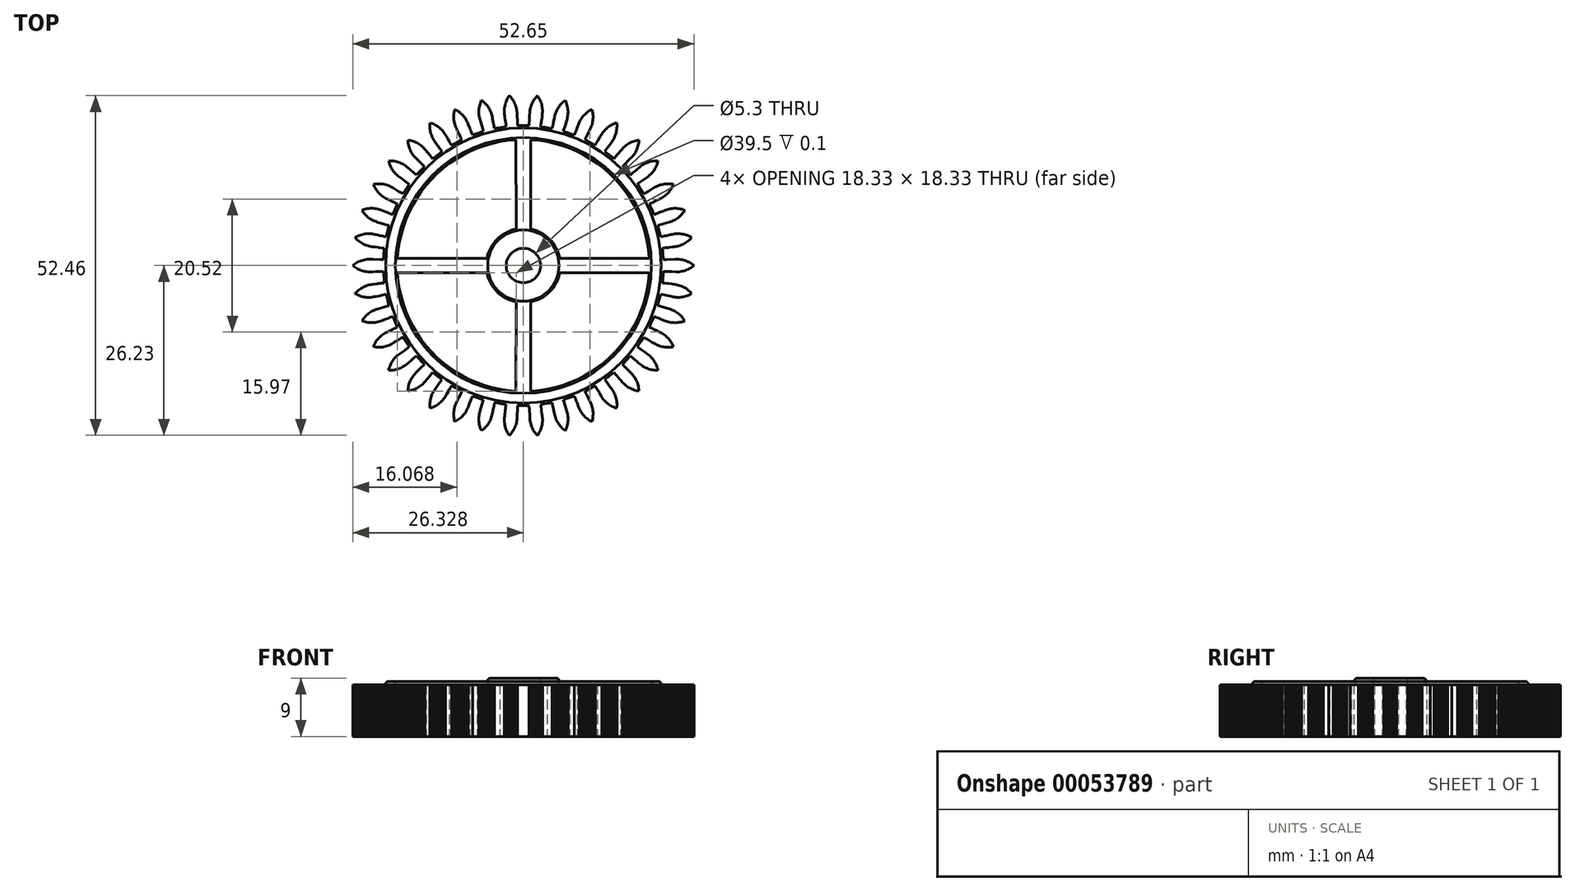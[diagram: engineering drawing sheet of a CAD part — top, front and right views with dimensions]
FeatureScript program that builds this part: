
annotation { "Feature Type Name" : "Feature", "Feature Type Description" : "" }
export const myFeature = defineFeature(function(context is Context, id is Id, definition is map)
    precondition{}
    {
        {
            var Q0;
            Q0=qCreatedBy(makeId("Top.planeOp"),FACE);
            var sketch = newSketch(context, id + "F0", { "sketchPlane" : qUnion([Q0])});
            skLineSegment(sketch, "E0", {"start": v(20.55, -0.9) * mm, "end": v(20.68, -0.9) * mm});
            skLineSegment(sketch, "E1", {"start": v(20.68, -0.9) * mm, "end": v(20.92, -0.9) * mm});
            skLineSegment(sketch, "E2", {"start": v(20.92, -0.9) * mm, "end": v(21.14, -0.92) * mm});
            skLineSegment(sketch, "E3", {"start": v(21.14, -0.92) * mm, "end": v(21.37, -0.93) * mm});
            skLineSegment(sketch, "E4", {"start": v(21.37, -0.93) * mm, "end": v(21.59, -0.94) * mm});
            skLineSegment(sketch, "E5", {"start": v(21.59, -0.94) * mm, "end": v(21.82, -0.95) * mm});
            skLineSegment(sketch, "E6", {"start": v(21.82, -0.95) * mm, "end": v(22.04, -0.96) * mm});
            skLineSegment(sketch, "E7", {"start": v(22.04, -0.96) * mm, "end": v(22.28, -0.96) * mm});
            skLineSegment(sketch, "E8", {"start": v(22.28, -0.96) * mm, "end": v(22.5, -0.97) * mm});
            skLineSegment(sketch, "E9", {"start": v(22.5, -0.97) * mm, "end": v(22.73, -0.97) * mm});
            skLineSegment(sketch, "E10", {"start": v(22.73, -0.97) * mm, "end": v(22.97, -0.96) * mm});
            skLineSegment(sketch, "E11", {"start": v(22.97, -0.96) * mm, "end": v(23.2, -0.94) * mm});
            skLineSegment(sketch, "E12", {"start": v(23.2, -0.94) * mm, "end": v(23.43, -0.9) * mm});
            skLineSegment(sketch, "E13", {"start": v(23.43, -0.9) * mm, "end": v(23.66, -0.84) * mm});
            skLineSegment(sketch, "E14", {"start": v(23.66, -0.84) * mm, "end": v(23.88, -0.78) * mm});
            skLineSegment(sketch, "E15", {"start": v(23.88, -0.78) * mm, "end": v(24.1, -0.7) * mm});
            skLineSegment(sketch, "E16", {"start": v(24.1, -0.7) * mm, "end": v(24.32, -0.6) * mm});
            skLineSegment(sketch, "E17", {"start": v(24.32, -0.6) * mm, "end": v(24.53, -0.5) * mm});
            skLineSegment(sketch, "E18", {"start": v(24.53, -0.5) * mm, "end": v(24.73, -0.39) * mm});
            skLineSegment(sketch, "E19", {"start": v(24.73, -0.39) * mm, "end": v(24.93, -0.26) * mm});
            skLineSegment(sketch, "E20", {"start": v(24.93, -0.26) * mm, "end": v(25.12, -0.13) * mm});
            skLineSegment(sketch, "E21", {"start": v(25.12, -0.13) * mm, "end": v(25.27, 0) * mm});
            skLineSegment(sketch, "E22", {"start": v(25.27, 0) * mm, "end": v(25.09, 0.15) * mm});
            skLineSegment(sketch, "E23", {"start": v(25.09, 0.15) * mm, "end": v(24.9, 0.28) * mm});
            skLineSegment(sketch, "E24", {"start": v(24.9, 0.28) * mm, "end": v(24.7, 0.4) * mm});
            skLineSegment(sketch, "E25", {"start": v(24.7, 0.4) * mm, "end": v(24.5, 0.52) * mm});
            skLineSegment(sketch, "E26", {"start": v(24.5, 0.52) * mm, "end": v(24.29, 0.62) * mm});
            skLineSegment(sketch, "E27", {"start": v(24.29, 0.62) * mm, "end": v(24.07, 0.71) * mm});
            skLineSegment(sketch, "E28", {"start": v(24.07, 0.71) * mm, "end": v(23.85, 0.79) * mm});
            skLineSegment(sketch, "E29", {"start": v(23.85, 0.79) * mm, "end": v(23.62, 0.85) * mm});
            skLineSegment(sketch, "E30", {"start": v(23.62, 0.85) * mm, "end": v(23.4, 0.9) * mm});
            skLineSegment(sketch, "E31", {"start": v(23.4, 0.9) * mm, "end": v(23.17, 0.94) * mm});
            skLineSegment(sketch, "E32", {"start": v(23.17, 0.94) * mm, "end": v(22.93, 0.96) * mm});
            skLineSegment(sketch, "E33", {"start": v(22.93, 0.96) * mm, "end": v(22.7, 0.98) * mm});
            skLineSegment(sketch, "E34", {"start": v(22.7, 0.98) * mm, "end": v(22.6, 0.98) * mm});
            skLineSegment(sketch, "E35", {"start": v(22.6, 0.98) * mm, "end": v(22.37, 0.97) * mm});
            skLineSegment(sketch, "E36", {"start": v(22.37, 0.97) * mm, "end": v(22.13, 0.96) * mm});
            skLineSegment(sketch, "E37", {"start": v(22.13, 0.96) * mm, "end": v(21.91, 0.95) * mm});
            skLineSegment(sketch, "E38", {"start": v(21.91, 0.95) * mm, "end": v(21.68, 0.94) * mm});
            skLineSegment(sketch, "E39", {"start": v(21.68, 0.94) * mm, "end": v(21.46, 0.93) * mm});
            skLineSegment(sketch, "E40", {"start": v(21.46, 0.93) * mm, "end": v(21.23, 0.92) * mm});
            skLineSegment(sketch, "E41", {"start": v(21.23, 0.92) * mm, "end": v(21, 0.91) * mm});
            skLineSegment(sketch, "E42", {"start": v(21, 0.91) * mm, "end": v(20.77, 0.9) * mm});
            skLineSegment(sketch, "E43", {"start": v(20.77, 0.9) * mm, "end": v(20.55, 0.9) * mm});
            skLineSegment(sketch, "E44", {"start": v(20.55, 0.9) * mm, "end": v(20.53, 1.13) * mm});
            skLineSegment(sketch, "E45", {"start": v(20.53, 1.13) * mm, "end": v(20.51, 1.36) * mm});
            skLineSegment(sketch, "E46", {"start": v(20.51, 1.36) * mm, "end": v(20.5, 1.6) * mm});
            skLineSegment(sketch, "E47", {"start": v(20.5, 1.6) * mm, "end": v(20.47, 1.83) * mm});
            skLineSegment(sketch, "E48", {"start": v(20.47, 1.83) * mm, "end": v(20.45, 2.06) * mm});
            skLineSegment(sketch, "E49", {"start": v(20.45, 2.06) * mm, "end": v(20.44, 2.3) * mm});
            skLineSegment(sketch, "E50", {"start": v(20.44, 2.3) * mm, "end": v(20.42, 2.53) * mm});
            skLineSegment(sketch, "E51", {"start": v(20.42, 2.53) * mm, "end": v(20.4, 2.67) * mm});
            skLineSegment(sketch, "E52", {"start": v(20.4, 2.67) * mm, "end": v(20.64, 2.7) * mm});
            skLineSegment(sketch, "E53", {"start": v(20.64, 2.7) * mm, "end": v(20.86, 2.73) * mm});
            skLineSegment(sketch, "E54", {"start": v(20.86, 2.73) * mm, "end": v(21.09, 2.76) * mm});
            skLineSegment(sketch, "E55", {"start": v(21.09, 2.76) * mm, "end": v(21.3, 2.79) * mm});
            skLineSegment(sketch, "E56", {"start": v(21.3, 2.79) * mm, "end": v(21.54, 2.82) * mm});
            skLineSegment(sketch, "E57", {"start": v(21.54, 2.82) * mm, "end": v(21.76, 2.84) * mm});
            skLineSegment(sketch, "E58", {"start": v(21.76, 2.84) * mm, "end": v(21.99, 2.87) * mm});
            skLineSegment(sketch, "E59", {"start": v(21.99, 2.87) * mm, "end": v(22.2, 2.9) * mm});
            skLineSegment(sketch, "E60", {"start": v(22.2, 2.9) * mm, "end": v(22.44, 2.93) * mm});
            skLineSegment(sketch, "E61", {"start": v(22.44, 2.93) * mm, "end": v(22.67, 2.98) * mm});
            skLineSegment(sketch, "E62", {"start": v(22.67, 2.98) * mm, "end": v(22.9, 3.03) * mm});
            skLineSegment(sketch, "E63", {"start": v(22.9, 3.03) * mm, "end": v(23.12, 3.1) * mm});
            skLineSegment(sketch, "E64", {"start": v(23.12, 3.1) * mm, "end": v(23.34, 3.18) * mm});
            skLineSegment(sketch, "E65", {"start": v(23.34, 3.18) * mm, "end": v(23.55, 3.28) * mm});
            skLineSegment(sketch, "E66", {"start": v(23.55, 3.28) * mm, "end": v(23.76, 3.38) * mm});
            skLineSegment(sketch, "E67", {"start": v(23.76, 3.38) * mm, "end": v(23.96, 3.5) * mm});
            skLineSegment(sketch, "E68", {"start": v(23.96, 3.5) * mm, "end": v(24.15, 3.63) * mm});
            skLineSegment(sketch, "E69", {"start": v(24.15, 3.63) * mm, "end": v(24.34, 3.77) * mm});
            skLineSegment(sketch, "E70", {"start": v(24.34, 3.77) * mm, "end": v(24.52, 3.93) * mm});
            skLineSegment(sketch, "E71", {"start": v(24.52, 3.93) * mm, "end": v(24.69, 4.09) * mm});
            skLineSegment(sketch, "E72", {"start": v(24.69, 4.09) * mm, "end": v(24.85, 4.26) * mm});
            skLineSegment(sketch, "E73", {"start": v(24.85, 4.26) * mm, "end": v(24.91, 4.33) * mm});
            skLineSegment(sketch, "E74", {"start": v(24.91, 4.33) * mm, "end": v(24.7, 4.45) * mm});
            skLineSegment(sketch, "E75", {"start": v(24.7, 4.45) * mm, "end": v(24.5, 4.55) * mm});
            skLineSegment(sketch, "E76", {"start": v(24.5, 4.55) * mm, "end": v(24.28, 4.64) * mm});
            skLineSegment(sketch, "E77", {"start": v(24.28, 4.64) * mm, "end": v(24.06, 4.72) * mm});
            skLineSegment(sketch, "E78", {"start": v(24.06, 4.72) * mm, "end": v(23.84, 4.78) * mm});
            skLineSegment(sketch, "E79", {"start": v(23.84, 4.78) * mm, "end": v(23.61, 4.84) * mm});
            skLineSegment(sketch, "E80", {"start": v(23.61, 4.84) * mm, "end": v(23.38, 4.88) * mm});
            skLineSegment(sketch, "E81", {"start": v(23.38, 4.88) * mm, "end": v(23.15, 4.9) * mm});
            skLineSegment(sketch, "E82", {"start": v(23.15, 4.9) * mm, "end": v(22.91, 4.92) * mm});
            skLineSegment(sketch, "E83", {"start": v(22.91, 4.92) * mm, "end": v(22.81, 4.92) * mm});
            skLineSegment(sketch, "E84", {"start": v(22.81, 4.92) * mm, "end": v(22.58, 4.9) * mm});
            skLineSegment(sketch, "E85", {"start": v(22.58, 4.9) * mm, "end": v(22.35, 4.89) * mm});
            skLineSegment(sketch, "E86", {"start": v(22.35, 4.89) * mm, "end": v(22.12, 4.86) * mm});
            skLineSegment(sketch, "E87", {"start": v(22.12, 4.86) * mm, "end": v(21.89, 4.81) * mm});
            skLineSegment(sketch, "E88", {"start": v(21.89, 4.81) * mm, "end": v(21.66, 4.76) * mm});
            skLineSegment(sketch, "E89", {"start": v(21.66, 4.76) * mm, "end": v(21.44, 4.72) * mm});
            skLineSegment(sketch, "E90", {"start": v(21.44, 4.72) * mm, "end": v(21.22, 4.67) * mm});
            skLineSegment(sketch, "E91", {"start": v(21.22, 4.67) * mm, "end": v(21, 4.62) * mm});
            skLineSegment(sketch, "E92", {"start": v(21, 4.62) * mm, "end": v(20.77, 4.58) * mm});
            skLineSegment(sketch, "E93", {"start": v(20.77, 4.58) * mm, "end": v(20.55, 4.53) * mm});
            skLineSegment(sketch, "E94", {"start": v(20.55, 4.53) * mm, "end": v(20.33, 4.48) * mm});
            skLineSegment(sketch, "E95", {"start": v(20.33, 4.48) * mm, "end": v(20.1, 4.44) * mm});
            skLineSegment(sketch, "E96", {"start": v(20.1, 4.44) * mm, "end": v(20.05, 4.66) * mm});
            skLineSegment(sketch, "E97", {"start": v(20.05, 4.66) * mm, "end": v(20, 4.9) * mm});
            skLineSegment(sketch, "E98", {"start": v(20, 4.9) * mm, "end": v(19.94, 5.12) * mm});
            skLineSegment(sketch, "E99", {"start": v(19.94, 5.12) * mm, "end": v(19.88, 5.34) * mm});
            skLineSegment(sketch, "E100", {"start": v(19.88, 5.34) * mm, "end": v(19.82, 5.57) * mm});
            skLineSegment(sketch, "E101", {"start": v(19.82, 5.57) * mm, "end": v(19.76, 5.8) * mm});
            skLineSegment(sketch, "E102", {"start": v(19.76, 5.8) * mm, "end": v(19.7, 6.03) * mm});
            skLineSegment(sketch, "E103", {"start": v(19.7, 6.03) * mm, "end": v(19.67, 6.17) * mm});
            skLineSegment(sketch, "E104", {"start": v(19.67, 6.17) * mm, "end": v(19.9, 6.24) * mm});
            skLineSegment(sketch, "E105", {"start": v(19.9, 6.24) * mm, "end": v(20.1, 6.3) * mm});
            skLineSegment(sketch, "E106", {"start": v(20.1, 6.3) * mm, "end": v(20.33, 6.37) * mm});
            skLineSegment(sketch, "E107", {"start": v(20.33, 6.37) * mm, "end": v(20.54, 6.43) * mm});
            skLineSegment(sketch, "E108", {"start": v(20.54, 6.43) * mm, "end": v(20.77, 6.5) * mm});
            skLineSegment(sketch, "E109", {"start": v(20.77, 6.5) * mm, "end": v(20.98, 6.56) * mm});
            skLineSegment(sketch, "E110", {"start": v(20.98, 6.56) * mm, "end": v(21.2, 6.63) * mm});
            skLineSegment(sketch, "E111", {"start": v(21.2, 6.63) * mm, "end": v(21.41, 6.69) * mm});
            skLineSegment(sketch, "E112", {"start": v(21.41, 6.69) * mm, "end": v(21.63, 6.76) * mm});
            skLineSegment(sketch, "E113", {"start": v(21.63, 6.76) * mm, "end": v(21.85, 6.84) * mm});
            skLineSegment(sketch, "E114", {"start": v(21.85, 6.84) * mm, "end": v(22.07, 6.93) * mm});
            skLineSegment(sketch, "E115", {"start": v(22.07, 6.93) * mm, "end": v(22.28, 7.03) * mm});
            skLineSegment(sketch, "E116", {"start": v(22.28, 7.03) * mm, "end": v(22.48, 7.15) * mm});
            skLineSegment(sketch, "E117", {"start": v(22.48, 7.15) * mm, "end": v(22.68, 7.28) * mm});
            skLineSegment(sketch, "E118", {"start": v(22.68, 7.28) * mm, "end": v(22.86, 7.42) * mm});
            skLineSegment(sketch, "E119", {"start": v(22.86, 7.42) * mm, "end": v(23.04, 7.57) * mm});
            skLineSegment(sketch, "E120", {"start": v(23.04, 7.57) * mm, "end": v(23.21, 7.73) * mm});
            skLineSegment(sketch, "E121", {"start": v(23.21, 7.73) * mm, "end": v(23.37, 7.9) * mm});
            skLineSegment(sketch, "E122", {"start": v(23.37, 7.9) * mm, "end": v(23.52, 8.08) * mm});
            skLineSegment(sketch, "E123", {"start": v(23.52, 8.08) * mm, "end": v(23.66, 8.27) * mm});
            skLineSegment(sketch, "E124", {"start": v(23.66, 8.27) * mm, "end": v(23.8, 8.46) * mm});
            skLineSegment(sketch, "E125", {"start": v(23.8, 8.46) * mm, "end": v(23.85, 8.55) * mm});
            skLineSegment(sketch, "E126", {"start": v(23.85, 8.55) * mm, "end": v(23.63, 8.63) * mm});
            skLineSegment(sketch, "E127", {"start": v(23.63, 8.63) * mm, "end": v(23.4, 8.7) * mm});
            skLineSegment(sketch, "E128", {"start": v(23.4, 8.7) * mm, "end": v(23.17, 8.75) * mm});
            skLineSegment(sketch, "E129", {"start": v(23.17, 8.75) * mm, "end": v(22.94, 8.79) * mm});
            skLineSegment(sketch, "E130", {"start": v(22.94, 8.79) * mm, "end": v(22.71, 8.82) * mm});
            skLineSegment(sketch, "E131", {"start": v(22.71, 8.82) * mm, "end": v(22.48, 8.83) * mm});
            skLineSegment(sketch, "E132", {"start": v(22.48, 8.83) * mm, "end": v(22.38, 8.83) * mm});
            skLineSegment(sketch, "E133", {"start": v(22.38, 8.83) * mm, "end": v(22.14, 8.83) * mm});
            skLineSegment(sketch, "E134", {"start": v(22.14, 8.83) * mm, "end": v(21.91, 8.8) * mm});
            skLineSegment(sketch, "E135", {"start": v(21.91, 8.8) * mm, "end": v(21.68, 8.78) * mm});
            skLineSegment(sketch, "E136", {"start": v(21.68, 8.78) * mm, "end": v(21.45, 8.73) * mm});
            skLineSegment(sketch, "E137", {"start": v(21.45, 8.73) * mm, "end": v(21.22, 8.67) * mm});
            skLineSegment(sketch, "E138", {"start": v(21.22, 8.67) * mm, "end": v(21, 8.6) * mm});
            skLineSegment(sketch, "E139", {"start": v(21, 8.6) * mm, "end": v(20.79, 8.52) * mm});
            skLineSegment(sketch, "E140", {"start": v(20.79, 8.52) * mm, "end": v(20.57, 8.44) * mm});
            skLineSegment(sketch, "E141", {"start": v(20.57, 8.44) * mm, "end": v(20.36, 8.36) * mm});
            skLineSegment(sketch, "E142", {"start": v(20.36, 8.36) * mm, "end": v(20.14, 8.27) * mm});
            skLineSegment(sketch, "E143", {"start": v(20.14, 8.27) * mm, "end": v(19.94, 8.2) * mm});
            skLineSegment(sketch, "E144", {"start": v(19.94, 8.2) * mm, "end": v(19.72, 8.1) * mm});
            skLineSegment(sketch, "E145", {"start": v(19.72, 8.1) * mm, "end": v(19.51, 8.02) * mm});
            skLineSegment(sketch, "E146", {"start": v(19.51, 8.02) * mm, "end": v(19.3, 7.94) * mm});
            skLineSegment(sketch, "E147", {"start": v(19.3, 7.94) * mm, "end": v(19.1, 7.86) * mm});
            skLineSegment(sketch, "E148", {"start": v(19.1, 7.86) * mm, "end": v(19, 8.07) * mm});
            skLineSegment(sketch, "E149", {"start": v(19, 8.07) * mm, "end": v(18.9, 8.29) * mm});
            skLineSegment(sketch, "E150", {"start": v(18.9, 8.29) * mm, "end": v(18.8, 8.5) * mm});
            skLineSegment(sketch, "E151", {"start": v(18.8, 8.5) * mm, "end": v(18.71, 8.72) * mm});
            skLineSegment(sketch, "E152", {"start": v(18.71, 8.72) * mm, "end": v(18.62, 8.93) * mm});
            skLineSegment(sketch, "E153", {"start": v(18.62, 8.93) * mm, "end": v(18.53, 9.15) * mm});
            skLineSegment(sketch, "E154", {"start": v(18.53, 9.15) * mm, "end": v(18.43, 9.36) * mm});
            skLineSegment(sketch, "E155", {"start": v(18.43, 9.36) * mm, "end": v(18.37, 9.5) * mm});
            skLineSegment(sketch, "E156", {"start": v(18.37, 9.5) * mm, "end": v(18.58, 9.6) * mm});
            skLineSegment(sketch, "E157", {"start": v(18.58, 9.6) * mm, "end": v(18.78, 9.7) * mm});
            skLineSegment(sketch, "E158", {"start": v(18.78, 9.7) * mm, "end": v(19, 9.8) * mm});
            skLineSegment(sketch, "E159", {"start": v(19, 9.8) * mm, "end": v(19.19, 9.9) * mm});
            skLineSegment(sketch, "E160", {"start": v(19.19, 9.9) * mm, "end": v(19.4, 10) * mm});
            skLineSegment(sketch, "E161", {"start": v(19.4, 10) * mm, "end": v(19.6, 10.1) * mm});
            skLineSegment(sketch, "E162", {"start": v(19.6, 10.1) * mm, "end": v(19.8, 10.2) * mm});
            skLineSegment(sketch, "E163", {"start": v(19.8, 10.2) * mm, "end": v(20, 10.3) * mm});
            skLineSegment(sketch, "E164", {"start": v(20, 10.3) * mm, "end": v(20.21, 10.4) * mm});
            skLineSegment(sketch, "E165", {"start": v(20.21, 10.4) * mm, "end": v(20.42, 10.52) * mm});
            skLineSegment(sketch, "E166", {"start": v(20.42, 10.52) * mm, "end": v(20.61, 10.64) * mm});
            skLineSegment(sketch, "E167", {"start": v(20.61, 10.64) * mm, "end": v(20.8, 10.78) * mm});
            skLineSegment(sketch, "E168", {"start": v(20.8, 10.78) * mm, "end": v(20.98, 10.93) * mm});
            skLineSegment(sketch, "E169", {"start": v(20.98, 10.93) * mm, "end": v(21.15, 11.09) * mm});
            skLineSegment(sketch, "E170", {"start": v(21.15, 11.09) * mm, "end": v(21.32, 11.26) * mm});
            skLineSegment(sketch, "E171", {"start": v(21.32, 11.26) * mm, "end": v(21.47, 11.43) * mm});
            skLineSegment(sketch, "E172", {"start": v(21.47, 11.43) * mm, "end": v(21.6, 11.62) * mm});
            skLineSegment(sketch, "E173", {"start": v(21.6, 11.62) * mm, "end": v(21.74, 11.81) * mm});
            skLineSegment(sketch, "E174", {"start": v(21.74, 11.81) * mm, "end": v(21.86, 12.02) * mm});
            skLineSegment(sketch, "E175", {"start": v(21.86, 12.02) * mm, "end": v(21.97, 12.22) * mm});
            skLineSegment(sketch, "E176", {"start": v(21.97, 12.22) * mm, "end": v(22.06, 12.44) * mm});
            skLineSegment(sketch, "E177", {"start": v(22.06, 12.44) * mm, "end": v(22.1, 12.53) * mm});
            skLineSegment(sketch, "E178", {"start": v(22.1, 12.53) * mm, "end": v(21.87, 12.57) * mm});
            skLineSegment(sketch, "E179", {"start": v(21.87, 12.57) * mm, "end": v(21.64, 12.6) * mm});
            skLineSegment(sketch, "E180", {"start": v(21.64, 12.6) * mm, "end": v(21.4, 12.62) * mm});
            skLineSegment(sketch, "E181", {"start": v(21.4, 12.62) * mm, "end": v(21.2, 12.62) * mm});
            skLineSegment(sketch, "E182", {"start": v(21.2, 12.62) * mm, "end": v(20.97, 12.6) * mm});
            skLineSegment(sketch, "E183", {"start": v(20.97, 12.6) * mm, "end": v(20.74, 12.59) * mm});
            skLineSegment(sketch, "E184", {"start": v(20.74, 12.59) * mm, "end": v(20.5, 12.55) * mm});
            skLineSegment(sketch, "E185", {"start": v(20.5, 12.55) * mm, "end": v(20.28, 12.5) * mm});
            skLineSegment(sketch, "E186", {"start": v(20.28, 12.5) * mm, "end": v(20.05, 12.44) * mm});
            skLineSegment(sketch, "E187", {"start": v(20.05, 12.44) * mm, "end": v(19.83, 12.37) * mm});
            skLineSegment(sketch, "E188", {"start": v(19.83, 12.37) * mm, "end": v(19.61, 12.28) * mm});
            skLineSegment(sketch, "E189", {"start": v(19.61, 12.28) * mm, "end": v(19.4, 12.18) * mm});
            skLineSegment(sketch, "E190", {"start": v(19.4, 12.18) * mm, "end": v(19.2, 12.07) * mm});
            skLineSegment(sketch, "E191", {"start": v(19.2, 12.07) * mm, "end": v(19, 11.95) * mm});
            skLineSegment(sketch, "E192", {"start": v(19, 11.95) * mm, "end": v(18.8, 11.83) * mm});
            skLineSegment(sketch, "E193", {"start": v(18.8, 11.83) * mm, "end": v(18.6, 11.71) * mm});
            skLineSegment(sketch, "E194", {"start": v(18.6, 11.71) * mm, "end": v(18.42, 11.6) * mm});
            skLineSegment(sketch, "E195", {"start": v(18.42, 11.6) * mm, "end": v(18.21, 11.48) * mm});
            skLineSegment(sketch, "E196", {"start": v(18.21, 11.48) * mm, "end": v(18.02, 11.37) * mm});
            skLineSegment(sketch, "E197", {"start": v(18.02, 11.37) * mm, "end": v(17.82, 11.25) * mm});
            skLineSegment(sketch, "E198", {"start": v(17.82, 11.25) * mm, "end": v(17.63, 11.13) * mm});
            skLineSegment(sketch, "E199", {"start": v(17.63, 11.13) * mm, "end": v(17.52, 11.07) * mm});
            skLineSegment(sketch, "E200", {"start": v(17.52, 11.07) * mm, "end": v(17.4, 11.26) * mm});
            skLineSegment(sketch, "E201", {"start": v(17.4, 11.26) * mm, "end": v(17.27, 11.46) * mm});
            skLineSegment(sketch, "E202", {"start": v(17.27, 11.46) * mm, "end": v(17.14, 11.66) * mm});
            skLineSegment(sketch, "E203", {"start": v(17.14, 11.66) * mm, "end": v(17.01, 11.85) * mm});
            skLineSegment(sketch, "E204", {"start": v(17.01, 11.85) * mm, "end": v(16.88, 12.05) * mm});
            skLineSegment(sketch, "E205", {"start": v(16.88, 12.05) * mm, "end": v(16.75, 12.24) * mm});
            skLineSegment(sketch, "E206", {"start": v(16.75, 12.24) * mm, "end": v(16.63, 12.44) * mm});
            skLineSegment(sketch, "E207", {"start": v(16.63, 12.44) * mm, "end": v(16.54, 12.56) * mm});
            skLineSegment(sketch, "E208", {"start": v(16.54, 12.56) * mm, "end": v(16.74, 12.7) * mm});
            skLineSegment(sketch, "E209", {"start": v(16.74, 12.7) * mm, "end": v(16.92, 12.83) * mm});
            skLineSegment(sketch, "E210", {"start": v(16.92, 12.83) * mm, "end": v(17.1, 12.96) * mm});
            skLineSegment(sketch, "E211", {"start": v(17.1, 12.96) * mm, "end": v(17.29, 13.1) * mm});
            skLineSegment(sketch, "E212", {"start": v(17.29, 13.1) * mm, "end": v(17.48, 13.23) * mm});
            skLineSegment(sketch, "E213", {"start": v(17.48, 13.23) * mm, "end": v(17.66, 13.36) * mm});
            skLineSegment(sketch, "E214", {"start": v(17.66, 13.36) * mm, "end": v(17.85, 13.5) * mm});
            skLineSegment(sketch, "E215", {"start": v(17.85, 13.5) * mm, "end": v(18.03, 13.62) * mm});
            skLineSegment(sketch, "E216", {"start": v(18.03, 13.62) * mm, "end": v(18.21, 13.76) * mm});
            skLineSegment(sketch, "E217", {"start": v(18.21, 13.76) * mm, "end": v(18.4, 13.9) * mm});
            skLineSegment(sketch, "E218", {"start": v(18.4, 13.9) * mm, "end": v(18.57, 14.06) * mm});
            skLineSegment(sketch, "E219", {"start": v(18.57, 14.06) * mm, "end": v(18.73, 14.23) * mm});
            skLineSegment(sketch, "E220", {"start": v(18.73, 14.23) * mm, "end": v(18.88, 14.4) * mm});
            skLineSegment(sketch, "E221", {"start": v(18.88, 14.4) * mm, "end": v(19.03, 14.6) * mm});
            skLineSegment(sketch, "E222", {"start": v(19.03, 14.6) * mm, "end": v(19.16, 14.78) * mm});
            skLineSegment(sketch, "E223", {"start": v(19.16, 14.78) * mm, "end": v(19.28, 14.98) * mm});
            skLineSegment(sketch, "E224", {"start": v(19.28, 14.98) * mm, "end": v(19.39, 15.2) * mm});
            skLineSegment(sketch, "E225", {"start": v(19.39, 15.2) * mm, "end": v(19.49, 15.4) * mm});
            skLineSegment(sketch, "E226", {"start": v(19.49, 15.4) * mm, "end": v(19.57, 15.62) * mm});
            skLineSegment(sketch, "E227", {"start": v(19.57, 15.62) * mm, "end": v(19.64, 15.85) * mm});
            skLineSegment(sketch, "E228", {"start": v(19.64, 15.85) * mm, "end": v(19.7, 16.07) * mm});
            skLineSegment(sketch, "E229", {"start": v(19.7, 16.07) * mm, "end": v(19.72, 16.17) * mm});
            skLineSegment(sketch, "E230", {"start": v(19.72, 16.17) * mm, "end": v(19.52, 16.17) * mm});
            skLineSegment(sketch, "E231", {"start": v(19.52, 16.17) * mm, "end": v(19.29, 16.16) * mm});
            skLineSegment(sketch, "E232", {"start": v(19.29, 16.16) * mm, "end": v(19.05, 16.14) * mm});
            skLineSegment(sketch, "E233", {"start": v(19.05, 16.14) * mm, "end": v(18.82, 16.11) * mm});
            skLineSegment(sketch, "E234", {"start": v(18.82, 16.11) * mm, "end": v(18.6, 16.06) * mm});
            skLineSegment(sketch, "E235", {"start": v(18.6, 16.06) * mm, "end": v(18.37, 16) * mm});
            skLineSegment(sketch, "E236", {"start": v(18.37, 16) * mm, "end": v(18.15, 15.93) * mm});
            skLineSegment(sketch, "E237", {"start": v(18.15, 15.93) * mm, "end": v(17.93, 15.84) * mm});
            skLineSegment(sketch, "E238", {"start": v(17.93, 15.84) * mm, "end": v(17.72, 15.74) * mm});
            skLineSegment(sketch, "E239", {"start": v(17.72, 15.74) * mm, "end": v(17.5, 15.63) * mm});
            skLineSegment(sketch, "E240", {"start": v(17.5, 15.63) * mm, "end": v(17.31, 15.5) * mm});
            skLineSegment(sketch, "E241", {"start": v(17.31, 15.5) * mm, "end": v(17.12, 15.38) * mm});
            skLineSegment(sketch, "E242", {"start": v(17.12, 15.38) * mm, "end": v(16.93, 15.23) * mm});
            skLineSegment(sketch, "E243", {"start": v(16.93, 15.23) * mm, "end": v(16.76, 15.08) * mm});
            skLineSegment(sketch, "E244", {"start": v(16.76, 15.08) * mm, "end": v(16.59, 14.94) * mm});
            skLineSegment(sketch, "E245", {"start": v(16.59, 14.94) * mm, "end": v(16.4, 14.79) * mm});
            skLineSegment(sketch, "E246", {"start": v(16.4, 14.79) * mm, "end": v(16.24, 14.65) * mm});
            skLineSegment(sketch, "E247", {"start": v(16.24, 14.65) * mm, "end": v(16.06, 14.5) * mm});
            skLineSegment(sketch, "E248", {"start": v(16.06, 14.5) * mm, "end": v(15.9, 14.35) * mm});
            skLineSegment(sketch, "E249", {"start": v(15.9, 14.35) * mm, "end": v(15.71, 14.2) * mm});
            skLineSegment(sketch, "E250", {"start": v(15.71, 14.2) * mm, "end": v(15.55, 14.06) * mm});
            skLineSegment(sketch, "E251", {"start": v(15.55, 14.06) * mm, "end": v(15.45, 13.97) * mm});
            skLineSegment(sketch, "E252", {"start": v(15.45, 13.97) * mm, "end": v(15.29, 14.15) * mm});
            skLineSegment(sketch, "E253", {"start": v(15.29, 14.15) * mm, "end": v(15.13, 14.32) * mm});
            skLineSegment(sketch, "E254", {"start": v(15.13, 14.32) * mm, "end": v(14.97, 14.5) * mm});
            skLineSegment(sketch, "E255", {"start": v(14.97, 14.5) * mm, "end": v(14.81, 14.66) * mm});
            skLineSegment(sketch, "E256", {"start": v(14.81, 14.66) * mm, "end": v(14.65, 14.83) * mm});
            skLineSegment(sketch, "E257", {"start": v(14.65, 14.83) * mm, "end": v(14.5, 15) * mm});
            skLineSegment(sketch, "E258", {"start": v(14.5, 15) * mm, "end": v(14.34, 15.18) * mm});
            skLineSegment(sketch, "E259", {"start": v(14.34, 15.18) * mm, "end": v(14.24, 15.29) * mm});
            skLineSegment(sketch, "E260", {"start": v(14.24, 15.29) * mm, "end": v(14.4, 15.45) * mm});
            skLineSegment(sketch, "E261", {"start": v(14.4, 15.45) * mm, "end": v(14.56, 15.61) * mm});
            skLineSegment(sketch, "E262", {"start": v(14.56, 15.61) * mm, "end": v(14.72, 15.78) * mm});
            skLineSegment(sketch, "E263", {"start": v(14.72, 15.78) * mm, "end": v(14.88, 15.93) * mm});
            skLineSegment(sketch, "E264", {"start": v(14.88, 15.93) * mm, "end": v(15.05, 16.1) * mm});
            skLineSegment(sketch, "E265", {"start": v(15.05, 16.1) * mm, "end": v(15.2, 16.25) * mm});
            skLineSegment(sketch, "E266", {"start": v(15.2, 16.25) * mm, "end": v(15.37, 16.42) * mm});
            skLineSegment(sketch, "E267", {"start": v(15.37, 16.42) * mm, "end": v(15.52, 16.57) * mm});
            skLineSegment(sketch, "E268", {"start": v(15.52, 16.57) * mm, "end": v(15.68, 16.74) * mm});
            skLineSegment(sketch, "E269", {"start": v(15.68, 16.74) * mm, "end": v(15.84, 16.92) * mm});
            skLineSegment(sketch, "E270", {"start": v(15.84, 16.92) * mm, "end": v(15.98, 17.1) * mm});
            skLineSegment(sketch, "E271", {"start": v(15.98, 17.1) * mm, "end": v(16.12, 17.3) * mm});
            skLineSegment(sketch, "E272", {"start": v(16.12, 17.3) * mm, "end": v(16.24, 17.5) * mm});
            skLineSegment(sketch, "E273", {"start": v(16.24, 17.5) * mm, "end": v(16.35, 17.7) * mm});
            skLineSegment(sketch, "E274", {"start": v(16.35, 17.7) * mm, "end": v(16.45, 17.9) * mm});
            skLineSegment(sketch, "E275", {"start": v(16.45, 17.9) * mm, "end": v(16.53, 18.13) * mm});
            skLineSegment(sketch, "E276", {"start": v(16.53, 18.13) * mm, "end": v(16.6, 18.35) * mm});
            skLineSegment(sketch, "E277", {"start": v(16.6, 18.35) * mm, "end": v(16.67, 18.57) * mm});
            skLineSegment(sketch, "E278", {"start": v(16.67, 18.57) * mm, "end": v(16.72, 18.8) * mm});
            skLineSegment(sketch, "E279", {"start": v(16.72, 18.8) * mm, "end": v(16.75, 19.03) * mm});
            skLineSegment(sketch, "E280", {"start": v(16.75, 19.03) * mm, "end": v(16.77, 19.27) * mm});
            skLineSegment(sketch, "E281", {"start": v(16.77, 19.27) * mm, "end": v(16.78, 19.37) * mm});
            skLineSegment(sketch, "E282", {"start": v(16.78, 19.37) * mm, "end": v(16.55, 19.33) * mm});
            skLineSegment(sketch, "E283", {"start": v(16.55, 19.33) * mm, "end": v(16.32, 19.28) * mm});
            skLineSegment(sketch, "E284", {"start": v(16.32, 19.28) * mm, "end": v(16.1, 19.22) * mm});
            skLineSegment(sketch, "E285", {"start": v(16.1, 19.22) * mm, "end": v(15.87, 19.15) * mm});
            skLineSegment(sketch, "E286", {"start": v(15.87, 19.15) * mm, "end": v(15.65, 19.06) * mm});
            skLineSegment(sketch, "E287", {"start": v(15.65, 19.06) * mm, "end": v(15.44, 18.97) * mm});
            skLineSegment(sketch, "E288", {"start": v(15.44, 18.97) * mm, "end": v(15.23, 18.85) * mm});
            skLineSegment(sketch, "E289", {"start": v(15.23, 18.85) * mm, "end": v(15.03, 18.73) * mm});
            skLineSegment(sketch, "E290", {"start": v(15.03, 18.73) * mm, "end": v(14.84, 18.6) * mm});
            skLineSegment(sketch, "E291", {"start": v(14.84, 18.6) * mm, "end": v(14.66, 18.45) * mm});
            skLineSegment(sketch, "E292", {"start": v(14.66, 18.45) * mm, "end": v(14.48, 18.3) * mm});
            skLineSegment(sketch, "E293", {"start": v(14.48, 18.3) * mm, "end": v(14.32, 18.13) * mm});
            skLineSegment(sketch, "E294", {"start": v(14.32, 18.13) * mm, "end": v(14.16, 17.96) * mm});
            skLineSegment(sketch, "E295", {"start": v(14.16, 17.96) * mm, "end": v(14.01, 17.79) * mm});
            skLineSegment(sketch, "E296", {"start": v(14.01, 17.79) * mm, "end": v(13.86, 17.6) * mm});
            skLineSegment(sketch, "E297", {"start": v(13.86, 17.6) * mm, "end": v(13.72, 17.44) * mm});
            skLineSegment(sketch, "E298", {"start": v(13.72, 17.44) * mm, "end": v(13.57, 17.26) * mm});
            skLineSegment(sketch, "E299", {"start": v(13.57, 17.26) * mm, "end": v(13.43, 17.1) * mm});
            skLineSegment(sketch, "E300", {"start": v(13.43, 17.1) * mm, "end": v(13.27, 16.92) * mm});
            skLineSegment(sketch, "E301", {"start": v(13.27, 16.92) * mm, "end": v(13.13, 16.75) * mm});
            skLineSegment(sketch, "E302", {"start": v(13.13, 16.75) * mm, "end": v(12.98, 16.57) * mm});
            skLineSegment(sketch, "E303", {"start": v(12.98, 16.57) * mm, "end": v(12.92, 16.5) * mm});
            skLineSegment(sketch, "E304", {"start": v(12.92, 16.5) * mm, "end": v(12.74, 16.64) * mm});
            skLineSegment(sketch, "E305", {"start": v(12.74, 16.64) * mm, "end": v(12.55, 16.79) * mm});
            skLineSegment(sketch, "E306", {"start": v(12.55, 16.79) * mm, "end": v(12.37, 16.93) * mm});
            skLineSegment(sketch, "E307", {"start": v(12.37, 16.93) * mm, "end": v(12.18, 17.07) * mm});
            skLineSegment(sketch, "E308", {"start": v(12.18, 17.07) * mm, "end": v(12, 17.22) * mm});
            skLineSegment(sketch, "E309", {"start": v(12, 17.22) * mm, "end": v(11.81, 17.36) * mm});
            skLineSegment(sketch, "E310", {"start": v(11.81, 17.36) * mm, "end": v(11.63, 17.5) * mm});
            skLineSegment(sketch, "E311", {"start": v(11.63, 17.5) * mm, "end": v(11.51, 17.6) * mm});
            skLineSegment(sketch, "E312", {"start": v(11.51, 17.6) * mm, "end": v(11.65, 17.79) * mm});
            skLineSegment(sketch, "E313", {"start": v(11.65, 17.79) * mm, "end": v(11.78, 17.97) * mm});
            skLineSegment(sketch, "E314", {"start": v(11.78, 17.97) * mm, "end": v(11.91, 18.16) * mm});
            skLineSegment(sketch, "E315", {"start": v(11.91, 18.16) * mm, "end": v(12.04, 18.34) * mm});
            skLineSegment(sketch, "E316", {"start": v(12.04, 18.34) * mm, "end": v(12.18, 18.53) * mm});
            skLineSegment(sketch, "E317", {"start": v(12.18, 18.53) * mm, "end": v(12.3, 18.7) * mm});
            skLineSegment(sketch, "E318", {"start": v(12.3, 18.7) * mm, "end": v(12.44, 18.9) * mm});
            skLineSegment(sketch, "E319", {"start": v(12.44, 18.9) * mm, "end": v(12.57, 19.08) * mm});
            skLineSegment(sketch, "E320", {"start": v(12.57, 19.08) * mm, "end": v(12.7, 19.27) * mm});
            skLineSegment(sketch, "E321", {"start": v(12.7, 19.27) * mm, "end": v(12.82, 19.46) * mm});
            skLineSegment(sketch, "E322", {"start": v(12.82, 19.46) * mm, "end": v(12.94, 19.67) * mm});
            skLineSegment(sketch, "E323", {"start": v(12.94, 19.67) * mm, "end": v(13.04, 19.88) * mm});
            skLineSegment(sketch, "E324", {"start": v(13.04, 19.88) * mm, "end": v(13.12, 20.1) * mm});
            skLineSegment(sketch, "E325", {"start": v(13.12, 20.1) * mm, "end": v(13.2, 20.32) * mm});
            skLineSegment(sketch, "E326", {"start": v(13.2, 20.32) * mm, "end": v(13.26, 20.54) * mm});
            skLineSegment(sketch, "E327", {"start": v(13.26, 20.54) * mm, "end": v(13.31, 20.77) * mm});
            skLineSegment(sketch, "E328", {"start": v(13.31, 20.77) * mm, "end": v(13.35, 21) * mm});
            skLineSegment(sketch, "E329", {"start": v(13.35, 21) * mm, "end": v(13.37, 21.24) * mm});
            skLineSegment(sketch, "E330", {"start": v(13.37, 21.24) * mm, "end": v(13.38, 21.47) * mm});
            skLineSegment(sketch, "E331", {"start": v(13.38, 21.47) * mm, "end": v(13.37, 21.7) * mm});
            skLineSegment(sketch, "E332", {"start": v(13.37, 21.7) * mm, "end": v(13.36, 21.94) * mm});
            skLineSegment(sketch, "E333", {"start": v(13.36, 21.94) * mm, "end": v(13.35, 22.04) * mm});
            skLineSegment(sketch, "E334", {"start": v(13.35, 22.04) * mm, "end": v(13.12, 21.96) * mm});
            skLineSegment(sketch, "E335", {"start": v(13.12, 21.96) * mm, "end": v(12.9, 21.88) * mm});
            skLineSegment(sketch, "E336", {"start": v(12.9, 21.88) * mm, "end": v(12.7, 21.78) * mm});
            skLineSegment(sketch, "E337", {"start": v(12.7, 21.78) * mm, "end": v(12.49, 21.67) * mm});
            skLineSegment(sketch, "E338", {"start": v(12.49, 21.67) * mm, "end": v(12.29, 21.55) * mm});
            skLineSegment(sketch, "E339", {"start": v(12.29, 21.55) * mm, "end": v(12.1, 21.42) * mm});
            skLineSegment(sketch, "E340", {"start": v(12.1, 21.42) * mm, "end": v(11.9, 21.28) * mm});
            skLineSegment(sketch, "E341", {"start": v(11.9, 21.28) * mm, "end": v(11.73, 21.12) * mm});
            skLineSegment(sketch, "E342", {"start": v(11.73, 21.12) * mm, "end": v(11.56, 20.96) * mm});
            skLineSegment(sketch, "E343", {"start": v(11.56, 20.96) * mm, "end": v(11.4, 20.79) * mm});
            skLineSegment(sketch, "E344", {"start": v(11.4, 20.79) * mm, "end": v(11.26, 20.6) * mm});
            skLineSegment(sketch, "E345", {"start": v(11.26, 20.6) * mm, "end": v(11.12, 20.42) * mm});
            skLineSegment(sketch, "E346", {"start": v(11.12, 20.42) * mm, "end": v(11, 20.22) * mm});
            skLineSegment(sketch, "E347", {"start": v(11, 20.22) * mm, "end": v(10.88, 20.02) * mm});
            skLineSegment(sketch, "E348", {"start": v(10.88, 20.02) * mm, "end": v(10.76, 19.82) * mm});
            skLineSegment(sketch, "E349", {"start": v(10.76, 19.82) * mm, "end": v(10.65, 19.63) * mm});
            skLineSegment(sketch, "E350", {"start": v(10.65, 19.63) * mm, "end": v(10.53, 19.43) * mm});
            skLineSegment(sketch, "E351", {"start": v(10.53, 19.43) * mm, "end": v(10.42, 19.24) * mm});
            skLineSegment(sketch, "E352", {"start": v(10.42, 19.24) * mm, "end": v(10.3, 19.04) * mm});
            skLineSegment(sketch, "E353", {"start": v(10.3, 19.04) * mm, "end": v(10.18, 18.85) * mm});
            skLineSegment(sketch, "E354", {"start": v(10.18, 18.85) * mm, "end": v(10.06, 18.65) * mm});
            skLineSegment(sketch, "E355", {"start": v(10.06, 18.65) * mm, "end": v(10.02, 18.57) * mm});
            skLineSegment(sketch, "E356", {"start": v(10.02, 18.57) * mm, "end": v(9.81, 18.69) * mm});
            skLineSegment(sketch, "E357", {"start": v(9.81, 18.69) * mm, "end": v(9.6, 18.8) * mm});
            skLineSegment(sketch, "E358", {"start": v(9.6, 18.8) * mm, "end": v(9.4, 18.9) * mm});
            skLineSegment(sketch, "E359", {"start": v(9.4, 18.9) * mm, "end": v(9.2, 19.02) * mm});
            skLineSegment(sketch, "E360", {"start": v(9.2, 19.02) * mm, "end": v(8.99, 19.13) * mm});
            skLineSegment(sketch, "E361", {"start": v(8.99, 19.13) * mm, "end": v(8.78, 19.24) * mm});
            skLineSegment(sketch, "E362", {"start": v(8.78, 19.24) * mm, "end": v(8.58, 19.35) * mm});
            skLineSegment(sketch, "E363", {"start": v(8.58, 19.35) * mm, "end": v(8.44, 19.42) * mm});
            skLineSegment(sketch, "E364", {"start": v(8.44, 19.42) * mm, "end": v(8.55, 19.63) * mm});
            skLineSegment(sketch, "E365", {"start": v(8.55, 19.63) * mm, "end": v(8.64, 19.83) * mm});
            skLineSegment(sketch, "E366", {"start": v(8.64, 19.83) * mm, "end": v(8.75, 20.04) * mm});
            skLineSegment(sketch, "E367", {"start": v(8.75, 20.04) * mm, "end": v(8.84, 20.24) * mm});
            skLineSegment(sketch, "E368", {"start": v(8.84, 20.24) * mm, "end": v(8.95, 20.45) * mm});
            skLineSegment(sketch, "E369", {"start": v(8.95, 20.45) * mm, "end": v(9.04, 20.65) * mm});
            skLineSegment(sketch, "E370", {"start": v(9.04, 20.65) * mm, "end": v(9.15, 20.86) * mm});
            skLineSegment(sketch, "E371", {"start": v(9.15, 20.86) * mm, "end": v(9.24, 21.06) * mm});
            skLineSegment(sketch, "E372", {"start": v(9.24, 21.06) * mm, "end": v(9.34, 21.27) * mm});
            skLineSegment(sketch, "E373", {"start": v(9.34, 21.27) * mm, "end": v(9.43, 21.48) * mm});
            skLineSegment(sketch, "E374", {"start": v(9.43, 21.48) * mm, "end": v(9.5, 21.7) * mm});
            skLineSegment(sketch, "E375", {"start": v(9.5, 21.7) * mm, "end": v(9.57, 21.93) * mm});
            skLineSegment(sketch, "E376", {"start": v(9.57, 21.93) * mm, "end": v(9.62, 22.16) * mm});
            skLineSegment(sketch, "E377", {"start": v(9.62, 22.16) * mm, "end": v(9.66, 22.39) * mm});
            skLineSegment(sketch, "E378", {"start": v(9.66, 22.39) * mm, "end": v(9.69, 22.62) * mm});
            skLineSegment(sketch, "E379", {"start": v(9.69, 22.62) * mm, "end": v(9.7, 22.85) * mm});
            skLineSegment(sketch, "E380", {"start": v(9.7, 22.85) * mm, "end": v(9.7, 23.09) * mm});
            skLineSegment(sketch, "E381", {"start": v(9.7, 23.09) * mm, "end": v(9.68, 23.32) * mm});
            skLineSegment(sketch, "E382", {"start": v(9.68, 23.32) * mm, "end": v(9.65, 23.55) * mm});
            skLineSegment(sketch, "E383", {"start": v(9.65, 23.55) * mm, "end": v(9.6, 23.78) * mm});
            skLineSegment(sketch, "E384", {"start": v(9.6, 23.78) * mm, "end": v(9.55, 24.01) * mm});
            skLineSegment(sketch, "E385", {"start": v(9.55, 24.01) * mm, "end": v(9.52, 24.1) * mm});
            skLineSegment(sketch, "E386", {"start": v(9.52, 24.1) * mm, "end": v(9.32, 24) * mm});
            skLineSegment(sketch, "E387", {"start": v(9.32, 24) * mm, "end": v(9.11, 23.88) * mm});
            skLineSegment(sketch, "E388", {"start": v(9.11, 23.88) * mm, "end": v(8.92, 23.75) * mm});
            skLineSegment(sketch, "E389", {"start": v(8.92, 23.75) * mm, "end": v(8.73, 23.6) * mm});
            skLineSegment(sketch, "E390", {"start": v(8.73, 23.6) * mm, "end": v(8.56, 23.45) * mm});
            skLineSegment(sketch, "E391", {"start": v(8.56, 23.45) * mm, "end": v(8.39, 23.3) * mm});
            skLineSegment(sketch, "E392", {"start": v(8.39, 23.3) * mm, "end": v(8.23, 23.12) * mm});
            skLineSegment(sketch, "E393", {"start": v(8.23, 23.12) * mm, "end": v(8.08, 22.94) * mm});
            skLineSegment(sketch, "E394", {"start": v(8.08, 22.94) * mm, "end": v(7.94, 22.75) * mm});
            skLineSegment(sketch, "E395", {"start": v(7.94, 22.75) * mm, "end": v(7.82, 22.55) * mm});
            skLineSegment(sketch, "E396", {"start": v(7.82, 22.55) * mm, "end": v(7.7, 22.35) * mm});
            skLineSegment(sketch, "E397", {"start": v(7.7, 22.35) * mm, "end": v(7.6, 22.14) * mm});
            skLineSegment(sketch, "E398", {"start": v(7.6, 22.14) * mm, "end": v(7.5, 21.93) * mm});
            skLineSegment(sketch, "E399", {"start": v(7.5, 21.93) * mm, "end": v(7.42, 21.72) * mm});
            skLineSegment(sketch, "E400", {"start": v(7.42, 21.72) * mm, "end": v(7.34, 21.5) * mm});
            skLineSegment(sketch, "E401", {"start": v(7.34, 21.5) * mm, "end": v(7.26, 21.3) * mm});
            skLineSegment(sketch, "E402", {"start": v(7.26, 21.3) * mm, "end": v(7.17, 21.07) * mm});
            skLineSegment(sketch, "E403", {"start": v(7.17, 21.07) * mm, "end": v(7.1, 20.87) * mm});
            skLineSegment(sketch, "E404", {"start": v(7.1, 20.87) * mm, "end": v(7, 20.65) * mm});
            skLineSegment(sketch, "E405", {"start": v(7, 20.65) * mm, "end": v(6.93, 20.45) * mm});
            skLineSegment(sketch, "E406", {"start": v(6.93, 20.45) * mm, "end": v(6.84, 20.23) * mm});
            skLineSegment(sketch, "E407", {"start": v(6.84, 20.23) * mm, "end": v(6.8, 20.14) * mm});
            skLineSegment(sketch, "E408", {"start": v(6.8, 20.14) * mm, "end": v(6.59, 20.22) * mm});
            skLineSegment(sketch, "E409", {"start": v(6.59, 20.22) * mm, "end": v(6.37, 20.3) * mm});
            skLineSegment(sketch, "E410", {"start": v(6.37, 20.3) * mm, "end": v(6.14, 20.37) * mm});
            skLineSegment(sketch, "E411", {"start": v(6.14, 20.37) * mm, "end": v(5.92, 20.45) * mm});
            skLineSegment(sketch, "E412", {"start": v(5.92, 20.45) * mm, "end": v(5.7, 20.52) * mm});
            skLineSegment(sketch, "E413", {"start": v(5.7, 20.52) * mm, "end": v(5.48, 20.6) * mm});
            skLineSegment(sketch, "E414", {"start": v(5.48, 20.6) * mm, "end": v(5.26, 20.67) * mm});
            skLineSegment(sketch, "E415", {"start": v(5.26, 20.67) * mm, "end": v(5.12, 20.72) * mm});
            skLineSegment(sketch, "E416", {"start": v(5.12, 20.72) * mm, "end": v(5.18, 20.95) * mm});
            skLineSegment(sketch, "E417", {"start": v(5.18, 20.95) * mm, "end": v(5.25, 21.16) * mm});
            skLineSegment(sketch, "E418", {"start": v(5.25, 21.16) * mm, "end": v(5.31, 21.38) * mm});
            skLineSegment(sketch, "E419", {"start": v(5.31, 21.38) * mm, "end": v(5.38, 21.6) * mm});
            skLineSegment(sketch, "E420", {"start": v(5.38, 21.6) * mm, "end": v(5.44, 21.82) * mm});
            skLineSegment(sketch, "E421", {"start": v(5.44, 21.82) * mm, "end": v(5.5, 22.03) * mm});
            skLineSegment(sketch, "E422", {"start": v(5.5, 22.03) * mm, "end": v(5.57, 22.25) * mm});
            skLineSegment(sketch, "E423", {"start": v(5.57, 22.25) * mm, "end": v(5.64, 22.47) * mm});
            skLineSegment(sketch, "E424", {"start": v(5.64, 22.47) * mm, "end": v(5.7, 22.69) * mm});
            skLineSegment(sketch, "E425", {"start": v(5.7, 22.69) * mm, "end": v(5.75, 22.92) * mm});
            skLineSegment(sketch, "E426", {"start": v(5.75, 22.92) * mm, "end": v(5.8, 23.15) * mm});
            skLineSegment(sketch, "E427", {"start": v(5.8, 23.15) * mm, "end": v(5.82, 23.38) * mm});
            skLineSegment(sketch, "E428", {"start": v(5.82, 23.38) * mm, "end": v(5.83, 23.61) * mm});
            skLineSegment(sketch, "E429", {"start": v(5.83, 23.61) * mm, "end": v(5.83, 23.85) * mm});
            skLineSegment(sketch, "E430", {"start": v(5.83, 23.85) * mm, "end": v(5.82, 24.08) * mm});
            skLineSegment(sketch, "E431", {"start": v(5.82, 24.08) * mm, "end": v(5.79, 24.31) * mm});
            skLineSegment(sketch, "E432", {"start": v(5.79, 24.31) * mm, "end": v(5.75, 24.54) * mm});
            skLineSegment(sketch, "E433", {"start": v(5.75, 24.54) * mm, "end": v(5.7, 24.77) * mm});
            skLineSegment(sketch, "E434", {"start": v(5.7, 24.77) * mm, "end": v(5.62, 25) * mm});
            skLineSegment(sketch, "E435", {"start": v(5.62, 25) * mm, "end": v(5.55, 25.21) * mm});
            skLineSegment(sketch, "E436", {"start": v(5.55, 25.21) * mm, "end": v(5.45, 25.43) * mm});
            skLineSegment(sketch, "E437", {"start": v(5.45, 25.43) * mm, "end": v(5.41, 25.52) * mm});
            skLineSegment(sketch, "E438", {"start": v(5.41, 25.52) * mm, "end": v(5.22, 25.38) * mm});
            skLineSegment(sketch, "E439", {"start": v(5.22, 25.38) * mm, "end": v(5.05, 25.23) * mm});
            skLineSegment(sketch, "E440", {"start": v(5.05, 25.23) * mm, "end": v(4.87, 25.07) * mm});
            skLineSegment(sketch, "E441", {"start": v(4.87, 25.07) * mm, "end": v(4.72, 24.9) * mm});
            skLineSegment(sketch, "E442", {"start": v(4.72, 24.9) * mm, "end": v(4.57, 24.72) * mm});
            skLineSegment(sketch, "E443", {"start": v(4.57, 24.72) * mm, "end": v(4.42, 24.53) * mm});
            skLineSegment(sketch, "E444", {"start": v(4.42, 24.53) * mm, "end": v(4.3, 24.33) * mm});
            skLineSegment(sketch, "E445", {"start": v(4.3, 24.33) * mm, "end": v(4.18, 24.13) * mm});
            skLineSegment(sketch, "E446", {"start": v(4.18, 24.13) * mm, "end": v(4.07, 23.92) * mm});
            skLineSegment(sketch, "E447", {"start": v(4.07, 23.92) * mm, "end": v(3.98, 23.7) * mm});
            skLineSegment(sketch, "E448", {"start": v(3.98, 23.7) * mm, "end": v(3.9, 23.49) * mm});
            skLineSegment(sketch, "E449", {"start": v(3.9, 23.49) * mm, "end": v(3.83, 23.26) * mm});
            skLineSegment(sketch, "E450", {"start": v(3.83, 23.26) * mm, "end": v(3.78, 23.04) * mm});
            skLineSegment(sketch, "E451", {"start": v(3.78, 23.04) * mm, "end": v(3.73, 22.81) * mm});
            skLineSegment(sketch, "E452", {"start": v(3.73, 22.81) * mm, "end": v(3.68, 22.59) * mm});
            skLineSegment(sketch, "E453", {"start": v(3.68, 22.59) * mm, "end": v(3.64, 22.37) * mm});
            skLineSegment(sketch, "E454", {"start": v(3.64, 22.37) * mm, "end": v(3.6, 22.14) * mm});
            skLineSegment(sketch, "E455", {"start": v(3.6, 22.14) * mm, "end": v(3.55, 21.92) * mm});
            skLineSegment(sketch, "E456", {"start": v(3.55, 21.92) * mm, "end": v(3.5, 21.7) * mm});
            skLineSegment(sketch, "E457", {"start": v(3.5, 21.7) * mm, "end": v(3.45, 21.48) * mm});
            skLineSegment(sketch, "E458", {"start": v(3.45, 21.48) * mm, "end": v(3.4, 21.25) * mm});
            skLineSegment(sketch, "E459", {"start": v(3.4, 21.25) * mm, "end": v(3.39, 21.16) * mm});
            skLineSegment(sketch, "E460", {"start": v(3.39, 21.16) * mm, "end": v(3.15, 21.2) * mm});
            skLineSegment(sketch, "E461", {"start": v(3.15, 21.2) * mm, "end": v(2.92, 21.24) * mm});
            skLineSegment(sketch, "E462", {"start": v(2.92, 21.24) * mm, "end": v(2.7, 21.28) * mm});
            skLineSegment(sketch, "E463", {"start": v(2.7, 21.28) * mm, "end": v(2.46, 21.32) * mm});
            skLineSegment(sketch, "E464", {"start": v(2.46, 21.32) * mm, "end": v(2.23, 21.35) * mm});
            skLineSegment(sketch, "E465", {"start": v(2.23, 21.35) * mm, "end": v(2, 21.4) * mm});
            skLineSegment(sketch, "E466", {"start": v(2, 21.4) * mm, "end": v(1.77, 21.43) * mm});
            skLineSegment(sketch, "E467", {"start": v(1.77, 21.43) * mm, "end": v(1.62, 21.46) * mm});
            skLineSegment(sketch, "E468", {"start": v(1.62, 21.46) * mm, "end": v(1.65, 21.69) * mm});
            skLineSegment(sketch, "E469", {"start": v(1.65, 21.69) * mm, "end": v(1.68, 21.9) * mm});
            skLineSegment(sketch, "E470", {"start": v(1.68, 21.9) * mm, "end": v(1.7, 22.14) * mm});
            skLineSegment(sketch, "E471", {"start": v(1.7, 22.14) * mm, "end": v(1.74, 22.36) * mm});
            skLineSegment(sketch, "E472", {"start": v(1.74, 22.36) * mm, "end": v(1.76, 22.6) * mm});
            skLineSegment(sketch, "E473", {"start": v(1.76, 22.6) * mm, "end": v(1.8, 22.8) * mm});
            skLineSegment(sketch, "E474", {"start": v(1.8, 22.8) * mm, "end": v(1.82, 23.04) * mm});
            skLineSegment(sketch, "E475", {"start": v(1.82, 23.04) * mm, "end": v(1.85, 23.26) * mm});
            skLineSegment(sketch, "E476", {"start": v(1.85, 23.26) * mm, "end": v(1.87, 23.49) * mm});
            skLineSegment(sketch, "E477", {"start": v(1.87, 23.49) * mm, "end": v(1.89, 23.72) * mm});
            skLineSegment(sketch, "E478", {"start": v(1.89, 23.72) * mm, "end": v(1.89, 23.96) * mm});
            skLineSegment(sketch, "E479", {"start": v(1.89, 23.96) * mm, "end": v(1.88, 24.2) * mm});
            skLineSegment(sketch, "E480", {"start": v(1.88, 24.2) * mm, "end": v(1.85, 24.42) * mm});
            skLineSegment(sketch, "E481", {"start": v(1.85, 24.42) * mm, "end": v(1.81, 24.65) * mm});
            skLineSegment(sketch, "E482", {"start": v(1.81, 24.65) * mm, "end": v(1.76, 24.88) * mm});
            skLineSegment(sketch, "E483", {"start": v(1.76, 24.88) * mm, "end": v(1.7, 25.1) * mm});
            skLineSegment(sketch, "E484", {"start": v(1.7, 25.1) * mm, "end": v(1.61, 25.33) * mm});
            skLineSegment(sketch, "E485", {"start": v(1.61, 25.33) * mm, "end": v(1.52, 25.54) * mm});
            skLineSegment(sketch, "E486", {"start": v(1.52, 25.54) * mm, "end": v(1.42, 25.75) * mm});
            skLineSegment(sketch, "E487", {"start": v(1.42, 25.75) * mm, "end": v(1.3, 25.96) * mm});
            skLineSegment(sketch, "E488", {"start": v(1.3, 25.96) * mm, "end": v(1.18, 26.15) * mm});
            skLineSegment(sketch, "E489", {"start": v(1.18, 26.15) * mm, "end": v(1.12, 26.23) * mm});
            skLineSegment(sketch, "E490", {"start": v(1.12, 26.23) * mm, "end": v(0.96, 26.06) * mm});
            skLineSegment(sketch, "E491", {"start": v(0.96, 26.06) * mm, "end": v(0.8, 25.89) * mm});
            skLineSegment(sketch, "E492", {"start": v(0.8, 25.89) * mm, "end": v(0.67, 25.7) * mm});
            skLineSegment(sketch, "E493", {"start": v(0.67, 25.7) * mm, "end": v(0.54, 25.5) * mm});
            skLineSegment(sketch, "E494", {"start": v(0.54, 25.5) * mm, "end": v(0.42, 25.3) * mm});
            skLineSegment(sketch, "E495", {"start": v(0.42, 25.3) * mm, "end": v(0.31, 25.1) * mm});
            skLineSegment(sketch, "E496", {"start": v(0.31, 25.1) * mm, "end": v(0.22, 24.88) * mm});
            skLineSegment(sketch, "E497", {"start": v(0.22, 24.88) * mm, "end": v(0.14, 24.66) * mm});
            skLineSegment(sketch, "E498", {"start": v(0.14, 24.66) * mm, "end": v(0.07, 24.44) * mm});
            skLineSegment(sketch, "E499", {"start": v(0.07, 24.44) * mm, "end": v(0.01, 24.21) * mm});
            skLineSegment(sketch, "E500", {"start": v(0.01, 24.21) * mm, "end": v(-0.03, 23.98) * mm});
            skLineSegment(sketch, "E501", {"start": v(-0.03, 23.98) * mm, "end": v(-0.06, 23.75) * mm});
            skLineSegment(sketch, "E502", {"start": v(-0.06, 23.75) * mm, "end": v(-0.08, 23.52) * mm});
            skLineSegment(sketch, "E503", {"start": v(-0.08, 23.52) * mm, "end": v(-0.09, 23.3) * mm});
            skLineSegment(sketch, "E504", {"start": v(-0.09, 23.3) * mm, "end": v(-0.1, 23.06) * mm});
            skLineSegment(sketch, "E505", {"start": v(-0.1, 23.06) * mm, "end": v(-0.1, 22.84) * mm});
            skLineSegment(sketch, "E506", {"start": v(-0.1, 22.84) * mm, "end": v(-0.12, 22.6) * mm});
            skLineSegment(sketch, "E507", {"start": v(-0.12, 22.6) * mm, "end": v(-0.13, 22.38) * mm});
            skLineSegment(sketch, "E508", {"start": v(-0.13, 22.38) * mm, "end": v(-0.14, 22.15) * mm});
            skLineSegment(sketch, "E509", {"start": v(-0.14, 22.15) * mm, "end": v(-0.14, 21.93) * mm});
            skLineSegment(sketch, "E510", {"start": v(-0.14, 21.93) * mm, "end": v(-0.15, 21.7) * mm});
            skLineSegment(sketch, "E511", {"start": v(-0.15, 21.7) * mm, "end": v(-0.16, 21.6) * mm});
            skLineSegment(sketch, "E512", {"start": v(-0.16, 21.6) * mm, "end": v(-0.4, 21.6) * mm});
            skLineSegment(sketch, "E513", {"start": v(-0.4, 21.6) * mm, "end": v(-0.63, 21.6) * mm});
            skLineSegment(sketch, "E514", {"start": v(-0.63, 21.6) * mm, "end": v(-0.86, 21.6) * mm});
            skLineSegment(sketch, "E515", {"start": v(-0.86, 21.6) * mm, "end": v(-1.1, 21.6) * mm});
            skLineSegment(sketch, "E516", {"start": v(-1.1, 21.6) * mm, "end": v(-1.33, 21.6) * mm});
            skLineSegment(sketch, "E517", {"start": v(-1.33, 21.6) * mm, "end": v(-1.56, 21.6) * mm});
            skLineSegment(sketch, "E518", {"start": v(-1.56, 21.6) * mm, "end": v(-1.8, 21.6) * mm});
            skLineSegment(sketch, "E519", {"start": v(-1.8, 21.6) * mm, "end": v(-1.95, 21.6) * mm});
            skLineSegment(sketch, "E520", {"start": v(-1.95, 21.6) * mm, "end": v(-1.95, 21.84) * mm});
            skLineSegment(sketch, "E521", {"start": v(-1.95, 21.84) * mm, "end": v(-1.96, 22.06) * mm});
            skLineSegment(sketch, "E522", {"start": v(-1.96, 22.06) * mm, "end": v(-1.97, 22.3) * mm});
            skLineSegment(sketch, "E523", {"start": v(-1.97, 22.3) * mm, "end": v(-1.98, 22.51) * mm});
            skLineSegment(sketch, "E524", {"start": v(-1.98, 22.51) * mm, "end": v(-2, 22.75) * mm});
            skLineSegment(sketch, "E525", {"start": v(-2, 22.75) * mm, "end": v(-2, 22.97) * mm});
            skLineSegment(sketch, "E526", {"start": v(-2, 22.97) * mm, "end": v(-2.01, 23.2) * mm});
            skLineSegment(sketch, "E527", {"start": v(-2.01, 23.2) * mm, "end": v(-2.02, 23.42) * mm});
            skLineSegment(sketch, "E528", {"start": v(-2.02, 23.42) * mm, "end": v(-2.03, 23.65) * mm});
            skLineSegment(sketch, "E529", {"start": v(-2.03, 23.65) * mm, "end": v(-2.06, 23.88) * mm});
            skLineSegment(sketch, "E530", {"start": v(-2.06, 23.88) * mm, "end": v(-2.1, 24.11) * mm});
            skLineSegment(sketch, "E531", {"start": v(-2.1, 24.11) * mm, "end": v(-2.14, 24.34) * mm});
            skLineSegment(sketch, "E532", {"start": v(-2.14, 24.34) * mm, "end": v(-2.2, 24.57) * mm});
            skLineSegment(sketch, "E533", {"start": v(-2.2, 24.57) * mm, "end": v(-2.29, 24.79) * mm});
            skLineSegment(sketch, "E534", {"start": v(-2.29, 24.79) * mm, "end": v(-2.37, 25) * mm});
            skLineSegment(sketch, "E535", {"start": v(-2.37, 25) * mm, "end": v(-2.48, 25.21) * mm});
            skLineSegment(sketch, "E536", {"start": v(-2.48, 25.21) * mm, "end": v(-2.6, 25.42) * mm});
            skLineSegment(sketch, "E537", {"start": v(-2.6, 25.42) * mm, "end": v(-2.71, 25.62) * mm});
            skLineSegment(sketch, "E538", {"start": v(-2.71, 25.62) * mm, "end": v(-2.85, 25.8) * mm});
            skLineSegment(sketch, "E539", {"start": v(-2.85, 25.8) * mm, "end": v(-3, 25.99) * mm});
            skLineSegment(sketch, "E540", {"start": v(-3, 25.99) * mm, "end": v(-3.16, 26.16) * mm});
            skLineSegment(sketch, "E541", {"start": v(-3.16, 26.16) * mm, "end": v(-3.23, 26.23) * mm});
            skLineSegment(sketch, "E542", {"start": v(-3.23, 26.23) * mm, "end": v(-3.36, 26.04) * mm});
            skLineSegment(sketch, "E543", {"start": v(-3.36, 26.04) * mm, "end": v(-3.48, 25.84) * mm});
            skLineSegment(sketch, "E544", {"start": v(-3.48, 25.84) * mm, "end": v(-3.59, 25.63) * mm});
            skLineSegment(sketch, "E545", {"start": v(-3.59, 25.63) * mm, "end": v(-3.68, 25.42) * mm});
            skLineSegment(sketch, "E546", {"start": v(-3.68, 25.42) * mm, "end": v(-3.76, 25.2) * mm});
            skLineSegment(sketch, "E547", {"start": v(-3.76, 25.2) * mm, "end": v(-3.84, 24.98) * mm});
            skLineSegment(sketch, "E548", {"start": v(-3.84, 24.98) * mm, "end": v(-3.9, 24.75) * mm});
            skLineSegment(sketch, "E549", {"start": v(-3.9, 24.75) * mm, "end": v(-3.94, 24.52) * mm});
            skLineSegment(sketch, "E550", {"start": v(-3.94, 24.52) * mm, "end": v(-3.97, 24.3) * mm});
            skLineSegment(sketch, "E551", {"start": v(-3.97, 24.3) * mm, "end": v(-3.99, 24.06) * mm});
            skLineSegment(sketch, "E552", {"start": v(-3.99, 24.06) * mm, "end": v(-4, 23.82) * mm});
            skLineSegment(sketch, "E553", {"start": v(-4, 23.82) * mm, "end": v(-3.99, 23.59) * mm});
            skLineSegment(sketch, "E554", {"start": v(-3.99, 23.59) * mm, "end": v(-3.96, 23.36) * mm});
            skLineSegment(sketch, "E555", {"start": v(-3.96, 23.36) * mm, "end": v(-3.94, 23.13) * mm});
            skLineSegment(sketch, "E556", {"start": v(-3.94, 23.13) * mm, "end": v(-3.9, 22.9) * mm});
            skLineSegment(sketch, "E557", {"start": v(-3.9, 22.9) * mm, "end": v(-3.88, 22.68) * mm});
            skLineSegment(sketch, "E558", {"start": v(-3.88, 22.68) * mm, "end": v(-3.85, 22.45) * mm});
            skLineSegment(sketch, "E559", {"start": v(-3.85, 22.45) * mm, "end": v(-3.82, 22.23) * mm});
            skLineSegment(sketch, "E560", {"start": v(-3.82, 22.23) * mm, "end": v(-3.8, 22) * mm});
            skLineSegment(sketch, "E561", {"start": v(-3.8, 22) * mm, "end": v(-3.77, 21.78) * mm});
            skLineSegment(sketch, "E562", {"start": v(-3.77, 21.78) * mm, "end": v(-3.74, 21.55) * mm});
            skLineSegment(sketch, "E563", {"start": v(-3.74, 21.55) * mm, "end": v(-3.73, 21.46) * mm});
            skLineSegment(sketch, "E564", {"start": v(-3.73, 21.46) * mm, "end": v(-3.96, 21.42) * mm});
            skLineSegment(sketch, "E565", {"start": v(-3.96, 21.42) * mm, "end": v(-4.19, 21.38) * mm});
            skLineSegment(sketch, "E566", {"start": v(-4.19, 21.38) * mm, "end": v(-4.42, 21.34) * mm});
            skLineSegment(sketch, "E567", {"start": v(-4.42, 21.34) * mm, "end": v(-4.65, 21.3) * mm});
            skLineSegment(sketch, "E568", {"start": v(-4.65, 21.3) * mm, "end": v(-4.88, 21.26) * mm});
            skLineSegment(sketch, "E569", {"start": v(-4.88, 21.26) * mm, "end": v(-5.11, 21.22) * mm});
            skLineSegment(sketch, "E570", {"start": v(-5.11, 21.22) * mm, "end": v(-5.34, 21.19) * mm});
            skLineSegment(sketch, "E571", {"start": v(-5.34, 21.19) * mm, "end": v(-5.49, 21.16) * mm});
            skLineSegment(sketch, "E572", {"start": v(-5.49, 21.16) * mm, "end": v(-5.54, 21.4) * mm});
            skLineSegment(sketch, "E573", {"start": v(-5.54, 21.4) * mm, "end": v(-5.58, 21.6) * mm});
            skLineSegment(sketch, "E574", {"start": v(-5.58, 21.6) * mm, "end": v(-5.63, 21.84) * mm});
            skLineSegment(sketch, "E575", {"start": v(-5.63, 21.84) * mm, "end": v(-5.68, 22.05) * mm});
            skLineSegment(sketch, "E576", {"start": v(-5.68, 22.05) * mm, "end": v(-5.72, 22.28) * mm});
            skLineSegment(sketch, "E577", {"start": v(-5.72, 22.28) * mm, "end": v(-5.77, 22.5) * mm});
            skLineSegment(sketch, "E578", {"start": v(-5.77, 22.5) * mm, "end": v(-5.82, 22.73) * mm});
            skLineSegment(sketch, "E579", {"start": v(-5.82, 22.73) * mm, "end": v(-5.86, 22.94) * mm});
            skLineSegment(sketch, "E580", {"start": v(-5.86, 22.94) * mm, "end": v(-5.91, 23.17) * mm});
            skLineSegment(sketch, "E581", {"start": v(-5.91, 23.17) * mm, "end": v(-5.98, 23.4) * mm});
            skLineSegment(sketch, "E582", {"start": v(-5.98, 23.4) * mm, "end": v(-6.05, 23.61) * mm});
            skLineSegment(sketch, "E583", {"start": v(-6.05, 23.61) * mm, "end": v(-6.14, 23.83) * mm});
            skLineSegment(sketch, "E584", {"start": v(-6.14, 23.83) * mm, "end": v(-6.24, 24.04) * mm});
            skLineSegment(sketch, "E585", {"start": v(-6.24, 24.04) * mm, "end": v(-6.35, 24.25) * mm});
            skLineSegment(sketch, "E586", {"start": v(-6.35, 24.25) * mm, "end": v(-6.47, 24.45) * mm});
            skLineSegment(sketch, "E587", {"start": v(-6.47, 24.45) * mm, "end": v(-6.6, 24.64) * mm});
            skLineSegment(sketch, "E588", {"start": v(-6.6, 24.64) * mm, "end": v(-6.75, 24.82) * mm});
            skLineSegment(sketch, "E589", {"start": v(-6.75, 24.82) * mm, "end": v(-6.9, 25) * mm});
            skLineSegment(sketch, "E590", {"start": v(-6.9, 25) * mm, "end": v(-7.08, 25.16) * mm});
            skLineSegment(sketch, "E591", {"start": v(-7.08, 25.16) * mm, "end": v(-7.25, 25.31) * mm});
            skLineSegment(sketch, "E592", {"start": v(-7.25, 25.31) * mm, "end": v(-7.43, 25.46) * mm});
            skLineSegment(sketch, "E593", {"start": v(-7.43, 25.46) * mm, "end": v(-7.51, 25.52) * mm});
            skLineSegment(sketch, "E594", {"start": v(-7.51, 25.52) * mm, "end": v(-7.61, 25.3) * mm});
            skLineSegment(sketch, "E595", {"start": v(-7.61, 25.3) * mm, "end": v(-7.7, 25.09) * mm});
            skLineSegment(sketch, "E596", {"start": v(-7.7, 25.09) * mm, "end": v(-7.77, 24.87) * mm});
            skLineSegment(sketch, "E597", {"start": v(-7.77, 24.87) * mm, "end": v(-7.83, 24.64) * mm});
            skLineSegment(sketch, "E598", {"start": v(-7.83, 24.64) * mm, "end": v(-7.88, 24.41) * mm});
            skLineSegment(sketch, "E599", {"start": v(-7.88, 24.41) * mm, "end": v(-7.9, 24.18) * mm});
            skLineSegment(sketch, "E600", {"start": v(-7.9, 24.18) * mm, "end": v(-7.93, 23.95) * mm});
            skLineSegment(sketch, "E601", {"start": v(-7.93, 23.95) * mm, "end": v(-7.94, 23.71) * mm});
            skLineSegment(sketch, "E602", {"start": v(-7.94, 23.71) * mm, "end": v(-7.93, 23.48) * mm});
            skLineSegment(sketch, "E603", {"start": v(-7.93, 23.48) * mm, "end": v(-7.9, 23.25) * mm});
            skLineSegment(sketch, "E604", {"start": v(-7.9, 23.25) * mm, "end": v(-7.87, 23.01) * mm});
            skLineSegment(sketch, "E605", {"start": v(-7.87, 23.01) * mm, "end": v(-7.83, 22.78) * mm});
            skLineSegment(sketch, "E606", {"start": v(-7.83, 22.78) * mm, "end": v(-7.77, 22.56) * mm});
            skLineSegment(sketch, "E607", {"start": v(-7.77, 22.56) * mm, "end": v(-7.7, 22.34) * mm});
            skLineSegment(sketch, "E608", {"start": v(-7.7, 22.34) * mm, "end": v(-7.64, 22.12) * mm});
            skLineSegment(sketch, "E609", {"start": v(-7.64, 22.12) * mm, "end": v(-7.57, 21.9) * mm});
            skLineSegment(sketch, "E610", {"start": v(-7.57, 21.9) * mm, "end": v(-7.5, 21.68) * mm});
            skLineSegment(sketch, "E611", {"start": v(-7.5, 21.68) * mm, "end": v(-7.44, 21.47) * mm});
            skLineSegment(sketch, "E612", {"start": v(-7.44, 21.47) * mm, "end": v(-7.38, 21.25) * mm});
            skLineSegment(sketch, "E613", {"start": v(-7.38, 21.25) * mm, "end": v(-7.31, 21.03) * mm});
            skLineSegment(sketch, "E614", {"start": v(-7.31, 21.03) * mm, "end": v(-7.25, 20.8) * mm});
            skLineSegment(sketch, "E615", {"start": v(-7.25, 20.8) * mm, "end": v(-7.22, 20.72) * mm});
            skLineSegment(sketch, "E616", {"start": v(-7.22, 20.72) * mm, "end": v(-7.44, 20.65) * mm});
            skLineSegment(sketch, "E617", {"start": v(-7.44, 20.65) * mm, "end": v(-7.66, 20.57) * mm});
            skLineSegment(sketch, "E618", {"start": v(-7.66, 20.57) * mm, "end": v(-7.89, 20.5) * mm});
            skLineSegment(sketch, "E619", {"start": v(-7.89, 20.5) * mm, "end": v(-8.1, 20.42) * mm});
            skLineSegment(sketch, "E620", {"start": v(-8.1, 20.42) * mm, "end": v(-8.33, 20.34) * mm});
            skLineSegment(sketch, "E621", {"start": v(-8.33, 20.34) * mm, "end": v(-8.55, 20.27) * mm});
            skLineSegment(sketch, "E622", {"start": v(-8.55, 20.27) * mm, "end": v(-8.77, 20.2) * mm});
            skLineSegment(sketch, "E623", {"start": v(-8.77, 20.2) * mm, "end": v(-8.91, 20.14) * mm});
            skLineSegment(sketch, "E624", {"start": v(-8.91, 20.14) * mm, "end": v(-9, 20.36) * mm});
            skLineSegment(sketch, "E625", {"start": v(-9, 20.36) * mm, "end": v(-9.08, 20.57) * mm});
            skLineSegment(sketch, "E626", {"start": v(-9.08, 20.57) * mm, "end": v(-9.16, 20.78) * mm});
            skLineSegment(sketch, "E627", {"start": v(-9.16, 20.78) * mm, "end": v(-9.24, 20.99) * mm});
            skLineSegment(sketch, "E628", {"start": v(-9.24, 20.99) * mm, "end": v(-9.33, 21.2) * mm});
            skLineSegment(sketch, "E629", {"start": v(-9.33, 21.2) * mm, "end": v(-9.4, 21.41) * mm});
            skLineSegment(sketch, "E630", {"start": v(-9.4, 21.41) * mm, "end": v(-9.5, 21.63) * mm});
            skLineSegment(sketch, "E631", {"start": v(-9.5, 21.63) * mm, "end": v(-9.57, 21.84) * mm});
            skLineSegment(sketch, "E632", {"start": v(-9.57, 21.84) * mm, "end": v(-9.66, 22.05) * mm});
            skLineSegment(sketch, "E633", {"start": v(-9.66, 22.05) * mm, "end": v(-9.76, 22.26) * mm});
            skLineSegment(sketch, "E634", {"start": v(-9.76, 22.26) * mm, "end": v(-9.87, 22.47) * mm});
            skLineSegment(sketch, "E635", {"start": v(-9.87, 22.47) * mm, "end": v(-9.99, 22.67) * mm});
            skLineSegment(sketch, "E636", {"start": v(-9.99, 22.67) * mm, "end": v(-10.12, 22.86) * mm});
            skLineSegment(sketch, "E637", {"start": v(-10.12, 22.86) * mm, "end": v(-10.27, 23.04) * mm});
            skLineSegment(sketch, "E638", {"start": v(-10.27, 23.04) * mm, "end": v(-10.42, 23.22) * mm});
            skLineSegment(sketch, "E639", {"start": v(-10.42, 23.22) * mm, "end": v(-10.59, 23.39) * mm});
            skLineSegment(sketch, "E640", {"start": v(-10.59, 23.39) * mm, "end": v(-10.76, 23.54) * mm});
            skLineSegment(sketch, "E641", {"start": v(-10.76, 23.54) * mm, "end": v(-10.94, 23.7) * mm});
            skLineSegment(sketch, "E642", {"start": v(-10.94, 23.7) * mm, "end": v(-11.13, 23.82) * mm});
            skLineSegment(sketch, "E643", {"start": v(-11.13, 23.82) * mm, "end": v(-11.33, 23.95) * mm});
            skLineSegment(sketch, "E644", {"start": v(-11.33, 23.95) * mm, "end": v(-11.54, 24.06) * mm});
            skLineSegment(sketch, "E645", {"start": v(-11.54, 24.06) * mm, "end": v(-11.63, 24.1) * mm});
            skLineSegment(sketch, "E646", {"start": v(-11.63, 24.1) * mm, "end": v(-11.69, 23.88) * mm});
            skLineSegment(sketch, "E647", {"start": v(-11.69, 23.88) * mm, "end": v(-11.74, 23.65) * mm});
            skLineSegment(sketch, "E648", {"start": v(-11.74, 23.65) * mm, "end": v(-11.77, 23.42) * mm});
            skLineSegment(sketch, "E649", {"start": v(-11.77, 23.42) * mm, "end": v(-11.8, 23.19) * mm});
            skLineSegment(sketch, "E650", {"start": v(-11.8, 23.19) * mm, "end": v(-11.8, 22.95) * mm});
            skLineSegment(sketch, "E651", {"start": v(-11.8, 22.95) * mm, "end": v(-11.8, 22.72) * mm});
            skLineSegment(sketch, "E652", {"start": v(-11.8, 22.72) * mm, "end": v(-11.78, 22.49) * mm});
            skLineSegment(sketch, "E653", {"start": v(-11.78, 22.49) * mm, "end": v(-11.74, 22.26) * mm});
            skLineSegment(sketch, "E654", {"start": v(-11.74, 22.26) * mm, "end": v(-11.7, 22.03) * mm});
            skLineSegment(sketch, "E655", {"start": v(-11.7, 22.03) * mm, "end": v(-11.64, 21.8) * mm});
            skLineSegment(sketch, "E656", {"start": v(-11.64, 21.8) * mm, "end": v(-11.57, 21.58) * mm});
            skLineSegment(sketch, "E657", {"start": v(-11.57, 21.58) * mm, "end": v(-11.49, 21.36) * mm});
            skLineSegment(sketch, "E658", {"start": v(-11.49, 21.36) * mm, "end": v(-11.39, 21.15) * mm});
            skLineSegment(sketch, "E659", {"start": v(-11.39, 21.15) * mm, "end": v(-11.29, 20.94) * mm});
            skLineSegment(sketch, "E660", {"start": v(-11.29, 20.94) * mm, "end": v(-11.19, 20.73) * mm});
            skLineSegment(sketch, "E661", {"start": v(-11.19, 20.73) * mm, "end": v(-11.09, 20.53) * mm});
            skLineSegment(sketch, "E662", {"start": v(-11.09, 20.53) * mm, "end": v(-10.99, 20.32) * mm});
            skLineSegment(sketch, "E663", {"start": v(-10.99, 20.32) * mm, "end": v(-10.9, 20.12) * mm});
            skLineSegment(sketch, "E664", {"start": v(-10.9, 20.12) * mm, "end": v(-10.79, 19.91) * mm});
            skLineSegment(sketch, "E665", {"start": v(-10.79, 19.91) * mm, "end": v(-10.7, 19.72) * mm});
            skLineSegment(sketch, "E666", {"start": v(-10.7, 19.72) * mm, "end": v(-10.59, 19.5) * mm});
            skLineSegment(sketch, "E667", {"start": v(-10.59, 19.5) * mm, "end": v(-10.55, 19.42) * mm});
            skLineSegment(sketch, "E668", {"start": v(-10.55, 19.42) * mm, "end": v(-10.75, 19.31) * mm});
            skLineSegment(sketch, "E669", {"start": v(-10.75, 19.31) * mm, "end": v(-10.96, 19.2) * mm});
            skLineSegment(sketch, "E670", {"start": v(-10.96, 19.2) * mm, "end": v(-11.17, 19.1) * mm});
            skLineSegment(sketch, "E671", {"start": v(-11.17, 19.1) * mm, "end": v(-11.37, 18.98) * mm});
            skLineSegment(sketch, "E672", {"start": v(-11.37, 18.98) * mm, "end": v(-11.58, 18.87) * mm});
            skLineSegment(sketch, "E673", {"start": v(-11.58, 18.87) * mm, "end": v(-11.78, 18.76) * mm});
            skLineSegment(sketch, "E674", {"start": v(-11.78, 18.76) * mm, "end": v(-11.99, 18.64) * mm});
            skLineSegment(sketch, "E675", {"start": v(-11.99, 18.64) * mm, "end": v(-12.12, 18.57) * mm});
            skLineSegment(sketch, "E676", {"start": v(-12.12, 18.57) * mm, "end": v(-12.24, 18.78) * mm});
            skLineSegment(sketch, "E677", {"start": v(-12.24, 18.78) * mm, "end": v(-12.35, 18.96) * mm});
            skLineSegment(sketch, "E678", {"start": v(-12.35, 18.96) * mm, "end": v(-12.47, 19.17) * mm});
            skLineSegment(sketch, "E679", {"start": v(-12.47, 19.17) * mm, "end": v(-12.58, 19.36) * mm});
            skLineSegment(sketch, "E680", {"start": v(-12.58, 19.36) * mm, "end": v(-12.7, 19.56) * mm});
            skLineSegment(sketch, "E681", {"start": v(-12.7, 19.56) * mm, "end": v(-12.82, 19.75) * mm});
            skLineSegment(sketch, "E682", {"start": v(-12.82, 19.75) * mm, "end": v(-12.94, 19.95) * mm});
            skLineSegment(sketch, "E683", {"start": v(-12.94, 19.95) * mm, "end": v(-13.05, 20.14) * mm});
            skLineSegment(sketch, "E684", {"start": v(-13.05, 20.14) * mm, "end": v(-13.17, 20.33) * mm});
            skLineSegment(sketch, "E685", {"start": v(-13.17, 20.33) * mm, "end": v(-13.3, 20.53) * mm});
            skLineSegment(sketch, "E686", {"start": v(-13.3, 20.53) * mm, "end": v(-13.45, 20.71) * mm});
            skLineSegment(sketch, "E687", {"start": v(-13.45, 20.71) * mm, "end": v(-13.6, 20.89) * mm});
            skLineSegment(sketch, "E688", {"start": v(-13.6, 20.89) * mm, "end": v(-13.76, 21.05) * mm});
            skLineSegment(sketch, "E689", {"start": v(-13.76, 21.05) * mm, "end": v(-13.94, 21.21) * mm});
            skLineSegment(sketch, "E690", {"start": v(-13.94, 21.21) * mm, "end": v(-14.12, 21.36) * mm});
            skLineSegment(sketch, "E691", {"start": v(-14.12, 21.36) * mm, "end": v(-14.3, 21.5) * mm});
            skLineSegment(sketch, "E692", {"start": v(-14.3, 21.5) * mm, "end": v(-14.5, 21.62) * mm});
            skLineSegment(sketch, "E693", {"start": v(-14.5, 21.62) * mm, "end": v(-14.7, 21.74) * mm});
            skLineSegment(sketch, "E694", {"start": v(-14.7, 21.74) * mm, "end": v(-14.92, 21.84) * mm});
            skLineSegment(sketch, "E695", {"start": v(-14.92, 21.84) * mm, "end": v(-15.13, 21.93) * mm});
            skLineSegment(sketch, "E696", {"start": v(-15.13, 21.93) * mm, "end": v(-15.35, 22) * mm});
            skLineSegment(sketch, "E697", {"start": v(-15.35, 22) * mm, "end": v(-15.45, 22.04) * mm});
            skLineSegment(sketch, "E698", {"start": v(-15.45, 22.04) * mm, "end": v(-15.47, 21.8) * mm});
            skLineSegment(sketch, "E699", {"start": v(-15.47, 21.8) * mm, "end": v(-15.48, 21.57) * mm});
            skLineSegment(sketch, "E700", {"start": v(-15.48, 21.57) * mm, "end": v(-15.48, 21.34) * mm});
            skLineSegment(sketch, "E701", {"start": v(-15.48, 21.34) * mm, "end": v(-15.46, 21.1) * mm});
            skLineSegment(sketch, "E702", {"start": v(-15.46, 21.1) * mm, "end": v(-15.43, 20.87) * mm});
            skLineSegment(sketch, "E703", {"start": v(-15.43, 20.87) * mm, "end": v(-15.39, 20.64) * mm});
            skLineSegment(sketch, "E704", {"start": v(-15.39, 20.64) * mm, "end": v(-15.33, 20.42) * mm});
            skLineSegment(sketch, "E705", {"start": v(-15.33, 20.42) * mm, "end": v(-15.26, 20.2) * mm});
            skLineSegment(sketch, "E706", {"start": v(-15.26, 20.2) * mm, "end": v(-15.18, 19.97) * mm});
            skLineSegment(sketch, "E707", {"start": v(-15.18, 19.97) * mm, "end": v(-15.08, 19.76) * mm});
            skLineSegment(sketch, "E708", {"start": v(-15.08, 19.76) * mm, "end": v(-14.98, 19.55) * mm});
            skLineSegment(sketch, "E709", {"start": v(-14.98, 19.55) * mm, "end": v(-14.86, 19.35) * mm});
            skLineSegment(sketch, "E710", {"start": v(-14.86, 19.35) * mm, "end": v(-14.73, 19.16) * mm});
            skLineSegment(sketch, "E711", {"start": v(-14.73, 19.16) * mm, "end": v(-14.6, 18.97) * mm});
            skLineSegment(sketch, "E712", {"start": v(-14.6, 18.97) * mm, "end": v(-14.46, 18.78) * mm});
            skLineSegment(sketch, "E713", {"start": v(-14.46, 18.78) * mm, "end": v(-14.33, 18.6) * mm});
            skLineSegment(sketch, "E714", {"start": v(-14.33, 18.6) * mm, "end": v(-14.2, 18.41) * mm});
            skLineSegment(sketch, "E715", {"start": v(-14.2, 18.41) * mm, "end": v(-14.07, 18.23) * mm});
            skLineSegment(sketch, "E716", {"start": v(-14.07, 18.23) * mm, "end": v(-13.93, 18.04) * mm});
            skLineSegment(sketch, "E717", {"start": v(-13.93, 18.04) * mm, "end": v(-13.8, 17.86) * mm});
            skLineSegment(sketch, "E718", {"start": v(-13.8, 17.86) * mm, "end": v(-13.67, 17.67) * mm});
            skLineSegment(sketch, "E719", {"start": v(-13.67, 17.67) * mm, "end": v(-13.62, 17.6) * mm});
            skLineSegment(sketch, "E720", {"start": v(-13.62, 17.6) * mm, "end": v(-13.8, 17.45) * mm});
            skLineSegment(sketch, "E721", {"start": v(-13.8, 17.45) * mm, "end": v(-13.98, 17.3) * mm});
            skLineSegment(sketch, "E722", {"start": v(-13.98, 17.3) * mm, "end": v(-14.17, 17.17) * mm});
            skLineSegment(sketch, "E723", {"start": v(-14.17, 17.17) * mm, "end": v(-14.35, 17.02) * mm});
            skLineSegment(sketch, "E724", {"start": v(-14.35, 17.02) * mm, "end": v(-14.54, 16.88) * mm});
            skLineSegment(sketch, "E725", {"start": v(-14.54, 16.88) * mm, "end": v(-14.72, 16.73) * mm});
            skLineSegment(sketch, "E726", {"start": v(-14.72, 16.73) * mm, "end": v(-14.9, 16.6) * mm});
            skLineSegment(sketch, "E727", {"start": v(-14.9, 16.6) * mm, "end": v(-15.03, 16.5) * mm});
            skLineSegment(sketch, "E728", {"start": v(-15.03, 16.5) * mm, "end": v(-15.18, 16.68) * mm});
            skLineSegment(sketch, "E729", {"start": v(-15.18, 16.68) * mm, "end": v(-15.32, 16.85) * mm});
            skLineSegment(sketch, "E730", {"start": v(-15.32, 16.85) * mm, "end": v(-15.47, 17.02) * mm});
            skLineSegment(sketch, "E731", {"start": v(-15.47, 17.02) * mm, "end": v(-15.61, 17.2) * mm});
            skLineSegment(sketch, "E732", {"start": v(-15.61, 17.2) * mm, "end": v(-15.76, 17.37) * mm});
            skLineSegment(sketch, "E733", {"start": v(-15.76, 17.37) * mm, "end": v(-15.9, 17.54) * mm});
            skLineSegment(sketch, "E734", {"start": v(-15.9, 17.54) * mm, "end": v(-16.06, 17.72) * mm});
            skLineSegment(sketch, "E735", {"start": v(-16.06, 17.72) * mm, "end": v(-16.2, 17.89) * mm});
            skLineSegment(sketch, "E736", {"start": v(-16.2, 17.89) * mm, "end": v(-16.35, 18.06) * mm});
            skLineSegment(sketch, "E737", {"start": v(-16.35, 18.06) * mm, "end": v(-16.51, 18.23) * mm});
            skLineSegment(sketch, "E738", {"start": v(-16.51, 18.23) * mm, "end": v(-16.69, 18.39) * mm});
            skLineSegment(sketch, "E739", {"start": v(-16.69, 18.39) * mm, "end": v(-16.87, 18.54) * mm});
            skLineSegment(sketch, "E740", {"start": v(-16.87, 18.54) * mm, "end": v(-17.06, 18.68) * mm});
            skLineSegment(sketch, "E741", {"start": v(-17.06, 18.68) * mm, "end": v(-17.25, 18.8) * mm});
            skLineSegment(sketch, "E742", {"start": v(-17.25, 18.8) * mm, "end": v(-17.45, 18.92) * mm});
            skLineSegment(sketch, "E743", {"start": v(-17.45, 18.92) * mm, "end": v(-17.66, 19.02) * mm});
            skLineSegment(sketch, "E744", {"start": v(-17.66, 19.02) * mm, "end": v(-17.88, 19.11) * mm});
            skLineSegment(sketch, "E745", {"start": v(-17.88, 19.11) * mm, "end": v(-18.1, 19.2) * mm});
            skLineSegment(sketch, "E746", {"start": v(-18.1, 19.2) * mm, "end": v(-18.32, 19.26) * mm});
            skLineSegment(sketch, "E747", {"start": v(-18.32, 19.26) * mm, "end": v(-18.55, 19.31) * mm});
            skLineSegment(sketch, "E748", {"start": v(-18.55, 19.31) * mm, "end": v(-18.78, 19.35) * mm});
            skLineSegment(sketch, "E749", {"start": v(-18.78, 19.35) * mm, "end": v(-18.88, 19.37) * mm});
            skLineSegment(sketch, "E750", {"start": v(-18.88, 19.37) * mm, "end": v(-18.86, 19.13) * mm});
            skLineSegment(sketch, "E751", {"start": v(-18.86, 19.13) * mm, "end": v(-18.84, 18.9) * mm});
            skLineSegment(sketch, "E752", {"start": v(-18.84, 18.9) * mm, "end": v(-18.8, 18.67) * mm});
            skLineSegment(sketch, "E753", {"start": v(-18.8, 18.67) * mm, "end": v(-18.74, 18.44) * mm});
            skLineSegment(sketch, "E754", {"start": v(-18.74, 18.44) * mm, "end": v(-18.67, 18.22) * mm});
            skLineSegment(sketch, "E755", {"start": v(-18.67, 18.22) * mm, "end": v(-18.6, 18) * mm});
            skLineSegment(sketch, "E756", {"start": v(-18.6, 18) * mm, "end": v(-18.5, 17.79) * mm});
            skLineSegment(sketch, "E757", {"start": v(-18.5, 17.79) * mm, "end": v(-18.4, 17.58) * mm});
            skLineSegment(sketch, "E758", {"start": v(-18.4, 17.58) * mm, "end": v(-18.27, 17.38) * mm});
            skLineSegment(sketch, "E759", {"start": v(-18.27, 17.38) * mm, "end": v(-18.14, 17.18) * mm});
            skLineSegment(sketch, "E760", {"start": v(-18.14, 17.18) * mm, "end": v(-18, 17) * mm});
            skLineSegment(sketch, "E761", {"start": v(-18, 17) * mm, "end": v(-17.86, 16.81) * mm});
            skLineSegment(sketch, "E762", {"start": v(-17.86, 16.81) * mm, "end": v(-17.7, 16.64) * mm});
            skLineSegment(sketch, "E763", {"start": v(-17.7, 16.64) * mm, "end": v(-17.53, 16.48) * mm});
            skLineSegment(sketch, "E764", {"start": v(-17.53, 16.48) * mm, "end": v(-17.37, 16.32) * mm});
            skLineSegment(sketch, "E765", {"start": v(-17.37, 16.32) * mm, "end": v(-17.21, 16.16) * mm});
            skLineSegment(sketch, "E766", {"start": v(-17.21, 16.16) * mm, "end": v(-17.05, 16) * mm});
            skLineSegment(sketch, "E767", {"start": v(-17.05, 16) * mm, "end": v(-16.9, 15.84) * mm});
            skLineSegment(sketch, "E768", {"start": v(-16.9, 15.84) * mm, "end": v(-16.73, 15.67) * mm});
            skLineSegment(sketch, "E769", {"start": v(-16.73, 15.67) * mm, "end": v(-16.57, 15.52) * mm});
            skLineSegment(sketch, "E770", {"start": v(-16.57, 15.52) * mm, "end": v(-16.4, 15.35) * mm});
            skLineSegment(sketch, "E771", {"start": v(-16.4, 15.35) * mm, "end": v(-16.34, 15.29) * mm});
            skLineSegment(sketch, "E772", {"start": v(-16.34, 15.29) * mm, "end": v(-16.5, 15.12) * mm});
            skLineSegment(sketch, "E773", {"start": v(-16.5, 15.12) * mm, "end": v(-16.66, 14.94) * mm});
            skLineSegment(sketch, "E774", {"start": v(-16.66, 14.94) * mm, "end": v(-16.82, 14.77) * mm});
            skLineSegment(sketch, "E775", {"start": v(-16.82, 14.77) * mm, "end": v(-16.97, 14.6) * mm});
            skLineSegment(sketch, "E776", {"start": v(-16.97, 14.6) * mm, "end": v(-17.13, 14.43) * mm});
            skLineSegment(sketch, "E777", {"start": v(-17.13, 14.43) * mm, "end": v(-17.3, 14.26) * mm});
            skLineSegment(sketch, "E778", {"start": v(-17.3, 14.26) * mm, "end": v(-17.45, 14.08) * mm});
            skLineSegment(sketch, "E779", {"start": v(-17.45, 14.08) * mm, "end": v(-17.55, 13.97) * mm});
            skLineSegment(sketch, "E780", {"start": v(-17.55, 13.97) * mm, "end": v(-17.73, 14.13) * mm});
            skLineSegment(sketch, "E781", {"start": v(-17.73, 14.13) * mm, "end": v(-17.9, 14.27) * mm});
            skLineSegment(sketch, "E782", {"start": v(-17.9, 14.27) * mm, "end": v(-18.08, 14.42) * mm});
            skLineSegment(sketch, "E783", {"start": v(-18.08, 14.42) * mm, "end": v(-18.24, 14.56) * mm});
            skLineSegment(sketch, "E784", {"start": v(-18.24, 14.56) * mm, "end": v(-18.42, 14.71) * mm});
            skLineSegment(sketch, "E785", {"start": v(-18.42, 14.71) * mm, "end": v(-18.6, 14.86) * mm});
            skLineSegment(sketch, "E786", {"start": v(-18.6, 14.86) * mm, "end": v(-18.77, 15) * mm});
            skLineSegment(sketch, "E787", {"start": v(-18.77, 15) * mm, "end": v(-18.94, 15.15) * mm});
            skLineSegment(sketch, "E788", {"start": v(-18.94, 15.15) * mm, "end": v(-19.12, 15.3) * mm});
            skLineSegment(sketch, "E789", {"start": v(-19.12, 15.3) * mm, "end": v(-19.3, 15.44) * mm});
            skLineSegment(sketch, "E790", {"start": v(-19.3, 15.44) * mm, "end": v(-19.5, 15.56) * mm});
            skLineSegment(sketch, "E791", {"start": v(-19.5, 15.56) * mm, "end": v(-19.7, 15.68) * mm});
            skLineSegment(sketch, "E792", {"start": v(-19.7, 15.68) * mm, "end": v(-19.91, 15.79) * mm});
            skLineSegment(sketch, "E793", {"start": v(-19.91, 15.79) * mm, "end": v(-20.13, 15.88) * mm});
            skLineSegment(sketch, "E794", {"start": v(-20.13, 15.88) * mm, "end": v(-20.34, 15.96) * mm});
            skLineSegment(sketch, "E795", {"start": v(-20.34, 15.96) * mm, "end": v(-20.57, 16.03) * mm});
            skLineSegment(sketch, "E796", {"start": v(-20.57, 16.03) * mm, "end": v(-20.8, 16.08) * mm});
            skLineSegment(sketch, "E797", {"start": v(-20.8, 16.08) * mm, "end": v(-21.03, 16.13) * mm});
            skLineSegment(sketch, "E798", {"start": v(-21.03, 16.13) * mm, "end": v(-21.26, 16.15) * mm});
            skLineSegment(sketch, "E799", {"start": v(-21.26, 16.15) * mm, "end": v(-21.5, 16.17) * mm});
            skLineSegment(sketch, "E800", {"start": v(-21.5, 16.17) * mm, "end": v(-21.63, 16.17) * mm});
            skLineSegment(sketch, "E801", {"start": v(-21.63, 16.17) * mm, "end": v(-21.83, 16.17) * mm});
            skLineSegment(sketch, "E802", {"start": v(-21.83, 16.17) * mm, "end": v(-21.77, 15.94) * mm});
            skLineSegment(sketch, "E803", {"start": v(-21.77, 15.94) * mm, "end": v(-21.7, 15.72) * mm});
            skLineSegment(sketch, "E804", {"start": v(-21.7, 15.72) * mm, "end": v(-21.63, 15.5) * mm});
            skLineSegment(sketch, "E805", {"start": v(-21.63, 15.5) * mm, "end": v(-21.53, 15.28) * mm});
            skLineSegment(sketch, "E806", {"start": v(-21.53, 15.28) * mm, "end": v(-21.43, 15.07) * mm});
            skLineSegment(sketch, "E807", {"start": v(-21.43, 15.07) * mm, "end": v(-21.31, 14.87) * mm});
            skLineSegment(sketch, "E808", {"start": v(-21.31, 14.87) * mm, "end": v(-21.19, 14.67) * mm});
            skLineSegment(sketch, "E809", {"start": v(-21.19, 14.67) * mm, "end": v(-21.05, 14.48) * mm});
            skLineSegment(sketch, "E810", {"start": v(-21.05, 14.48) * mm, "end": v(-20.9, 14.3) * mm});
            skLineSegment(sketch, "E811", {"start": v(-20.9, 14.3) * mm, "end": v(-20.74, 14.13) * mm});
            skLineSegment(sketch, "E812", {"start": v(-20.74, 14.13) * mm, "end": v(-20.57, 13.97) * mm});
            skLineSegment(sketch, "E813", {"start": v(-20.57, 13.97) * mm, "end": v(-20.4, 13.82) * mm});
            skLineSegment(sketch, "E814", {"start": v(-20.4, 13.82) * mm, "end": v(-20.2, 13.68) * mm});
            skLineSegment(sketch, "E815", {"start": v(-20.2, 13.68) * mm, "end": v(-20.02, 13.55) * mm});
            skLineSegment(sketch, "E816", {"start": v(-20.02, 13.55) * mm, "end": v(-19.83, 13.4) * mm});
            skLineSegment(sketch, "E817", {"start": v(-19.83, 13.4) * mm, "end": v(-19.65, 13.28) * mm});
            skLineSegment(sketch, "E818", {"start": v(-19.65, 13.28) * mm, "end": v(-19.46, 13.14) * mm});
            skLineSegment(sketch, "E819", {"start": v(-19.46, 13.14) * mm, "end": v(-19.28, 13.02) * mm});
            skLineSegment(sketch, "E820", {"start": v(-19.28, 13.02) * mm, "end": v(-19.1, 12.88) * mm});
            skLineSegment(sketch, "E821", {"start": v(-19.1, 12.88) * mm, "end": v(-18.91, 12.75) * mm});
            skLineSegment(sketch, "E822", {"start": v(-18.91, 12.75) * mm, "end": v(-18.72, 12.62) * mm});
            skLineSegment(sketch, "E823", {"start": v(-18.72, 12.62) * mm, "end": v(-18.65, 12.56) * mm});
            skLineSegment(sketch, "E824", {"start": v(-18.65, 12.56) * mm, "end": v(-18.78, 12.37) * mm});
            skLineSegment(sketch, "E825", {"start": v(-18.78, 12.37) * mm, "end": v(-18.9, 12.17) * mm});
            skLineSegment(sketch, "E826", {"start": v(-18.9, 12.17) * mm, "end": v(-19.03, 11.98) * mm});
            skLineSegment(sketch, "E827", {"start": v(-19.03, 11.98) * mm, "end": v(-19.16, 11.78) * mm});
            skLineSegment(sketch, "E828", {"start": v(-19.16, 11.78) * mm, "end": v(-19.29, 11.58) * mm});
            skLineSegment(sketch, "E829", {"start": v(-19.29, 11.58) * mm, "end": v(-19.42, 11.39) * mm});
            skLineSegment(sketch, "E830", {"start": v(-19.42, 11.39) * mm, "end": v(-19.54, 11.2) * mm});
            skLineSegment(sketch, "E831", {"start": v(-19.54, 11.2) * mm, "end": v(-19.63, 11.07) * mm});
            skLineSegment(sketch, "E832", {"start": v(-19.63, 11.07) * mm, "end": v(-19.83, 11.19) * mm});
            skLineSegment(sketch, "E833", {"start": v(-19.83, 11.19) * mm, "end": v(-20.02, 11.3) * mm});
            skLineSegment(sketch, "E834", {"start": v(-20.02, 11.3) * mm, "end": v(-20.22, 11.42) * mm});
            skLineSegment(sketch, "E835", {"start": v(-20.22, 11.42) * mm, "end": v(-20.4, 11.53) * mm});
            skLineSegment(sketch, "E836", {"start": v(-20.4, 11.53) * mm, "end": v(-20.6, 11.65) * mm});
            skLineSegment(sketch, "E837", {"start": v(-20.6, 11.65) * mm, "end": v(-20.8, 11.77) * mm});
            skLineSegment(sketch, "E838", {"start": v(-20.8, 11.77) * mm, "end": v(-21, 11.89) * mm});
            skLineSegment(sketch, "E839", {"start": v(-21, 11.89) * mm, "end": v(-21.19, 12) * mm});
            skLineSegment(sketch, "E840", {"start": v(-21.19, 12) * mm, "end": v(-21.39, 12.11) * mm});
            skLineSegment(sketch, "E841", {"start": v(-21.39, 12.11) * mm, "end": v(-21.6, 12.22) * mm});
            skLineSegment(sketch, "E842", {"start": v(-21.6, 12.22) * mm, "end": v(-21.8, 12.32) * mm});
            skLineSegment(sketch, "E843", {"start": v(-21.8, 12.32) * mm, "end": v(-22.03, 12.4) * mm});
            skLineSegment(sketch, "E844", {"start": v(-22.03, 12.4) * mm, "end": v(-22.25, 12.47) * mm});
            skLineSegment(sketch, "E845", {"start": v(-22.25, 12.47) * mm, "end": v(-22.48, 12.52) * mm});
            skLineSegment(sketch, "E846", {"start": v(-22.48, 12.52) * mm, "end": v(-22.7, 12.57) * mm});
            skLineSegment(sketch, "E847", {"start": v(-22.7, 12.57) * mm, "end": v(-22.94, 12.6) * mm});
            skLineSegment(sketch, "E848", {"start": v(-22.94, 12.6) * mm, "end": v(-23.17, 12.62) * mm});
            skLineSegment(sketch, "E849", {"start": v(-23.17, 12.62) * mm, "end": v(-23.3, 12.62) * mm});
            skLineSegment(sketch, "E850", {"start": v(-23.3, 12.62) * mm, "end": v(-23.54, 12.61) * mm});
            skLineSegment(sketch, "E851", {"start": v(-23.54, 12.61) * mm, "end": v(-23.77, 12.6) * mm});
            skLineSegment(sketch, "E852", {"start": v(-23.77, 12.6) * mm, "end": v(-24, 12.57) * mm});
            skLineSegment(sketch, "E853", {"start": v(-24, 12.57) * mm, "end": v(-24.2, 12.53) * mm});
            skLineSegment(sketch, "E854", {"start": v(-24.2, 12.53) * mm, "end": v(-24.11, 12.31) * mm});
            skLineSegment(sketch, "E855", {"start": v(-24.11, 12.31) * mm, "end": v(-24, 12.1) * mm});
            skLineSegment(sketch, "E856", {"start": v(-24, 12.1) * mm, "end": v(-23.9, 11.9) * mm});
            skLineSegment(sketch, "E857", {"start": v(-23.9, 11.9) * mm, "end": v(-23.77, 11.7) * mm});
            skLineSegment(sketch, "E858", {"start": v(-23.77, 11.7) * mm, "end": v(-23.63, 11.51) * mm});
            skLineSegment(sketch, "E859", {"start": v(-23.63, 11.51) * mm, "end": v(-23.49, 11.33) * mm});
            skLineSegment(sketch, "E860", {"start": v(-23.49, 11.33) * mm, "end": v(-23.33, 11.16) * mm});
            skLineSegment(sketch, "E861", {"start": v(-23.33, 11.16) * mm, "end": v(-23.16, 11) * mm});
            skLineSegment(sketch, "E862", {"start": v(-23.16, 11) * mm, "end": v(-22.98, 10.84) * mm});
            skLineSegment(sketch, "E863", {"start": v(-22.98, 10.84) * mm, "end": v(-22.8, 10.7) * mm});
            skLineSegment(sketch, "E864", {"start": v(-22.8, 10.7) * mm, "end": v(-22.6, 10.57) * mm});
            skLineSegment(sketch, "E865", {"start": v(-22.6, 10.57) * mm, "end": v(-22.4, 10.45) * mm});
            skLineSegment(sketch, "E866", {"start": v(-22.4, 10.45) * mm, "end": v(-22.2, 10.34) * mm});
            skLineSegment(sketch, "E867", {"start": v(-22.2, 10.34) * mm, "end": v(-22, 10.24) * mm});
            skLineSegment(sketch, "E868", {"start": v(-22, 10.24) * mm, "end": v(-21.78, 10.14) * mm});
            skLineSegment(sketch, "E869", {"start": v(-21.78, 10.14) * mm, "end": v(-21.59, 10.04) * mm});
            skLineSegment(sketch, "E870", {"start": v(-21.59, 10.04) * mm, "end": v(-21.37, 9.94) * mm});
            skLineSegment(sketch, "E871", {"start": v(-21.37, 9.94) * mm, "end": v(-21.18, 9.84) * mm});
            skLineSegment(sketch, "E872", {"start": v(-21.18, 9.84) * mm, "end": v(-20.97, 9.74) * mm});
            skLineSegment(sketch, "E873", {"start": v(-20.97, 9.74) * mm, "end": v(-20.77, 9.64) * mm});
            skLineSegment(sketch, "E874", {"start": v(-20.77, 9.64) * mm, "end": v(-20.56, 9.54) * mm});
            skLineSegment(sketch, "E875", {"start": v(-20.56, 9.54) * mm, "end": v(-20.48, 9.5) * mm});
            skLineSegment(sketch, "E876", {"start": v(-20.48, 9.5) * mm, "end": v(-20.57, 9.28) * mm});
            skLineSegment(sketch, "E877", {"start": v(-20.57, 9.28) * mm, "end": v(-20.66, 9.07) * mm});
            skLineSegment(sketch, "E878", {"start": v(-20.66, 9.07) * mm, "end": v(-20.76, 8.85) * mm});
            skLineSegment(sketch, "E879", {"start": v(-20.76, 8.85) * mm, "end": v(-20.85, 8.64) * mm});
            skLineSegment(sketch, "E880", {"start": v(-20.85, 8.64) * mm, "end": v(-20.95, 8.42) * mm});
            skLineSegment(sketch, "E881", {"start": v(-20.95, 8.42) * mm, "end": v(-21.04, 8.21) * mm});
            skLineSegment(sketch, "E882", {"start": v(-21.04, 8.21) * mm, "end": v(-21.13, 8) * mm});
            skLineSegment(sketch, "E883", {"start": v(-21.13, 8) * mm, "end": v(-21.2, 7.86) * mm});
            skLineSegment(sketch, "E884", {"start": v(-21.2, 7.86) * mm, "end": v(-21.41, 7.94) * mm});
            skLineSegment(sketch, "E885", {"start": v(-21.41, 7.94) * mm, "end": v(-21.62, 8.02) * mm});
            skLineSegment(sketch, "E886", {"start": v(-21.62, 8.02) * mm, "end": v(-21.84, 8.1) * mm});
            skLineSegment(sketch, "E887", {"start": v(-21.84, 8.1) * mm, "end": v(-22.04, 8.2) * mm});
            skLineSegment(sketch, "E888", {"start": v(-22.04, 8.2) * mm, "end": v(-22.26, 8.28) * mm});
            skLineSegment(sketch, "E889", {"start": v(-22.26, 8.28) * mm, "end": v(-22.46, 8.36) * mm});
            skLineSegment(sketch, "E890", {"start": v(-22.46, 8.36) * mm, "end": v(-22.68, 8.44) * mm});
            skLineSegment(sketch, "E891", {"start": v(-22.68, 8.44) * mm, "end": v(-22.89, 8.52) * mm});
            skLineSegment(sketch, "E892", {"start": v(-22.89, 8.52) * mm, "end": v(-23.1, 8.6) * mm});
            skLineSegment(sketch, "E893", {"start": v(-23.1, 8.6) * mm, "end": v(-23.33, 8.67) * mm});
            skLineSegment(sketch, "E894", {"start": v(-23.33, 8.67) * mm, "end": v(-23.55, 8.73) * mm});
            skLineSegment(sketch, "E895", {"start": v(-23.55, 8.73) * mm, "end": v(-23.78, 8.78) * mm});
            skLineSegment(sketch, "E896", {"start": v(-23.78, 8.78) * mm, "end": v(-24.01, 8.8) * mm});
            skLineSegment(sketch, "E897", {"start": v(-24.01, 8.8) * mm, "end": v(-24.25, 8.83) * mm});
            skLineSegment(sketch, "E898", {"start": v(-24.25, 8.83) * mm, "end": v(-24.48, 8.83) * mm});
            skLineSegment(sketch, "E899", {"start": v(-24.48, 8.83) * mm, "end": v(-24.72, 8.82) * mm});
            skLineSegment(sketch, "E900", {"start": v(-24.72, 8.82) * mm, "end": v(-24.95, 8.8) * mm});
            skLineSegment(sketch, "E901", {"start": v(-24.95, 8.8) * mm, "end": v(-25.18, 8.77) * mm});
            skLineSegment(sketch, "E902", {"start": v(-25.18, 8.77) * mm, "end": v(-25.4, 8.72) * mm});
            skLineSegment(sketch, "E903", {"start": v(-25.4, 8.72) * mm, "end": v(-25.63, 8.66) * mm});
            skLineSegment(sketch, "E904", {"start": v(-25.63, 8.66) * mm, "end": v(-25.86, 8.58) * mm});
            skLineSegment(sketch, "E905", {"start": v(-25.86, 8.58) * mm, "end": v(-25.95, 8.55) * mm});
            skLineSegment(sketch, "E906", {"start": v(-25.95, 8.55) * mm, "end": v(-25.82, 8.35) * mm});
            skLineSegment(sketch, "E907", {"start": v(-25.82, 8.35) * mm, "end": v(-25.69, 8.16) * mm});
            skLineSegment(sketch, "E908", {"start": v(-25.69, 8.16) * mm, "end": v(-25.54, 7.98) * mm});
            skLineSegment(sketch, "E909", {"start": v(-25.54, 7.98) * mm, "end": v(-25.39, 7.8) * mm});
            skLineSegment(sketch, "E910", {"start": v(-25.39, 7.8) * mm, "end": v(-25.22, 7.64) * mm});
            skLineSegment(sketch, "E911", {"start": v(-25.22, 7.64) * mm, "end": v(-25.04, 7.48) * mm});
            skLineSegment(sketch, "E912", {"start": v(-25.04, 7.48) * mm, "end": v(-24.86, 7.34) * mm});
            skLineSegment(sketch, "E913", {"start": v(-24.86, 7.34) * mm, "end": v(-24.67, 7.2) * mm});
            skLineSegment(sketch, "E914", {"start": v(-24.67, 7.2) * mm, "end": v(-24.47, 7.08) * mm});
            skLineSegment(sketch, "E915", {"start": v(-24.47, 7.08) * mm, "end": v(-24.26, 6.97) * mm});
            skLineSegment(sketch, "E916", {"start": v(-24.26, 6.97) * mm, "end": v(-24.05, 6.88) * mm});
            skLineSegment(sketch, "E917", {"start": v(-24.05, 6.88) * mm, "end": v(-23.83, 6.79) * mm});
            skLineSegment(sketch, "E918", {"start": v(-23.83, 6.79) * mm, "end": v(-23.6, 6.72) * mm});
            skLineSegment(sketch, "E919", {"start": v(-23.6, 6.72) * mm, "end": v(-23.4, 6.65) * mm});
            skLineSegment(sketch, "E920", {"start": v(-23.4, 6.65) * mm, "end": v(-23.17, 6.58) * mm});
            skLineSegment(sketch, "E921", {"start": v(-23.17, 6.58) * mm, "end": v(-22.96, 6.52) * mm});
            skLineSegment(sketch, "E922", {"start": v(-22.96, 6.52) * mm, "end": v(-22.73, 6.45) * mm});
            skLineSegment(sketch, "E923", {"start": v(-22.73, 6.45) * mm, "end": v(-22.52, 6.4) * mm});
            skLineSegment(sketch, "E924", {"start": v(-22.52, 6.4) * mm, "end": v(-22.3, 6.33) * mm});
            skLineSegment(sketch, "E925", {"start": v(-22.3, 6.33) * mm, "end": v(-22.09, 6.26) * mm});
            skLineSegment(sketch, "E926", {"start": v(-22.09, 6.26) * mm, "end": v(-21.86, 6.2) * mm});
            skLineSegment(sketch, "E927", {"start": v(-21.86, 6.2) * mm, "end": v(-21.77, 6.17) * mm});
            skLineSegment(sketch, "E928", {"start": v(-21.77, 6.17) * mm, "end": v(-21.83, 5.94) * mm});
            skLineSegment(sketch, "E929", {"start": v(-21.83, 5.94) * mm, "end": v(-21.89, 5.72) * mm});
            skLineSegment(sketch, "E930", {"start": v(-21.89, 5.72) * mm, "end": v(-21.95, 5.49) * mm});
            skLineSegment(sketch, "E931", {"start": v(-21.95, 5.49) * mm, "end": v(-22, 5.26) * mm});
            skLineSegment(sketch, "E932", {"start": v(-22, 5.26) * mm, "end": v(-22.06, 5.04) * mm});
            skLineSegment(sketch, "E933", {"start": v(-22.06, 5.04) * mm, "end": v(-22.12, 4.8) * mm});
            skLineSegment(sketch, "E934", {"start": v(-22.12, 4.8) * mm, "end": v(-22.18, 4.58) * mm});
            skLineSegment(sketch, "E935", {"start": v(-22.18, 4.58) * mm, "end": v(-22.21, 4.44) * mm});
            skLineSegment(sketch, "E936", {"start": v(-22.21, 4.44) * mm, "end": v(-22.44, 4.49) * mm});
            skLineSegment(sketch, "E937", {"start": v(-22.44, 4.49) * mm, "end": v(-22.66, 4.53) * mm});
            skLineSegment(sketch, "E938", {"start": v(-22.66, 4.53) * mm, "end": v(-22.89, 4.58) * mm});
            skLineSegment(sketch, "E939", {"start": v(-22.89, 4.58) * mm, "end": v(-23.1, 4.62) * mm});
            skLineSegment(sketch, "E940", {"start": v(-23.1, 4.62) * mm, "end": v(-23.33, 4.67) * mm});
            skLineSegment(sketch, "E941", {"start": v(-23.33, 4.67) * mm, "end": v(-23.55, 4.72) * mm});
            skLineSegment(sketch, "E942", {"start": v(-23.55, 4.72) * mm, "end": v(-23.78, 4.77) * mm});
            skLineSegment(sketch, "E943", {"start": v(-23.78, 4.77) * mm, "end": v(-24, 4.81) * mm});
            skLineSegment(sketch, "E944", {"start": v(-24, 4.81) * mm, "end": v(-24.22, 4.86) * mm});
            skLineSegment(sketch, "E945", {"start": v(-24.22, 4.86) * mm, "end": v(-24.45, 4.89) * mm});
            skLineSegment(sketch, "E946", {"start": v(-24.45, 4.89) * mm, "end": v(-24.68, 4.9) * mm});
            skLineSegment(sketch, "E947", {"start": v(-24.68, 4.9) * mm, "end": v(-24.92, 4.92) * mm});
            skLineSegment(sketch, "E948", {"start": v(-24.92, 4.92) * mm, "end": v(-25.15, 4.9) * mm});
            skLineSegment(sketch, "E949", {"start": v(-25.15, 4.9) * mm, "end": v(-25.38, 4.89) * mm});
            skLineSegment(sketch, "E950", {"start": v(-25.38, 4.89) * mm, "end": v(-25.62, 4.86) * mm});
            skLineSegment(sketch, "E951", {"start": v(-25.62, 4.86) * mm, "end": v(-25.85, 4.8) * mm});
            skLineSegment(sketch, "E952", {"start": v(-25.85, 4.8) * mm, "end": v(-26.07, 4.75) * mm});
            skLineSegment(sketch, "E953", {"start": v(-26.07, 4.75) * mm, "end": v(-26.3, 4.68) * mm});
            skLineSegment(sketch, "E954", {"start": v(-26.3, 4.68) * mm, "end": v(-26.51, 4.59) * mm});
            skLineSegment(sketch, "E955", {"start": v(-26.51, 4.59) * mm, "end": v(-26.72, 4.5) * mm});
            skLineSegment(sketch, "E956", {"start": v(-26.72, 4.5) * mm, "end": v(-26.93, 4.38) * mm});
            skLineSegment(sketch, "E957", {"start": v(-26.93, 4.38) * mm, "end": v(-27.02, 4.33) * mm});
            skLineSegment(sketch, "E958", {"start": v(-27.02, 4.33) * mm, "end": v(-26.86, 4.16) * mm});
            skLineSegment(sketch, "E959", {"start": v(-26.86, 4.16) * mm, "end": v(-26.7, 4) * mm});
            skLineSegment(sketch, "E960", {"start": v(-26.7, 4) * mm, "end": v(-26.52, 3.84) * mm});
            skLineSegment(sketch, "E961", {"start": v(-26.52, 3.84) * mm, "end": v(-26.34, 3.7) * mm});
            skLineSegment(sketch, "E962", {"start": v(-26.34, 3.7) * mm, "end": v(-26.15, 3.56) * mm});
            skLineSegment(sketch, "E963", {"start": v(-26.15, 3.56) * mm, "end": v(-25.95, 3.43) * mm});
            skLineSegment(sketch, "E964", {"start": v(-25.95, 3.43) * mm, "end": v(-25.74, 3.32) * mm});
            skLineSegment(sketch, "E965", {"start": v(-25.74, 3.32) * mm, "end": v(-25.53, 3.22) * mm});
            skLineSegment(sketch, "E966", {"start": v(-25.53, 3.22) * mm, "end": v(-25.32, 3.13) * mm});
            skLineSegment(sketch, "E967", {"start": v(-25.32, 3.13) * mm, "end": v(-25.1, 3.06) * mm});
            skLineSegment(sketch, "E968", {"start": v(-25.1, 3.06) * mm, "end": v(-24.87, 3) * mm});
            skLineSegment(sketch, "E969", {"start": v(-24.87, 3) * mm, "end": v(-24.64, 2.95) * mm});
            skLineSegment(sketch, "E970", {"start": v(-24.64, 2.95) * mm, "end": v(-24.4, 2.91) * mm});
            skLineSegment(sketch, "E971", {"start": v(-24.4, 2.91) * mm, "end": v(-24.18, 2.88) * mm});
            skLineSegment(sketch, "E972", {"start": v(-24.18, 2.88) * mm, "end": v(-23.95, 2.85) * mm});
            skLineSegment(sketch, "E973", {"start": v(-23.95, 2.85) * mm, "end": v(-23.73, 2.83) * mm});
            skLineSegment(sketch, "E974", {"start": v(-23.73, 2.83) * mm, "end": v(-23.5, 2.8) * mm});
            skLineSegment(sketch, "E975", {"start": v(-23.5, 2.8) * mm, "end": v(-23.28, 2.77) * mm});
            skLineSegment(sketch, "E976", {"start": v(-23.28, 2.77) * mm, "end": v(-23.05, 2.74) * mm});
            skLineSegment(sketch, "E977", {"start": v(-23.05, 2.74) * mm, "end": v(-22.83, 2.71) * mm});
            skLineSegment(sketch, "E978", {"start": v(-22.83, 2.71) * mm, "end": v(-22.6, 2.69) * mm});
            skLineSegment(sketch, "E979", {"start": v(-22.6, 2.69) * mm, "end": v(-22.5, 2.67) * mm});
            skLineSegment(sketch, "E980", {"start": v(-22.5, 2.67) * mm, "end": v(-22.53, 2.44) * mm});
            skLineSegment(sketch, "E981", {"start": v(-22.53, 2.44) * mm, "end": v(-22.55, 2.2) * mm});
            skLineSegment(sketch, "E982", {"start": v(-22.55, 2.2) * mm, "end": v(-22.57, 1.97) * mm});
            skLineSegment(sketch, "E983", {"start": v(-22.57, 1.97) * mm, "end": v(-22.58, 1.74) * mm});
            skLineSegment(sketch, "E984", {"start": v(-22.58, 1.74) * mm, "end": v(-22.6, 1.5) * mm});
            skLineSegment(sketch, "E985", {"start": v(-22.6, 1.5) * mm, "end": v(-22.62, 1.27) * mm});
            skLineSegment(sketch, "E986", {"start": v(-22.62, 1.27) * mm, "end": v(-22.64, 1.04) * mm});
            skLineSegment(sketch, "E987", {"start": v(-22.64, 1.04) * mm, "end": v(-22.65, 0.9) * mm});
            skLineSegment(sketch, "E988", {"start": v(-22.65, 0.9) * mm, "end": v(-22.89, 0.9) * mm});
            skLineSegment(sketch, "E989", {"start": v(-22.89, 0.9) * mm, "end": v(-23.1, 0.91) * mm});
            skLineSegment(sketch, "E990", {"start": v(-23.1, 0.91) * mm, "end": v(-23.34, 0.92) * mm});
            skLineSegment(sketch, "E991", {"start": v(-23.34, 0.92) * mm, "end": v(-23.56, 0.93) * mm});
            skLineSegment(sketch, "E992", {"start": v(-23.56, 0.93) * mm, "end": v(-23.8, 0.94) * mm});
            skLineSegment(sketch, "E993", {"start": v(-23.8, 0.94) * mm, "end": v(-24.02, 0.95) * mm});
            skLineSegment(sketch, "E994", {"start": v(-24.02, 0.95) * mm, "end": v(-24.25, 0.96) * mm});
            skLineSegment(sketch, "E995", {"start": v(-24.25, 0.96) * mm, "end": v(-24.47, 0.97) * mm});
            skLineSegment(sketch, "E996", {"start": v(-24.47, 0.97) * mm, "end": v(-24.7, 0.98) * mm});
            skLineSegment(sketch, "E997", {"start": v(-24.7, 0.98) * mm, "end": v(-24.94, 0.97) * mm});
            skLineSegment(sketch, "E998", {"start": v(-24.94, 0.97) * mm, "end": v(-25.17, 0.95) * mm});
            skLineSegment(sketch, "E999", {"start": v(-25.17, 0.95) * mm, "end": v(-25.4, 0.92) * mm});
            skLineSegment(sketch, "E1000", {"start": v(-25.4, 0.92) * mm, "end": v(-25.63, 0.87) * mm});
            skLineSegment(sketch, "E1001", {"start": v(-25.63, 0.87) * mm, "end": v(-25.86, 0.82) * mm});
            skLineSegment(sketch, "E1002", {"start": v(-25.86, 0.82) * mm, "end": v(-26.08, 0.75) * mm});
            skLineSegment(sketch, "E1003", {"start": v(-26.08, 0.75) * mm, "end": v(-26.3, 0.66) * mm});
            skLineSegment(sketch, "E1004", {"start": v(-26.3, 0.66) * mm, "end": v(-26.51, 0.57) * mm});
            skLineSegment(sketch, "E1005", {"start": v(-26.51, 0.57) * mm, "end": v(-26.72, 0.46) * mm});
            skLineSegment(sketch, "E1006", {"start": v(-26.72, 0.46) * mm, "end": v(-26.92, 0.34) * mm});
            skLineSegment(sketch, "E1007", {"start": v(-26.92, 0.34) * mm, "end": v(-27.11, 0.2) * mm});
            skLineSegment(sketch, "E1008", {"start": v(-27.11, 0.2) * mm, "end": v(-27.3, 0.06) * mm});
            skLineSegment(sketch, "E1009", {"start": v(-27.3, 0.06) * mm, "end": v(-27.38, 0) * mm});
            skLineSegment(sketch, "E1010", {"start": v(-27.38, 0) * mm, "end": v(-27.2, -0.15) * mm});
            skLineSegment(sketch, "E1011", {"start": v(-27.2, -0.15) * mm, "end": v(-27, -0.28) * mm});
            skLineSegment(sketch, "E1012", {"start": v(-27, -0.28) * mm, "end": v(-26.8, -0.4) * mm});
            skLineSegment(sketch, "E1013", {"start": v(-26.8, -0.4) * mm, "end": v(-26.6, -0.52) * mm});
            skLineSegment(sketch, "E1014", {"start": v(-26.6, -0.52) * mm, "end": v(-26.4, -0.62) * mm});
            skLineSegment(sketch, "E1015", {"start": v(-26.4, -0.62) * mm, "end": v(-26.17, -0.71) * mm});
            skLineSegment(sketch, "E1016", {"start": v(-26.17, -0.71) * mm, "end": v(-25.95, -0.79) * mm});
            skLineSegment(sketch, "E1017", {"start": v(-25.95, -0.79) * mm, "end": v(-25.73, -0.85) * mm});
            skLineSegment(sketch, "E1018", {"start": v(-25.73, -0.85) * mm, "end": v(-25.5, -0.9) * mm});
            skLineSegment(sketch, "E1019", {"start": v(-25.5, -0.9) * mm, "end": v(-25.27, -0.94) * mm});
            skLineSegment(sketch, "E1020", {"start": v(-25.27, -0.94) * mm, "end": v(-25.04, -0.96) * mm});
            skLineSegment(sketch, "E1021", {"start": v(-25.04, -0.96) * mm, "end": v(-24.8, -0.98) * mm});
            skLineSegment(sketch, "E1022", {"start": v(-24.8, -0.98) * mm, "end": v(-24.57, -0.97) * mm});
            skLineSegment(sketch, "E1023", {"start": v(-24.57, -0.97) * mm, "end": v(-24.34, -0.96) * mm});
            skLineSegment(sketch, "E1024", {"start": v(-24.34, -0.96) * mm, "end": v(-24.1, -0.95) * mm});
            skLineSegment(sketch, "E1025", {"start": v(-24.1, -0.95) * mm, "end": v(-23.89, -0.94) * mm});
            skLineSegment(sketch, "E1026", {"start": v(-23.89, -0.94) * mm, "end": v(-23.65, -0.93) * mm});
            skLineSegment(sketch, "E1027", {"start": v(-23.65, -0.93) * mm, "end": v(-23.43, -0.93) * mm});
            skLineSegment(sketch, "E1028", {"start": v(-23.43, -0.93) * mm, "end": v(-23.2, -0.92) * mm});
            skLineSegment(sketch, "E1029", {"start": v(-23.2, -0.92) * mm, "end": v(-22.98, -0.9) * mm});
            skLineSegment(sketch, "E1030", {"start": v(-22.98, -0.9) * mm, "end": v(-22.75, -0.9) * mm});
            skLineSegment(sketch, "E1031", {"start": v(-22.75, -0.9) * mm, "end": v(-22.65, -0.9) * mm});
            skLineSegment(sketch, "E1032", {"start": v(-22.65, -0.9) * mm, "end": v(-22.64, -1.13) * mm});
            skLineSegment(sketch, "E1033", {"start": v(-22.64, -1.13) * mm, "end": v(-22.62, -1.36) * mm});
            skLineSegment(sketch, "E1034", {"start": v(-22.62, -1.36) * mm, "end": v(-22.6, -1.6) * mm});
            skLineSegment(sketch, "E1035", {"start": v(-22.6, -1.6) * mm, "end": v(-22.58, -1.83) * mm});
            skLineSegment(sketch, "E1036", {"start": v(-22.58, -1.83) * mm, "end": v(-22.56, -2.06) * mm});
            skLineSegment(sketch, "E1037", {"start": v(-22.56, -2.06) * mm, "end": v(-22.54, -2.3) * mm});
            skLineSegment(sketch, "E1038", {"start": v(-22.54, -2.3) * mm, "end": v(-22.52, -2.53) * mm});
            skLineSegment(sketch, "E1039", {"start": v(-22.52, -2.53) * mm, "end": v(-22.5, -2.67) * mm});
            skLineSegment(sketch, "E1040", {"start": v(-22.5, -2.67) * mm, "end": v(-22.74, -2.7) * mm});
            skLineSegment(sketch, "E1041", {"start": v(-22.74, -2.7) * mm, "end": v(-22.96, -2.73) * mm});
            skLineSegment(sketch, "E1042", {"start": v(-22.96, -2.73) * mm, "end": v(-23.2, -2.76) * mm});
            skLineSegment(sketch, "E1043", {"start": v(-23.2, -2.76) * mm, "end": v(-23.4, -2.79) * mm});
            skLineSegment(sketch, "E1044", {"start": v(-23.4, -2.79) * mm, "end": v(-23.64, -2.82) * mm});
            skLineSegment(sketch, "E1045", {"start": v(-23.64, -2.82) * mm, "end": v(-23.86, -2.84) * mm});
            skLineSegment(sketch, "E1046", {"start": v(-23.86, -2.84) * mm, "end": v(-24.1, -2.87) * mm});
            skLineSegment(sketch, "E1047", {"start": v(-24.1, -2.87) * mm, "end": v(-24.31, -2.9) * mm});
            skLineSegment(sketch, "E1048", {"start": v(-24.31, -2.9) * mm, "end": v(-24.54, -2.93) * mm});
            skLineSegment(sketch, "E1049", {"start": v(-24.54, -2.93) * mm, "end": v(-24.77, -2.98) * mm});
            skLineSegment(sketch, "E1050", {"start": v(-24.77, -2.98) * mm, "end": v(-25, -3.03) * mm});
            skLineSegment(sketch, "E1051", {"start": v(-25, -3.03) * mm, "end": v(-25.22, -3.1) * mm});
            skLineSegment(sketch, "E1052", {"start": v(-25.22, -3.1) * mm, "end": v(-25.44, -3.18) * mm});
            skLineSegment(sketch, "E1053", {"start": v(-25.44, -3.18) * mm, "end": v(-25.65, -3.28) * mm});
            skLineSegment(sketch, "E1054", {"start": v(-25.65, -3.28) * mm, "end": v(-25.86, -3.38) * mm});
            skLineSegment(sketch, "E1055", {"start": v(-25.86, -3.38) * mm, "end": v(-26.06, -3.5) * mm});
            skLineSegment(sketch, "E1056", {"start": v(-26.06, -3.5) * mm, "end": v(-26.26, -3.63) * mm});
            skLineSegment(sketch, "E1057", {"start": v(-26.26, -3.63) * mm, "end": v(-26.44, -3.77) * mm});
            skLineSegment(sketch, "E1058", {"start": v(-26.44, -3.77) * mm, "end": v(-26.62, -3.93) * mm});
            skLineSegment(sketch, "E1059", {"start": v(-26.62, -3.93) * mm, "end": v(-26.8, -4.09) * mm});
            skLineSegment(sketch, "E1060", {"start": v(-26.8, -4.09) * mm, "end": v(-26.95, -4.26) * mm});
            skLineSegment(sketch, "E1061", {"start": v(-26.95, -4.26) * mm, "end": v(-27.02, -4.33) * mm});
            skLineSegment(sketch, "E1062", {"start": v(-27.02, -4.33) * mm, "end": v(-26.81, -4.45) * mm});
            skLineSegment(sketch, "E1063", {"start": v(-26.81, -4.45) * mm, "end": v(-26.6, -4.55) * mm});
            skLineSegment(sketch, "E1064", {"start": v(-26.6, -4.55) * mm, "end": v(-26.39, -4.64) * mm});
            skLineSegment(sketch, "E1065", {"start": v(-26.39, -4.64) * mm, "end": v(-26.17, -4.72) * mm});
            skLineSegment(sketch, "E1066", {"start": v(-26.17, -4.72) * mm, "end": v(-25.94, -4.78) * mm});
            skLineSegment(sketch, "E1067", {"start": v(-25.94, -4.78) * mm, "end": v(-25.71, -4.84) * mm});
            skLineSegment(sketch, "E1068", {"start": v(-25.71, -4.84) * mm, "end": v(-25.48, -4.88) * mm});
            skLineSegment(sketch, "E1069", {"start": v(-25.48, -4.88) * mm, "end": v(-25.25, -4.9) * mm});
            skLineSegment(sketch, "E1070", {"start": v(-25.25, -4.9) * mm, "end": v(-25.02, -4.92) * mm});
            skLineSegment(sketch, "E1071", {"start": v(-25.02, -4.92) * mm, "end": v(-24.78, -4.91) * mm});
            skLineSegment(sketch, "E1072", {"start": v(-24.78, -4.91) * mm, "end": v(-24.55, -4.9) * mm});
            skLineSegment(sketch, "E1073", {"start": v(-24.55, -4.9) * mm, "end": v(-24.32, -4.87) * mm});
            skLineSegment(sketch, "E1074", {"start": v(-24.32, -4.87) * mm, "end": v(-24.09, -4.83) * mm});
            skLineSegment(sketch, "E1075", {"start": v(-24.09, -4.83) * mm, "end": v(-23.87, -4.78) * mm});
            skLineSegment(sketch, "E1076", {"start": v(-23.87, -4.78) * mm, "end": v(-23.64, -4.74) * mm});
            skLineSegment(sketch, "E1077", {"start": v(-23.64, -4.74) * mm, "end": v(-23.42, -4.7) * mm});
            skLineSegment(sketch, "E1078", {"start": v(-23.42, -4.7) * mm, "end": v(-23.2, -4.64) * mm});
            skLineSegment(sketch, "E1079", {"start": v(-23.2, -4.64) * mm, "end": v(-22.98, -4.6) * mm});
            skLineSegment(sketch, "E1080", {"start": v(-22.98, -4.6) * mm, "end": v(-22.75, -4.55) * mm});
            skLineSegment(sketch, "E1081", {"start": v(-22.75, -4.55) * mm, "end": v(-22.53, -4.5) * mm});
            skLineSegment(sketch, "E1082", {"start": v(-22.53, -4.5) * mm, "end": v(-22.3, -4.46) * mm});
            skLineSegment(sketch, "E1083", {"start": v(-22.3, -4.46) * mm, "end": v(-22.21, -4.44) * mm});
            skLineSegment(sketch, "E1084", {"start": v(-22.21, -4.44) * mm, "end": v(-22.16, -4.66) * mm});
            skLineSegment(sketch, "E1085", {"start": v(-22.16, -4.66) * mm, "end": v(-22.1, -4.9) * mm});
            skLineSegment(sketch, "E1086", {"start": v(-22.1, -4.9) * mm, "end": v(-22.04, -5.12) * mm});
            skLineSegment(sketch, "E1087", {"start": v(-22.04, -5.12) * mm, "end": v(-21.98, -5.34) * mm});
            skLineSegment(sketch, "E1088", {"start": v(-21.98, -5.34) * mm, "end": v(-21.93, -5.57) * mm});
            skLineSegment(sketch, "E1089", {"start": v(-21.93, -5.57) * mm, "end": v(-21.87, -5.8) * mm});
            skLineSegment(sketch, "E1090", {"start": v(-21.87, -5.8) * mm, "end": v(-21.81, -6.03) * mm});
            skLineSegment(sketch, "E1091", {"start": v(-21.81, -6.03) * mm, "end": v(-21.77, -6.17) * mm});
            skLineSegment(sketch, "E1092", {"start": v(-21.77, -6.17) * mm, "end": v(-22, -6.24) * mm});
            skLineSegment(sketch, "E1093", {"start": v(-22, -6.24) * mm, "end": v(-22.21, -6.3) * mm});
            skLineSegment(sketch, "E1094", {"start": v(-22.21, -6.3) * mm, "end": v(-22.43, -6.37) * mm});
            skLineSegment(sketch, "E1095", {"start": v(-22.43, -6.37) * mm, "end": v(-22.65, -6.43) * mm});
            skLineSegment(sketch, "E1096", {"start": v(-22.65, -6.43) * mm, "end": v(-22.87, -6.5) * mm});
            skLineSegment(sketch, "E1097", {"start": v(-22.87, -6.5) * mm, "end": v(-23.08, -6.56) * mm});
            skLineSegment(sketch, "E1098", {"start": v(-23.08, -6.56) * mm, "end": v(-23.3, -6.63) * mm});
            skLineSegment(sketch, "E1099", {"start": v(-23.3, -6.63) * mm, "end": v(-23.52, -6.69) * mm});
            skLineSegment(sketch, "E1100", {"start": v(-23.52, -6.69) * mm, "end": v(-23.74, -6.76) * mm});
            skLineSegment(sketch, "E1101", {"start": v(-23.74, -6.76) * mm, "end": v(-23.96, -6.84) * mm});
            skLineSegment(sketch, "E1102", {"start": v(-23.96, -6.84) * mm, "end": v(-24.17, -6.93) * mm});
            skLineSegment(sketch, "E1103", {"start": v(-24.17, -6.93) * mm, "end": v(-24.38, -7.03) * mm});
            skLineSegment(sketch, "E1104", {"start": v(-24.38, -7.03) * mm, "end": v(-24.58, -7.15) * mm});
            skLineSegment(sketch, "E1105", {"start": v(-24.58, -7.15) * mm, "end": v(-24.78, -7.28) * mm});
            skLineSegment(sketch, "E1106", {"start": v(-24.78, -7.28) * mm, "end": v(-24.97, -7.42) * mm});
            skLineSegment(sketch, "E1107", {"start": v(-24.97, -7.42) * mm, "end": v(-25.15, -7.57) * mm});
            skLineSegment(sketch, "E1108", {"start": v(-25.15, -7.57) * mm, "end": v(-25.32, -7.73) * mm});
            skLineSegment(sketch, "E1109", {"start": v(-25.32, -7.73) * mm, "end": v(-25.48, -7.9) * mm});
            skLineSegment(sketch, "E1110", {"start": v(-25.48, -7.9) * mm, "end": v(-25.63, -8.08) * mm});
            skLineSegment(sketch, "E1111", {"start": v(-25.63, -8.08) * mm, "end": v(-25.77, -8.27) * mm});
            skLineSegment(sketch, "E1112", {"start": v(-25.77, -8.27) * mm, "end": v(-25.9, -8.46) * mm});
            skLineSegment(sketch, "E1113", {"start": v(-25.9, -8.46) * mm, "end": v(-25.95, -8.55) * mm});
            skLineSegment(sketch, "E1114", {"start": v(-25.95, -8.55) * mm, "end": v(-25.73, -8.63) * mm});
            skLineSegment(sketch, "E1115", {"start": v(-25.73, -8.63) * mm, "end": v(-25.5, -8.7) * mm});
            skLineSegment(sketch, "E1116", {"start": v(-25.5, -8.7) * mm, "end": v(-25.28, -8.75) * mm});
            skLineSegment(sketch, "E1117", {"start": v(-25.28, -8.75) * mm, "end": v(-25.05, -8.79) * mm});
            skLineSegment(sketch, "E1118", {"start": v(-25.05, -8.79) * mm, "end": v(-24.82, -8.82) * mm});
            skLineSegment(sketch, "E1119", {"start": v(-24.82, -8.82) * mm, "end": v(-24.58, -8.83) * mm});
            skLineSegment(sketch, "E1120", {"start": v(-24.58, -8.83) * mm, "end": v(-24.35, -8.83) * mm});
            skLineSegment(sketch, "E1121", {"start": v(-24.35, -8.83) * mm, "end": v(-24.11, -8.82) * mm});
            skLineSegment(sketch, "E1122", {"start": v(-24.11, -8.82) * mm, "end": v(-23.88, -8.8) * mm});
            skLineSegment(sketch, "E1123", {"start": v(-23.88, -8.8) * mm, "end": v(-23.65, -8.75) * mm});
            skLineSegment(sketch, "E1124", {"start": v(-23.65, -8.75) * mm, "end": v(-23.42, -8.7) * mm});
            skLineSegment(sketch, "E1125", {"start": v(-23.42, -8.7) * mm, "end": v(-23.2, -8.63) * mm});
            skLineSegment(sketch, "E1126", {"start": v(-23.2, -8.63) * mm, "end": v(-22.98, -8.56) * mm});
            skLineSegment(sketch, "E1127", {"start": v(-22.98, -8.56) * mm, "end": v(-22.77, -8.47) * mm});
            skLineSegment(sketch, "E1128", {"start": v(-22.77, -8.47) * mm, "end": v(-22.55, -8.39) * mm});
            skLineSegment(sketch, "E1129", {"start": v(-22.55, -8.39) * mm, "end": v(-22.34, -8.3) * mm});
            skLineSegment(sketch, "E1130", {"start": v(-22.34, -8.3) * mm, "end": v(-22.13, -8.22) * mm});
            skLineSegment(sketch, "E1131", {"start": v(-22.13, -8.22) * mm, "end": v(-21.92, -8.14) * mm});
            skLineSegment(sketch, "E1132", {"start": v(-21.92, -8.14) * mm, "end": v(-21.7, -8.06) * mm});
            skLineSegment(sketch, "E1133", {"start": v(-21.7, -8.06) * mm, "end": v(-21.5, -7.98) * mm});
            skLineSegment(sketch, "E1134", {"start": v(-21.5, -7.98) * mm, "end": v(-21.28, -7.9) * mm});
            skLineSegment(sketch, "E1135", {"start": v(-21.28, -7.9) * mm, "end": v(-21.2, -7.86) * mm});
            skLineSegment(sketch, "E1136", {"start": v(-21.2, -7.86) * mm, "end": v(-21.1, -8.07) * mm});
            skLineSegment(sketch, "E1137", {"start": v(-21.1, -8.07) * mm, "end": v(-21, -8.29) * mm});
            skLineSegment(sketch, "E1138", {"start": v(-21, -8.29) * mm, "end": v(-20.91, -8.5) * mm});
            skLineSegment(sketch, "E1139", {"start": v(-20.91, -8.5) * mm, "end": v(-20.82, -8.72) * mm});
            skLineSegment(sketch, "E1140", {"start": v(-20.82, -8.72) * mm, "end": v(-20.72, -8.93) * mm});
            skLineSegment(sketch, "E1141", {"start": v(-20.72, -8.93) * mm, "end": v(-20.63, -9.15) * mm});
            skLineSegment(sketch, "E1142", {"start": v(-20.63, -9.15) * mm, "end": v(-20.54, -9.36) * mm});
            skLineSegment(sketch, "E1143", {"start": v(-20.54, -9.36) * mm, "end": v(-20.48, -9.5) * mm});
            skLineSegment(sketch, "E1144", {"start": v(-20.48, -9.5) * mm, "end": v(-20.69, -9.6) * mm});
            skLineSegment(sketch, "E1145", {"start": v(-20.69, -9.6) * mm, "end": v(-20.88, -9.7) * mm});
            skLineSegment(sketch, "E1146", {"start": v(-20.88, -9.7) * mm, "end": v(-21.1, -9.8) * mm});
            skLineSegment(sketch, "E1147", {"start": v(-21.1, -9.8) * mm, "end": v(-21.3, -9.9) * mm});
            skLineSegment(sketch, "E1148", {"start": v(-21.3, -9.9) * mm, "end": v(-21.5, -10) * mm});
            skLineSegment(sketch, "E1149", {"start": v(-21.5, -10) * mm, "end": v(-21.7, -10.1) * mm});
            skLineSegment(sketch, "E1150", {"start": v(-21.7, -10.1) * mm, "end": v(-21.91, -10.2) * mm});
            skLineSegment(sketch, "E1151", {"start": v(-21.91, -10.2) * mm, "end": v(-22.11, -10.3) * mm});
            skLineSegment(sketch, "E1152", {"start": v(-22.11, -10.3) * mm, "end": v(-22.32, -10.4) * mm});
            skLineSegment(sketch, "E1153", {"start": v(-22.32, -10.4) * mm, "end": v(-22.52, -10.52) * mm});
            skLineSegment(sketch, "E1154", {"start": v(-22.52, -10.52) * mm, "end": v(-22.72, -10.64) * mm});
            skLineSegment(sketch, "E1155", {"start": v(-22.72, -10.64) * mm, "end": v(-22.9, -10.78) * mm});
            skLineSegment(sketch, "E1156", {"start": v(-22.9, -10.78) * mm, "end": v(-23.08, -10.93) * mm});
            skLineSegment(sketch, "E1157", {"start": v(-23.08, -10.93) * mm, "end": v(-23.26, -11.09) * mm});
            skLineSegment(sketch, "E1158", {"start": v(-23.26, -11.09) * mm, "end": v(-23.42, -11.26) * mm});
            skLineSegment(sketch, "E1159", {"start": v(-23.42, -11.26) * mm, "end": v(-23.57, -11.43) * mm});
            skLineSegment(sketch, "E1160", {"start": v(-23.57, -11.43) * mm, "end": v(-23.71, -11.62) * mm});
            skLineSegment(sketch, "E1161", {"start": v(-23.71, -11.62) * mm, "end": v(-23.84, -11.81) * mm});
            skLineSegment(sketch, "E1162", {"start": v(-23.84, -11.81) * mm, "end": v(-23.96, -12.02) * mm});
            skLineSegment(sketch, "E1163", {"start": v(-23.96, -12.02) * mm, "end": v(-24.07, -12.22) * mm});
            skLineSegment(sketch, "E1164", {"start": v(-24.07, -12.22) * mm, "end": v(-24.17, -12.44) * mm});
            skLineSegment(sketch, "E1165", {"start": v(-24.17, -12.44) * mm, "end": v(-24.2, -12.53) * mm});
            skLineSegment(sketch, "E1166", {"start": v(-24.2, -12.53) * mm, "end": v(-23.97, -12.57) * mm});
            skLineSegment(sketch, "E1167", {"start": v(-23.97, -12.57) * mm, "end": v(-23.74, -12.6) * mm});
            skLineSegment(sketch, "E1168", {"start": v(-23.74, -12.6) * mm, "end": v(-23.5, -12.62) * mm});
            skLineSegment(sketch, "E1169", {"start": v(-23.5, -12.62) * mm, "end": v(-23.27, -12.62) * mm});
            skLineSegment(sketch, "E1170", {"start": v(-23.27, -12.62) * mm, "end": v(-23.04, -12.6) * mm});
            skLineSegment(sketch, "E1171", {"start": v(-23.04, -12.6) * mm, "end": v(-22.8, -12.58) * mm});
            skLineSegment(sketch, "E1172", {"start": v(-22.8, -12.58) * mm, "end": v(-22.58, -12.54) * mm});
            skLineSegment(sketch, "E1173", {"start": v(-22.58, -12.54) * mm, "end": v(-22.35, -12.5) * mm});
            skLineSegment(sketch, "E1174", {"start": v(-22.35, -12.5) * mm, "end": v(-22.12, -12.43) * mm});
            skLineSegment(sketch, "E1175", {"start": v(-22.12, -12.43) * mm, "end": v(-21.9, -12.35) * mm});
            skLineSegment(sketch, "E1176", {"start": v(-21.9, -12.35) * mm, "end": v(-21.69, -12.26) * mm});
            skLineSegment(sketch, "E1177", {"start": v(-21.69, -12.26) * mm, "end": v(-21.48, -12.16) * mm});
            skLineSegment(sketch, "E1178", {"start": v(-21.48, -12.16) * mm, "end": v(-21.27, -12.05) * mm});
            skLineSegment(sketch, "E1179", {"start": v(-21.27, -12.05) * mm, "end": v(-21.08, -11.93) * mm});
            skLineSegment(sketch, "E1180", {"start": v(-21.08, -11.93) * mm, "end": v(-20.88, -11.81) * mm});
            skLineSegment(sketch, "E1181", {"start": v(-20.88, -11.81) * mm, "end": v(-20.69, -11.7) * mm});
            skLineSegment(sketch, "E1182", {"start": v(-20.69, -11.7) * mm, "end": v(-20.48, -11.58) * mm});
            skLineSegment(sketch, "E1183", {"start": v(-20.48, -11.58) * mm, "end": v(-20.3, -11.47) * mm});
            skLineSegment(sketch, "E1184", {"start": v(-20.3, -11.47) * mm, "end": v(-20.1, -11.35) * mm});
            skLineSegment(sketch, "E1185", {"start": v(-20.1, -11.35) * mm, "end": v(-19.9, -11.23) * mm});
            skLineSegment(sketch, "E1186", {"start": v(-19.9, -11.23) * mm, "end": v(-19.7, -11.11) * mm});
            skLineSegment(sketch, "E1187", {"start": v(-19.7, -11.11) * mm, "end": v(-19.63, -11.07) * mm});
            skLineSegment(sketch, "E1188", {"start": v(-19.63, -11.07) * mm, "end": v(-19.5, -11.26) * mm});
            skLineSegment(sketch, "E1189", {"start": v(-19.5, -11.26) * mm, "end": v(-19.37, -11.46) * mm});
            skLineSegment(sketch, "E1190", {"start": v(-19.37, -11.46) * mm, "end": v(-19.24, -11.66) * mm});
            skLineSegment(sketch, "E1191", {"start": v(-19.24, -11.66) * mm, "end": v(-19.11, -11.85) * mm});
            skLineSegment(sketch, "E1192", {"start": v(-19.11, -11.85) * mm, "end": v(-18.99, -12.05) * mm});
            skLineSegment(sketch, "E1193", {"start": v(-18.99, -12.05) * mm, "end": v(-18.86, -12.24) * mm});
            skLineSegment(sketch, "E1194", {"start": v(-18.86, -12.24) * mm, "end": v(-18.73, -12.44) * mm});
            skLineSegment(sketch, "E1195", {"start": v(-18.73, -12.44) * mm, "end": v(-18.65, -12.56) * mm});
            skLineSegment(sketch, "E1196", {"start": v(-18.65, -12.56) * mm, "end": v(-18.84, -12.7) * mm});
            skLineSegment(sketch, "E1197", {"start": v(-18.84, -12.7) * mm, "end": v(-19.02, -12.83) * mm});
            skLineSegment(sketch, "E1198", {"start": v(-19.02, -12.83) * mm, "end": v(-19.2, -12.96) * mm});
            skLineSegment(sketch, "E1199", {"start": v(-19.2, -12.96) * mm, "end": v(-19.39, -13.1) * mm});
            skLineSegment(sketch, "E1200", {"start": v(-19.39, -13.1) * mm, "end": v(-19.58, -13.23) * mm});
            skLineSegment(sketch, "E1201", {"start": v(-19.58, -13.23) * mm, "end": v(-19.76, -13.36) * mm});
            skLineSegment(sketch, "E1202", {"start": v(-19.76, -13.36) * mm, "end": v(-19.95, -13.5) * mm});
            skLineSegment(sketch, "E1203", {"start": v(-19.95, -13.5) * mm, "end": v(-20.13, -13.62) * mm});
            skLineSegment(sketch, "E1204", {"start": v(-20.13, -13.62) * mm, "end": v(-20.31, -13.76) * mm});
            skLineSegment(sketch, "E1205", {"start": v(-20.31, -13.76) * mm, "end": v(-20.5, -13.9) * mm});
            skLineSegment(sketch, "E1206", {"start": v(-20.5, -13.9) * mm, "end": v(-20.67, -14.06) * mm});
            skLineSegment(sketch, "E1207", {"start": v(-20.67, -14.06) * mm, "end": v(-20.83, -14.23) * mm});
            skLineSegment(sketch, "E1208", {"start": v(-20.83, -14.23) * mm, "end": v(-20.98, -14.4) * mm});
            skLineSegment(sketch, "E1209", {"start": v(-20.98, -14.4) * mm, "end": v(-21.13, -14.6) * mm});
            skLineSegment(sketch, "E1210", {"start": v(-21.13, -14.6) * mm, "end": v(-21.26, -14.78) * mm});
            skLineSegment(sketch, "E1211", {"start": v(-21.26, -14.78) * mm, "end": v(-21.38, -14.98) * mm});
            skLineSegment(sketch, "E1212", {"start": v(-21.38, -14.98) * mm, "end": v(-21.5, -15.2) * mm});
            skLineSegment(sketch, "E1213", {"start": v(-21.5, -15.2) * mm, "end": v(-21.59, -15.4) * mm});
            skLineSegment(sketch, "E1214", {"start": v(-21.59, -15.4) * mm, "end": v(-21.67, -15.62) * mm});
            skLineSegment(sketch, "E1215", {"start": v(-21.67, -15.62) * mm, "end": v(-21.74, -15.85) * mm});
            skLineSegment(sketch, "E1216", {"start": v(-21.74, -15.85) * mm, "end": v(-21.8, -16.07) * mm});
            skLineSegment(sketch, "E1217", {"start": v(-21.8, -16.07) * mm, "end": v(-21.83, -16.17) * mm});
            skLineSegment(sketch, "E1218", {"start": v(-21.83, -16.17) * mm, "end": v(-21.6, -16.17) * mm});
            skLineSegment(sketch, "E1219", {"start": v(-21.6, -16.17) * mm, "end": v(-21.36, -16.16) * mm});
            skLineSegment(sketch, "E1220", {"start": v(-21.36, -16.16) * mm, "end": v(-21.12, -16.14) * mm});
            skLineSegment(sketch, "E1221", {"start": v(-21.12, -16.14) * mm, "end": v(-20.9, -16.1) * mm});
            skLineSegment(sketch, "E1222", {"start": v(-20.9, -16.1) * mm, "end": v(-20.67, -16.05) * mm});
            skLineSegment(sketch, "E1223", {"start": v(-20.67, -16.05) * mm, "end": v(-20.44, -16) * mm});
            skLineSegment(sketch, "E1224", {"start": v(-20.44, -16) * mm, "end": v(-20.22, -15.92) * mm});
            skLineSegment(sketch, "E1225", {"start": v(-20.22, -15.92) * mm, "end": v(-20, -15.83) * mm});
            skLineSegment(sketch, "E1226", {"start": v(-20, -15.83) * mm, "end": v(-19.79, -15.73) * mm});
            skLineSegment(sketch, "E1227", {"start": v(-19.79, -15.73) * mm, "end": v(-19.59, -15.62) * mm});
            skLineSegment(sketch, "E1228", {"start": v(-19.59, -15.62) * mm, "end": v(-19.39, -15.5) * mm});
            skLineSegment(sketch, "E1229", {"start": v(-19.39, -15.5) * mm, "end": v(-19.2, -15.36) * mm});
            skLineSegment(sketch, "E1230", {"start": v(-19.2, -15.36) * mm, "end": v(-19.01, -15.21) * mm});
            skLineSegment(sketch, "E1231", {"start": v(-19.01, -15.21) * mm, "end": v(-18.84, -15.07) * mm});
            skLineSegment(sketch, "E1232", {"start": v(-18.84, -15.07) * mm, "end": v(-18.66, -14.91) * mm});
            skLineSegment(sketch, "E1233", {"start": v(-18.66, -14.91) * mm, "end": v(-18.5, -14.77) * mm});
            skLineSegment(sketch, "E1234", {"start": v(-18.5, -14.77) * mm, "end": v(-18.31, -14.62) * mm});
            skLineSegment(sketch, "E1235", {"start": v(-18.31, -14.62) * mm, "end": v(-18.15, -14.48) * mm});
            skLineSegment(sketch, "E1236", {"start": v(-18.15, -14.48) * mm, "end": v(-17.97, -14.33) * mm});
            skLineSegment(sketch, "E1237", {"start": v(-17.97, -14.33) * mm, "end": v(-17.8, -14.18) * mm});
            skLineSegment(sketch, "E1238", {"start": v(-17.8, -14.18) * mm, "end": v(-17.62, -14.03) * mm});
            skLineSegment(sketch, "E1239", {"start": v(-17.62, -14.03) * mm, "end": v(-17.55, -13.97) * mm});
            skLineSegment(sketch, "E1240", {"start": v(-17.55, -13.97) * mm, "end": v(-17.4, -14.15) * mm});
            skLineSegment(sketch, "E1241", {"start": v(-17.4, -14.15) * mm, "end": v(-17.23, -14.32) * mm});
            skLineSegment(sketch, "E1242", {"start": v(-17.23, -14.32) * mm, "end": v(-17.08, -14.5) * mm});
            skLineSegment(sketch, "E1243", {"start": v(-17.08, -14.5) * mm, "end": v(-16.92, -14.66) * mm});
            skLineSegment(sketch, "E1244", {"start": v(-16.92, -14.66) * mm, "end": v(-16.76, -14.83) * mm});
            skLineSegment(sketch, "E1245", {"start": v(-16.76, -14.83) * mm, "end": v(-16.6, -15) * mm});
            skLineSegment(sketch, "E1246", {"start": v(-16.6, -15) * mm, "end": v(-16.44, -15.18) * mm});
            skLineSegment(sketch, "E1247", {"start": v(-16.44, -15.18) * mm, "end": v(-16.34, -15.29) * mm});
            skLineSegment(sketch, "E1248", {"start": v(-16.34, -15.29) * mm, "end": v(-16.5, -15.45) * mm});
            skLineSegment(sketch, "E1249", {"start": v(-16.5, -15.45) * mm, "end": v(-16.66, -15.61) * mm});
            skLineSegment(sketch, "E1250", {"start": v(-16.66, -15.61) * mm, "end": v(-16.83, -15.78) * mm});
            skLineSegment(sketch, "E1251", {"start": v(-16.83, -15.78) * mm, "end": v(-16.98, -15.93) * mm});
            skLineSegment(sketch, "E1252", {"start": v(-16.98, -15.93) * mm, "end": v(-17.15, -16.1) * mm});
            skLineSegment(sketch, "E1253", {"start": v(-17.15, -16.1) * mm, "end": v(-17.3, -16.25) * mm});
            skLineSegment(sketch, "E1254", {"start": v(-17.3, -16.25) * mm, "end": v(-17.47, -16.42) * mm});
            skLineSegment(sketch, "E1255", {"start": v(-17.47, -16.42) * mm, "end": v(-17.63, -16.57) * mm});
            skLineSegment(sketch, "E1256", {"start": v(-17.63, -16.57) * mm, "end": v(-17.79, -16.74) * mm});
            skLineSegment(sketch, "E1257", {"start": v(-17.79, -16.74) * mm, "end": v(-17.94, -16.92) * mm});
            skLineSegment(sketch, "E1258", {"start": v(-17.94, -16.92) * mm, "end": v(-18.09, -17.1) * mm});
            skLineSegment(sketch, "E1259", {"start": v(-18.09, -17.1) * mm, "end": v(-18.22, -17.3) * mm});
            skLineSegment(sketch, "E1260", {"start": v(-18.22, -17.3) * mm, "end": v(-18.34, -17.5) * mm});
            skLineSegment(sketch, "E1261", {"start": v(-18.34, -17.5) * mm, "end": v(-18.45, -17.7) * mm});
            skLineSegment(sketch, "E1262", {"start": v(-18.45, -17.7) * mm, "end": v(-18.55, -17.9) * mm});
            skLineSegment(sketch, "E1263", {"start": v(-18.55, -17.9) * mm, "end": v(-18.64, -18.13) * mm});
            skLineSegment(sketch, "E1264", {"start": v(-18.64, -18.13) * mm, "end": v(-18.71, -18.35) * mm});
            skLineSegment(sketch, "E1265", {"start": v(-18.71, -18.35) * mm, "end": v(-18.77, -18.57) * mm});
            skLineSegment(sketch, "E1266", {"start": v(-18.77, -18.57) * mm, "end": v(-18.82, -18.8) * mm});
            skLineSegment(sketch, "E1267", {"start": v(-18.82, -18.8) * mm, "end": v(-18.85, -19.03) * mm});
            skLineSegment(sketch, "E1268", {"start": v(-18.85, -19.03) * mm, "end": v(-18.88, -19.27) * mm});
            skLineSegment(sketch, "E1269", {"start": v(-18.88, -19.27) * mm, "end": v(-18.88, -19.37) * mm});
            skLineSegment(sketch, "E1270", {"start": v(-18.88, -19.37) * mm, "end": v(-18.65, -19.33) * mm});
            skLineSegment(sketch, "E1271", {"start": v(-18.65, -19.33) * mm, "end": v(-18.42, -19.28) * mm});
            skLineSegment(sketch, "E1272", {"start": v(-18.42, -19.28) * mm, "end": v(-18.2, -19.22) * mm});
            skLineSegment(sketch, "E1273", {"start": v(-18.2, -19.22) * mm, "end": v(-17.97, -19.15) * mm});
            skLineSegment(sketch, "E1274", {"start": v(-17.97, -19.15) * mm, "end": v(-17.76, -19.06) * mm});
            skLineSegment(sketch, "E1275", {"start": v(-17.76, -19.06) * mm, "end": v(-17.54, -18.97) * mm});
            skLineSegment(sketch, "E1276", {"start": v(-17.54, -18.97) * mm, "end": v(-17.34, -18.85) * mm});
            skLineSegment(sketch, "E1277", {"start": v(-17.34, -18.85) * mm, "end": v(-17.14, -18.73) * mm});
            skLineSegment(sketch, "E1278", {"start": v(-17.14, -18.73) * mm, "end": v(-16.95, -18.6) * mm});
            skLineSegment(sketch, "E1279", {"start": v(-16.95, -18.6) * mm, "end": v(-16.76, -18.45) * mm});
            skLineSegment(sketch, "E1280", {"start": v(-16.76, -18.45) * mm, "end": v(-16.59, -18.3) * mm});
            skLineSegment(sketch, "E1281", {"start": v(-16.59, -18.3) * mm, "end": v(-16.42, -18.13) * mm});
            skLineSegment(sketch, "E1282", {"start": v(-16.42, -18.13) * mm, "end": v(-16.26, -17.96) * mm});
            skLineSegment(sketch, "E1283", {"start": v(-16.26, -17.96) * mm, "end": v(-16.12, -17.79) * mm});
            skLineSegment(sketch, "E1284", {"start": v(-16.12, -17.79) * mm, "end": v(-15.97, -17.6) * mm});
            skLineSegment(sketch, "E1285", {"start": v(-15.97, -17.6) * mm, "end": v(-15.82, -17.44) * mm});
            skLineSegment(sketch, "E1286", {"start": v(-15.82, -17.44) * mm, "end": v(-15.67, -17.26) * mm});
            skLineSegment(sketch, "E1287", {"start": v(-15.67, -17.26) * mm, "end": v(-15.53, -17.1) * mm});
            skLineSegment(sketch, "E1288", {"start": v(-15.53, -17.1) * mm, "end": v(-15.38, -16.92) * mm});
            skLineSegment(sketch, "E1289", {"start": v(-15.38, -16.92) * mm, "end": v(-15.24, -16.75) * mm});
            skLineSegment(sketch, "E1290", {"start": v(-15.24, -16.75) * mm, "end": v(-15.08, -16.57) * mm});
            skLineSegment(sketch, "E1291", {"start": v(-15.08, -16.57) * mm, "end": v(-15.03, -16.5) * mm});
            skLineSegment(sketch, "E1292", {"start": v(-15.03, -16.5) * mm, "end": v(-14.84, -16.64) * mm});
            skLineSegment(sketch, "E1293", {"start": v(-14.84, -16.64) * mm, "end": v(-14.66, -16.79) * mm});
            skLineSegment(sketch, "E1294", {"start": v(-14.66, -16.79) * mm, "end": v(-14.47, -16.93) * mm});
            skLineSegment(sketch, "E1295", {"start": v(-14.47, -16.93) * mm, "end": v(-14.29, -17.07) * mm});
            skLineSegment(sketch, "E1296", {"start": v(-14.29, -17.07) * mm, "end": v(-14.1, -17.22) * mm});
            skLineSegment(sketch, "E1297", {"start": v(-14.1, -17.22) * mm, "end": v(-13.92, -17.36) * mm});
            skLineSegment(sketch, "E1298", {"start": v(-13.92, -17.36) * mm, "end": v(-13.73, -17.5) * mm});
            skLineSegment(sketch, "E1299", {"start": v(-13.73, -17.5) * mm, "end": v(-13.62, -17.6) * mm});
            skLineSegment(sketch, "E1300", {"start": v(-13.62, -17.6) * mm, "end": v(-13.75, -17.79) * mm});
            skLineSegment(sketch, "E1301", {"start": v(-13.75, -17.79) * mm, "end": v(-13.88, -17.97) * mm});
            skLineSegment(sketch, "E1302", {"start": v(-13.88, -17.97) * mm, "end": v(-14.02, -18.16) * mm});
            skLineSegment(sketch, "E1303", {"start": v(-14.02, -18.16) * mm, "end": v(-14.14, -18.34) * mm});
            skLineSegment(sketch, "E1304", {"start": v(-14.14, -18.34) * mm, "end": v(-14.28, -18.53) * mm});
            skLineSegment(sketch, "E1305", {"start": v(-14.28, -18.53) * mm, "end": v(-14.4, -18.7) * mm});
            skLineSegment(sketch, "E1306", {"start": v(-14.4, -18.7) * mm, "end": v(-14.54, -18.9) * mm});
            skLineSegment(sketch, "E1307", {"start": v(-14.54, -18.9) * mm, "end": v(-14.67, -19.08) * mm});
            skLineSegment(sketch, "E1308", {"start": v(-14.67, -19.08) * mm, "end": v(-14.8, -19.27) * mm});
            skLineSegment(sketch, "E1309", {"start": v(-14.8, -19.27) * mm, "end": v(-14.93, -19.46) * mm});
            skLineSegment(sketch, "E1310", {"start": v(-14.93, -19.46) * mm, "end": v(-15.04, -19.67) * mm});
            skLineSegment(sketch, "E1311", {"start": v(-15.04, -19.67) * mm, "end": v(-15.14, -19.88) * mm});
            skLineSegment(sketch, "E1312", {"start": v(-15.14, -19.88) * mm, "end": v(-15.23, -20.1) * mm});
            skLineSegment(sketch, "E1313", {"start": v(-15.23, -20.1) * mm, "end": v(-15.3, -20.32) * mm});
            skLineSegment(sketch, "E1314", {"start": v(-15.3, -20.32) * mm, "end": v(-15.37, -20.54) * mm});
            skLineSegment(sketch, "E1315", {"start": v(-15.37, -20.54) * mm, "end": v(-15.41, -20.77) * mm});
            skLineSegment(sketch, "E1316", {"start": v(-15.41, -20.77) * mm, "end": v(-15.45, -21) * mm});
            skLineSegment(sketch, "E1317", {"start": v(-15.45, -21) * mm, "end": v(-15.47, -21.24) * mm});
            skLineSegment(sketch, "E1318", {"start": v(-15.47, -21.24) * mm, "end": v(-15.48, -21.47) * mm});
            skLineSegment(sketch, "E1319", {"start": v(-15.48, -21.47) * mm, "end": v(-15.48, -21.7) * mm});
            skLineSegment(sketch, "E1320", {"start": v(-15.48, -21.7) * mm, "end": v(-15.46, -21.94) * mm});
            skLineSegment(sketch, "E1321", {"start": v(-15.46, -21.94) * mm, "end": v(-15.45, -22.04) * mm});
            skLineSegment(sketch, "E1322", {"start": v(-15.45, -22.04) * mm, "end": v(-15.23, -21.96) * mm});
            skLineSegment(sketch, "E1323", {"start": v(-15.23, -21.96) * mm, "end": v(-15, -21.88) * mm});
            skLineSegment(sketch, "E1324", {"start": v(-15, -21.88) * mm, "end": v(-14.8, -21.78) * mm});
            skLineSegment(sketch, "E1325", {"start": v(-14.8, -21.78) * mm, "end": v(-14.6, -21.67) * mm});
            skLineSegment(sketch, "E1326", {"start": v(-14.6, -21.67) * mm, "end": v(-14.39, -21.55) * mm});
            skLineSegment(sketch, "E1327", {"start": v(-14.39, -21.55) * mm, "end": v(-14.2, -21.42) * mm});
            skLineSegment(sketch, "E1328", {"start": v(-14.2, -21.42) * mm, "end": v(-14.01, -21.28) * mm});
            skLineSegment(sketch, "E1329", {"start": v(-14.01, -21.28) * mm, "end": v(-13.84, -21.12) * mm});
            skLineSegment(sketch, "E1330", {"start": v(-13.84, -21.12) * mm, "end": v(-13.67, -20.96) * mm});
            skLineSegment(sketch, "E1331", {"start": v(-13.67, -20.96) * mm, "end": v(-13.51, -20.79) * mm});
            skLineSegment(sketch, "E1332", {"start": v(-13.51, -20.79) * mm, "end": v(-13.36, -20.6) * mm});
            skLineSegment(sketch, "E1333", {"start": v(-13.36, -20.6) * mm, "end": v(-13.23, -20.42) * mm});
            skLineSegment(sketch, "E1334", {"start": v(-13.23, -20.42) * mm, "end": v(-13.1, -20.22) * mm});
            skLineSegment(sketch, "E1335", {"start": v(-13.1, -20.22) * mm, "end": v(-12.98, -20.02) * mm});
            skLineSegment(sketch, "E1336", {"start": v(-12.98, -20.02) * mm, "end": v(-12.86, -19.82) * mm});
            skLineSegment(sketch, "E1337", {"start": v(-12.86, -19.82) * mm, "end": v(-12.75, -19.63) * mm});
            skLineSegment(sketch, "E1338", {"start": v(-12.75, -19.63) * mm, "end": v(-12.63, -19.43) * mm});
            skLineSegment(sketch, "E1339", {"start": v(-12.63, -19.43) * mm, "end": v(-12.52, -19.24) * mm});
            skLineSegment(sketch, "E1340", {"start": v(-12.52, -19.24) * mm, "end": v(-12.4, -19.04) * mm});
            skLineSegment(sketch, "E1341", {"start": v(-12.4, -19.04) * mm, "end": v(-12.29, -18.85) * mm});
            skLineSegment(sketch, "E1342", {"start": v(-12.29, -18.85) * mm, "end": v(-12.17, -18.65) * mm});
            skLineSegment(sketch, "E1343", {"start": v(-12.17, -18.65) * mm, "end": v(-12.12, -18.57) * mm});
            skLineSegment(sketch, "E1344", {"start": v(-12.12, -18.57) * mm, "end": v(-11.91, -18.69) * mm});
            skLineSegment(sketch, "E1345", {"start": v(-11.91, -18.69) * mm, "end": v(-11.7, -18.8) * mm});
            skLineSegment(sketch, "E1346", {"start": v(-11.7, -18.8) * mm, "end": v(-11.5, -18.9) * mm});
            skLineSegment(sketch, "E1347", {"start": v(-11.5, -18.9) * mm, "end": v(-11.3, -19.02) * mm});
            skLineSegment(sketch, "E1348", {"start": v(-11.3, -19.02) * mm, "end": v(-11.1, -19.13) * mm});
            skLineSegment(sketch, "E1349", {"start": v(-11.1, -19.13) * mm, "end": v(-10.88, -19.24) * mm});
            skLineSegment(sketch, "E1350", {"start": v(-10.88, -19.24) * mm, "end": v(-10.68, -19.35) * mm});
            skLineSegment(sketch, "E1351", {"start": v(-10.68, -19.35) * mm, "end": v(-10.55, -19.42) * mm});
            skLineSegment(sketch, "E1352", {"start": v(-10.55, -19.42) * mm, "end": v(-10.65, -19.63) * mm});
            skLineSegment(sketch, "E1353", {"start": v(-10.65, -19.63) * mm, "end": v(-10.75, -19.83) * mm});
            skLineSegment(sketch, "E1354", {"start": v(-10.75, -19.83) * mm, "end": v(-10.85, -20.04) * mm});
            skLineSegment(sketch, "E1355", {"start": v(-10.85, -20.04) * mm, "end": v(-10.95, -20.24) * mm});
            skLineSegment(sketch, "E1356", {"start": v(-10.95, -20.24) * mm, "end": v(-11.05, -20.45) * mm});
            skLineSegment(sketch, "E1357", {"start": v(-11.05, -20.45) * mm, "end": v(-11.15, -20.65) * mm});
            skLineSegment(sketch, "E1358", {"start": v(-11.15, -20.65) * mm, "end": v(-11.25, -20.86) * mm});
            skLineSegment(sketch, "E1359", {"start": v(-11.25, -20.86) * mm, "end": v(-11.35, -21.06) * mm});
            skLineSegment(sketch, "E1360", {"start": v(-11.35, -21.06) * mm, "end": v(-11.45, -21.27) * mm});
            skLineSegment(sketch, "E1361", {"start": v(-11.45, -21.27) * mm, "end": v(-11.53, -21.48) * mm});
            skLineSegment(sketch, "E1362", {"start": v(-11.53, -21.48) * mm, "end": v(-11.61, -21.7) * mm});
            skLineSegment(sketch, "E1363", {"start": v(-11.61, -21.7) * mm, "end": v(-11.68, -21.93) * mm});
            skLineSegment(sketch, "E1364", {"start": v(-11.68, -21.93) * mm, "end": v(-11.73, -22.16) * mm});
            skLineSegment(sketch, "E1365", {"start": v(-11.73, -22.16) * mm, "end": v(-11.76, -22.39) * mm});
            skLineSegment(sketch, "E1366", {"start": v(-11.76, -22.39) * mm, "end": v(-11.79, -22.62) * mm});
            skLineSegment(sketch, "E1367", {"start": v(-11.79, -22.62) * mm, "end": v(-11.8, -22.85) * mm});
            skLineSegment(sketch, "E1368", {"start": v(-11.8, -22.85) * mm, "end": v(-11.8, -23.09) * mm});
            skLineSegment(sketch, "E1369", {"start": v(-11.8, -23.09) * mm, "end": v(-11.78, -23.32) * mm});
            skLineSegment(sketch, "E1370", {"start": v(-11.78, -23.32) * mm, "end": v(-11.75, -23.55) * mm});
            skLineSegment(sketch, "E1371", {"start": v(-11.75, -23.55) * mm, "end": v(-11.7, -23.78) * mm});
            skLineSegment(sketch, "E1372", {"start": v(-11.7, -23.78) * mm, "end": v(-11.65, -24.01) * mm});
            skLineSegment(sketch, "E1373", {"start": v(-11.65, -24.01) * mm, "end": v(-11.63, -24.1) * mm});
            skLineSegment(sketch, "E1374", {"start": v(-11.63, -24.1) * mm, "end": v(-11.42, -24) * mm});
            skLineSegment(sketch, "E1375", {"start": v(-11.42, -24) * mm, "end": v(-11.22, -23.88) * mm});
            skLineSegment(sketch, "E1376", {"start": v(-11.22, -23.88) * mm, "end": v(-11.02, -23.75) * mm});
            skLineSegment(sketch, "E1377", {"start": v(-11.02, -23.75) * mm, "end": v(-10.84, -23.6) * mm});
            skLineSegment(sketch, "E1378", {"start": v(-10.84, -23.6) * mm, "end": v(-10.66, -23.45) * mm});
            skLineSegment(sketch, "E1379", {"start": v(-10.66, -23.45) * mm, "end": v(-10.5, -23.3) * mm});
            skLineSegment(sketch, "E1380", {"start": v(-10.5, -23.3) * mm, "end": v(-10.33, -23.12) * mm});
            skLineSegment(sketch, "E1381", {"start": v(-10.33, -23.12) * mm, "end": v(-10.18, -22.94) * mm});
            skLineSegment(sketch, "E1382", {"start": v(-10.18, -22.94) * mm, "end": v(-10.04, -22.75) * mm});
            skLineSegment(sketch, "E1383", {"start": v(-10.04, -22.75) * mm, "end": v(-9.92, -22.55) * mm});
            skLineSegment(sketch, "E1384", {"start": v(-9.92, -22.55) * mm, "end": v(-9.8, -22.35) * mm});
            skLineSegment(sketch, "E1385", {"start": v(-9.8, -22.35) * mm, "end": v(-9.7, -22.14) * mm});
            skLineSegment(sketch, "E1386", {"start": v(-9.7, -22.14) * mm, "end": v(-9.6, -21.93) * mm});
            skLineSegment(sketch, "E1387", {"start": v(-9.6, -21.93) * mm, "end": v(-9.53, -21.72) * mm});
            skLineSegment(sketch, "E1388", {"start": v(-9.53, -21.72) * mm, "end": v(-9.44, -21.5) * mm});
            skLineSegment(sketch, "E1389", {"start": v(-9.44, -21.5) * mm, "end": v(-9.36, -21.3) * mm});
            skLineSegment(sketch, "E1390", {"start": v(-9.36, -21.3) * mm, "end": v(-9.27, -21.07) * mm});
            skLineSegment(sketch, "E1391", {"start": v(-9.27, -21.07) * mm, "end": v(-9.2, -20.87) * mm});
            skLineSegment(sketch, "E1392", {"start": v(-9.2, -20.87) * mm, "end": v(-9.1, -20.65) * mm});
            skLineSegment(sketch, "E1393", {"start": v(-9.1, -20.65) * mm, "end": v(-9.03, -20.45) * mm});
            skLineSegment(sketch, "E1394", {"start": v(-9.03, -20.45) * mm, "end": v(-8.94, -20.23) * mm});
            skLineSegment(sketch, "E1395", {"start": v(-8.94, -20.23) * mm, "end": v(-8.91, -20.14) * mm});
            skLineSegment(sketch, "E1396", {"start": v(-8.91, -20.14) * mm, "end": v(-8.69, -20.22) * mm});
            skLineSegment(sketch, "E1397", {"start": v(-8.69, -20.22) * mm, "end": v(-8.47, -20.3) * mm});
            skLineSegment(sketch, "E1398", {"start": v(-8.47, -20.3) * mm, "end": v(-8.25, -20.37) * mm});
            skLineSegment(sketch, "E1399", {"start": v(-8.25, -20.37) * mm, "end": v(-8.03, -20.45) * mm});
            skLineSegment(sketch, "E1400", {"start": v(-8.03, -20.45) * mm, "end": v(-7.8, -20.52) * mm});
            skLineSegment(sketch, "E1401", {"start": v(-7.8, -20.52) * mm, "end": v(-7.58, -20.6) * mm});
            skLineSegment(sketch, "E1402", {"start": v(-7.58, -20.6) * mm, "end": v(-7.36, -20.67) * mm});
            skLineSegment(sketch, "E1403", {"start": v(-7.36, -20.67) * mm, "end": v(-7.22, -20.72) * mm});
            skLineSegment(sketch, "E1404", {"start": v(-7.22, -20.72) * mm, "end": v(-7.29, -20.95) * mm});
            skLineSegment(sketch, "E1405", {"start": v(-7.29, -20.95) * mm, "end": v(-7.35, -21.16) * mm});
            skLineSegment(sketch, "E1406", {"start": v(-7.35, -21.16) * mm, "end": v(-7.42, -21.38) * mm});
            skLineSegment(sketch, "E1407", {"start": v(-7.42, -21.38) * mm, "end": v(-7.48, -21.6) * mm});
            skLineSegment(sketch, "E1408", {"start": v(-7.48, -21.6) * mm, "end": v(-7.55, -21.82) * mm});
            skLineSegment(sketch, "E1409", {"start": v(-7.55, -21.82) * mm, "end": v(-7.61, -22.03) * mm});
            skLineSegment(sketch, "E1410", {"start": v(-7.61, -22.03) * mm, "end": v(-7.68, -22.25) * mm});
            skLineSegment(sketch, "E1411", {"start": v(-7.68, -22.25) * mm, "end": v(-7.74, -22.47) * mm});
            skLineSegment(sketch, "E1412", {"start": v(-7.74, -22.47) * mm, "end": v(-7.8, -22.69) * mm});
            skLineSegment(sketch, "E1413", {"start": v(-7.8, -22.69) * mm, "end": v(-7.85, -22.92) * mm});
            skLineSegment(sketch, "E1414", {"start": v(-7.85, -22.92) * mm, "end": v(-7.9, -23.15) * mm});
            skLineSegment(sketch, "E1415", {"start": v(-7.9, -23.15) * mm, "end": v(-7.92, -23.38) * mm});
            skLineSegment(sketch, "E1416", {"start": v(-7.92, -23.38) * mm, "end": v(-7.93, -23.61) * mm});
            skLineSegment(sketch, "E1417", {"start": v(-7.93, -23.61) * mm, "end": v(-7.93, -23.85) * mm});
            skLineSegment(sketch, "E1418", {"start": v(-7.93, -23.85) * mm, "end": v(-7.92, -24.08) * mm});
            skLineSegment(sketch, "E1419", {"start": v(-7.92, -24.08) * mm, "end": v(-7.9, -24.31) * mm});
            skLineSegment(sketch, "E1420", {"start": v(-7.9, -24.31) * mm, "end": v(-7.85, -24.54) * mm});
            skLineSegment(sketch, "E1421", {"start": v(-7.85, -24.54) * mm, "end": v(-7.8, -24.77) * mm});
            skLineSegment(sketch, "E1422", {"start": v(-7.8, -24.77) * mm, "end": v(-7.73, -25) * mm});
            skLineSegment(sketch, "E1423", {"start": v(-7.73, -25) * mm, "end": v(-7.65, -25.21) * mm});
            skLineSegment(sketch, "E1424", {"start": v(-7.65, -25.21) * mm, "end": v(-7.56, -25.43) * mm});
            skLineSegment(sketch, "E1425", {"start": v(-7.56, -25.43) * mm, "end": v(-7.51, -25.52) * mm});
            skLineSegment(sketch, "E1426", {"start": v(-7.51, -25.52) * mm, "end": v(-7.33, -25.38) * mm});
            skLineSegment(sketch, "E1427", {"start": v(-7.33, -25.38) * mm, "end": v(-7.15, -25.23) * mm});
            skLineSegment(sketch, "E1428", {"start": v(-7.15, -25.23) * mm, "end": v(-6.98, -25.07) * mm});
            skLineSegment(sketch, "E1429", {"start": v(-6.98, -25.07) * mm, "end": v(-6.82, -24.9) * mm});
            skLineSegment(sketch, "E1430", {"start": v(-6.82, -24.9) * mm, "end": v(-6.67, -24.72) * mm});
            skLineSegment(sketch, "E1431", {"start": v(-6.67, -24.72) * mm, "end": v(-6.53, -24.53) * mm});
            skLineSegment(sketch, "E1432", {"start": v(-6.53, -24.53) * mm, "end": v(-6.4, -24.33) * mm});
            skLineSegment(sketch, "E1433", {"start": v(-6.4, -24.33) * mm, "end": v(-6.28, -24.13) * mm});
            skLineSegment(sketch, "E1434", {"start": v(-6.28, -24.13) * mm, "end": v(-6.18, -23.92) * mm});
            skLineSegment(sketch, "E1435", {"start": v(-6.18, -23.92) * mm, "end": v(-6.09, -23.7) * mm});
            skLineSegment(sketch, "E1436", {"start": v(-6.09, -23.7) * mm, "end": v(-6, -23.49) * mm});
            skLineSegment(sketch, "E1437", {"start": v(-6, -23.49) * mm, "end": v(-5.94, -23.26) * mm});
            skLineSegment(sketch, "E1438", {"start": v(-5.94, -23.26) * mm, "end": v(-5.88, -23.04) * mm});
            skLineSegment(sketch, "E1439", {"start": v(-5.88, -23.04) * mm, "end": v(-5.84, -22.81) * mm});
            skLineSegment(sketch, "E1440", {"start": v(-5.84, -22.81) * mm, "end": v(-5.79, -22.59) * mm});
            skLineSegment(sketch, "E1441", {"start": v(-5.79, -22.59) * mm, "end": v(-5.74, -22.37) * mm});
            skLineSegment(sketch, "E1442", {"start": v(-5.74, -22.37) * mm, "end": v(-5.7, -22.14) * mm});
            skLineSegment(sketch, "E1443", {"start": v(-5.7, -22.14) * mm, "end": v(-5.65, -21.92) * mm});
            skLineSegment(sketch, "E1444", {"start": v(-5.65, -21.92) * mm, "end": v(-5.6, -21.7) * mm});
            skLineSegment(sketch, "E1445", {"start": v(-5.6, -21.7) * mm, "end": v(-5.56, -21.48) * mm});
            skLineSegment(sketch, "E1446", {"start": v(-5.56, -21.48) * mm, "end": v(-5.5, -21.25) * mm});
            skLineSegment(sketch, "E1447", {"start": v(-5.5, -21.25) * mm, "end": v(-5.49, -21.16) * mm});
            skLineSegment(sketch, "E1448", {"start": v(-5.49, -21.16) * mm, "end": v(-5.26, -21.2) * mm});
            skLineSegment(sketch, "E1449", {"start": v(-5.26, -21.2) * mm, "end": v(-5.03, -21.24) * mm});
            skLineSegment(sketch, "E1450", {"start": v(-5.03, -21.24) * mm, "end": v(-4.8, -21.28) * mm});
            skLineSegment(sketch, "E1451", {"start": v(-4.8, -21.28) * mm, "end": v(-4.57, -21.32) * mm});
            skLineSegment(sketch, "E1452", {"start": v(-4.57, -21.32) * mm, "end": v(-4.33, -21.35) * mm});
            skLineSegment(sketch, "E1453", {"start": v(-4.33, -21.35) * mm, "end": v(-4.1, -21.4) * mm});
            skLineSegment(sketch, "E1454", {"start": v(-4.1, -21.4) * mm, "end": v(-3.87, -21.43) * mm});
            skLineSegment(sketch, "E1455", {"start": v(-3.87, -21.43) * mm, "end": v(-3.73, -21.46) * mm});
            skLineSegment(sketch, "E1456", {"start": v(-3.73, -21.46) * mm, "end": v(-3.76, -21.69) * mm});
            skLineSegment(sketch, "E1457", {"start": v(-3.76, -21.69) * mm, "end": v(-3.78, -21.9) * mm});
            skLineSegment(sketch, "E1458", {"start": v(-3.78, -21.9) * mm, "end": v(-3.81, -22.14) * mm});
            skLineSegment(sketch, "E1459", {"start": v(-3.81, -22.14) * mm, "end": v(-3.84, -22.36) * mm});
            skLineSegment(sketch, "E1460", {"start": v(-3.84, -22.36) * mm, "end": v(-3.87, -22.6) * mm});
            skLineSegment(sketch, "E1461", {"start": v(-3.87, -22.6) * mm, "end": v(-3.9, -22.8) * mm});
            skLineSegment(sketch, "E1462", {"start": v(-3.9, -22.8) * mm, "end": v(-3.92, -23.04) * mm});
            skLineSegment(sketch, "E1463", {"start": v(-3.92, -23.04) * mm, "end": v(-3.95, -23.26) * mm});
            skLineSegment(sketch, "E1464", {"start": v(-3.95, -23.26) * mm, "end": v(-3.98, -23.49) * mm});
            skLineSegment(sketch, "E1465", {"start": v(-3.98, -23.49) * mm, "end": v(-4, -23.72) * mm});
            skLineSegment(sketch, "E1466", {"start": v(-4, -23.72) * mm, "end": v(-4, -23.96) * mm});
            skLineSegment(sketch, "E1467", {"start": v(-4, -23.96) * mm, "end": v(-3.98, -24.2) * mm});
            skLineSegment(sketch, "E1468", {"start": v(-3.98, -24.2) * mm, "end": v(-3.95, -24.42) * mm});
            skLineSegment(sketch, "E1469", {"start": v(-3.95, -24.42) * mm, "end": v(-3.91, -24.65) * mm});
            skLineSegment(sketch, "E1470", {"start": v(-3.91, -24.65) * mm, "end": v(-3.86, -24.88) * mm});
            skLineSegment(sketch, "E1471", {"start": v(-3.86, -24.88) * mm, "end": v(-3.8, -25.1) * mm});
            skLineSegment(sketch, "E1472", {"start": v(-3.8, -25.1) * mm, "end": v(-3.72, -25.33) * mm});
            skLineSegment(sketch, "E1473", {"start": v(-3.72, -25.33) * mm, "end": v(-3.63, -25.54) * mm});
            skLineSegment(sketch, "E1474", {"start": v(-3.63, -25.54) * mm, "end": v(-3.52, -25.75) * mm});
            skLineSegment(sketch, "E1475", {"start": v(-3.52, -25.75) * mm, "end": v(-3.4, -25.96) * mm});
            skLineSegment(sketch, "E1476", {"start": v(-3.4, -25.96) * mm, "end": v(-3.28, -26.15) * mm});
            skLineSegment(sketch, "E1477", {"start": v(-3.28, -26.15) * mm, "end": v(-3.23, -26.23) * mm});
            skLineSegment(sketch, "E1478", {"start": v(-3.23, -26.23) * mm, "end": v(-3.07, -26.06) * mm});
            skLineSegment(sketch, "E1479", {"start": v(-3.07, -26.06) * mm, "end": v(-2.91, -25.89) * mm});
            skLineSegment(sketch, "E1480", {"start": v(-2.91, -25.89) * mm, "end": v(-2.77, -25.7) * mm});
            skLineSegment(sketch, "E1481", {"start": v(-2.77, -25.7) * mm, "end": v(-2.64, -25.5) * mm});
            skLineSegment(sketch, "E1482", {"start": v(-2.64, -25.5) * mm, "end": v(-2.52, -25.3) * mm});
            skLineSegment(sketch, "E1483", {"start": v(-2.52, -25.3) * mm, "end": v(-2.42, -25.1) * mm});
            skLineSegment(sketch, "E1484", {"start": v(-2.42, -25.1) * mm, "end": v(-2.32, -24.88) * mm});
            skLineSegment(sketch, "E1485", {"start": v(-2.32, -24.88) * mm, "end": v(-2.24, -24.66) * mm});
            skLineSegment(sketch, "E1486", {"start": v(-2.24, -24.66) * mm, "end": v(-2.17, -24.44) * mm});
            skLineSegment(sketch, "E1487", {"start": v(-2.17, -24.44) * mm, "end": v(-2.12, -24.21) * mm});
            skLineSegment(sketch, "E1488", {"start": v(-2.12, -24.21) * mm, "end": v(-2.07, -23.98) * mm});
            skLineSegment(sketch, "E1489", {"start": v(-2.07, -23.98) * mm, "end": v(-2.04, -23.75) * mm});
            skLineSegment(sketch, "E1490", {"start": v(-2.04, -23.75) * mm, "end": v(-2.03, -23.52) * mm});
            skLineSegment(sketch, "E1491", {"start": v(-2.03, -23.52) * mm, "end": v(-2.02, -23.3) * mm});
            skLineSegment(sketch, "E1492", {"start": v(-2.02, -23.3) * mm, "end": v(-2, -23.06) * mm});
            skLineSegment(sketch, "E1493", {"start": v(-2, -23.06) * mm, "end": v(-2, -22.84) * mm});
            skLineSegment(sketch, "E1494", {"start": v(-2, -22.84) * mm, "end": v(-1.99, -22.6) * mm});
            skLineSegment(sketch, "E1495", {"start": v(-1.99, -22.6) * mm, "end": v(-1.98, -22.38) * mm});
            skLineSegment(sketch, "E1496", {"start": v(-1.98, -22.38) * mm, "end": v(-1.97, -22.15) * mm});
            skLineSegment(sketch, "E1497", {"start": v(-1.97, -22.15) * mm, "end": v(-1.96, -21.93) * mm});
            skLineSegment(sketch, "E1498", {"start": v(-1.96, -21.93) * mm, "end": v(-1.95, -21.7) * mm});
            skLineSegment(sketch, "E1499", {"start": v(-1.95, -21.7) * mm, "end": v(-1.95, -21.6) * mm});
            skLineSegment(sketch, "E1500", {"start": v(-1.95, -21.6) * mm, "end": v(-1.71, -21.6) * mm});
            skLineSegment(sketch, "E1501", {"start": v(-1.71, -21.6) * mm, "end": v(-1.48, -21.6) * mm});
            skLineSegment(sketch, "E1502", {"start": v(-1.48, -21.6) * mm, "end": v(-1.24, -21.6) * mm});
            skLineSegment(sketch, "E1503", {"start": v(-1.24, -21.6) * mm, "end": v(-1, -21.6) * mm});
            skLineSegment(sketch, "E1504", {"start": v(-1, -21.6) * mm, "end": v(-0.78, -21.6) * mm});
            skLineSegment(sketch, "E1505", {"start": v(-0.78, -21.6) * mm, "end": v(-0.54, -21.6) * mm});
            skLineSegment(sketch, "E1506", {"start": v(-0.54, -21.6) * mm, "end": v(-0.3, -21.6) * mm});
            skLineSegment(sketch, "E1507", {"start": v(-0.3, -21.6) * mm, "end": v(-0.16, -21.6) * mm});
            skLineSegment(sketch, "E1508", {"start": v(-0.16, -21.6) * mm, "end": v(-0.15, -21.84) * mm});
            skLineSegment(sketch, "E1509", {"start": v(-0.15, -21.84) * mm, "end": v(-0.14, -22.06) * mm});
            skLineSegment(sketch, "E1510", {"start": v(-0.14, -22.06) * mm, "end": v(-0.13, -22.3) * mm});
            skLineSegment(sketch, "E1511", {"start": v(-0.13, -22.3) * mm, "end": v(-0.12, -22.51) * mm});
            skLineSegment(sketch, "E1512", {"start": v(-0.12, -22.51) * mm, "end": v(-0.11, -22.75) * mm});
            skLineSegment(sketch, "E1513", {"start": v(-0.11, -22.75) * mm, "end": v(-0.1, -22.97) * mm});
            skLineSegment(sketch, "E1514", {"start": v(-0.1, -22.97) * mm, "end": v(-0.1, -23.2) * mm});
            skLineSegment(sketch, "E1515", {"start": v(-0.1, -23.2) * mm, "end": v(-0.08, -23.42) * mm});
            skLineSegment(sketch, "E1516", {"start": v(-0.08, -23.42) * mm, "end": v(-0.07, -23.65) * mm});
            skLineSegment(sketch, "E1517", {"start": v(-0.07, -23.65) * mm, "end": v(-0.05, -23.88) * mm});
            skLineSegment(sketch, "E1518", {"start": v(-0.05, -23.88) * mm, "end": v(0, -24.11) * mm});
            skLineSegment(sketch, "E1519", {"start": v(0, -24.11) * mm, "end": v(0.04, -24.34) * mm});
            skLineSegment(sketch, "E1520", {"start": v(0.04, -24.34) * mm, "end": v(0.1, -24.57) * mm});
            skLineSegment(sketch, "E1521", {"start": v(0.1, -24.57) * mm, "end": v(0.18, -24.79) * mm});
            skLineSegment(sketch, "E1522", {"start": v(0.18, -24.79) * mm, "end": v(0.27, -25) * mm});
            skLineSegment(sketch, "E1523", {"start": v(0.27, -25) * mm, "end": v(0.37, -25.21) * mm});
            skLineSegment(sketch, "E1524", {"start": v(0.37, -25.21) * mm, "end": v(0.49, -25.42) * mm});
            skLineSegment(sketch, "E1525", {"start": v(0.49, -25.42) * mm, "end": v(0.61, -25.62) * mm});
            skLineSegment(sketch, "E1526", {"start": v(0.61, -25.62) * mm, "end": v(0.75, -25.8) * mm});
            skLineSegment(sketch, "E1527", {"start": v(0.75, -25.8) * mm, "end": v(0.9, -25.99) * mm});
            skLineSegment(sketch, "E1528", {"start": v(0.9, -25.99) * mm, "end": v(1.05, -26.16) * mm});
            skLineSegment(sketch, "E1529", {"start": v(1.05, -26.16) * mm, "end": v(1.12, -26.23) * mm});
            skLineSegment(sketch, "E1530", {"start": v(1.12, -26.23) * mm, "end": v(1.25, -26.04) * mm});
            skLineSegment(sketch, "E1531", {"start": v(1.25, -26.04) * mm, "end": v(1.37, -25.84) * mm});
            skLineSegment(sketch, "E1532", {"start": v(1.37, -25.84) * mm, "end": v(1.48, -25.63) * mm});
            skLineSegment(sketch, "E1533", {"start": v(1.48, -25.63) * mm, "end": v(1.58, -25.42) * mm});
            skLineSegment(sketch, "E1534", {"start": v(1.58, -25.42) * mm, "end": v(1.66, -25.2) * mm});
            skLineSegment(sketch, "E1535", {"start": v(1.66, -25.2) * mm, "end": v(1.73, -24.98) * mm});
            skLineSegment(sketch, "E1536", {"start": v(1.73, -24.98) * mm, "end": v(1.79, -24.75) * mm});
            skLineSegment(sketch, "E1537", {"start": v(1.79, -24.75) * mm, "end": v(1.84, -24.52) * mm});
            skLineSegment(sketch, "E1538", {"start": v(1.84, -24.52) * mm, "end": v(1.87, -24.3) * mm});
            skLineSegment(sketch, "E1539", {"start": v(1.87, -24.3) * mm, "end": v(1.88, -24.06) * mm});
            skLineSegment(sketch, "E1540", {"start": v(1.88, -24.06) * mm, "end": v(1.89, -23.82) * mm});
            skLineSegment(sketch, "E1541", {"start": v(1.89, -23.82) * mm, "end": v(1.88, -23.59) * mm});
            skLineSegment(sketch, "E1542", {"start": v(1.88, -23.59) * mm, "end": v(1.86, -23.36) * mm});
            skLineSegment(sketch, "E1543", {"start": v(1.86, -23.36) * mm, "end": v(1.83, -23.13) * mm});
            skLineSegment(sketch, "E1544", {"start": v(1.83, -23.13) * mm, "end": v(1.8, -22.9) * mm});
            skLineSegment(sketch, "E1545", {"start": v(1.8, -22.9) * mm, "end": v(1.78, -22.68) * mm});
            skLineSegment(sketch, "E1546", {"start": v(1.78, -22.68) * mm, "end": v(1.75, -22.45) * mm});
            skLineSegment(sketch, "E1547", {"start": v(1.75, -22.45) * mm, "end": v(1.72, -22.23) * mm});
            skLineSegment(sketch, "E1548", {"start": v(1.72, -22.23) * mm, "end": v(1.7, -22) * mm});
            skLineSegment(sketch, "E1549", {"start": v(1.7, -22) * mm, "end": v(1.66, -21.78) * mm});
            skLineSegment(sketch, "E1550", {"start": v(1.66, -21.78) * mm, "end": v(1.63, -21.55) * mm});
            skLineSegment(sketch, "E1551", {"start": v(1.63, -21.55) * mm, "end": v(1.62, -21.46) * mm});
            skLineSegment(sketch, "E1552", {"start": v(1.62, -21.46) * mm, "end": v(1.85, -21.42) * mm});
            skLineSegment(sketch, "E1553", {"start": v(1.85, -21.42) * mm, "end": v(2.08, -21.38) * mm});
            skLineSegment(sketch, "E1554", {"start": v(2.08, -21.38) * mm, "end": v(2.32, -21.34) * mm});
            skLineSegment(sketch, "E1555", {"start": v(2.32, -21.34) * mm, "end": v(2.55, -21.3) * mm});
            skLineSegment(sketch, "E1556", {"start": v(2.55, -21.3) * mm, "end": v(2.78, -21.26) * mm});
            skLineSegment(sketch, "E1557", {"start": v(2.78, -21.26) * mm, "end": v(3, -21.22) * mm});
            skLineSegment(sketch, "E1558", {"start": v(3, -21.22) * mm, "end": v(3.24, -21.19) * mm});
            skLineSegment(sketch, "E1559", {"start": v(3.24, -21.19) * mm, "end": v(3.39, -21.16) * mm});
            skLineSegment(sketch, "E1560", {"start": v(3.39, -21.16) * mm, "end": v(3.43, -21.4) * mm});
            skLineSegment(sketch, "E1561", {"start": v(3.43, -21.4) * mm, "end": v(3.48, -21.6) * mm});
            skLineSegment(sketch, "E1562", {"start": v(3.48, -21.6) * mm, "end": v(3.53, -21.84) * mm});
            skLineSegment(sketch, "E1563", {"start": v(3.53, -21.84) * mm, "end": v(3.57, -22.05) * mm});
            skLineSegment(sketch, "E1564", {"start": v(3.57, -22.05) * mm, "end": v(3.62, -22.28) * mm});
            skLineSegment(sketch, "E1565", {"start": v(3.62, -22.28) * mm, "end": v(3.67, -22.5) * mm});
            skLineSegment(sketch, "E1566", {"start": v(3.67, -22.5) * mm, "end": v(3.71, -22.73) * mm});
            skLineSegment(sketch, "E1567", {"start": v(3.71, -22.73) * mm, "end": v(3.76, -22.94) * mm});
            skLineSegment(sketch, "E1568", {"start": v(3.76, -22.94) * mm, "end": v(3.8, -23.17) * mm});
            skLineSegment(sketch, "E1569", {"start": v(3.8, -23.17) * mm, "end": v(3.87, -23.4) * mm});
            skLineSegment(sketch, "E1570", {"start": v(3.87, -23.4) * mm, "end": v(3.95, -23.61) * mm});
            skLineSegment(sketch, "E1571", {"start": v(3.95, -23.61) * mm, "end": v(4.03, -23.83) * mm});
            skLineSegment(sketch, "E1572", {"start": v(4.03, -23.83) * mm, "end": v(4.13, -24.04) * mm});
            skLineSegment(sketch, "E1573", {"start": v(4.13, -24.04) * mm, "end": v(4.25, -24.25) * mm});
            skLineSegment(sketch, "E1574", {"start": v(4.25, -24.25) * mm, "end": v(4.37, -24.45) * mm});
            skLineSegment(sketch, "E1575", {"start": v(4.37, -24.45) * mm, "end": v(4.5, -24.64) * mm});
            skLineSegment(sketch, "E1576", {"start": v(4.5, -24.64) * mm, "end": v(4.65, -24.82) * mm});
            skLineSegment(sketch, "E1577", {"start": v(4.65, -24.82) * mm, "end": v(4.8, -25) * mm});
            skLineSegment(sketch, "E1578", {"start": v(4.8, -25) * mm, "end": v(4.97, -25.16) * mm});
            skLineSegment(sketch, "E1579", {"start": v(4.97, -25.16) * mm, "end": v(5.15, -25.31) * mm});
            skLineSegment(sketch, "E1580", {"start": v(5.15, -25.31) * mm, "end": v(5.33, -25.46) * mm});
            skLineSegment(sketch, "E1581", {"start": v(5.33, -25.46) * mm, "end": v(5.41, -25.52) * mm});
            skLineSegment(sketch, "E1582", {"start": v(5.41, -25.52) * mm, "end": v(5.5, -25.3) * mm});
            skLineSegment(sketch, "E1583", {"start": v(5.5, -25.3) * mm, "end": v(5.6, -25.09) * mm});
            skLineSegment(sketch, "E1584", {"start": v(5.6, -25.09) * mm, "end": v(5.67, -24.87) * mm});
            skLineSegment(sketch, "E1585", {"start": v(5.67, -24.87) * mm, "end": v(5.72, -24.64) * mm});
            skLineSegment(sketch, "E1586", {"start": v(5.72, -24.64) * mm, "end": v(5.77, -24.41) * mm});
            skLineSegment(sketch, "E1587", {"start": v(5.77, -24.41) * mm, "end": v(5.8, -24.18) * mm});
            skLineSegment(sketch, "E1588", {"start": v(5.8, -24.18) * mm, "end": v(5.82, -23.95) * mm});
            skLineSegment(sketch, "E1589", {"start": v(5.82, -23.95) * mm, "end": v(5.83, -23.71) * mm});
            skLineSegment(sketch, "E1590", {"start": v(5.83, -23.71) * mm, "end": v(5.83, -23.48) * mm});
            skLineSegment(sketch, "E1591", {"start": v(5.83, -23.48) * mm, "end": v(5.8, -23.25) * mm});
            skLineSegment(sketch, "E1592", {"start": v(5.8, -23.25) * mm, "end": v(5.77, -23.01) * mm});
            skLineSegment(sketch, "E1593", {"start": v(5.77, -23.01) * mm, "end": v(5.72, -22.78) * mm});
            skLineSegment(sketch, "E1594", {"start": v(5.72, -22.78) * mm, "end": v(5.66, -22.56) * mm});
            skLineSegment(sketch, "E1595", {"start": v(5.66, -22.56) * mm, "end": v(5.6, -22.34) * mm});
            skLineSegment(sketch, "E1596", {"start": v(5.6, -22.34) * mm, "end": v(5.53, -22.12) * mm});
            skLineSegment(sketch, "E1597", {"start": v(5.53, -22.12) * mm, "end": v(5.47, -21.9) * mm});
            skLineSegment(sketch, "E1598", {"start": v(5.47, -21.9) * mm, "end": v(5.4, -21.68) * mm});
            skLineSegment(sketch, "E1599", {"start": v(5.4, -21.68) * mm, "end": v(5.34, -21.47) * mm});
            skLineSegment(sketch, "E1600", {"start": v(5.34, -21.47) * mm, "end": v(5.27, -21.25) * mm});
            skLineSegment(sketch, "E1601", {"start": v(5.27, -21.25) * mm, "end": v(5.21, -21.03) * mm});
            skLineSegment(sketch, "E1602", {"start": v(5.21, -21.03) * mm, "end": v(5.14, -20.8) * mm});
            skLineSegment(sketch, "E1603", {"start": v(5.14, -20.8) * mm, "end": v(5.12, -20.72) * mm});
            skLineSegment(sketch, "E1604", {"start": v(5.12, -20.72) * mm, "end": v(5.34, -20.65) * mm});
            skLineSegment(sketch, "E1605", {"start": v(5.34, -20.65) * mm, "end": v(5.56, -20.57) * mm});
            skLineSegment(sketch, "E1606", {"start": v(5.56, -20.57) * mm, "end": v(5.78, -20.5) * mm});
            skLineSegment(sketch, "E1607", {"start": v(5.78, -20.5) * mm, "end": v(6, -20.42) * mm});
            skLineSegment(sketch, "E1608", {"start": v(6, -20.42) * mm, "end": v(6.22, -20.34) * mm});
            skLineSegment(sketch, "E1609", {"start": v(6.22, -20.34) * mm, "end": v(6.45, -20.27) * mm});
            skLineSegment(sketch, "E1610", {"start": v(6.45, -20.27) * mm, "end": v(6.67, -20.2) * mm});
            skLineSegment(sketch, "E1611", {"start": v(6.67, -20.2) * mm, "end": v(6.8, -20.14) * mm});
            skLineSegment(sketch, "E1612", {"start": v(6.8, -20.14) * mm, "end": v(6.9, -20.36) * mm});
            skLineSegment(sketch, "E1613", {"start": v(6.9, -20.36) * mm, "end": v(6.97, -20.57) * mm});
            skLineSegment(sketch, "E1614", {"start": v(6.97, -20.57) * mm, "end": v(7.06, -20.78) * mm});
            skLineSegment(sketch, "E1615", {"start": v(7.06, -20.78) * mm, "end": v(7.14, -20.99) * mm});
            skLineSegment(sketch, "E1616", {"start": v(7.14, -20.99) * mm, "end": v(7.22, -21.2) * mm});
            skLineSegment(sketch, "E1617", {"start": v(7.22, -21.2) * mm, "end": v(7.3, -21.41) * mm});
            skLineSegment(sketch, "E1618", {"start": v(7.3, -21.41) * mm, "end": v(7.39, -21.63) * mm});
            skLineSegment(sketch, "E1619", {"start": v(7.39, -21.63) * mm, "end": v(7.47, -21.84) * mm});
            skLineSegment(sketch, "E1620", {"start": v(7.47, -21.84) * mm, "end": v(7.55, -22.05) * mm});
            skLineSegment(sketch, "E1621", {"start": v(7.55, -22.05) * mm, "end": v(7.65, -22.26) * mm});
            skLineSegment(sketch, "E1622", {"start": v(7.65, -22.26) * mm, "end": v(7.76, -22.47) * mm});
            skLineSegment(sketch, "E1623", {"start": v(7.76, -22.47) * mm, "end": v(7.89, -22.67) * mm});
            skLineSegment(sketch, "E1624", {"start": v(7.89, -22.67) * mm, "end": v(8.02, -22.86) * mm});
            skLineSegment(sketch, "E1625", {"start": v(8.02, -22.86) * mm, "end": v(8.16, -23.04) * mm});
            skLineSegment(sketch, "E1626", {"start": v(8.16, -23.04) * mm, "end": v(8.32, -23.22) * mm});
            skLineSegment(sketch, "E1627", {"start": v(8.32, -23.22) * mm, "end": v(8.48, -23.39) * mm});
            skLineSegment(sketch, "E1628", {"start": v(8.48, -23.39) * mm, "end": v(8.66, -23.54) * mm});
            skLineSegment(sketch, "E1629", {"start": v(8.66, -23.54) * mm, "end": v(8.84, -23.7) * mm});
            skLineSegment(sketch, "E1630", {"start": v(8.84, -23.7) * mm, "end": v(9.03, -23.82) * mm});
            skLineSegment(sketch, "E1631", {"start": v(9.03, -23.82) * mm, "end": v(9.23, -23.95) * mm});
            skLineSegment(sketch, "E1632", {"start": v(9.23, -23.95) * mm, "end": v(9.43, -24.06) * mm});
            skLineSegment(sketch, "E1633", {"start": v(9.43, -24.06) * mm, "end": v(9.52, -24.1) * mm});
            skLineSegment(sketch, "E1634", {"start": v(9.52, -24.1) * mm, "end": v(9.58, -23.88) * mm});
            skLineSegment(sketch, "E1635", {"start": v(9.58, -23.88) * mm, "end": v(9.63, -23.65) * mm});
            skLineSegment(sketch, "E1636", {"start": v(9.63, -23.65) * mm, "end": v(9.67, -23.42) * mm});
            skLineSegment(sketch, "E1637", {"start": v(9.67, -23.42) * mm, "end": v(9.69, -23.19) * mm});
            skLineSegment(sketch, "E1638", {"start": v(9.69, -23.19) * mm, "end": v(9.7, -22.95) * mm});
            skLineSegment(sketch, "E1639", {"start": v(9.7, -22.95) * mm, "end": v(9.7, -22.72) * mm});
            skLineSegment(sketch, "E1640", {"start": v(9.7, -22.72) * mm, "end": v(9.67, -22.49) * mm});
            skLineSegment(sketch, "E1641", {"start": v(9.67, -22.49) * mm, "end": v(9.64, -22.26) * mm});
            skLineSegment(sketch, "E1642", {"start": v(9.64, -22.26) * mm, "end": v(9.6, -22.03) * mm});
            skLineSegment(sketch, "E1643", {"start": v(9.6, -22.03) * mm, "end": v(9.54, -21.8) * mm});
            skLineSegment(sketch, "E1644", {"start": v(9.54, -21.8) * mm, "end": v(9.47, -21.58) * mm});
            skLineSegment(sketch, "E1645", {"start": v(9.47, -21.58) * mm, "end": v(9.38, -21.36) * mm});
            skLineSegment(sketch, "E1646", {"start": v(9.38, -21.36) * mm, "end": v(9.28, -21.15) * mm});
            skLineSegment(sketch, "E1647", {"start": v(9.28, -21.15) * mm, "end": v(9.19, -20.94) * mm});
            skLineSegment(sketch, "E1648", {"start": v(9.19, -20.94) * mm, "end": v(9.08, -20.73) * mm});
            skLineSegment(sketch, "E1649", {"start": v(9.08, -20.73) * mm, "end": v(8.99, -20.53) * mm});
            skLineSegment(sketch, "E1650", {"start": v(8.99, -20.53) * mm, "end": v(8.88, -20.32) * mm});
            skLineSegment(sketch, "E1651", {"start": v(8.88, -20.32) * mm, "end": v(8.79, -20.12) * mm});
            skLineSegment(sketch, "E1652", {"start": v(8.79, -20.12) * mm, "end": v(8.68, -19.91) * mm});
            skLineSegment(sketch, "E1653", {"start": v(8.68, -19.91) * mm, "end": v(8.59, -19.72) * mm});
            skLineSegment(sketch, "E1654", {"start": v(8.59, -19.72) * mm, "end": v(8.48, -19.5) * mm});
            skLineSegment(sketch, "E1655", {"start": v(8.48, -19.5) * mm, "end": v(8.44, -19.42) * mm});
            skLineSegment(sketch, "E1656", {"start": v(8.44, -19.42) * mm, "end": v(8.65, -19.31) * mm});
            skLineSegment(sketch, "E1657", {"start": v(8.65, -19.31) * mm, "end": v(8.86, -19.2) * mm});
            skLineSegment(sketch, "E1658", {"start": v(8.86, -19.2) * mm, "end": v(9.06, -19.1) * mm});
            skLineSegment(sketch, "E1659", {"start": v(9.06, -19.1) * mm, "end": v(9.27, -18.98) * mm});
            skLineSegment(sketch, "E1660", {"start": v(9.27, -18.98) * mm, "end": v(9.47, -18.87) * mm});
            skLineSegment(sketch, "E1661", {"start": v(9.47, -18.87) * mm, "end": v(9.68, -18.76) * mm});
            skLineSegment(sketch, "E1662", {"start": v(9.68, -18.76) * mm, "end": v(9.89, -18.64) * mm});
            skLineSegment(sketch, "E1663", {"start": v(9.89, -18.64) * mm, "end": v(10.02, -18.57) * mm});
            skLineSegment(sketch, "E1664", {"start": v(10.02, -18.57) * mm, "end": v(10.14, -18.78) * mm});
            skLineSegment(sketch, "E1665", {"start": v(10.14, -18.78) * mm, "end": v(10.25, -18.96) * mm});
            skLineSegment(sketch, "E1666", {"start": v(10.25, -18.96) * mm, "end": v(10.37, -19.17) * mm});
            skLineSegment(sketch, "E1667", {"start": v(10.37, -19.17) * mm, "end": v(10.48, -19.36) * mm});
            skLineSegment(sketch, "E1668", {"start": v(10.48, -19.36) * mm, "end": v(10.6, -19.56) * mm});
            skLineSegment(sketch, "E1669", {"start": v(10.6, -19.56) * mm, "end": v(10.71, -19.75) * mm});
            skLineSegment(sketch, "E1670", {"start": v(10.71, -19.75) * mm, "end": v(10.83, -19.95) * mm});
            skLineSegment(sketch, "E1671", {"start": v(10.83, -19.95) * mm, "end": v(10.95, -20.14) * mm});
            skLineSegment(sketch, "E1672", {"start": v(10.95, -20.14) * mm, "end": v(11.07, -20.33) * mm});
            skLineSegment(sketch, "E1673", {"start": v(11.07, -20.33) * mm, "end": v(11.2, -20.53) * mm});
            skLineSegment(sketch, "E1674", {"start": v(11.2, -20.53) * mm, "end": v(11.34, -20.71) * mm});
            skLineSegment(sketch, "E1675", {"start": v(11.34, -20.71) * mm, "end": v(11.5, -20.89) * mm});
            skLineSegment(sketch, "E1676", {"start": v(11.5, -20.89) * mm, "end": v(11.66, -21.05) * mm});
            skLineSegment(sketch, "E1677", {"start": v(11.66, -21.05) * mm, "end": v(11.83, -21.21) * mm});
            skLineSegment(sketch, "E1678", {"start": v(11.83, -21.21) * mm, "end": v(12.01, -21.36) * mm});
            skLineSegment(sketch, "E1679", {"start": v(12.01, -21.36) * mm, "end": v(12.2, -21.5) * mm});
            skLineSegment(sketch, "E1680", {"start": v(12.2, -21.5) * mm, "end": v(12.4, -21.62) * mm});
            skLineSegment(sketch, "E1681", {"start": v(12.4, -21.62) * mm, "end": v(12.6, -21.74) * mm});
            skLineSegment(sketch, "E1682", {"start": v(12.6, -21.74) * mm, "end": v(12.81, -21.84) * mm});
            skLineSegment(sketch, "E1683", {"start": v(12.81, -21.84) * mm, "end": v(13.03, -21.93) * mm});
            skLineSegment(sketch, "E1684", {"start": v(13.03, -21.93) * mm, "end": v(13.25, -22) * mm});
            skLineSegment(sketch, "E1685", {"start": v(13.25, -22) * mm, "end": v(13.35, -22.04) * mm});
            skLineSegment(sketch, "E1686", {"start": v(13.35, -22.04) * mm, "end": v(13.37, -21.8) * mm});
            skLineSegment(sketch, "E1687", {"start": v(13.37, -21.8) * mm, "end": v(13.38, -21.57) * mm});
            skLineSegment(sketch, "E1688", {"start": v(13.38, -21.57) * mm, "end": v(13.38, -21.34) * mm});
            skLineSegment(sketch, "E1689", {"start": v(13.38, -21.34) * mm, "end": v(13.36, -21.1) * mm});
            skLineSegment(sketch, "E1690", {"start": v(13.36, -21.1) * mm, "end": v(13.33, -20.87) * mm});
            skLineSegment(sketch, "E1691", {"start": v(13.33, -20.87) * mm, "end": v(13.29, -20.64) * mm});
            skLineSegment(sketch, "E1692", {"start": v(13.29, -20.64) * mm, "end": v(13.23, -20.42) * mm});
            skLineSegment(sketch, "E1693", {"start": v(13.23, -20.42) * mm, "end": v(13.16, -20.2) * mm});
            skLineSegment(sketch, "E1694", {"start": v(13.16, -20.2) * mm, "end": v(13.08, -19.97) * mm});
            skLineSegment(sketch, "E1695", {"start": v(13.08, -19.97) * mm, "end": v(12.98, -19.76) * mm});
            skLineSegment(sketch, "E1696", {"start": v(12.98, -19.76) * mm, "end": v(12.87, -19.55) * mm});
            skLineSegment(sketch, "E1697", {"start": v(12.87, -19.55) * mm, "end": v(12.76, -19.35) * mm});
            skLineSegment(sketch, "E1698", {"start": v(12.76, -19.35) * mm, "end": v(12.62, -19.16) * mm});
            skLineSegment(sketch, "E1699", {"start": v(12.62, -19.16) * mm, "end": v(12.5, -18.97) * mm});
            skLineSegment(sketch, "E1700", {"start": v(12.5, -18.97) * mm, "end": v(12.36, -18.78) * mm});
            skLineSegment(sketch, "E1701", {"start": v(12.36, -18.78) * mm, "end": v(12.23, -18.6) * mm});
            skLineSegment(sketch, "E1702", {"start": v(12.23, -18.6) * mm, "end": v(12.1, -18.41) * mm});
            skLineSegment(sketch, "E1703", {"start": v(12.1, -18.41) * mm, "end": v(11.97, -18.23) * mm});
            skLineSegment(sketch, "E1704", {"start": v(11.97, -18.23) * mm, "end": v(11.83, -18.04) * mm});
            skLineSegment(sketch, "E1705", {"start": v(11.83, -18.04) * mm, "end": v(11.7, -17.86) * mm});
            skLineSegment(sketch, "E1706", {"start": v(11.7, -17.86) * mm, "end": v(11.56, -17.67) * mm});
            skLineSegment(sketch, "E1707", {"start": v(11.56, -17.67) * mm, "end": v(11.51, -17.6) * mm});
            skLineSegment(sketch, "E1708", {"start": v(11.51, -17.6) * mm, "end": v(11.7, -17.45) * mm});
            skLineSegment(sketch, "E1709", {"start": v(11.7, -17.45) * mm, "end": v(11.88, -17.3) * mm});
            skLineSegment(sketch, "E1710", {"start": v(11.88, -17.3) * mm, "end": v(12.07, -17.17) * mm});
            skLineSegment(sketch, "E1711", {"start": v(12.07, -17.17) * mm, "end": v(12.25, -17.02) * mm});
            skLineSegment(sketch, "E1712", {"start": v(12.25, -17.02) * mm, "end": v(12.44, -16.88) * mm});
            skLineSegment(sketch, "E1713", {"start": v(12.44, -16.88) * mm, "end": v(12.62, -16.73) * mm});
            skLineSegment(sketch, "E1714", {"start": v(12.62, -16.73) * mm, "end": v(12.8, -16.6) * mm});
            skLineSegment(sketch, "E1715", {"start": v(12.8, -16.6) * mm, "end": v(12.92, -16.5) * mm});
            skLineSegment(sketch, "E1716", {"start": v(12.92, -16.5) * mm, "end": v(13.07, -16.68) * mm});
            skLineSegment(sketch, "E1717", {"start": v(13.07, -16.68) * mm, "end": v(13.22, -16.85) * mm});
            skLineSegment(sketch, "E1718", {"start": v(13.22, -16.85) * mm, "end": v(13.37, -17.02) * mm});
            skLineSegment(sketch, "E1719", {"start": v(13.37, -17.02) * mm, "end": v(13.51, -17.2) * mm});
            skLineSegment(sketch, "E1720", {"start": v(13.51, -17.2) * mm, "end": v(13.66, -17.37) * mm});
            skLineSegment(sketch, "E1721", {"start": v(13.66, -17.37) * mm, "end": v(13.8, -17.54) * mm});
            skLineSegment(sketch, "E1722", {"start": v(13.8, -17.54) * mm, "end": v(13.96, -17.72) * mm});
            skLineSegment(sketch, "E1723", {"start": v(13.96, -17.72) * mm, "end": v(14.1, -17.89) * mm});
            skLineSegment(sketch, "E1724", {"start": v(14.1, -17.89) * mm, "end": v(14.25, -18.06) * mm});
            skLineSegment(sketch, "E1725", {"start": v(14.25, -18.06) * mm, "end": v(14.41, -18.23) * mm});
            skLineSegment(sketch, "E1726", {"start": v(14.41, -18.23) * mm, "end": v(14.58, -18.39) * mm});
            skLineSegment(sketch, "E1727", {"start": v(14.58, -18.39) * mm, "end": v(14.76, -18.54) * mm});
            skLineSegment(sketch, "E1728", {"start": v(14.76, -18.54) * mm, "end": v(14.95, -18.68) * mm});
            skLineSegment(sketch, "E1729", {"start": v(14.95, -18.68) * mm, "end": v(15.15, -18.8) * mm});
            skLineSegment(sketch, "E1730", {"start": v(15.15, -18.8) * mm, "end": v(15.35, -18.92) * mm});
            skLineSegment(sketch, "E1731", {"start": v(15.35, -18.92) * mm, "end": v(15.56, -19.02) * mm});
            skLineSegment(sketch, "E1732", {"start": v(15.56, -19.02) * mm, "end": v(15.78, -19.11) * mm});
            skLineSegment(sketch, "E1733", {"start": v(15.78, -19.11) * mm, "end": v(16, -19.2) * mm});
            skLineSegment(sketch, "E1734", {"start": v(16, -19.2) * mm, "end": v(16.22, -19.26) * mm});
            skLineSegment(sketch, "E1735", {"start": v(16.22, -19.26) * mm, "end": v(16.45, -19.31) * mm});
            skLineSegment(sketch, "E1736", {"start": v(16.45, -19.31) * mm, "end": v(16.68, -19.35) * mm});
            skLineSegment(sketch, "E1737", {"start": v(16.68, -19.35) * mm, "end": v(16.78, -19.37) * mm});
            skLineSegment(sketch, "E1738", {"start": v(16.78, -19.37) * mm, "end": v(16.76, -19.13) * mm});
            skLineSegment(sketch, "E1739", {"start": v(16.76, -19.13) * mm, "end": v(16.73, -18.9) * mm});
            skLineSegment(sketch, "E1740", {"start": v(16.73, -18.9) * mm, "end": v(16.7, -18.67) * mm});
            skLineSegment(sketch, "E1741", {"start": v(16.7, -18.67) * mm, "end": v(16.64, -18.44) * mm});
            skLineSegment(sketch, "E1742", {"start": v(16.64, -18.44) * mm, "end": v(16.57, -18.22) * mm});
            skLineSegment(sketch, "E1743", {"start": v(16.57, -18.22) * mm, "end": v(16.49, -18) * mm});
            skLineSegment(sketch, "E1744", {"start": v(16.49, -18) * mm, "end": v(16.4, -17.79) * mm});
            skLineSegment(sketch, "E1745", {"start": v(16.4, -17.79) * mm, "end": v(16.29, -17.58) * mm});
            skLineSegment(sketch, "E1746", {"start": v(16.29, -17.58) * mm, "end": v(16.17, -17.38) * mm});
            skLineSegment(sketch, "E1747", {"start": v(16.17, -17.38) * mm, "end": v(16.04, -17.18) * mm});
            skLineSegment(sketch, "E1748", {"start": v(16.04, -17.18) * mm, "end": v(15.9, -17) * mm});
            skLineSegment(sketch, "E1749", {"start": v(15.9, -17) * mm, "end": v(15.75, -16.81) * mm});
            skLineSegment(sketch, "E1750", {"start": v(15.75, -16.81) * mm, "end": v(15.6, -16.64) * mm});
            skLineSegment(sketch, "E1751", {"start": v(15.6, -16.64) * mm, "end": v(15.43, -16.48) * mm});
            skLineSegment(sketch, "E1752", {"start": v(15.43, -16.48) * mm, "end": v(15.27, -16.32) * mm});
            skLineSegment(sketch, "E1753", {"start": v(15.27, -16.32) * mm, "end": v(15.1, -16.16) * mm});
            skLineSegment(sketch, "E1754", {"start": v(15.1, -16.16) * mm, "end": v(14.94, -16) * mm});
            skLineSegment(sketch, "E1755", {"start": v(14.94, -16) * mm, "end": v(14.79, -15.84) * mm});
            skLineSegment(sketch, "E1756", {"start": v(14.79, -15.84) * mm, "end": v(14.62, -15.67) * mm});
            skLineSegment(sketch, "E1757", {"start": v(14.62, -15.67) * mm, "end": v(14.47, -15.52) * mm});
            skLineSegment(sketch, "E1758", {"start": v(14.47, -15.52) * mm, "end": v(14.3, -15.35) * mm});
            skLineSegment(sketch, "E1759", {"start": v(14.3, -15.35) * mm, "end": v(14.24, -15.29) * mm});
            skLineSegment(sketch, "E1760", {"start": v(14.24, -15.29) * mm, "end": v(14.4, -15.12) * mm});
            skLineSegment(sketch, "E1761", {"start": v(14.4, -15.12) * mm, "end": v(14.55, -14.94) * mm});
            skLineSegment(sketch, "E1762", {"start": v(14.55, -14.94) * mm, "end": v(14.71, -14.77) * mm});
            skLineSegment(sketch, "E1763", {"start": v(14.71, -14.77) * mm, "end": v(14.87, -14.6) * mm});
            skLineSegment(sketch, "E1764", {"start": v(14.87, -14.6) * mm, "end": v(15.03, -14.43) * mm});
            skLineSegment(sketch, "E1765", {"start": v(15.03, -14.43) * mm, "end": v(15.19, -14.26) * mm});
            skLineSegment(sketch, "E1766", {"start": v(15.19, -14.26) * mm, "end": v(15.35, -14.08) * mm});
            skLineSegment(sketch, "E1767", {"start": v(15.35, -14.08) * mm, "end": v(15.45, -13.97) * mm});
            skLineSegment(sketch, "E1768", {"start": v(15.45, -13.97) * mm, "end": v(15.63, -14.13) * mm});
            skLineSegment(sketch, "E1769", {"start": v(15.63, -14.13) * mm, "end": v(15.8, -14.27) * mm});
            skLineSegment(sketch, "E1770", {"start": v(15.8, -14.27) * mm, "end": v(15.97, -14.42) * mm});
            skLineSegment(sketch, "E1771", {"start": v(15.97, -14.42) * mm, "end": v(16.14, -14.56) * mm});
            skLineSegment(sketch, "E1772", {"start": v(16.14, -14.56) * mm, "end": v(16.32, -14.71) * mm});
            skLineSegment(sketch, "E1773", {"start": v(16.32, -14.71) * mm, "end": v(16.49, -14.86) * mm});
            skLineSegment(sketch, "E1774", {"start": v(16.49, -14.86) * mm, "end": v(16.67, -15) * mm});
            skLineSegment(sketch, "E1775", {"start": v(16.67, -15) * mm, "end": v(16.84, -15.15) * mm});
            skLineSegment(sketch, "E1776", {"start": v(16.84, -15.15) * mm, "end": v(17.01, -15.3) * mm});
            skLineSegment(sketch, "E1777", {"start": v(17.01, -15.3) * mm, "end": v(17.2, -15.44) * mm});
            skLineSegment(sketch, "E1778", {"start": v(17.2, -15.44) * mm, "end": v(17.4, -15.56) * mm});
            skLineSegment(sketch, "E1779", {"start": v(17.4, -15.56) * mm, "end": v(17.6, -15.68) * mm});
            skLineSegment(sketch, "E1780", {"start": v(17.6, -15.68) * mm, "end": v(17.8, -15.79) * mm});
            skLineSegment(sketch, "E1781", {"start": v(17.8, -15.79) * mm, "end": v(18.02, -15.88) * mm});
            skLineSegment(sketch, "E1782", {"start": v(18.02, -15.88) * mm, "end": v(18.24, -15.96) * mm});
            skLineSegment(sketch, "E1783", {"start": v(18.24, -15.96) * mm, "end": v(18.47, -16.03) * mm});
            skLineSegment(sketch, "E1784", {"start": v(18.47, -16.03) * mm, "end": v(18.7, -16.08) * mm});
            skLineSegment(sketch, "E1785", {"start": v(18.7, -16.08) * mm, "end": v(18.92, -16.13) * mm});
            skLineSegment(sketch, "E1786", {"start": v(18.92, -16.13) * mm, "end": v(19.15, -16.15) * mm});
            skLineSegment(sketch, "E1787", {"start": v(19.15, -16.15) * mm, "end": v(19.39, -16.17) * mm});
            skLineSegment(sketch, "E1788", {"start": v(19.39, -16.17) * mm, "end": v(19.62, -16.17) * mm});
            skLineSegment(sketch, "E1789", {"start": v(19.62, -16.17) * mm, "end": v(19.72, -16.17) * mm});
            skLineSegment(sketch, "E1790", {"start": v(19.72, -16.17) * mm, "end": v(19.67, -15.94) * mm});
            skLineSegment(sketch, "E1791", {"start": v(19.67, -15.94) * mm, "end": v(19.6, -15.72) * mm});
            skLineSegment(sketch, "E1792", {"start": v(19.6, -15.72) * mm, "end": v(19.52, -15.5) * mm});
            skLineSegment(sketch, "E1793", {"start": v(19.52, -15.5) * mm, "end": v(19.43, -15.28) * mm});
            skLineSegment(sketch, "E1794", {"start": v(19.43, -15.28) * mm, "end": v(19.33, -15.07) * mm});
            skLineSegment(sketch, "E1795", {"start": v(19.33, -15.07) * mm, "end": v(19.21, -14.87) * mm});
            skLineSegment(sketch, "E1796", {"start": v(19.21, -14.87) * mm, "end": v(19.08, -14.67) * mm});
            skLineSegment(sketch, "E1797", {"start": v(19.08, -14.67) * mm, "end": v(18.94, -14.48) * mm});
            skLineSegment(sketch, "E1798", {"start": v(18.94, -14.48) * mm, "end": v(18.8, -14.3) * mm});
            skLineSegment(sketch, "E1799", {"start": v(18.8, -14.3) * mm, "end": v(18.64, -14.13) * mm});
            skLineSegment(sketch, "E1800", {"start": v(18.64, -14.13) * mm, "end": v(18.47, -13.97) * mm});
            skLineSegment(sketch, "E1801", {"start": v(18.47, -13.97) * mm, "end": v(18.3, -13.82) * mm});
            skLineSegment(sketch, "E1802", {"start": v(18.3, -13.82) * mm, "end": v(18.13, -13.7) * mm});
            skLineSegment(sketch, "E1803", {"start": v(18.13, -13.7) * mm, "end": v(17.94, -13.56) * mm});
            skLineSegment(sketch, "E1804", {"start": v(17.94, -13.56) * mm, "end": v(17.76, -13.43) * mm});
            skLineSegment(sketch, "E1805", {"start": v(17.76, -13.43) * mm, "end": v(17.57, -13.3) * mm});
            skLineSegment(sketch, "E1806", {"start": v(17.57, -13.3) * mm, "end": v(17.4, -13.17) * mm});
            skLineSegment(sketch, "E1807", {"start": v(17.4, -13.17) * mm, "end": v(17.2, -13.03) * mm});
            skLineSegment(sketch, "E1808", {"start": v(17.2, -13.03) * mm, "end": v(17.02, -12.9) * mm});
            skLineSegment(sketch, "E1809", {"start": v(17.02, -12.9) * mm, "end": v(16.83, -12.77) * mm});
            skLineSegment(sketch, "E1810", {"start": v(16.83, -12.77) * mm, "end": v(16.65, -12.64) * mm});
            skLineSegment(sketch, "E1811", {"start": v(16.65, -12.64) * mm, "end": v(16.54, -12.56) * mm});
            skLineSegment(sketch, "E1812", {"start": v(16.54, -12.56) * mm, "end": v(16.67, -12.37) * mm});
            skLineSegment(sketch, "E1813", {"start": v(16.67, -12.37) * mm, "end": v(16.8, -12.17) * mm});
            skLineSegment(sketch, "E1814", {"start": v(16.8, -12.17) * mm, "end": v(16.93, -11.98) * mm});
            skLineSegment(sketch, "E1815", {"start": v(16.93, -11.98) * mm, "end": v(17.06, -11.78) * mm});
            skLineSegment(sketch, "E1816", {"start": v(17.06, -11.78) * mm, "end": v(17.19, -11.58) * mm});
            skLineSegment(sketch, "E1817", {"start": v(17.19, -11.58) * mm, "end": v(17.31, -11.39) * mm});
            skLineSegment(sketch, "E1818", {"start": v(17.31, -11.39) * mm, "end": v(17.44, -11.2) * mm});
            skLineSegment(sketch, "E1819", {"start": v(17.44, -11.2) * mm, "end": v(17.52, -11.07) * mm});
            skLineSegment(sketch, "E1820", {"start": v(17.52, -11.07) * mm, "end": v(17.72, -11.19) * mm});
            skLineSegment(sketch, "E1821", {"start": v(17.72, -11.19) * mm, "end": v(17.91, -11.3) * mm});
            skLineSegment(sketch, "E1822", {"start": v(17.91, -11.3) * mm, "end": v(18.11, -11.42) * mm});
            skLineSegment(sketch, "E1823", {"start": v(18.11, -11.42) * mm, "end": v(18.3, -11.53) * mm});
            skLineSegment(sketch, "E1824", {"start": v(18.3, -11.53) * mm, "end": v(18.5, -11.65) * mm});
            skLineSegment(sketch, "E1825", {"start": v(18.5, -11.65) * mm, "end": v(18.7, -11.77) * mm});
            skLineSegment(sketch, "E1826", {"start": v(18.7, -11.77) * mm, "end": v(18.9, -11.89) * mm});
            skLineSegment(sketch, "E1827", {"start": v(18.9, -11.89) * mm, "end": v(19.08, -12) * mm});
            skLineSegment(sketch, "E1828", {"start": v(19.08, -12) * mm, "end": v(19.28, -12.11) * mm});
            skLineSegment(sketch, "E1829", {"start": v(19.28, -12.11) * mm, "end": v(19.5, -12.22) * mm});
            skLineSegment(sketch, "E1830", {"start": v(19.5, -12.22) * mm, "end": v(19.7, -12.32) * mm});
            skLineSegment(sketch, "E1831", {"start": v(19.7, -12.32) * mm, "end": v(19.92, -12.4) * mm});
            skLineSegment(sketch, "E1832", {"start": v(19.92, -12.4) * mm, "end": v(20.15, -12.47) * mm});
            skLineSegment(sketch, "E1833", {"start": v(20.15, -12.47) * mm, "end": v(20.38, -12.52) * mm});
            skLineSegment(sketch, "E1834", {"start": v(20.38, -12.52) * mm, "end": v(20.6, -12.57) * mm});
            skLineSegment(sketch, "E1835", {"start": v(20.6, -12.57) * mm, "end": v(20.84, -12.6) * mm});
            skLineSegment(sketch, "E1836", {"start": v(20.84, -12.6) * mm, "end": v(21.07, -12.62) * mm});
            skLineSegment(sketch, "E1837", {"start": v(21.07, -12.62) * mm, "end": v(21.3, -12.62) * mm});
            skLineSegment(sketch, "E1838", {"start": v(21.3, -12.62) * mm, "end": v(21.54, -12.6) * mm});
            skLineSegment(sketch, "E1839", {"start": v(21.54, -12.6) * mm, "end": v(21.77, -12.58) * mm});
            skLineSegment(sketch, "E1840", {"start": v(21.77, -12.58) * mm, "end": v(22, -12.55) * mm});
            skLineSegment(sketch, "E1841", {"start": v(22, -12.55) * mm, "end": v(22.1, -12.53) * mm});
            skLineSegment(sketch, "E1842", {"start": v(22.1, -12.53) * mm, "end": v(22, -12.31) * mm});
            skLineSegment(sketch, "E1843", {"start": v(22, -12.31) * mm, "end": v(21.9, -12.1) * mm});
            skLineSegment(sketch, "E1844", {"start": v(21.9, -12.1) * mm, "end": v(21.8, -11.9) * mm});
            skLineSegment(sketch, "E1845", {"start": v(21.8, -11.9) * mm, "end": v(21.67, -11.7) * mm});
            skLineSegment(sketch, "E1846", {"start": v(21.67, -11.7) * mm, "end": v(21.53, -11.51) * mm});
            skLineSegment(sketch, "E1847", {"start": v(21.53, -11.51) * mm, "end": v(21.38, -11.33) * mm});
            skLineSegment(sketch, "E1848", {"start": v(21.38, -11.33) * mm, "end": v(21.22, -11.16) * mm});
            skLineSegment(sketch, "E1849", {"start": v(21.22, -11.16) * mm, "end": v(21.06, -11) * mm});
            skLineSegment(sketch, "E1850", {"start": v(21.06, -11) * mm, "end": v(20.88, -10.84) * mm});
            skLineSegment(sketch, "E1851", {"start": v(20.88, -10.84) * mm, "end": v(20.7, -10.7) * mm});
            skLineSegment(sketch, "E1852", {"start": v(20.7, -10.7) * mm, "end": v(20.5, -10.57) * mm});
            skLineSegment(sketch, "E1853", {"start": v(20.5, -10.57) * mm, "end": v(20.3, -10.45) * mm});
            skLineSegment(sketch, "E1854", {"start": v(20.3, -10.45) * mm, "end": v(20.1, -10.34) * mm});
            skLineSegment(sketch, "E1855", {"start": v(20.1, -10.34) * mm, "end": v(19.9, -10.24) * mm});
            skLineSegment(sketch, "E1856", {"start": v(19.9, -10.24) * mm, "end": v(19.68, -10.14) * mm});
            skLineSegment(sketch, "E1857", {"start": v(19.68, -10.14) * mm, "end": v(19.48, -10.04) * mm});
            skLineSegment(sketch, "E1858", {"start": v(19.48, -10.04) * mm, "end": v(19.27, -9.94) * mm});
            skLineSegment(sketch, "E1859", {"start": v(19.27, -9.94) * mm, "end": v(19.07, -9.84) * mm});
            skLineSegment(sketch, "E1860", {"start": v(19.07, -9.84) * mm, "end": v(18.86, -9.74) * mm});
            skLineSegment(sketch, "E1861", {"start": v(18.86, -9.74) * mm, "end": v(18.66, -9.64) * mm});
            skLineSegment(sketch, "E1862", {"start": v(18.66, -9.64) * mm, "end": v(18.45, -9.54) * mm});
            skLineSegment(sketch, "E1863", {"start": v(18.45, -9.54) * mm, "end": v(18.37, -9.5) * mm});
            skLineSegment(sketch, "E1864", {"start": v(18.37, -9.5) * mm, "end": v(18.47, -9.28) * mm});
            skLineSegment(sketch, "E1865", {"start": v(18.47, -9.28) * mm, "end": v(18.56, -9.07) * mm});
            skLineSegment(sketch, "E1866", {"start": v(18.56, -9.07) * mm, "end": v(18.65, -8.85) * mm});
            skLineSegment(sketch, "E1867", {"start": v(18.65, -8.85) * mm, "end": v(18.75, -8.64) * mm});
            skLineSegment(sketch, "E1868", {"start": v(18.75, -8.64) * mm, "end": v(18.84, -8.42) * mm});
            skLineSegment(sketch, "E1869", {"start": v(18.84, -8.42) * mm, "end": v(18.94, -8.21) * mm});
            skLineSegment(sketch, "E1870", {"start": v(18.94, -8.21) * mm, "end": v(19.03, -8) * mm});
            skLineSegment(sketch, "E1871", {"start": v(19.03, -8) * mm, "end": v(19.1, -7.86) * mm});
            skLineSegment(sketch, "E1872", {"start": v(19.1, -7.86) * mm, "end": v(19.3, -7.94) * mm});
            skLineSegment(sketch, "E1873", {"start": v(19.3, -7.94) * mm, "end": v(19.51, -8.02) * mm});
            skLineSegment(sketch, "E1874", {"start": v(19.51, -8.02) * mm, "end": v(19.73, -8.1) * mm});
            skLineSegment(sketch, "E1875", {"start": v(19.73, -8.1) * mm, "end": v(19.94, -8.2) * mm});
            skLineSegment(sketch, "E1876", {"start": v(19.94, -8.2) * mm, "end": v(20.16, -8.28) * mm});
            skLineSegment(sketch, "E1877", {"start": v(20.16, -8.28) * mm, "end": v(20.36, -8.36) * mm});
            skLineSegment(sketch, "E1878", {"start": v(20.36, -8.36) * mm, "end": v(20.58, -8.44) * mm});
            skLineSegment(sketch, "E1879", {"start": v(20.58, -8.44) * mm, "end": v(20.79, -8.52) * mm});
            skLineSegment(sketch, "E1880", {"start": v(20.79, -8.52) * mm, "end": v(21, -8.6) * mm});
            skLineSegment(sketch, "E1881", {"start": v(21, -8.6) * mm, "end": v(21.22, -8.67) * mm});
            skLineSegment(sketch, "E1882", {"start": v(21.22, -8.67) * mm, "end": v(21.45, -8.73) * mm});
            skLineSegment(sketch, "E1883", {"start": v(21.45, -8.73) * mm, "end": v(21.68, -8.78) * mm});
            skLineSegment(sketch, "E1884", {"start": v(21.68, -8.78) * mm, "end": v(21.91, -8.8) * mm});
            skLineSegment(sketch, "E1885", {"start": v(21.91, -8.8) * mm, "end": v(22.14, -8.83) * mm});
            skLineSegment(sketch, "E1886", {"start": v(22.14, -8.83) * mm, "end": v(22.38, -8.83) * mm});
            skLineSegment(sketch, "E1887", {"start": v(22.38, -8.83) * mm, "end": v(22.61, -8.82) * mm});
            skLineSegment(sketch, "E1888", {"start": v(22.61, -8.82) * mm, "end": v(22.85, -8.8) * mm});
            skLineSegment(sketch, "E1889", {"start": v(22.85, -8.8) * mm, "end": v(23.08, -8.77) * mm});
            skLineSegment(sketch, "E1890", {"start": v(23.08, -8.77) * mm, "end": v(23.3, -8.72) * mm});
            skLineSegment(sketch, "E1891", {"start": v(23.3, -8.72) * mm, "end": v(23.53, -8.66) * mm});
            skLineSegment(sketch, "E1892", {"start": v(23.53, -8.66) * mm, "end": v(23.75, -8.58) * mm});
            skLineSegment(sketch, "E1893", {"start": v(23.75, -8.58) * mm, "end": v(23.85, -8.55) * mm});
            skLineSegment(sketch, "E1894", {"start": v(23.85, -8.55) * mm, "end": v(23.72, -8.35) * mm});
            skLineSegment(sketch, "E1895", {"start": v(23.72, -8.35) * mm, "end": v(23.59, -8.16) * mm});
            skLineSegment(sketch, "E1896", {"start": v(23.59, -8.16) * mm, "end": v(23.44, -7.98) * mm});
            skLineSegment(sketch, "E1897", {"start": v(23.44, -7.98) * mm, "end": v(23.28, -7.8) * mm});
            skLineSegment(sketch, "E1898", {"start": v(23.28, -7.8) * mm, "end": v(23.12, -7.64) * mm});
            skLineSegment(sketch, "E1899", {"start": v(23.12, -7.64) * mm, "end": v(22.94, -7.48) * mm});
            skLineSegment(sketch, "E1900", {"start": v(22.94, -7.48) * mm, "end": v(22.76, -7.34) * mm});
            skLineSegment(sketch, "E1901", {"start": v(22.76, -7.34) * mm, "end": v(22.56, -7.2) * mm});
            skLineSegment(sketch, "E1902", {"start": v(22.56, -7.2) * mm, "end": v(22.37, -7.08) * mm});
            skLineSegment(sketch, "E1903", {"start": v(22.37, -7.08) * mm, "end": v(22.16, -6.97) * mm});
            skLineSegment(sketch, "E1904", {"start": v(22.16, -6.97) * mm, "end": v(21.95, -6.88) * mm});
            skLineSegment(sketch, "E1905", {"start": v(21.95, -6.88) * mm, "end": v(21.73, -6.79) * mm});
            skLineSegment(sketch, "E1906", {"start": v(21.73, -6.79) * mm, "end": v(21.5, -6.72) * mm});
            skLineSegment(sketch, "E1907", {"start": v(21.5, -6.72) * mm, "end": v(21.29, -6.65) * mm});
            skLineSegment(sketch, "E1908", {"start": v(21.29, -6.65) * mm, "end": v(21.07, -6.58) * mm});
            skLineSegment(sketch, "E1909", {"start": v(21.07, -6.58) * mm, "end": v(20.85, -6.52) * mm});
            skLineSegment(sketch, "E1910", {"start": v(20.85, -6.52) * mm, "end": v(20.63, -6.45) * mm});
            skLineSegment(sketch, "E1911", {"start": v(20.63, -6.45) * mm, "end": v(20.42, -6.4) * mm});
            skLineSegment(sketch, "E1912", {"start": v(20.42, -6.4) * mm, "end": v(20.2, -6.33) * mm});
            skLineSegment(sketch, "E1913", {"start": v(20.2, -6.33) * mm, "end": v(19.98, -6.26) * mm});
            skLineSegment(sketch, "E1914", {"start": v(19.98, -6.26) * mm, "end": v(19.76, -6.2) * mm});
            skLineSegment(sketch, "E1915", {"start": v(19.76, -6.2) * mm, "end": v(19.67, -6.17) * mm});
            skLineSegment(sketch, "E1916", {"start": v(19.67, -6.17) * mm, "end": v(19.73, -5.94) * mm});
            skLineSegment(sketch, "E1917", {"start": v(19.73, -5.94) * mm, "end": v(19.79, -5.72) * mm});
            skLineSegment(sketch, "E1918", {"start": v(19.79, -5.72) * mm, "end": v(19.84, -5.49) * mm});
            skLineSegment(sketch, "E1919", {"start": v(19.84, -5.49) * mm, "end": v(19.9, -5.26) * mm});
            skLineSegment(sketch, "E1920", {"start": v(19.9, -5.26) * mm, "end": v(19.96, -5.04) * mm});
            skLineSegment(sketch, "E1921", {"start": v(19.96, -5.04) * mm, "end": v(20.02, -4.8) * mm});
            skLineSegment(sketch, "E1922", {"start": v(20.02, -4.8) * mm, "end": v(20.07, -4.58) * mm});
            skLineSegment(sketch, "E1923", {"start": v(20.07, -4.58) * mm, "end": v(20.1, -4.44) * mm});
            skLineSegment(sketch, "E1924", {"start": v(20.1, -4.44) * mm, "end": v(20.34, -4.49) * mm});
            skLineSegment(sketch, "E1925", {"start": v(20.34, -4.49) * mm, "end": v(20.55, -4.53) * mm});
            skLineSegment(sketch, "E1926", {"start": v(20.55, -4.53) * mm, "end": v(20.78, -4.58) * mm});
            skLineSegment(sketch, "E1927", {"start": v(20.78, -4.58) * mm, "end": v(21, -4.62) * mm});
            skLineSegment(sketch, "E1928", {"start": v(21, -4.62) * mm, "end": v(21.23, -4.67) * mm});
            skLineSegment(sketch, "E1929", {"start": v(21.23, -4.67) * mm, "end": v(21.44, -4.72) * mm});
            skLineSegment(sketch, "E1930", {"start": v(21.44, -4.72) * mm, "end": v(21.67, -4.77) * mm});
            skLineSegment(sketch, "E1931", {"start": v(21.67, -4.77) * mm, "end": v(21.89, -4.81) * mm});
            skLineSegment(sketch, "E1932", {"start": v(21.89, -4.81) * mm, "end": v(22.12, -4.86) * mm});
            skLineSegment(sketch, "E1933", {"start": v(22.12, -4.86) * mm, "end": v(22.35, -4.89) * mm});
            skLineSegment(sketch, "E1934", {"start": v(22.35, -4.89) * mm, "end": v(22.58, -4.9) * mm});
            skLineSegment(sketch, "E1935", {"start": v(22.58, -4.9) * mm, "end": v(22.81, -4.92) * mm});
            skLineSegment(sketch, "E1936", {"start": v(22.81, -4.92) * mm, "end": v(23.05, -4.9) * mm});
            skLineSegment(sketch, "E1937", {"start": v(23.05, -4.9) * mm, "end": v(23.28, -4.89) * mm});
            skLineSegment(sketch, "E1938", {"start": v(23.28, -4.89) * mm, "end": v(23.51, -4.86) * mm});
            skLineSegment(sketch, "E1939", {"start": v(23.51, -4.86) * mm, "end": v(23.74, -4.8) * mm});
            skLineSegment(sketch, "E1940", {"start": v(23.74, -4.8) * mm, "end": v(23.97, -4.75) * mm});
            skLineSegment(sketch, "E1941", {"start": v(23.97, -4.75) * mm, "end": v(24.2, -4.68) * mm});
            skLineSegment(sketch, "E1942", {"start": v(24.2, -4.68) * mm, "end": v(24.4, -4.59) * mm});
            skLineSegment(sketch, "E1943", {"start": v(24.4, -4.59) * mm, "end": v(24.62, -4.5) * mm});
            skLineSegment(sketch, "E1944", {"start": v(24.62, -4.5) * mm, "end": v(24.83, -4.38) * mm});
            skLineSegment(sketch, "E1945", {"start": v(24.83, -4.38) * mm, "end": v(24.91, -4.33) * mm});
            skLineSegment(sketch, "E1946", {"start": v(24.91, -4.33) * mm, "end": v(24.76, -4.16) * mm});
            skLineSegment(sketch, "E1947", {"start": v(24.76, -4.16) * mm, "end": v(24.6, -4) * mm});
            skLineSegment(sketch, "E1948", {"start": v(24.6, -4) * mm, "end": v(24.42, -3.84) * mm});
            skLineSegment(sketch, "E1949", {"start": v(24.42, -3.84) * mm, "end": v(24.23, -3.7) * mm});
            skLineSegment(sketch, "E1950", {"start": v(24.23, -3.7) * mm, "end": v(24.04, -3.56) * mm});
            skLineSegment(sketch, "E1951", {"start": v(24.04, -3.56) * mm, "end": v(23.85, -3.43) * mm});
            skLineSegment(sketch, "E1952", {"start": v(23.85, -3.43) * mm, "end": v(23.64, -3.32) * mm});
            skLineSegment(sketch, "E1953", {"start": v(23.64, -3.32) * mm, "end": v(23.43, -3.22) * mm});
            skLineSegment(sketch, "E1954", {"start": v(23.43, -3.22) * mm, "end": v(23.21, -3.13) * mm});
            skLineSegment(sketch, "E1955", {"start": v(23.21, -3.13) * mm, "end": v(22.99, -3.06) * mm});
            skLineSegment(sketch, "E1956", {"start": v(22.99, -3.06) * mm, "end": v(22.76, -3) * mm});
            skLineSegment(sketch, "E1957", {"start": v(22.76, -3) * mm, "end": v(22.54, -2.95) * mm});
            skLineSegment(sketch, "E1958", {"start": v(22.54, -2.95) * mm, "end": v(22.3, -2.91) * mm});
            skLineSegment(sketch, "E1959", {"start": v(22.3, -2.91) * mm, "end": v(22.08, -2.88) * mm});
            skLineSegment(sketch, "E1960", {"start": v(22.08, -2.88) * mm, "end": v(21.85, -2.85) * mm});
            skLineSegment(sketch, "E1961", {"start": v(21.85, -2.85) * mm, "end": v(21.63, -2.83) * mm});
            skLineSegment(sketch, "E1962", {"start": v(21.63, -2.83) * mm, "end": v(21.4, -2.8) * mm});
            skLineSegment(sketch, "E1963", {"start": v(21.4, -2.8) * mm, "end": v(21.18, -2.77) * mm});
            skLineSegment(sketch, "E1964", {"start": v(21.18, -2.77) * mm, "end": v(20.95, -2.74) * mm});
            skLineSegment(sketch, "E1965", {"start": v(20.95, -2.74) * mm, "end": v(20.73, -2.71) * mm});
            skLineSegment(sketch, "E1966", {"start": v(20.73, -2.71) * mm, "end": v(20.5, -2.69) * mm});
            skLineSegment(sketch, "E1967", {"start": v(20.5, -2.69) * mm, "end": v(20.4, -2.67) * mm});
            skLineSegment(sketch, "E1968", {"start": v(20.4, -2.67) * mm, "end": v(20.42, -2.44) * mm});
            skLineSegment(sketch, "E1969", {"start": v(20.42, -2.44) * mm, "end": v(20.44, -2.2) * mm});
            skLineSegment(sketch, "E1970", {"start": v(20.44, -2.2) * mm, "end": v(20.46, -1.97) * mm});
            skLineSegment(sketch, "E1971", {"start": v(20.46, -1.97) * mm, "end": v(20.48, -1.74) * mm});
            skLineSegment(sketch, "E1972", {"start": v(20.48, -1.74) * mm, "end": v(20.5, -1.5) * mm});
            skLineSegment(sketch, "E1973", {"start": v(20.5, -1.5) * mm, "end": v(20.52, -1.27) * mm});
            skLineSegment(sketch, "E1974", {"start": v(20.52, -1.27) * mm, "end": v(20.54, -1.04) * mm});
            skLineSegment(sketch, "E1975", {"start": v(20.54, -1.04) * mm, "end": v(20.55, -0.9) * mm});
            skLineSegment(sketch, "E1976", {"start": v(-4.82, 1.22) * mm, "end": v(-4.74, 1.46) * mm});
            skLineSegment(sketch, "E1977", {"start": v(-4.74, 1.46) * mm, "end": v(-4.64, 1.69) * mm});
            skLineSegment(sketch, "E1978", {"start": v(-4.64, 1.69) * mm, "end": v(-4.52, 1.9) * mm});
            skLineSegment(sketch, "E1979", {"start": v(-4.52, 1.9) * mm, "end": v(-4.4, 2.12) * mm});
            skLineSegment(sketch, "E1980", {"start": v(-4.4, 2.12) * mm, "end": v(-4.26, 2.33) * mm});
            skLineSegment(sketch, "E1981", {"start": v(-4.26, 2.33) * mm, "end": v(-4.1, 2.53) * mm});
            skLineSegment(sketch, "E1982", {"start": v(-4.1, 2.53) * mm, "end": v(-3.94, 2.71) * mm});
            skLineSegment(sketch, "E1983", {"start": v(-3.94, 2.71) * mm, "end": v(-3.76, 2.89) * mm});
            skLineSegment(sketch, "E1984", {"start": v(-3.76, 2.89) * mm, "end": v(-3.58, 3.05) * mm});
            skLineSegment(sketch, "E1985", {"start": v(-3.58, 3.05) * mm, "end": v(-3.38, 3.2) * mm});
            skLineSegment(sketch, "E1986", {"start": v(-3.38, 3.2) * mm, "end": v(-3.17, 3.35) * mm});
            skLineSegment(sketch, "E1987", {"start": v(-3.17, 3.35) * mm, "end": v(-2.96, 3.47) * mm});
            skLineSegment(sketch, "E1988", {"start": v(-2.96, 3.47) * mm, "end": v(-2.74, 3.59) * mm});
            skLineSegment(sketch, "E1989", {"start": v(-2.74, 3.59) * mm, "end": v(-2.51, 3.68) * mm});
            skLineSegment(sketch, "E1990", {"start": v(-2.51, 3.68) * mm, "end": v(-2.28, 3.77) * mm});
            skLineSegment(sketch, "E1991", {"start": v(-2.28, 3.77) * mm, "end": v(-2.14, 3.8) * mm});
            skLineSegment(sketch, "E1992", {"start": v(-2.14, 3.8) * mm, "end": v(-2.19, 19.42) * mm});
            skLineSegment(sketch, "E1993", {"start": v(-2.19, 19.42) * mm, "end": v(-2.27, 19.42) * mm});
            skLineSegment(sketch, "E1994", {"start": v(-2.27, 19.42) * mm, "end": v(-3.5, 19.3) * mm});
            skLineSegment(sketch, "E1995", {"start": v(-3.5, 19.3) * mm, "end": v(-4.7, 19.11) * mm});
            skLineSegment(sketch, "E1996", {"start": v(-4.7, 19.11) * mm, "end": v(-5.9, 18.85) * mm});
            skLineSegment(sketch, "E1997", {"start": v(-5.9, 18.85) * mm, "end": v(-7.07, 18.5) * mm});
            skLineSegment(sketch, "E1998", {"start": v(-7.07, 18.5) * mm, "end": v(-8.21, 18.1) * mm});
            skLineSegment(sketch, "E1999", {"start": v(-8.21, 18.1) * mm, "end": v(-9.34, 17.6) * mm});
            skLineSegment(sketch, "E2000", {"start": v(-9.34, 17.6) * mm, "end": v(-10.43, 17.05) * mm});
            skLineSegment(sketch, "E2001", {"start": v(-10.43, 17.05) * mm, "end": v(-11.48, 16.43) * mm});
            skLineSegment(sketch, "E2002", {"start": v(-11.48, 16.43) * mm, "end": v(-12.49, 15.74) * mm});
            skLineSegment(sketch, "E2003", {"start": v(-12.49, 15.74) * mm, "end": v(-13.46, 15) * mm});
            skLineSegment(sketch, "E2004", {"start": v(-13.46, 15) * mm, "end": v(-14.37, 14.18) * mm});
            skLineSegment(sketch, "E2005", {"start": v(-14.37, 14.18) * mm, "end": v(-15.24, 13.32) * mm});
            skLineSegment(sketch, "E2006", {"start": v(-15.24, 13.32) * mm, "end": v(-16.04, 12.4) * mm});
            skLineSegment(sketch, "E2007", {"start": v(-16.04, 12.4) * mm, "end": v(-16.8, 11.44) * mm});
            skLineSegment(sketch, "E2008", {"start": v(-16.8, 11.44) * mm, "end": v(-17.48, 10.43) * mm});
            skLineSegment(sketch, "E2009", {"start": v(-17.48, 10.43) * mm, "end": v(-18.1, 9.37) * mm});
            skLineSegment(sketch, "E2010", {"start": v(-18.1, 9.37) * mm, "end": v(-18.66, 8.28) * mm});
            skLineSegment(sketch, "E2011", {"start": v(-18.66, 8.28) * mm, "end": v(-19.14, 7.16) * mm});
            skLineSegment(sketch, "E2012", {"start": v(-19.14, 7.16) * mm, "end": v(-19.56, 6.01) * mm});
            skLineSegment(sketch, "E2013", {"start": v(-19.56, 6.01) * mm, "end": v(-19.9, 4.84) * mm});
            skLineSegment(sketch, "E2014", {"start": v(-19.9, 4.84) * mm, "end": v(-20.17, 3.65) * mm});
            skLineSegment(sketch, "E2015", {"start": v(-20.17, 3.65) * mm, "end": v(-20.36, 2.44) * mm});
            skLineSegment(sketch, "E2016", {"start": v(-20.36, 2.44) * mm, "end": v(-20.47, 1.22) * mm});
            skLineSegment(sketch, "E2017", {"start": v(-20.47, 1.22) * mm, "end": v(-20.47, 1.14) * mm});
            skLineSegment(sketch, "E2018", {"start": v(-20.47, 1.14) * mm, "end": v(-4.86, 1.1) * mm});
            skLineSegment(sketch, "E2019", {"start": v(-4.86, 1.1) * mm, "end": v(-4.82, 1.22) * mm});
            skLineSegment(sketch, "E2020", {"start": v(18.37, 1.14) * mm, "end": v(18.37, 1.22) * mm});
            skLineSegment(sketch, "E2021", {"start": v(18.37, 1.22) * mm, "end": v(18.25, 2.44) * mm});
            skLineSegment(sketch, "E2022", {"start": v(18.25, 2.44) * mm, "end": v(18.06, 3.65) * mm});
            skLineSegment(sketch, "E2023", {"start": v(18.06, 3.65) * mm, "end": v(17.8, 4.84) * mm});
            skLineSegment(sketch, "E2024", {"start": v(17.8, 4.84) * mm, "end": v(17.45, 6.01) * mm});
            skLineSegment(sketch, "E2025", {"start": v(17.45, 6.01) * mm, "end": v(17.04, 7.16) * mm});
            skLineSegment(sketch, "E2026", {"start": v(17.04, 7.16) * mm, "end": v(16.55, 8.28) * mm});
            skLineSegment(sketch, "E2027", {"start": v(16.55, 8.28) * mm, "end": v(16, 9.37) * mm});
            skLineSegment(sketch, "E2028", {"start": v(16, 9.37) * mm, "end": v(15.38, 10.43) * mm});
            skLineSegment(sketch, "E2029", {"start": v(15.38, 10.43) * mm, "end": v(14.7, 11.44) * mm});
            skLineSegment(sketch, "E2030", {"start": v(14.7, 11.44) * mm, "end": v(13.94, 12.4) * mm});
            skLineSegment(sketch, "E2031", {"start": v(13.94, 12.4) * mm, "end": v(13.13, 13.32) * mm});
            skLineSegment(sketch, "E2032", {"start": v(13.13, 13.32) * mm, "end": v(12.27, 14.18) * mm});
            skLineSegment(sketch, "E2033", {"start": v(12.27, 14.18) * mm, "end": v(11.35, 15) * mm});
            skLineSegment(sketch, "E2034", {"start": v(11.35, 15) * mm, "end": v(10.39, 15.74) * mm});
            skLineSegment(sketch, "E2035", {"start": v(10.39, 15.74) * mm, "end": v(9.37, 16.43) * mm});
            skLineSegment(sketch, "E2036", {"start": v(9.37, 16.43) * mm, "end": v(8.32, 17.05) * mm});
            skLineSegment(sketch, "E2037", {"start": v(8.32, 17.05) * mm, "end": v(7.23, 17.6) * mm});
            skLineSegment(sketch, "E2038", {"start": v(7.23, 17.6) * mm, "end": v(6.11, 18.1) * mm});
            skLineSegment(sketch, "E2039", {"start": v(6.11, 18.1) * mm, "end": v(4.96, 18.5) * mm});
            skLineSegment(sketch, "E2040", {"start": v(4.96, 18.5) * mm, "end": v(3.79, 18.85) * mm});
            skLineSegment(sketch, "E2041", {"start": v(3.79, 18.85) * mm, "end": v(2.6, 19.11) * mm});
            skLineSegment(sketch, "E2042", {"start": v(2.6, 19.11) * mm, "end": v(1.39, 19.3) * mm});
            skLineSegment(sketch, "E2043", {"start": v(1.39, 19.3) * mm, "end": v(0.17, 19.42) * mm});
            skLineSegment(sketch, "E2044", {"start": v(0.17, 19.42) * mm, "end": v(0.08, 19.42) * mm});
            skLineSegment(sketch, "E2045", {"start": v(0.08, 19.42) * mm, "end": v(0.04, 3.8) * mm});
            skLineSegment(sketch, "E2046", {"start": v(0.04, 3.8) * mm, "end": v(0.17, 3.77) * mm});
            skLineSegment(sketch, "E2047", {"start": v(0.17, 3.77) * mm, "end": v(0.4, 3.68) * mm});
            skLineSegment(sketch, "E2048", {"start": v(0.4, 3.68) * mm, "end": v(0.64, 3.59) * mm});
            skLineSegment(sketch, "E2049", {"start": v(0.64, 3.59) * mm, "end": v(0.86, 3.47) * mm});
            skLineSegment(sketch, "E2050", {"start": v(0.86, 3.47) * mm, "end": v(1.07, 3.35) * mm});
            skLineSegment(sketch, "E2051", {"start": v(1.07, 3.35) * mm, "end": v(1.28, 3.2) * mm});
            skLineSegment(sketch, "E2052", {"start": v(1.28, 3.2) * mm, "end": v(1.47, 3.05) * mm});
            skLineSegment(sketch, "E2053", {"start": v(1.47, 3.05) * mm, "end": v(1.66, 2.89) * mm});
            skLineSegment(sketch, "E2054", {"start": v(1.66, 2.89) * mm, "end": v(1.84, 2.71) * mm});
            skLineSegment(sketch, "E2055", {"start": v(1.84, 2.71) * mm, "end": v(2, 2.53) * mm});
            skLineSegment(sketch, "E2056", {"start": v(2, 2.53) * mm, "end": v(2.15, 2.33) * mm});
            skLineSegment(sketch, "E2057", {"start": v(2.15, 2.33) * mm, "end": v(2.3, 2.12) * mm});
            skLineSegment(sketch, "E2058", {"start": v(2.3, 2.12) * mm, "end": v(2.42, 1.9) * mm});
            skLineSegment(sketch, "E2059", {"start": v(2.42, 1.9) * mm, "end": v(2.53, 1.69) * mm});
            skLineSegment(sketch, "E2060", {"start": v(2.53, 1.69) * mm, "end": v(2.63, 1.46) * mm});
            skLineSegment(sketch, "E2061", {"start": v(2.63, 1.46) * mm, "end": v(2.72, 1.22) * mm});
            skLineSegment(sketch, "E2062", {"start": v(2.72, 1.22) * mm, "end": v(2.75, 1.1) * mm});
            skLineSegment(sketch, "E2063", {"start": v(2.75, 1.1) * mm, "end": v(18.37, 1.14) * mm});
            skLineSegment(sketch, "E2064", {"start": v(0.17, -19.42) * mm, "end": v(1.39, -19.3) * mm});
            skLineSegment(sketch, "E2065", {"start": v(1.39, -19.3) * mm, "end": v(2.6, -19.11) * mm});
            skLineSegment(sketch, "E2066", {"start": v(2.6, -19.11) * mm, "end": v(3.79, -18.85) * mm});
            skLineSegment(sketch, "E2067", {"start": v(3.79, -18.85) * mm, "end": v(4.96, -18.5) * mm});
            skLineSegment(sketch, "E2068", {"start": v(4.96, -18.5) * mm, "end": v(6.11, -18.1) * mm});
            skLineSegment(sketch, "E2069", {"start": v(6.11, -18.1) * mm, "end": v(7.23, -17.6) * mm});
            skLineSegment(sketch, "E2070", {"start": v(7.23, -17.6) * mm, "end": v(8.32, -17.05) * mm});
            skLineSegment(sketch, "E2071", {"start": v(8.32, -17.05) * mm, "end": v(9.37, -16.43) * mm});
            skLineSegment(sketch, "E2072", {"start": v(9.37, -16.43) * mm, "end": v(10.39, -15.74) * mm});
            skLineSegment(sketch, "E2073", {"start": v(10.39, -15.74) * mm, "end": v(11.35, -15) * mm});
            skLineSegment(sketch, "E2074", {"start": v(11.35, -15) * mm, "end": v(12.27, -14.18) * mm});
            skLineSegment(sketch, "E2075", {"start": v(12.27, -14.18) * mm, "end": v(13.13, -13.32) * mm});
            skLineSegment(sketch, "E2076", {"start": v(13.13, -13.32) * mm, "end": v(13.94, -12.4) * mm});
            skLineSegment(sketch, "E2077", {"start": v(13.94, -12.4) * mm, "end": v(14.7, -11.44) * mm});
            skLineSegment(sketch, "E2078", {"start": v(14.7, -11.44) * mm, "end": v(15.38, -10.43) * mm});
            skLineSegment(sketch, "E2079", {"start": v(15.38, -10.43) * mm, "end": v(16, -9.37) * mm});
            skLineSegment(sketch, "E2080", {"start": v(16, -9.37) * mm, "end": v(16.55, -8.28) * mm});
            skLineSegment(sketch, "E2081", {"start": v(16.55, -8.28) * mm, "end": v(17.04, -7.16) * mm});
            skLineSegment(sketch, "E2082", {"start": v(17.04, -7.16) * mm, "end": v(17.45, -6.01) * mm});
            skLineSegment(sketch, "E2083", {"start": v(17.45, -6.01) * mm, "end": v(17.8, -4.84) * mm});
            skLineSegment(sketch, "E2084", {"start": v(17.8, -4.84) * mm, "end": v(18.06, -3.65) * mm});
            skLineSegment(sketch, "E2085", {"start": v(18.06, -3.65) * mm, "end": v(18.25, -2.44) * mm});
            skLineSegment(sketch, "E2086", {"start": v(18.25, -2.44) * mm, "end": v(18.37, -1.22) * mm});
            skLineSegment(sketch, "E2087", {"start": v(18.37, -1.22) * mm, "end": v(18.37, -1.14) * mm});
            skLineSegment(sketch, "E2088", {"start": v(18.37, -1.14) * mm, "end": v(2.75, -1.1) * mm});
            skLineSegment(sketch, "E2089", {"start": v(2.75, -1.1) * mm, "end": v(2.72, -1.22) * mm});
            skLineSegment(sketch, "E2090", {"start": v(2.72, -1.22) * mm, "end": v(2.63, -1.46) * mm});
            skLineSegment(sketch, "E2091", {"start": v(2.63, -1.46) * mm, "end": v(2.53, -1.69) * mm});
            skLineSegment(sketch, "E2092", {"start": v(2.53, -1.69) * mm, "end": v(2.42, -1.9) * mm});
            skLineSegment(sketch, "E2093", {"start": v(2.42, -1.9) * mm, "end": v(2.3, -2.12) * mm});
            skLineSegment(sketch, "E2094", {"start": v(2.3, -2.12) * mm, "end": v(2.15, -2.33) * mm});
            skLineSegment(sketch, "E2095", {"start": v(2.15, -2.33) * mm, "end": v(2, -2.53) * mm});
            skLineSegment(sketch, "E2096", {"start": v(2, -2.53) * mm, "end": v(1.84, -2.71) * mm});
            skLineSegment(sketch, "E2097", {"start": v(1.84, -2.71) * mm, "end": v(1.66, -2.89) * mm});
            skLineSegment(sketch, "E2098", {"start": v(1.66, -2.89) * mm, "end": v(1.47, -3.05) * mm});
            skLineSegment(sketch, "E2099", {"start": v(1.47, -3.05) * mm, "end": v(1.28, -3.2) * mm});
            skLineSegment(sketch, "E2100", {"start": v(1.28, -3.2) * mm, "end": v(1.07, -3.35) * mm});
            skLineSegment(sketch, "E2101", {"start": v(1.07, -3.35) * mm, "end": v(0.86, -3.47) * mm});
            skLineSegment(sketch, "E2102", {"start": v(0.86, -3.47) * mm, "end": v(0.64, -3.59) * mm});
            skLineSegment(sketch, "E2103", {"start": v(0.64, -3.59) * mm, "end": v(0.4, -3.68) * mm});
            skLineSegment(sketch, "E2104", {"start": v(0.4, -3.68) * mm, "end": v(0.17, -3.77) * mm});
            skLineSegment(sketch, "E2105", {"start": v(0.17, -3.77) * mm, "end": v(0.04, -3.8) * mm});
            skLineSegment(sketch, "E2106", {"start": v(0.04, -3.8) * mm, "end": v(0.08, -19.42) * mm});
            skLineSegment(sketch, "E2107", {"start": v(0.08, -19.42) * mm, "end": v(0.17, -19.42) * mm});
            skLineSegment(sketch, "E2108", {"start": v(-2.14, -3.8) * mm, "end": v(-2.28, -3.77) * mm});
            skLineSegment(sketch, "E2109", {"start": v(-2.28, -3.77) * mm, "end": v(-2.51, -3.68) * mm});
            skLineSegment(sketch, "E2110", {"start": v(-2.51, -3.68) * mm, "end": v(-2.74, -3.59) * mm});
            skLineSegment(sketch, "E2111", {"start": v(-2.74, -3.59) * mm, "end": v(-2.96, -3.47) * mm});
            skLineSegment(sketch, "E2112", {"start": v(-2.96, -3.47) * mm, "end": v(-3.17, -3.35) * mm});
            skLineSegment(sketch, "E2113", {"start": v(-3.17, -3.35) * mm, "end": v(-3.38, -3.2) * mm});
            skLineSegment(sketch, "E2114", {"start": v(-3.38, -3.2) * mm, "end": v(-3.58, -3.05) * mm});
            skLineSegment(sketch, "E2115", {"start": v(-3.58, -3.05) * mm, "end": v(-3.76, -2.89) * mm});
            skLineSegment(sketch, "E2116", {"start": v(-3.76, -2.89) * mm, "end": v(-3.94, -2.71) * mm});
            skLineSegment(sketch, "E2117", {"start": v(-3.94, -2.71) * mm, "end": v(-4.1, -2.53) * mm});
            skLineSegment(sketch, "E2118", {"start": v(-4.1, -2.53) * mm, "end": v(-4.26, -2.33) * mm});
            skLineSegment(sketch, "E2119", {"start": v(-4.26, -2.33) * mm, "end": v(-4.4, -2.12) * mm});
            skLineSegment(sketch, "E2120", {"start": v(-4.4, -2.12) * mm, "end": v(-4.52, -1.9) * mm});
            skLineSegment(sketch, "E2121", {"start": v(-4.52, -1.9) * mm, "end": v(-4.64, -1.69) * mm});
            skLineSegment(sketch, "E2122", {"start": v(-4.64, -1.69) * mm, "end": v(-4.74, -1.46) * mm});
            skLineSegment(sketch, "E2123", {"start": v(-4.74, -1.46) * mm, "end": v(-4.82, -1.22) * mm});
            skLineSegment(sketch, "E2124", {"start": v(-4.82, -1.22) * mm, "end": v(-4.86, -1.1) * mm});
            skLineSegment(sketch, "E2125", {"start": v(-4.86, -1.1) * mm, "end": v(-20.47, -1.14) * mm});
            skLineSegment(sketch, "E2126", {"start": v(-20.47, -1.14) * mm, "end": v(-20.47, -1.22) * mm});
            skLineSegment(sketch, "E2127", {"start": v(-20.47, -1.22) * mm, "end": v(-20.36, -2.44) * mm});
            skLineSegment(sketch, "E2128", {"start": v(-20.36, -2.44) * mm, "end": v(-20.17, -3.65) * mm});
            skLineSegment(sketch, "E2129", {"start": v(-20.17, -3.65) * mm, "end": v(-19.9, -4.84) * mm});
            skLineSegment(sketch, "E2130", {"start": v(-19.9, -4.84) * mm, "end": v(-19.56, -6.01) * mm});
            skLineSegment(sketch, "E2131", {"start": v(-19.56, -6.01) * mm, "end": v(-19.14, -7.16) * mm});
            skLineSegment(sketch, "E2132", {"start": v(-19.14, -7.16) * mm, "end": v(-18.66, -8.28) * mm});
            skLineSegment(sketch, "E2133", {"start": v(-18.66, -8.28) * mm, "end": v(-18.1, -9.37) * mm});
            skLineSegment(sketch, "E2134", {"start": v(-18.1, -9.37) * mm, "end": v(-17.48, -10.43) * mm});
            skLineSegment(sketch, "E2135", {"start": v(-17.48, -10.43) * mm, "end": v(-16.8, -11.44) * mm});
            skLineSegment(sketch, "E2136", {"start": v(-16.8, -11.44) * mm, "end": v(-16.04, -12.4) * mm});
            skLineSegment(sketch, "E2137", {"start": v(-16.04, -12.4) * mm, "end": v(-15.24, -13.32) * mm});
            skLineSegment(sketch, "E2138", {"start": v(-15.24, -13.32) * mm, "end": v(-14.37, -14.18) * mm});
            skLineSegment(sketch, "E2139", {"start": v(-14.37, -14.18) * mm, "end": v(-13.46, -15) * mm});
            skLineSegment(sketch, "E2140", {"start": v(-13.46, -15) * mm, "end": v(-12.49, -15.74) * mm});
            skLineSegment(sketch, "E2141", {"start": v(-12.49, -15.74) * mm, "end": v(-11.48, -16.43) * mm});
            skLineSegment(sketch, "E2142", {"start": v(-11.48, -16.43) * mm, "end": v(-10.43, -17.05) * mm});
            skLineSegment(sketch, "E2143", {"start": v(-10.43, -17.05) * mm, "end": v(-9.34, -17.6) * mm});
            skLineSegment(sketch, "E2144", {"start": v(-9.34, -17.6) * mm, "end": v(-8.21, -18.1) * mm});
            skLineSegment(sketch, "E2145", {"start": v(-8.21, -18.1) * mm, "end": v(-7.07, -18.5) * mm});
            skLineSegment(sketch, "E2146", {"start": v(-7.07, -18.5) * mm, "end": v(-5.9, -18.85) * mm});
            skLineSegment(sketch, "E2147", {"start": v(-5.9, -18.85) * mm, "end": v(-4.7, -19.11) * mm});
            skLineSegment(sketch, "E2148", {"start": v(-4.7, -19.11) * mm, "end": v(-3.5, -19.3) * mm});
            skLineSegment(sketch, "E2149", {"start": v(-3.5, -19.3) * mm, "end": v(-2.27, -19.42) * mm});
            skLineSegment(sketch, "E2150", {"start": v(-2.27, -19.42) * mm, "end": v(-2.19, -19.42) * mm});
            skLineSegment(sketch, "E2151", {"start": v(-2.19, -19.42) * mm, "end": v(-2.14, -3.8) * mm});
            skCircle(sketch, "E2152", {"center": v(-1.05, 0) * mm, "radius": 2.65 * mm});
            skCircle(sketch, "E2153", {"center": v(-1.05, 0) * mm, "radius": 5.73 * mm});
            skSolve(sketch);
        }
        {
            var Q0;
            Q0=makeQuery(id+"F0.imprint","IMPRINT",FACE,{"disambiguationData":[TD([[makeQuery(id+"F0.imprint","IMPRINT",EDGE,{"derivedFrom":sQuery(id+"F0.wireOp",EDGE,"E0")}),1.0]])]});
            var Q1;
            {var subQ0=sQuery(id+"F0.wireOp",EDGE,"E2089");Q1=makeQuery(id+"F0.imprint","IMPRINT",FACE,{"disambiguationData":[TD([[makeQuery(id+"F0.imprint","IMPRINT",EDGE,{"derivedFrom":subQ0}),1.0]])]});}
            var Q2;
            {var subQ0=sQuery(id+"F0.wireOp",EDGE,"E2108");Q2=makeQuery(id+"F0.imprint","IMPRINT",FACE,{"disambiguationData":[TD([[makeQuery(id+"F0.imprint","IMPRINT",EDGE,{"derivedFrom":subQ0}),1.0]])]});}
            var Q3;
            Q3=makeQuery(id+"F0.imprint","IMPRINT",FACE,{"disambiguationData":[TD([[makeQuery(id+"F0.imprint","IMPRINT",EDGE,{"derivedFrom":sQuery(id+"F0.wireOp",EDGE,"E1976")}),1.0]])]});
            var Q4;
            {var subQ0=sQuery(id+"F0.wireOp",EDGE,"E2046");Q4=makeQuery(id+"F0.imprint","IMPRINT",FACE,{"disambiguationData":[TD([[makeQuery(id+"F0.imprint","IMPRINT",EDGE,{"derivedFrom":subQ0}),1.0]])]});}
            var Q5;
            Q5=makeQuery(id+"F0.imprint","IMPRINT",FACE,{"disambiguationData":[TD([[makeQuery(id+"F0.imprint","IMPRINT",EDGE,{"derivedFrom":sQuery(id+"F0.wireOp",EDGE,"E1976")}),-1.0]])]});
            extrude(context, id + "F1", {"entities" : qUnion([Q0, Q1, Q2, Q3, Q4, Q5]), "depth" : 8 * mm});
        }
        {
            var Q0;
            Q0=makeQuery(id+"F1.opExtrude","CAP_FACE",FACE,{"disambiguationData":[OSD([sQuery(id+"F0.wireOp",EDGE,"E0"),sQuery(id+"F0.wireOp",EDGE,"E1"),sQuery(id+"F0.wireOp",EDGE,"E2"),sQuery(id+"F0.wireOp",EDGE,"E3"),sQuery(id+"F0.wireOp",EDGE,"E4"),sQuery(id+"F0.wireOp",EDGE,"E5"),sQuery(id+"F0.wireOp",EDGE,"E6"),sQuery(id+"F0.wireOp",EDGE,"E7"),sQuery(id+"F0.wireOp",EDGE,"E8"),sQuery(id+"F0.wireOp",EDGE,"E9"),sQuery(id+"F0.wireOp",EDGE,"E10"),sQuery(id+"F0.wireOp",EDGE,"E11"),sQuery(id+"F0.wireOp",EDGE,"E12"),sQuery(id+"F0.wireOp",EDGE,"E13"),sQuery(id+"F0.wireOp",EDGE,"E14"),sQuery(id+"F0.wireOp",EDGE,"E15"),sQuery(id+"F0.wireOp",EDGE,"E16"),sQuery(id+"F0.wireOp",EDGE,"E17"),sQuery(id+"F0.wireOp",EDGE,"E18"),sQuery(id+"F0.wireOp",EDGE,"E19"),sQuery(id+"F0.wireOp",EDGE,"E20"),sQuery(id+"F0.wireOp",EDGE,"E21"),sQuery(id+"F0.wireOp",EDGE,"E22"),sQuery(id+"F0.wireOp",EDGE,"E23"),sQuery(id+"F0.wireOp",EDGE,"E24"),sQuery(id+"F0.wireOp",EDGE,"E25"),sQuery(id+"F0.wireOp",EDGE,"E26"),sQuery(id+"F0.wireOp",EDGE,"E27"),sQuery(id+"F0.wireOp",EDGE,"E28"),sQuery(id+"F0.wireOp",EDGE,"E29"),sQuery(id+"F0.wireOp",EDGE,"E30"),sQuery(id+"F0.wireOp",EDGE,"E31"),sQuery(id+"F0.wireOp",EDGE,"E32"),sQuery(id+"F0.wireOp",EDGE,"E33"),sQuery(id+"F0.wireOp",EDGE,"E34"),sQuery(id+"F0.wireOp",EDGE,"E35"),sQuery(id+"F0.wireOp",EDGE,"E36"),sQuery(id+"F0.wireOp",EDGE,"E37"),sQuery(id+"F0.wireOp",EDGE,"E38"),sQuery(id+"F0.wireOp",EDGE,"E39"),sQuery(id+"F0.wireOp",EDGE,"E40"),sQuery(id+"F0.wireOp",EDGE,"E41"),sQuery(id+"F0.wireOp",EDGE,"E42"),sQuery(id+"F0.wireOp",EDGE,"E43"),sQuery(id+"F0.wireOp",EDGE,"E44"),sQuery(id+"F0.wireOp",EDGE,"E45"),sQuery(id+"F0.wireOp",EDGE,"E46"),sQuery(id+"F0.wireOp",EDGE,"E47"),sQuery(id+"F0.wireOp",EDGE,"E48"),sQuery(id+"F0.wireOp",EDGE,"E49"),sQuery(id+"F0.wireOp",EDGE,"E50"),sQuery(id+"F0.wireOp",EDGE,"E51"),sQuery(id+"F0.wireOp",EDGE,"E52"),sQuery(id+"F0.wireOp",EDGE,"E53"),sQuery(id+"F0.wireOp",EDGE,"E54"),sQuery(id+"F0.wireOp",EDGE,"E55"),sQuery(id+"F0.wireOp",EDGE,"E56"),sQuery(id+"F0.wireOp",EDGE,"E57"),sQuery(id+"F0.wireOp",EDGE,"E58"),sQuery(id+"F0.wireOp",EDGE,"E59"),sQuery(id+"F0.wireOp",EDGE,"E60"),sQuery(id+"F0.wireOp",EDGE,"E61"),sQuery(id+"F0.wireOp",EDGE,"E62"),sQuery(id+"F0.wireOp",EDGE,"E63"),sQuery(id+"F0.wireOp",EDGE,"E64"),sQuery(id+"F0.wireOp",EDGE,"E65"),sQuery(id+"F0.wireOp",EDGE,"E66"),sQuery(id+"F0.wireOp",EDGE,"E67"),sQuery(id+"F0.wireOp",EDGE,"E68"),sQuery(id+"F0.wireOp",EDGE,"E69"),sQuery(id+"F0.wireOp",EDGE,"E70"),sQuery(id+"F0.wireOp",EDGE,"E71"),sQuery(id+"F0.wireOp",EDGE,"E72"),sQuery(id+"F0.wireOp",EDGE,"E73"),sQuery(id+"F0.wireOp",EDGE,"E74"),sQuery(id+"F0.wireOp",EDGE,"E75"),sQuery(id+"F0.wireOp",EDGE,"E76"),sQuery(id+"F0.wireOp",EDGE,"E77"),sQuery(id+"F0.wireOp",EDGE,"E78"),sQuery(id+"F0.wireOp",EDGE,"E79"),sQuery(id+"F0.wireOp",EDGE,"E80"),sQuery(id+"F0.wireOp",EDGE,"E81"),sQuery(id+"F0.wireOp",EDGE,"E82"),sQuery(id+"F0.wireOp",EDGE,"E83"),sQuery(id+"F0.wireOp",EDGE,"E84"),sQuery(id+"F0.wireOp",EDGE,"E85"),sQuery(id+"F0.wireOp",EDGE,"E86"),sQuery(id+"F0.wireOp",EDGE,"E87"),sQuery(id+"F0.wireOp",EDGE,"E88"),sQuery(id+"F0.wireOp",EDGE,"E89"),sQuery(id+"F0.wireOp",EDGE,"E90"),sQuery(id+"F0.wireOp",EDGE,"E91"),sQuery(id+"F0.wireOp",EDGE,"E92"),sQuery(id+"F0.wireOp",EDGE,"E93"),sQuery(id+"F0.wireOp",EDGE,"E94"),sQuery(id+"F0.wireOp",EDGE,"E95"),sQuery(id+"F0.wireOp",EDGE,"E96"),sQuery(id+"F0.wireOp",EDGE,"E97"),sQuery(id+"F0.wireOp",EDGE,"E98"),sQuery(id+"F0.wireOp",EDGE,"E99"),sQuery(id+"F0.wireOp",EDGE,"E100"),sQuery(id+"F0.wireOp",EDGE,"E101"),sQuery(id+"F0.wireOp",EDGE,"E102"),sQuery(id+"F0.wireOp",EDGE,"E103"),sQuery(id+"F0.wireOp",EDGE,"E104"),sQuery(id+"F0.wireOp",EDGE,"E105"),sQuery(id+"F0.wireOp",EDGE,"E106"),sQuery(id+"F0.wireOp",EDGE,"E107"),sQuery(id+"F0.wireOp",EDGE,"E108"),sQuery(id+"F0.wireOp",EDGE,"E109"),sQuery(id+"F0.wireOp",EDGE,"E110"),sQuery(id+"F0.wireOp",EDGE,"E111"),sQuery(id+"F0.wireOp",EDGE,"E112"),sQuery(id+"F0.wireOp",EDGE,"E113"),sQuery(id+"F0.wireOp",EDGE,"E114"),sQuery(id+"F0.wireOp",EDGE,"E115"),sQuery(id+"F0.wireOp",EDGE,"E116"),sQuery(id+"F0.wireOp",EDGE,"E117"),sQuery(id+"F0.wireOp",EDGE,"E118"),sQuery(id+"F0.wireOp",EDGE,"E119"),sQuery(id+"F0.wireOp",EDGE,"E120"),sQuery(id+"F0.wireOp",EDGE,"E121"),sQuery(id+"F0.wireOp",EDGE,"E122"),sQuery(id+"F0.wireOp",EDGE,"E123"),sQuery(id+"F0.wireOp",EDGE,"E124"),sQuery(id+"F0.wireOp",EDGE,"E125"),sQuery(id+"F0.wireOp",EDGE,"E126"),sQuery(id+"F0.wireOp",EDGE,"E127"),sQuery(id+"F0.wireOp",EDGE,"E128"),sQuery(id+"F0.wireOp",EDGE,"E129"),sQuery(id+"F0.wireOp",EDGE,"E130"),sQuery(id+"F0.wireOp",EDGE,"E131"),sQuery(id+"F0.wireOp",EDGE,"E132"),sQuery(id+"F0.wireOp",EDGE,"E133"),sQuery(id+"F0.wireOp",EDGE,"E134"),sQuery(id+"F0.wireOp",EDGE,"E135"),sQuery(id+"F0.wireOp",EDGE,"E136"),sQuery(id+"F0.wireOp",EDGE,"E137"),sQuery(id+"F0.wireOp",EDGE,"E138"),sQuery(id+"F0.wireOp",EDGE,"E139"),sQuery(id+"F0.wireOp",EDGE,"E140"),sQuery(id+"F0.wireOp",EDGE,"E141"),sQuery(id+"F0.wireOp",EDGE,"E142"),sQuery(id+"F0.wireOp",EDGE,"E143"),sQuery(id+"F0.wireOp",EDGE,"E144"),sQuery(id+"F0.wireOp",EDGE,"E145"),sQuery(id+"F0.wireOp",EDGE,"E146"),sQuery(id+"F0.wireOp",EDGE,"E147"),sQuery(id+"F0.wireOp",EDGE,"E148"),sQuery(id+"F0.wireOp",EDGE,"E149"),sQuery(id+"F0.wireOp",EDGE,"E150"),sQuery(id+"F0.wireOp",EDGE,"E151"),sQuery(id+"F0.wireOp",EDGE,"E152"),sQuery(id+"F0.wireOp",EDGE,"E153"),sQuery(id+"F0.wireOp",EDGE,"E154"),sQuery(id+"F0.wireOp",EDGE,"E155"),sQuery(id+"F0.wireOp",EDGE,"E156"),sQuery(id+"F0.wireOp",EDGE,"E157"),sQuery(id+"F0.wireOp",EDGE,"E158"),sQuery(id+"F0.wireOp",EDGE,"E159"),sQuery(id+"F0.wireOp",EDGE,"E160"),sQuery(id+"F0.wireOp",EDGE,"E161"),sQuery(id+"F0.wireOp",EDGE,"E162"),sQuery(id+"F0.wireOp",EDGE,"E163"),sQuery(id+"F0.wireOp",EDGE,"E164"),sQuery(id+"F0.wireOp",EDGE,"E165"),sQuery(id+"F0.wireOp",EDGE,"E166"),sQuery(id+"F0.wireOp",EDGE,"E167"),sQuery(id+"F0.wireOp",EDGE,"E168"),sQuery(id+"F0.wireOp",EDGE,"E169"),sQuery(id+"F0.wireOp",EDGE,"E170"),sQuery(id+"F0.wireOp",EDGE,"E171"),sQuery(id+"F0.wireOp",EDGE,"E172"),sQuery(id+"F0.wireOp",EDGE,"E173"),sQuery(id+"F0.wireOp",EDGE,"E174"),sQuery(id+"F0.wireOp",EDGE,"E175"),sQuery(id+"F0.wireOp",EDGE,"E176"),sQuery(id+"F0.wireOp",EDGE,"E177"),sQuery(id+"F0.wireOp",EDGE,"E178"),sQuery(id+"F0.wireOp",EDGE,"E179"),sQuery(id+"F0.wireOp",EDGE,"E180"),sQuery(id+"F0.wireOp",EDGE,"E181"),sQuery(id+"F0.wireOp",EDGE,"E182"),sQuery(id+"F0.wireOp",EDGE,"E183"),sQuery(id+"F0.wireOp",EDGE,"E184"),sQuery(id+"F0.wireOp",EDGE,"E185"),sQuery(id+"F0.wireOp",EDGE,"E186"),sQuery(id+"F0.wireOp",EDGE,"E187"),sQuery(id+"F0.wireOp",EDGE,"E188"),sQuery(id+"F0.wireOp",EDGE,"E189"),sQuery(id+"F0.wireOp",EDGE,"E190"),sQuery(id+"F0.wireOp",EDGE,"E191"),sQuery(id+"F0.wireOp",EDGE,"E192"),sQuery(id+"F0.wireOp",EDGE,"E193"),sQuery(id+"F0.wireOp",EDGE,"E194"),sQuery(id+"F0.wireOp",EDGE,"E195"),sQuery(id+"F0.wireOp",EDGE,"E196"),sQuery(id+"F0.wireOp",EDGE,"E197"),sQuery(id+"F0.wireOp",EDGE,"E198"),sQuery(id+"F0.wireOp",EDGE,"E199"),sQuery(id+"F0.wireOp",EDGE,"E200"),sQuery(id+"F0.wireOp",EDGE,"E201"),sQuery(id+"F0.wireOp",EDGE,"E202"),sQuery(id+"F0.wireOp",EDGE,"E203"),sQuery(id+"F0.wireOp",EDGE,"E204"),sQuery(id+"F0.wireOp",EDGE,"E205"),sQuery(id+"F0.wireOp",EDGE,"E206"),sQuery(id+"F0.wireOp",EDGE,"E207"),sQuery(id+"F0.wireOp",EDGE,"E208"),sQuery(id+"F0.wireOp",EDGE,"E209"),sQuery(id+"F0.wireOp",EDGE,"E210"),sQuery(id+"F0.wireOp",EDGE,"E211"),sQuery(id+"F0.wireOp",EDGE,"E212"),sQuery(id+"F0.wireOp",EDGE,"E213"),sQuery(id+"F0.wireOp",EDGE,"E214"),sQuery(id+"F0.wireOp",EDGE,"E215"),sQuery(id+"F0.wireOp",EDGE,"E216"),sQuery(id+"F0.wireOp",EDGE,"E217"),sQuery(id+"F0.wireOp",EDGE,"E218"),sQuery(id+"F0.wireOp",EDGE,"E219"),sQuery(id+"F0.wireOp",EDGE,"E220"),sQuery(id+"F0.wireOp",EDGE,"E221"),sQuery(id+"F0.wireOp",EDGE,"E222"),sQuery(id+"F0.wireOp",EDGE,"E223"),sQuery(id+"F0.wireOp",EDGE,"E224"),sQuery(id+"F0.wireOp",EDGE,"E225"),sQuery(id+"F0.wireOp",EDGE,"E226"),sQuery(id+"F0.wireOp",EDGE,"E227"),sQuery(id+"F0.wireOp",EDGE,"E228"),sQuery(id+"F0.wireOp",EDGE,"E229"),sQuery(id+"F0.wireOp",EDGE,"E230"),sQuery(id+"F0.wireOp",EDGE,"E231"),sQuery(id+"F0.wireOp",EDGE,"E232"),sQuery(id+"F0.wireOp",EDGE,"E233"),sQuery(id+"F0.wireOp",EDGE,"E234"),sQuery(id+"F0.wireOp",EDGE,"E235"),sQuery(id+"F0.wireOp",EDGE,"E236"),sQuery(id+"F0.wireOp",EDGE,"E237"),sQuery(id+"F0.wireOp",EDGE,"E238"),sQuery(id+"F0.wireOp",EDGE,"E239"),sQuery(id+"F0.wireOp",EDGE,"E240"),sQuery(id+"F0.wireOp",EDGE,"E241"),sQuery(id+"F0.wireOp",EDGE,"E242"),sQuery(id+"F0.wireOp",EDGE,"E243"),sQuery(id+"F0.wireOp",EDGE,"E244"),sQuery(id+"F0.wireOp",EDGE,"E245"),sQuery(id+"F0.wireOp",EDGE,"E246"),sQuery(id+"F0.wireOp",EDGE,"E247"),sQuery(id+"F0.wireOp",EDGE,"E248"),sQuery(id+"F0.wireOp",EDGE,"E249"),sQuery(id+"F0.wireOp",EDGE,"E250"),sQuery(id+"F0.wireOp",EDGE,"E251"),sQuery(id+"F0.wireOp",EDGE,"E252"),sQuery(id+"F0.wireOp",EDGE,"E253"),sQuery(id+"F0.wireOp",EDGE,"E254"),sQuery(id+"F0.wireOp",EDGE,"E255"),sQuery(id+"F0.wireOp",EDGE,"E256"),sQuery(id+"F0.wireOp",EDGE,"E257"),sQuery(id+"F0.wireOp",EDGE,"E258"),sQuery(id+"F0.wireOp",EDGE,"E259"),sQuery(id+"F0.wireOp",EDGE,"E260"),sQuery(id+"F0.wireOp",EDGE,"E261"),sQuery(id+"F0.wireOp",EDGE,"E262"),sQuery(id+"F0.wireOp",EDGE,"E263"),sQuery(id+"F0.wireOp",EDGE,"E264"),sQuery(id+"F0.wireOp",EDGE,"E265"),sQuery(id+"F0.wireOp",EDGE,"E266"),sQuery(id+"F0.wireOp",EDGE,"E267"),sQuery(id+"F0.wireOp",EDGE,"E268"),sQuery(id+"F0.wireOp",EDGE,"E269"),sQuery(id+"F0.wireOp",EDGE,"E270"),sQuery(id+"F0.wireOp",EDGE,"E271"),sQuery(id+"F0.wireOp",EDGE,"E272"),sQuery(id+"F0.wireOp",EDGE,"E273"),sQuery(id+"F0.wireOp",EDGE,"E274"),sQuery(id+"F0.wireOp",EDGE,"E275"),sQuery(id+"F0.wireOp",EDGE,"E276"),sQuery(id+"F0.wireOp",EDGE,"E277"),sQuery(id+"F0.wireOp",EDGE,"E278"),sQuery(id+"F0.wireOp",EDGE,"E279"),sQuery(id+"F0.wireOp",EDGE,"E280"),sQuery(id+"F0.wireOp",EDGE,"E281"),sQuery(id+"F0.wireOp",EDGE,"E282"),sQuery(id+"F0.wireOp",EDGE,"E283"),sQuery(id+"F0.wireOp",EDGE,"E284"),sQuery(id+"F0.wireOp",EDGE,"E285"),sQuery(id+"F0.wireOp",EDGE,"E286"),sQuery(id+"F0.wireOp",EDGE,"E287"),sQuery(id+"F0.wireOp",EDGE,"E288"),sQuery(id+"F0.wireOp",EDGE,"E289"),sQuery(id+"F0.wireOp",EDGE,"E290"),sQuery(id+"F0.wireOp",EDGE,"E291"),sQuery(id+"F0.wireOp",EDGE,"E292"),sQuery(id+"F0.wireOp",EDGE,"E293"),sQuery(id+"F0.wireOp",EDGE,"E294"),sQuery(id+"F0.wireOp",EDGE,"E295"),sQuery(id+"F0.wireOp",EDGE,"E296"),sQuery(id+"F0.wireOp",EDGE,"E297"),sQuery(id+"F0.wireOp",EDGE,"E298"),sQuery(id+"F0.wireOp",EDGE,"E299"),sQuery(id+"F0.wireOp",EDGE,"E300"),sQuery(id+"F0.wireOp",EDGE,"E301"),sQuery(id+"F0.wireOp",EDGE,"E302"),sQuery(id+"F0.wireOp",EDGE,"E303"),sQuery(id+"F0.wireOp",EDGE,"E304"),sQuery(id+"F0.wireOp",EDGE,"E305"),sQuery(id+"F0.wireOp",EDGE,"E306"),sQuery(id+"F0.wireOp",EDGE,"E307"),sQuery(id+"F0.wireOp",EDGE,"E308"),sQuery(id+"F0.wireOp",EDGE,"E309"),sQuery(id+"F0.wireOp",EDGE,"E310"),sQuery(id+"F0.wireOp",EDGE,"E311"),sQuery(id+"F0.wireOp",EDGE,"E312"),sQuery(id+"F0.wireOp",EDGE,"E313"),sQuery(id+"F0.wireOp",EDGE,"E314"),sQuery(id+"F0.wireOp",EDGE,"E315"),sQuery(id+"F0.wireOp",EDGE,"E316"),sQuery(id+"F0.wireOp",EDGE,"E317"),sQuery(id+"F0.wireOp",EDGE,"E318"),sQuery(id+"F0.wireOp",EDGE,"E319"),sQuery(id+"F0.wireOp",EDGE,"E320"),sQuery(id+"F0.wireOp",EDGE,"E321"),sQuery(id+"F0.wireOp",EDGE,"E322"),sQuery(id+"F0.wireOp",EDGE,"E323"),sQuery(id+"F0.wireOp",EDGE,"E324"),sQuery(id+"F0.wireOp",EDGE,"E325"),sQuery(id+"F0.wireOp",EDGE,"E326"),sQuery(id+"F0.wireOp",EDGE,"E327"),sQuery(id+"F0.wireOp",EDGE,"E328"),sQuery(id+"F0.wireOp",EDGE,"E329"),sQuery(id+"F0.wireOp",EDGE,"E330"),sQuery(id+"F0.wireOp",EDGE,"E331"),sQuery(id+"F0.wireOp",EDGE,"E332"),sQuery(id+"F0.wireOp",EDGE,"E333"),sQuery(id+"F0.wireOp",EDGE,"E334"),sQuery(id+"F0.wireOp",EDGE,"E335"),sQuery(id+"F0.wireOp",EDGE,"E336"),sQuery(id+"F0.wireOp",EDGE,"E337"),sQuery(id+"F0.wireOp",EDGE,"E338"),sQuery(id+"F0.wireOp",EDGE,"E339"),sQuery(id+"F0.wireOp",EDGE,"E340"),sQuery(id+"F0.wireOp",EDGE,"E341"),sQuery(id+"F0.wireOp",EDGE,"E342"),sQuery(id+"F0.wireOp",EDGE,"E343"),sQuery(id+"F0.wireOp",EDGE,"E344"),sQuery(id+"F0.wireOp",EDGE,"E345"),sQuery(id+"F0.wireOp",EDGE,"E346"),sQuery(id+"F0.wireOp",EDGE,"E347"),sQuery(id+"F0.wireOp",EDGE,"E348"),sQuery(id+"F0.wireOp",EDGE,"E349"),sQuery(id+"F0.wireOp",EDGE,"E350"),sQuery(id+"F0.wireOp",EDGE,"E351"),sQuery(id+"F0.wireOp",EDGE,"E352"),sQuery(id+"F0.wireOp",EDGE,"E353"),sQuery(id+"F0.wireOp",EDGE,"E354"),sQuery(id+"F0.wireOp",EDGE,"E355"),sQuery(id+"F0.wireOp",EDGE,"E356"),sQuery(id+"F0.wireOp",EDGE,"E357"),sQuery(id+"F0.wireOp",EDGE,"E358"),sQuery(id+"F0.wireOp",EDGE,"E359"),sQuery(id+"F0.wireOp",EDGE,"E360"),sQuery(id+"F0.wireOp",EDGE,"E361"),sQuery(id+"F0.wireOp",EDGE,"E362"),sQuery(id+"F0.wireOp",EDGE,"E363"),sQuery(id+"F0.wireOp",EDGE,"E364"),sQuery(id+"F0.wireOp",EDGE,"E365"),sQuery(id+"F0.wireOp",EDGE,"E366"),sQuery(id+"F0.wireOp",EDGE,"E367"),sQuery(id+"F0.wireOp",EDGE,"E368"),sQuery(id+"F0.wireOp",EDGE,"E369"),sQuery(id+"F0.wireOp",EDGE,"E370"),sQuery(id+"F0.wireOp",EDGE,"E371"),sQuery(id+"F0.wireOp",EDGE,"E372"),sQuery(id+"F0.wireOp",EDGE,"E373"),sQuery(id+"F0.wireOp",EDGE,"E374"),sQuery(id+"F0.wireOp",EDGE,"E375"),sQuery(id+"F0.wireOp",EDGE,"E376"),sQuery(id+"F0.wireOp",EDGE,"E377"),sQuery(id+"F0.wireOp",EDGE,"E378"),sQuery(id+"F0.wireOp",EDGE,"E379"),sQuery(id+"F0.wireOp",EDGE,"E380"),sQuery(id+"F0.wireOp",EDGE,"E381"),sQuery(id+"F0.wireOp",EDGE,"E382"),sQuery(id+"F0.wireOp",EDGE,"E383"),sQuery(id+"F0.wireOp",EDGE,"E384"),sQuery(id+"F0.wireOp",EDGE,"E385"),sQuery(id+"F0.wireOp",EDGE,"E386"),sQuery(id+"F0.wireOp",EDGE,"E387"),sQuery(id+"F0.wireOp",EDGE,"E388"),sQuery(id+"F0.wireOp",EDGE,"E389"),sQuery(id+"F0.wireOp",EDGE,"E390"),sQuery(id+"F0.wireOp",EDGE,"E391"),sQuery(id+"F0.wireOp",EDGE,"E392"),sQuery(id+"F0.wireOp",EDGE,"E393"),sQuery(id+"F0.wireOp",EDGE,"E394"),sQuery(id+"F0.wireOp",EDGE,"E395"),sQuery(id+"F0.wireOp",EDGE,"E396"),sQuery(id+"F0.wireOp",EDGE,"E397"),sQuery(id+"F0.wireOp",EDGE,"E398"),sQuery(id+"F0.wireOp",EDGE,"E399"),sQuery(id+"F0.wireOp",EDGE,"E400"),sQuery(id+"F0.wireOp",EDGE,"E401"),sQuery(id+"F0.wireOp",EDGE,"E402"),sQuery(id+"F0.wireOp",EDGE,"E403"),sQuery(id+"F0.wireOp",EDGE,"E404"),sQuery(id+"F0.wireOp",EDGE,"E405"),sQuery(id+"F0.wireOp",EDGE,"E406"),sQuery(id+"F0.wireOp",EDGE,"E407"),sQuery(id+"F0.wireOp",EDGE,"E408"),sQuery(id+"F0.wireOp",EDGE,"E409"),sQuery(id+"F0.wireOp",EDGE,"E410"),sQuery(id+"F0.wireOp",EDGE,"E411"),sQuery(id+"F0.wireOp",EDGE,"E412"),sQuery(id+"F0.wireOp",EDGE,"E413"),sQuery(id+"F0.wireOp",EDGE,"E414"),sQuery(id+"F0.wireOp",EDGE,"E415"),sQuery(id+"F0.wireOp",EDGE,"E416"),sQuery(id+"F0.wireOp",EDGE,"E417"),sQuery(id+"F0.wireOp",EDGE,"E418"),sQuery(id+"F0.wireOp",EDGE,"E419"),sQuery(id+"F0.wireOp",EDGE,"E420"),sQuery(id+"F0.wireOp",EDGE,"E421"),sQuery(id+"F0.wireOp",EDGE,"E422"),sQuery(id+"F0.wireOp",EDGE,"E423"),sQuery(id+"F0.wireOp",EDGE,"E424"),sQuery(id+"F0.wireOp",EDGE,"E425"),sQuery(id+"F0.wireOp",EDGE,"E426"),sQuery(id+"F0.wireOp",EDGE,"E427"),sQuery(id+"F0.wireOp",EDGE,"E428"),sQuery(id+"F0.wireOp",EDGE,"E429"),sQuery(id+"F0.wireOp",EDGE,"E430"),sQuery(id+"F0.wireOp",EDGE,"E431"),sQuery(id+"F0.wireOp",EDGE,"E432"),sQuery(id+"F0.wireOp",EDGE,"E433"),sQuery(id+"F0.wireOp",EDGE,"E434"),sQuery(id+"F0.wireOp",EDGE,"E435"),sQuery(id+"F0.wireOp",EDGE,"E436"),sQuery(id+"F0.wireOp",EDGE,"E437"),sQuery(id+"F0.wireOp",EDGE,"E438"),sQuery(id+"F0.wireOp",EDGE,"E439"),sQuery(id+"F0.wireOp",EDGE,"E440"),sQuery(id+"F0.wireOp",EDGE,"E441"),sQuery(id+"F0.wireOp",EDGE,"E442"),sQuery(id+"F0.wireOp",EDGE,"E443"),sQuery(id+"F0.wireOp",EDGE,"E444"),sQuery(id+"F0.wireOp",EDGE,"E445"),sQuery(id+"F0.wireOp",EDGE,"E446"),sQuery(id+"F0.wireOp",EDGE,"E447"),sQuery(id+"F0.wireOp",EDGE,"E448"),sQuery(id+"F0.wireOp",EDGE,"E449"),sQuery(id+"F0.wireOp",EDGE,"E450"),sQuery(id+"F0.wireOp",EDGE,"E451"),sQuery(id+"F0.wireOp",EDGE,"E452"),sQuery(id+"F0.wireOp",EDGE,"E453"),sQuery(id+"F0.wireOp",EDGE,"E454"),sQuery(id+"F0.wireOp",EDGE,"E455"),sQuery(id+"F0.wireOp",EDGE,"E456"),sQuery(id+"F0.wireOp",EDGE,"E457"),sQuery(id+"F0.wireOp",EDGE,"E458"),sQuery(id+"F0.wireOp",EDGE,"E459"),sQuery(id+"F0.wireOp",EDGE,"E460"),sQuery(id+"F0.wireOp",EDGE,"E461"),sQuery(id+"F0.wireOp",EDGE,"E462"),sQuery(id+"F0.wireOp",EDGE,"E463"),sQuery(id+"F0.wireOp",EDGE,"E464"),sQuery(id+"F0.wireOp",EDGE,"E465"),sQuery(id+"F0.wireOp",EDGE,"E466"),sQuery(id+"F0.wireOp",EDGE,"E467"),sQuery(id+"F0.wireOp",EDGE,"E468"),sQuery(id+"F0.wireOp",EDGE,"E469"),sQuery(id+"F0.wireOp",EDGE,"E470"),sQuery(id+"F0.wireOp",EDGE,"E471"),sQuery(id+"F0.wireOp",EDGE,"E472"),sQuery(id+"F0.wireOp",EDGE,"E473"),sQuery(id+"F0.wireOp",EDGE,"E474"),sQuery(id+"F0.wireOp",EDGE,"E475"),sQuery(id+"F0.wireOp",EDGE,"E476"),sQuery(id+"F0.wireOp",EDGE,"E477"),sQuery(id+"F0.wireOp",EDGE,"E478"),sQuery(id+"F0.wireOp",EDGE,"E479"),sQuery(id+"F0.wireOp",EDGE,"E480"),sQuery(id+"F0.wireOp",EDGE,"E481"),sQuery(id+"F0.wireOp",EDGE,"E482"),sQuery(id+"F0.wireOp",EDGE,"E483"),sQuery(id+"F0.wireOp",EDGE,"E484"),sQuery(id+"F0.wireOp",EDGE,"E485"),sQuery(id+"F0.wireOp",EDGE,"E486"),sQuery(id+"F0.wireOp",EDGE,"E487"),sQuery(id+"F0.wireOp",EDGE,"E488"),sQuery(id+"F0.wireOp",EDGE,"E489"),sQuery(id+"F0.wireOp",EDGE,"E490"),sQuery(id+"F0.wireOp",EDGE,"E491"),sQuery(id+"F0.wireOp",EDGE,"E492"),sQuery(id+"F0.wireOp",EDGE,"E493"),sQuery(id+"F0.wireOp",EDGE,"E494"),sQuery(id+"F0.wireOp",EDGE,"E495"),sQuery(id+"F0.wireOp",EDGE,"E496"),sQuery(id+"F0.wireOp",EDGE,"E497"),sQuery(id+"F0.wireOp",EDGE,"E498"),sQuery(id+"F0.wireOp",EDGE,"E499"),sQuery(id+"F0.wireOp",EDGE,"E500"),sQuery(id+"F0.wireOp",EDGE,"E501"),sQuery(id+"F0.wireOp",EDGE,"E502"),sQuery(id+"F0.wireOp",EDGE,"E503"),sQuery(id+"F0.wireOp",EDGE,"E504"),sQuery(id+"F0.wireOp",EDGE,"E505"),sQuery(id+"F0.wireOp",EDGE,"E506"),sQuery(id+"F0.wireOp",EDGE,"E507"),sQuery(id+"F0.wireOp",EDGE,"E508"),sQuery(id+"F0.wireOp",EDGE,"E509"),sQuery(id+"F0.wireOp",EDGE,"E510"),sQuery(id+"F0.wireOp",EDGE,"E511"),sQuery(id+"F0.wireOp",EDGE,"E512"),sQuery(id+"F0.wireOp",EDGE,"E513"),sQuery(id+"F0.wireOp",EDGE,"E514"),sQuery(id+"F0.wireOp",EDGE,"E515"),sQuery(id+"F0.wireOp",EDGE,"E516"),sQuery(id+"F0.wireOp",EDGE,"E517"),sQuery(id+"F0.wireOp",EDGE,"E518"),sQuery(id+"F0.wireOp",EDGE,"E519"),sQuery(id+"F0.wireOp",EDGE,"E520"),sQuery(id+"F0.wireOp",EDGE,"E521"),sQuery(id+"F0.wireOp",EDGE,"E522"),sQuery(id+"F0.wireOp",EDGE,"E523"),sQuery(id+"F0.wireOp",EDGE,"E524"),sQuery(id+"F0.wireOp",EDGE,"E525"),sQuery(id+"F0.wireOp",EDGE,"E526"),sQuery(id+"F0.wireOp",EDGE,"E527"),sQuery(id+"F0.wireOp",EDGE,"E528"),sQuery(id+"F0.wireOp",EDGE,"E529"),sQuery(id+"F0.wireOp",EDGE,"E530"),sQuery(id+"F0.wireOp",EDGE,"E531"),sQuery(id+"F0.wireOp",EDGE,"E532"),sQuery(id+"F0.wireOp",EDGE,"E533"),sQuery(id+"F0.wireOp",EDGE,"E534"),sQuery(id+"F0.wireOp",EDGE,"E535"),sQuery(id+"F0.wireOp",EDGE,"E536"),sQuery(id+"F0.wireOp",EDGE,"E537"),sQuery(id+"F0.wireOp",EDGE,"E538"),sQuery(id+"F0.wireOp",EDGE,"E539"),sQuery(id+"F0.wireOp",EDGE,"E540"),sQuery(id+"F0.wireOp",EDGE,"E541"),sQuery(id+"F0.wireOp",EDGE,"E542"),sQuery(id+"F0.wireOp",EDGE,"E543"),sQuery(id+"F0.wireOp",EDGE,"E544"),sQuery(id+"F0.wireOp",EDGE,"E545"),sQuery(id+"F0.wireOp",EDGE,"E546"),sQuery(id+"F0.wireOp",EDGE,"E547"),sQuery(id+"F0.wireOp",EDGE,"E548"),sQuery(id+"F0.wireOp",EDGE,"E549"),sQuery(id+"F0.wireOp",EDGE,"E550"),sQuery(id+"F0.wireOp",EDGE,"E551"),sQuery(id+"F0.wireOp",EDGE,"E552"),sQuery(id+"F0.wireOp",EDGE,"E553"),sQuery(id+"F0.wireOp",EDGE,"E554"),sQuery(id+"F0.wireOp",EDGE,"E555"),sQuery(id+"F0.wireOp",EDGE,"E556"),sQuery(id+"F0.wireOp",EDGE,"E557"),sQuery(id+"F0.wireOp",EDGE,"E558"),sQuery(id+"F0.wireOp",EDGE,"E559"),sQuery(id+"F0.wireOp",EDGE,"E560"),sQuery(id+"F0.wireOp",EDGE,"E561"),sQuery(id+"F0.wireOp",EDGE,"E562"),sQuery(id+"F0.wireOp",EDGE,"E563"),sQuery(id+"F0.wireOp",EDGE,"E564"),sQuery(id+"F0.wireOp",EDGE,"E565"),sQuery(id+"F0.wireOp",EDGE,"E566"),sQuery(id+"F0.wireOp",EDGE,"E567"),sQuery(id+"F0.wireOp",EDGE,"E568"),sQuery(id+"F0.wireOp",EDGE,"E569"),sQuery(id+"F0.wireOp",EDGE,"E570"),sQuery(id+"F0.wireOp",EDGE,"E571"),sQuery(id+"F0.wireOp",EDGE,"E572"),sQuery(id+"F0.wireOp",EDGE,"E573"),sQuery(id+"F0.wireOp",EDGE,"E574"),sQuery(id+"F0.wireOp",EDGE,"E575"),sQuery(id+"F0.wireOp",EDGE,"E576"),sQuery(id+"F0.wireOp",EDGE,"E577"),sQuery(id+"F0.wireOp",EDGE,"E578"),sQuery(id+"F0.wireOp",EDGE,"E579"),sQuery(id+"F0.wireOp",EDGE,"E580"),sQuery(id+"F0.wireOp",EDGE,"E581"),sQuery(id+"F0.wireOp",EDGE,"E582"),sQuery(id+"F0.wireOp",EDGE,"E583"),sQuery(id+"F0.wireOp",EDGE,"E584"),sQuery(id+"F0.wireOp",EDGE,"E585"),sQuery(id+"F0.wireOp",EDGE,"E586"),sQuery(id+"F0.wireOp",EDGE,"E587"),sQuery(id+"F0.wireOp",EDGE,"E588"),sQuery(id+"F0.wireOp",EDGE,"E589"),sQuery(id+"F0.wireOp",EDGE,"E590"),sQuery(id+"F0.wireOp",EDGE,"E591"),sQuery(id+"F0.wireOp",EDGE,"E592"),sQuery(id+"F0.wireOp",EDGE,"E593"),sQuery(id+"F0.wireOp",EDGE,"E594"),sQuery(id+"F0.wireOp",EDGE,"E595"),sQuery(id+"F0.wireOp",EDGE,"E596"),sQuery(id+"F0.wireOp",EDGE,"E597"),sQuery(id+"F0.wireOp",EDGE,"E598"),sQuery(id+"F0.wireOp",EDGE,"E599"),sQuery(id+"F0.wireOp",EDGE,"E600"),sQuery(id+"F0.wireOp",EDGE,"E601"),sQuery(id+"F0.wireOp",EDGE,"E602"),sQuery(id+"F0.wireOp",EDGE,"E603"),sQuery(id+"F0.wireOp",EDGE,"E604"),sQuery(id+"F0.wireOp",EDGE,"E605"),sQuery(id+"F0.wireOp",EDGE,"E606"),sQuery(id+"F0.wireOp",EDGE,"E607"),sQuery(id+"F0.wireOp",EDGE,"E608"),sQuery(id+"F0.wireOp",EDGE,"E609"),sQuery(id+"F0.wireOp",EDGE,"E610"),sQuery(id+"F0.wireOp",EDGE,"E611"),sQuery(id+"F0.wireOp",EDGE,"E612"),sQuery(id+"F0.wireOp",EDGE,"E613"),sQuery(id+"F0.wireOp",EDGE,"E614"),sQuery(id+"F0.wireOp",EDGE,"E615"),sQuery(id+"F0.wireOp",EDGE,"E616"),sQuery(id+"F0.wireOp",EDGE,"E617"),sQuery(id+"F0.wireOp",EDGE,"E618"),sQuery(id+"F0.wireOp",EDGE,"E619"),sQuery(id+"F0.wireOp",EDGE,"E620"),sQuery(id+"F0.wireOp",EDGE,"E621"),sQuery(id+"F0.wireOp",EDGE,"E622"),sQuery(id+"F0.wireOp",EDGE,"E623"),sQuery(id+"F0.wireOp",EDGE,"E624"),sQuery(id+"F0.wireOp",EDGE,"E625"),sQuery(id+"F0.wireOp",EDGE,"E626"),sQuery(id+"F0.wireOp",EDGE,"E627"),sQuery(id+"F0.wireOp",EDGE,"E628"),sQuery(id+"F0.wireOp",EDGE,"E629"),sQuery(id+"F0.wireOp",EDGE,"E630"),sQuery(id+"F0.wireOp",EDGE,"E631"),sQuery(id+"F0.wireOp",EDGE,"E632"),sQuery(id+"F0.wireOp",EDGE,"E633"),sQuery(id+"F0.wireOp",EDGE,"E634"),sQuery(id+"F0.wireOp",EDGE,"E635"),sQuery(id+"F0.wireOp",EDGE,"E636"),sQuery(id+"F0.wireOp",EDGE,"E637"),sQuery(id+"F0.wireOp",EDGE,"E638"),sQuery(id+"F0.wireOp",EDGE,"E639"),sQuery(id+"F0.wireOp",EDGE,"E640"),sQuery(id+"F0.wireOp",EDGE,"E641"),sQuery(id+"F0.wireOp",EDGE,"E642"),sQuery(id+"F0.wireOp",EDGE,"E643"),sQuery(id+"F0.wireOp",EDGE,"E644"),sQuery(id+"F0.wireOp",EDGE,"E645"),sQuery(id+"F0.wireOp",EDGE,"E646"),sQuery(id+"F0.wireOp",EDGE,"E647"),sQuery(id+"F0.wireOp",EDGE,"E648"),sQuery(id+"F0.wireOp",EDGE,"E649"),sQuery(id+"F0.wireOp",EDGE,"E650"),sQuery(id+"F0.wireOp",EDGE,"E651"),sQuery(id+"F0.wireOp",EDGE,"E652"),sQuery(id+"F0.wireOp",EDGE,"E653"),sQuery(id+"F0.wireOp",EDGE,"E654"),sQuery(id+"F0.wireOp",EDGE,"E655"),sQuery(id+"F0.wireOp",EDGE,"E656"),sQuery(id+"F0.wireOp",EDGE,"E657"),sQuery(id+"F0.wireOp",EDGE,"E658"),sQuery(id+"F0.wireOp",EDGE,"E659"),sQuery(id+"F0.wireOp",EDGE,"E660"),sQuery(id+"F0.wireOp",EDGE,"E661"),sQuery(id+"F0.wireOp",EDGE,"E662"),sQuery(id+"F0.wireOp",EDGE,"E663"),sQuery(id+"F0.wireOp",EDGE,"E664"),sQuery(id+"F0.wireOp",EDGE,"E665"),sQuery(id+"F0.wireOp",EDGE,"E666"),sQuery(id+"F0.wireOp",EDGE,"E667"),sQuery(id+"F0.wireOp",EDGE,"E668"),sQuery(id+"F0.wireOp",EDGE,"E669"),sQuery(id+"F0.wireOp",EDGE,"E670"),sQuery(id+"F0.wireOp",EDGE,"E671"),sQuery(id+"F0.wireOp",EDGE,"E672"),sQuery(id+"F0.wireOp",EDGE,"E673"),sQuery(id+"F0.wireOp",EDGE,"E674"),sQuery(id+"F0.wireOp",EDGE,"E675"),sQuery(id+"F0.wireOp",EDGE,"E676"),sQuery(id+"F0.wireOp",EDGE,"E677"),sQuery(id+"F0.wireOp",EDGE,"E678"),sQuery(id+"F0.wireOp",EDGE,"E679"),sQuery(id+"F0.wireOp",EDGE,"E680"),sQuery(id+"F0.wireOp",EDGE,"E681"),sQuery(id+"F0.wireOp",EDGE,"E682"),sQuery(id+"F0.wireOp",EDGE,"E683"),sQuery(id+"F0.wireOp",EDGE,"E684"),sQuery(id+"F0.wireOp",EDGE,"E685"),sQuery(id+"F0.wireOp",EDGE,"E686"),sQuery(id+"F0.wireOp",EDGE,"E687"),sQuery(id+"F0.wireOp",EDGE,"E688"),sQuery(id+"F0.wireOp",EDGE,"E689"),sQuery(id+"F0.wireOp",EDGE,"E690"),sQuery(id+"F0.wireOp",EDGE,"E691"),sQuery(id+"F0.wireOp",EDGE,"E692"),sQuery(id+"F0.wireOp",EDGE,"E693"),sQuery(id+"F0.wireOp",EDGE,"E694"),sQuery(id+"F0.wireOp",EDGE,"E695"),sQuery(id+"F0.wireOp",EDGE,"E696"),sQuery(id+"F0.wireOp",EDGE,"E697"),sQuery(id+"F0.wireOp",EDGE,"E698"),sQuery(id+"F0.wireOp",EDGE,"E699"),sQuery(id+"F0.wireOp",EDGE,"E700"),sQuery(id+"F0.wireOp",EDGE,"E701"),sQuery(id+"F0.wireOp",EDGE,"E702"),sQuery(id+"F0.wireOp",EDGE,"E703"),sQuery(id+"F0.wireOp",EDGE,"E704"),sQuery(id+"F0.wireOp",EDGE,"E705"),sQuery(id+"F0.wireOp",EDGE,"E706"),sQuery(id+"F0.wireOp",EDGE,"E707"),sQuery(id+"F0.wireOp",EDGE,"E708"),sQuery(id+"F0.wireOp",EDGE,"E709"),sQuery(id+"F0.wireOp",EDGE,"E710"),sQuery(id+"F0.wireOp",EDGE,"E711"),sQuery(id+"F0.wireOp",EDGE,"E712"),sQuery(id+"F0.wireOp",EDGE,"E713"),sQuery(id+"F0.wireOp",EDGE,"E714"),sQuery(id+"F0.wireOp",EDGE,"E715"),sQuery(id+"F0.wireOp",EDGE,"E716"),sQuery(id+"F0.wireOp",EDGE,"E717"),sQuery(id+"F0.wireOp",EDGE,"E718"),sQuery(id+"F0.wireOp",EDGE,"E719"),sQuery(id+"F0.wireOp",EDGE,"E720"),sQuery(id+"F0.wireOp",EDGE,"E721"),sQuery(id+"F0.wireOp",EDGE,"E722"),sQuery(id+"F0.wireOp",EDGE,"E723"),sQuery(id+"F0.wireOp",EDGE,"E724"),sQuery(id+"F0.wireOp",EDGE,"E725"),sQuery(id+"F0.wireOp",EDGE,"E726"),sQuery(id+"F0.wireOp",EDGE,"E727"),sQuery(id+"F0.wireOp",EDGE,"E728"),sQuery(id+"F0.wireOp",EDGE,"E729"),sQuery(id+"F0.wireOp",EDGE,"E730"),sQuery(id+"F0.wireOp",EDGE,"E731"),sQuery(id+"F0.wireOp",EDGE,"E732"),sQuery(id+"F0.wireOp",EDGE,"E733"),sQuery(id+"F0.wireOp",EDGE,"E734"),sQuery(id+"F0.wireOp",EDGE,"E735"),sQuery(id+"F0.wireOp",EDGE,"E736"),sQuery(id+"F0.wireOp",EDGE,"E737"),sQuery(id+"F0.wireOp",EDGE,"E738"),sQuery(id+"F0.wireOp",EDGE,"E739"),sQuery(id+"F0.wireOp",EDGE,"E740"),sQuery(id+"F0.wireOp",EDGE,"E741"),sQuery(id+"F0.wireOp",EDGE,"E742"),sQuery(id+"F0.wireOp",EDGE,"E743"),sQuery(id+"F0.wireOp",EDGE,"E744"),sQuery(id+"F0.wireOp",EDGE,"E745"),sQuery(id+"F0.wireOp",EDGE,"E746"),sQuery(id+"F0.wireOp",EDGE,"E747"),sQuery(id+"F0.wireOp",EDGE,"E748"),sQuery(id+"F0.wireOp",EDGE,"E749"),sQuery(id+"F0.wireOp",EDGE,"E750"),sQuery(id+"F0.wireOp",EDGE,"E751"),sQuery(id+"F0.wireOp",EDGE,"E752"),sQuery(id+"F0.wireOp",EDGE,"E753"),sQuery(id+"F0.wireOp",EDGE,"E754"),sQuery(id+"F0.wireOp",EDGE,"E755"),sQuery(id+"F0.wireOp",EDGE,"E756"),sQuery(id+"F0.wireOp",EDGE,"E757"),sQuery(id+"F0.wireOp",EDGE,"E758"),sQuery(id+"F0.wireOp",EDGE,"E759"),sQuery(id+"F0.wireOp",EDGE,"E760"),sQuery(id+"F0.wireOp",EDGE,"E761"),sQuery(id+"F0.wireOp",EDGE,"E762"),sQuery(id+"F0.wireOp",EDGE,"E763"),sQuery(id+"F0.wireOp",EDGE,"E764"),sQuery(id+"F0.wireOp",EDGE,"E765"),sQuery(id+"F0.wireOp",EDGE,"E766"),sQuery(id+"F0.wireOp",EDGE,"E767"),sQuery(id+"F0.wireOp",EDGE,"E768"),sQuery(id+"F0.wireOp",EDGE,"E769"),sQuery(id+"F0.wireOp",EDGE,"E770"),sQuery(id+"F0.wireOp",EDGE,"E771"),sQuery(id+"F0.wireOp",EDGE,"E772"),sQuery(id+"F0.wireOp",EDGE,"E773"),sQuery(id+"F0.wireOp",EDGE,"E774"),sQuery(id+"F0.wireOp",EDGE,"E775"),sQuery(id+"F0.wireOp",EDGE,"E776"),sQuery(id+"F0.wireOp",EDGE,"E777"),sQuery(id+"F0.wireOp",EDGE,"E778"),sQuery(id+"F0.wireOp",EDGE,"E779"),sQuery(id+"F0.wireOp",EDGE,"E780"),sQuery(id+"F0.wireOp",EDGE,"E781"),sQuery(id+"F0.wireOp",EDGE,"E782"),sQuery(id+"F0.wireOp",EDGE,"E783"),sQuery(id+"F0.wireOp",EDGE,"E784"),sQuery(id+"F0.wireOp",EDGE,"E785"),sQuery(id+"F0.wireOp",EDGE,"E786"),sQuery(id+"F0.wireOp",EDGE,"E787"),sQuery(id+"F0.wireOp",EDGE,"E788"),sQuery(id+"F0.wireOp",EDGE,"E789"),sQuery(id+"F0.wireOp",EDGE,"E790"),sQuery(id+"F0.wireOp",EDGE,"E791"),sQuery(id+"F0.wireOp",EDGE,"E792"),sQuery(id+"F0.wireOp",EDGE,"E793"),sQuery(id+"F0.wireOp",EDGE,"E794"),sQuery(id+"F0.wireOp",EDGE,"E795"),sQuery(id+"F0.wireOp",EDGE,"E796"),sQuery(id+"F0.wireOp",EDGE,"E797"),sQuery(id+"F0.wireOp",EDGE,"E798"),sQuery(id+"F0.wireOp",EDGE,"E799"),sQuery(id+"F0.wireOp",EDGE,"E800"),sQuery(id+"F0.wireOp",EDGE,"E801"),sQuery(id+"F0.wireOp",EDGE,"E802"),sQuery(id+"F0.wireOp",EDGE,"E803"),sQuery(id+"F0.wireOp",EDGE,"E804"),sQuery(id+"F0.wireOp",EDGE,"E805"),sQuery(id+"F0.wireOp",EDGE,"E806"),sQuery(id+"F0.wireOp",EDGE,"E807"),sQuery(id+"F0.wireOp",EDGE,"E808"),sQuery(id+"F0.wireOp",EDGE,"E809"),sQuery(id+"F0.wireOp",EDGE,"E810"),sQuery(id+"F0.wireOp",EDGE,"E811"),sQuery(id+"F0.wireOp",EDGE,"E812"),sQuery(id+"F0.wireOp",EDGE,"E813"),sQuery(id+"F0.wireOp",EDGE,"E814"),sQuery(id+"F0.wireOp",EDGE,"E815"),sQuery(id+"F0.wireOp",EDGE,"E816"),sQuery(id+"F0.wireOp",EDGE,"E817"),sQuery(id+"F0.wireOp",EDGE,"E818"),sQuery(id+"F0.wireOp",EDGE,"E819"),sQuery(id+"F0.wireOp",EDGE,"E820"),sQuery(id+"F0.wireOp",EDGE,"E821"),sQuery(id+"F0.wireOp",EDGE,"E822"),sQuery(id+"F0.wireOp",EDGE,"E823"),sQuery(id+"F0.wireOp",EDGE,"E824"),sQuery(id+"F0.wireOp",EDGE,"E825"),sQuery(id+"F0.wireOp",EDGE,"E826"),sQuery(id+"F0.wireOp",EDGE,"E827"),sQuery(id+"F0.wireOp",EDGE,"E828"),sQuery(id+"F0.wireOp",EDGE,"E829"),sQuery(id+"F0.wireOp",EDGE,"E830"),sQuery(id+"F0.wireOp",EDGE,"E831"),sQuery(id+"F0.wireOp",EDGE,"E832"),sQuery(id+"F0.wireOp",EDGE,"E833"),sQuery(id+"F0.wireOp",EDGE,"E834"),sQuery(id+"F0.wireOp",EDGE,"E835"),sQuery(id+"F0.wireOp",EDGE,"E836"),sQuery(id+"F0.wireOp",EDGE,"E837"),sQuery(id+"F0.wireOp",EDGE,"E838"),sQuery(id+"F0.wireOp",EDGE,"E839"),sQuery(id+"F0.wireOp",EDGE,"E840"),sQuery(id+"F0.wireOp",EDGE,"E841"),sQuery(id+"F0.wireOp",EDGE,"E842"),sQuery(id+"F0.wireOp",EDGE,"E843"),sQuery(id+"F0.wireOp",EDGE,"E844"),sQuery(id+"F0.wireOp",EDGE,"E845"),sQuery(id+"F0.wireOp",EDGE,"E846"),sQuery(id+"F0.wireOp",EDGE,"E847"),sQuery(id+"F0.wireOp",EDGE,"E848"),sQuery(id+"F0.wireOp",EDGE,"E849"),sQuery(id+"F0.wireOp",EDGE,"E850"),sQuery(id+"F0.wireOp",EDGE,"E851"),sQuery(id+"F0.wireOp",EDGE,"E852"),sQuery(id+"F0.wireOp",EDGE,"E853"),sQuery(id+"F0.wireOp",EDGE,"E854"),sQuery(id+"F0.wireOp",EDGE,"E855"),sQuery(id+"F0.wireOp",EDGE,"E856"),sQuery(id+"F0.wireOp",EDGE,"E857"),sQuery(id+"F0.wireOp",EDGE,"E858"),sQuery(id+"F0.wireOp",EDGE,"E859"),sQuery(id+"F0.wireOp",EDGE,"E860"),sQuery(id+"F0.wireOp",EDGE,"E861"),sQuery(id+"F0.wireOp",EDGE,"E862"),sQuery(id+"F0.wireOp",EDGE,"E863"),sQuery(id+"F0.wireOp",EDGE,"E864"),sQuery(id+"F0.wireOp",EDGE,"E865"),sQuery(id+"F0.wireOp",EDGE,"E866"),sQuery(id+"F0.wireOp",EDGE,"E867"),sQuery(id+"F0.wireOp",EDGE,"E868"),sQuery(id+"F0.wireOp",EDGE,"E869"),sQuery(id+"F0.wireOp",EDGE,"E870"),sQuery(id+"F0.wireOp",EDGE,"E871"),sQuery(id+"F0.wireOp",EDGE,"E872"),sQuery(id+"F0.wireOp",EDGE,"E873"),sQuery(id+"F0.wireOp",EDGE,"E874"),sQuery(id+"F0.wireOp",EDGE,"E875"),sQuery(id+"F0.wireOp",EDGE,"E876"),sQuery(id+"F0.wireOp",EDGE,"E877"),sQuery(id+"F0.wireOp",EDGE,"E878"),sQuery(id+"F0.wireOp",EDGE,"E879"),sQuery(id+"F0.wireOp",EDGE,"E880"),sQuery(id+"F0.wireOp",EDGE,"E881"),sQuery(id+"F0.wireOp",EDGE,"E882"),sQuery(id+"F0.wireOp",EDGE,"E883"),sQuery(id+"F0.wireOp",EDGE,"E884"),sQuery(id+"F0.wireOp",EDGE,"E885"),sQuery(id+"F0.wireOp",EDGE,"E886"),sQuery(id+"F0.wireOp",EDGE,"E887"),sQuery(id+"F0.wireOp",EDGE,"E888"),sQuery(id+"F0.wireOp",EDGE,"E889"),sQuery(id+"F0.wireOp",EDGE,"E890"),sQuery(id+"F0.wireOp",EDGE,"E891"),sQuery(id+"F0.wireOp",EDGE,"E892"),sQuery(id+"F0.wireOp",EDGE,"E893"),sQuery(id+"F0.wireOp",EDGE,"E894"),sQuery(id+"F0.wireOp",EDGE,"E895"),sQuery(id+"F0.wireOp",EDGE,"E896"),sQuery(id+"F0.wireOp",EDGE,"E897"),sQuery(id+"F0.wireOp",EDGE,"E898"),sQuery(id+"F0.wireOp",EDGE,"E899"),sQuery(id+"F0.wireOp",EDGE,"E900"),sQuery(id+"F0.wireOp",EDGE,"E901"),sQuery(id+"F0.wireOp",EDGE,"E902"),sQuery(id+"F0.wireOp",EDGE,"E903"),sQuery(id+"F0.wireOp",EDGE,"E904"),sQuery(id+"F0.wireOp",EDGE,"E905"),sQuery(id+"F0.wireOp",EDGE,"E906"),sQuery(id+"F0.wireOp",EDGE,"E907"),sQuery(id+"F0.wireOp",EDGE,"E908"),sQuery(id+"F0.wireOp",EDGE,"E909"),sQuery(id+"F0.wireOp",EDGE,"E910"),sQuery(id+"F0.wireOp",EDGE,"E911"),sQuery(id+"F0.wireOp",EDGE,"E912"),sQuery(id+"F0.wireOp",EDGE,"E913"),sQuery(id+"F0.wireOp",EDGE,"E914"),sQuery(id+"F0.wireOp",EDGE,"E915"),sQuery(id+"F0.wireOp",EDGE,"E916"),sQuery(id+"F0.wireOp",EDGE,"E917"),sQuery(id+"F0.wireOp",EDGE,"E918"),sQuery(id+"F0.wireOp",EDGE,"E919"),sQuery(id+"F0.wireOp",EDGE,"E920"),sQuery(id+"F0.wireOp",EDGE,"E921"),sQuery(id+"F0.wireOp",EDGE,"E922"),sQuery(id+"F0.wireOp",EDGE,"E923"),sQuery(id+"F0.wireOp",EDGE,"E924"),sQuery(id+"F0.wireOp",EDGE,"E925"),sQuery(id+"F0.wireOp",EDGE,"E926"),sQuery(id+"F0.wireOp",EDGE,"E927"),sQuery(id+"F0.wireOp",EDGE,"E928"),sQuery(id+"F0.wireOp",EDGE,"E929"),sQuery(id+"F0.wireOp",EDGE,"E930"),sQuery(id+"F0.wireOp",EDGE,"E931"),sQuery(id+"F0.wireOp",EDGE,"E932"),sQuery(id+"F0.wireOp",EDGE,"E933"),sQuery(id+"F0.wireOp",EDGE,"E934"),sQuery(id+"F0.wireOp",EDGE,"E935"),sQuery(id+"F0.wireOp",EDGE,"E936"),sQuery(id+"F0.wireOp",EDGE,"E937"),sQuery(id+"F0.wireOp",EDGE,"E938"),sQuery(id+"F0.wireOp",EDGE,"E939"),sQuery(id+"F0.wireOp",EDGE,"E940"),sQuery(id+"F0.wireOp",EDGE,"E941"),sQuery(id+"F0.wireOp",EDGE,"E942"),sQuery(id+"F0.wireOp",EDGE,"E943"),sQuery(id+"F0.wireOp",EDGE,"E944"),sQuery(id+"F0.wireOp",EDGE,"E945"),sQuery(id+"F0.wireOp",EDGE,"E946"),sQuery(id+"F0.wireOp",EDGE,"E947"),sQuery(id+"F0.wireOp",EDGE,"E948"),sQuery(id+"F0.wireOp",EDGE,"E949"),sQuery(id+"F0.wireOp",EDGE,"E950"),sQuery(id+"F0.wireOp",EDGE,"E951"),sQuery(id+"F0.wireOp",EDGE,"E952"),sQuery(id+"F0.wireOp",EDGE,"E953"),sQuery(id+"F0.wireOp",EDGE,"E954"),sQuery(id+"F0.wireOp",EDGE,"E955"),sQuery(id+"F0.wireOp",EDGE,"E956"),sQuery(id+"F0.wireOp",EDGE,"E957"),sQuery(id+"F0.wireOp",EDGE,"E958"),sQuery(id+"F0.wireOp",EDGE,"E959"),sQuery(id+"F0.wireOp",EDGE,"E960"),sQuery(id+"F0.wireOp",EDGE,"E961"),sQuery(id+"F0.wireOp",EDGE,"E962"),sQuery(id+"F0.wireOp",EDGE,"E963"),sQuery(id+"F0.wireOp",EDGE,"E964"),sQuery(id+"F0.wireOp",EDGE,"E965"),sQuery(id+"F0.wireOp",EDGE,"E966"),sQuery(id+"F0.wireOp",EDGE,"E967"),sQuery(id+"F0.wireOp",EDGE,"E968"),sQuery(id+"F0.wireOp",EDGE,"E969"),sQuery(id+"F0.wireOp",EDGE,"E970"),sQuery(id+"F0.wireOp",EDGE,"E971"),sQuery(id+"F0.wireOp",EDGE,"E972"),sQuery(id+"F0.wireOp",EDGE,"E973"),sQuery(id+"F0.wireOp",EDGE,"E974"),sQuery(id+"F0.wireOp",EDGE,"E975"),sQuery(id+"F0.wireOp",EDGE,"E976"),sQuery(id+"F0.wireOp",EDGE,"E977"),sQuery(id+"F0.wireOp",EDGE,"E978"),sQuery(id+"F0.wireOp",EDGE,"E979"),sQuery(id+"F0.wireOp",EDGE,"E980"),sQuery(id+"F0.wireOp",EDGE,"E981"),sQuery(id+"F0.wireOp",EDGE,"E982"),sQuery(id+"F0.wireOp",EDGE,"E983"),sQuery(id+"F0.wireOp",EDGE,"E984"),sQuery(id+"F0.wireOp",EDGE,"E985"),sQuery(id+"F0.wireOp",EDGE,"E986"),sQuery(id+"F0.wireOp",EDGE,"E987"),sQuery(id+"F0.wireOp",EDGE,"E988"),sQuery(id+"F0.wireOp",EDGE,"E989"),sQuery(id+"F0.wireOp",EDGE,"E990"),sQuery(id+"F0.wireOp",EDGE,"E991"),sQuery(id+"F0.wireOp",EDGE,"E992"),sQuery(id+"F0.wireOp",EDGE,"E993"),sQuery(id+"F0.wireOp",EDGE,"E994"),sQuery(id+"F0.wireOp",EDGE,"E995"),sQuery(id+"F0.wireOp",EDGE,"E996"),sQuery(id+"F0.wireOp",EDGE,"E997"),sQuery(id+"F0.wireOp",EDGE,"E998"),sQuery(id+"F0.wireOp",EDGE,"E999"),sQuery(id+"F0.wireOp",EDGE,"E1000"),sQuery(id+"F0.wireOp",EDGE,"E1001"),sQuery(id+"F0.wireOp",EDGE,"E1002"),sQuery(id+"F0.wireOp",EDGE,"E1003"),sQuery(id+"F0.wireOp",EDGE,"E1004"),sQuery(id+"F0.wireOp",EDGE,"E1005"),sQuery(id+"F0.wireOp",EDGE,"E1006"),sQuery(id+"F0.wireOp",EDGE,"E1007"),sQuery(id+"F0.wireOp",EDGE,"E1008"),sQuery(id+"F0.wireOp",EDGE,"E1009"),sQuery(id+"F0.wireOp",EDGE,"E1010"),sQuery(id+"F0.wireOp",EDGE,"E1011"),sQuery(id+"F0.wireOp",EDGE,"E1012"),sQuery(id+"F0.wireOp",EDGE,"E1013"),sQuery(id+"F0.wireOp",EDGE,"E1014"),sQuery(id+"F0.wireOp",EDGE,"E1015"),sQuery(id+"F0.wireOp",EDGE,"E1016"),sQuery(id+"F0.wireOp",EDGE,"E1017"),sQuery(id+"F0.wireOp",EDGE,"E1018"),sQuery(id+"F0.wireOp",EDGE,"E1019"),sQuery(id+"F0.wireOp",EDGE,"E1020"),sQuery(id+"F0.wireOp",EDGE,"E1021"),sQuery(id+"F0.wireOp",EDGE,"E1022"),sQuery(id+"F0.wireOp",EDGE,"E1023"),sQuery(id+"F0.wireOp",EDGE,"E1024"),sQuery(id+"F0.wireOp",EDGE,"E1025"),sQuery(id+"F0.wireOp",EDGE,"E1026"),sQuery(id+"F0.wireOp",EDGE,"E1027"),sQuery(id+"F0.wireOp",EDGE,"E1028"),sQuery(id+"F0.wireOp",EDGE,"E1029"),sQuery(id+"F0.wireOp",EDGE,"E1030"),sQuery(id+"F0.wireOp",EDGE,"E1031"),sQuery(id+"F0.wireOp",EDGE,"E1032"),sQuery(id+"F0.wireOp",EDGE,"E1033"),sQuery(id+"F0.wireOp",EDGE,"E1034"),sQuery(id+"F0.wireOp",EDGE,"E1035"),sQuery(id+"F0.wireOp",EDGE,"E1036"),sQuery(id+"F0.wireOp",EDGE,"E1037"),sQuery(id+"F0.wireOp",EDGE,"E1038"),sQuery(id+"F0.wireOp",EDGE,"E1039"),sQuery(id+"F0.wireOp",EDGE,"E1040"),sQuery(id+"F0.wireOp",EDGE,"E1041"),sQuery(id+"F0.wireOp",EDGE,"E1042"),sQuery(id+"F0.wireOp",EDGE,"E1043"),sQuery(id+"F0.wireOp",EDGE,"E1044"),sQuery(id+"F0.wireOp",EDGE,"E1045"),sQuery(id+"F0.wireOp",EDGE,"E1046"),sQuery(id+"F0.wireOp",EDGE,"E1047"),sQuery(id+"F0.wireOp",EDGE,"E1048"),sQuery(id+"F0.wireOp",EDGE,"E1049"),sQuery(id+"F0.wireOp",EDGE,"E1050"),sQuery(id+"F0.wireOp",EDGE,"E1051"),sQuery(id+"F0.wireOp",EDGE,"E1052"),sQuery(id+"F0.wireOp",EDGE,"E1053"),sQuery(id+"F0.wireOp",EDGE,"E1054"),sQuery(id+"F0.wireOp",EDGE,"E1055"),sQuery(id+"F0.wireOp",EDGE,"E1056"),sQuery(id+"F0.wireOp",EDGE,"E1057"),sQuery(id+"F0.wireOp",EDGE,"E1058"),sQuery(id+"F0.wireOp",EDGE,"E1059"),sQuery(id+"F0.wireOp",EDGE,"E1060"),sQuery(id+"F0.wireOp",EDGE,"E1061"),sQuery(id+"F0.wireOp",EDGE,"E1062"),sQuery(id+"F0.wireOp",EDGE,"E1063"),sQuery(id+"F0.wireOp",EDGE,"E1064"),sQuery(id+"F0.wireOp",EDGE,"E1065"),sQuery(id+"F0.wireOp",EDGE,"E1066"),sQuery(id+"F0.wireOp",EDGE,"E1067"),sQuery(id+"F0.wireOp",EDGE,"E1068"),sQuery(id+"F0.wireOp",EDGE,"E1069"),sQuery(id+"F0.wireOp",EDGE,"E1070"),sQuery(id+"F0.wireOp",EDGE,"E1071"),sQuery(id+"F0.wireOp",EDGE,"E1072"),sQuery(id+"F0.wireOp",EDGE,"E1073"),sQuery(id+"F0.wireOp",EDGE,"E1074"),sQuery(id+"F0.wireOp",EDGE,"E1075"),sQuery(id+"F0.wireOp",EDGE,"E1076"),sQuery(id+"F0.wireOp",EDGE,"E1077"),sQuery(id+"F0.wireOp",EDGE,"E1078"),sQuery(id+"F0.wireOp",EDGE,"E1079"),sQuery(id+"F0.wireOp",EDGE,"E1080"),sQuery(id+"F0.wireOp",EDGE,"E1081"),sQuery(id+"F0.wireOp",EDGE,"E1082"),sQuery(id+"F0.wireOp",EDGE,"E1083"),sQuery(id+"F0.wireOp",EDGE,"E1084"),sQuery(id+"F0.wireOp",EDGE,"E1085"),sQuery(id+"F0.wireOp",EDGE,"E1086"),sQuery(id+"F0.wireOp",EDGE,"E1087"),sQuery(id+"F0.wireOp",EDGE,"E1088"),sQuery(id+"F0.wireOp",EDGE,"E1089"),sQuery(id+"F0.wireOp",EDGE,"E1090"),sQuery(id+"F0.wireOp",EDGE,"E1091"),sQuery(id+"F0.wireOp",EDGE,"E1092"),sQuery(id+"F0.wireOp",EDGE,"E1093"),sQuery(id+"F0.wireOp",EDGE,"E1094"),sQuery(id+"F0.wireOp",EDGE,"E1095"),sQuery(id+"F0.wireOp",EDGE,"E1096"),sQuery(id+"F0.wireOp",EDGE,"E1097"),sQuery(id+"F0.wireOp",EDGE,"E1098"),sQuery(id+"F0.wireOp",EDGE,"E1099"),sQuery(id+"F0.wireOp",EDGE,"E1100"),sQuery(id+"F0.wireOp",EDGE,"E1101"),sQuery(id+"F0.wireOp",EDGE,"E1102"),sQuery(id+"F0.wireOp",EDGE,"E1103"),sQuery(id+"F0.wireOp",EDGE,"E1104"),sQuery(id+"F0.wireOp",EDGE,"E1105"),sQuery(id+"F0.wireOp",EDGE,"E1106"),sQuery(id+"F0.wireOp",EDGE,"E1107"),sQuery(id+"F0.wireOp",EDGE,"E1108"),sQuery(id+"F0.wireOp",EDGE,"E1109"),sQuery(id+"F0.wireOp",EDGE,"E1110"),sQuery(id+"F0.wireOp",EDGE,"E1111"),sQuery(id+"F0.wireOp",EDGE,"E1112"),sQuery(id+"F0.wireOp",EDGE,"E1113"),sQuery(id+"F0.wireOp",EDGE,"E1114"),sQuery(id+"F0.wireOp",EDGE,"E1115"),sQuery(id+"F0.wireOp",EDGE,"E1116"),sQuery(id+"F0.wireOp",EDGE,"E1117"),sQuery(id+"F0.wireOp",EDGE,"E1118"),sQuery(id+"F0.wireOp",EDGE,"E1119"),sQuery(id+"F0.wireOp",EDGE,"E1120"),sQuery(id+"F0.wireOp",EDGE,"E1121"),sQuery(id+"F0.wireOp",EDGE,"E1122"),sQuery(id+"F0.wireOp",EDGE,"E1123"),sQuery(id+"F0.wireOp",EDGE,"E1124"),sQuery(id+"F0.wireOp",EDGE,"E1125"),sQuery(id+"F0.wireOp",EDGE,"E1126"),sQuery(id+"F0.wireOp",EDGE,"E1127"),sQuery(id+"F0.wireOp",EDGE,"E1128"),sQuery(id+"F0.wireOp",EDGE,"E1129"),sQuery(id+"F0.wireOp",EDGE,"E1130"),sQuery(id+"F0.wireOp",EDGE,"E1131"),sQuery(id+"F0.wireOp",EDGE,"E1132"),sQuery(id+"F0.wireOp",EDGE,"E1133"),sQuery(id+"F0.wireOp",EDGE,"E1134"),sQuery(id+"F0.wireOp",EDGE,"E1135"),sQuery(id+"F0.wireOp",EDGE,"E1136"),sQuery(id+"F0.wireOp",EDGE,"E1137"),sQuery(id+"F0.wireOp",EDGE,"E1138"),sQuery(id+"F0.wireOp",EDGE,"E1139"),sQuery(id+"F0.wireOp",EDGE,"E1140"),sQuery(id+"F0.wireOp",EDGE,"E1141"),sQuery(id+"F0.wireOp",EDGE,"E1142"),sQuery(id+"F0.wireOp",EDGE,"E1143"),sQuery(id+"F0.wireOp",EDGE,"E1144"),sQuery(id+"F0.wireOp",EDGE,"E1145"),sQuery(id+"F0.wireOp",EDGE,"E1146"),sQuery(id+"F0.wireOp",EDGE,"E1147"),sQuery(id+"F0.wireOp",EDGE,"E1148"),sQuery(id+"F0.wireOp",EDGE,"E1149"),sQuery(id+"F0.wireOp",EDGE,"E1150"),sQuery(id+"F0.wireOp",EDGE,"E1151"),sQuery(id+"F0.wireOp",EDGE,"E1152"),sQuery(id+"F0.wireOp",EDGE,"E1153"),sQuery(id+"F0.wireOp",EDGE,"E1154"),sQuery(id+"F0.wireOp",EDGE,"E1155"),sQuery(id+"F0.wireOp",EDGE,"E1156"),sQuery(id+"F0.wireOp",EDGE,"E1157"),sQuery(id+"F0.wireOp",EDGE,"E1158"),sQuery(id+"F0.wireOp",EDGE,"E1159"),sQuery(id+"F0.wireOp",EDGE,"E1160"),sQuery(id+"F0.wireOp",EDGE,"E1161"),sQuery(id+"F0.wireOp",EDGE,"E1162"),sQuery(id+"F0.wireOp",EDGE,"E1163"),sQuery(id+"F0.wireOp",EDGE,"E1164"),sQuery(id+"F0.wireOp",EDGE,"E1165"),sQuery(id+"F0.wireOp",EDGE,"E1166"),sQuery(id+"F0.wireOp",EDGE,"E1167"),sQuery(id+"F0.wireOp",EDGE,"E1168"),sQuery(id+"F0.wireOp",EDGE,"E1169"),sQuery(id+"F0.wireOp",EDGE,"E1170"),sQuery(id+"F0.wireOp",EDGE,"E1171"),sQuery(id+"F0.wireOp",EDGE,"E1172"),sQuery(id+"F0.wireOp",EDGE,"E1173"),sQuery(id+"F0.wireOp",EDGE,"E1174"),sQuery(id+"F0.wireOp",EDGE,"E1175"),sQuery(id+"F0.wireOp",EDGE,"E1176"),sQuery(id+"F0.wireOp",EDGE,"E1177"),sQuery(id+"F0.wireOp",EDGE,"E1178"),sQuery(id+"F0.wireOp",EDGE,"E1179"),sQuery(id+"F0.wireOp",EDGE,"E1180"),sQuery(id+"F0.wireOp",EDGE,"E1181"),sQuery(id+"F0.wireOp",EDGE,"E1182"),sQuery(id+"F0.wireOp",EDGE,"E1183"),sQuery(id+"F0.wireOp",EDGE,"E1184"),sQuery(id+"F0.wireOp",EDGE,"E1185"),sQuery(id+"F0.wireOp",EDGE,"E1186"),sQuery(id+"F0.wireOp",EDGE,"E1187"),sQuery(id+"F0.wireOp",EDGE,"E1188"),sQuery(id+"F0.wireOp",EDGE,"E1189"),sQuery(id+"F0.wireOp",EDGE,"E1190"),sQuery(id+"F0.wireOp",EDGE,"E1191"),sQuery(id+"F0.wireOp",EDGE,"E1192"),sQuery(id+"F0.wireOp",EDGE,"E1193"),sQuery(id+"F0.wireOp",EDGE,"E1194"),sQuery(id+"F0.wireOp",EDGE,"E1195"),sQuery(id+"F0.wireOp",EDGE,"E1196"),sQuery(id+"F0.wireOp",EDGE,"E1197"),sQuery(id+"F0.wireOp",EDGE,"E1198"),sQuery(id+"F0.wireOp",EDGE,"E1199"),sQuery(id+"F0.wireOp",EDGE,"E1200"),sQuery(id+"F0.wireOp",EDGE,"E1201"),sQuery(id+"F0.wireOp",EDGE,"E1202"),sQuery(id+"F0.wireOp",EDGE,"E1203"),sQuery(id+"F0.wireOp",EDGE,"E1204"),sQuery(id+"F0.wireOp",EDGE,"E1205"),sQuery(id+"F0.wireOp",EDGE,"E1206"),sQuery(id+"F0.wireOp",EDGE,"E1207"),sQuery(id+"F0.wireOp",EDGE,"E1208"),sQuery(id+"F0.wireOp",EDGE,"E1209"),sQuery(id+"F0.wireOp",EDGE,"E1210"),sQuery(id+"F0.wireOp",EDGE,"E1211"),sQuery(id+"F0.wireOp",EDGE,"E1212"),sQuery(id+"F0.wireOp",EDGE,"E1213"),sQuery(id+"F0.wireOp",EDGE,"E1214"),sQuery(id+"F0.wireOp",EDGE,"E1215"),sQuery(id+"F0.wireOp",EDGE,"E1216"),sQuery(id+"F0.wireOp",EDGE,"E1217"),sQuery(id+"F0.wireOp",EDGE,"E1218"),sQuery(id+"F0.wireOp",EDGE,"E1219"),sQuery(id+"F0.wireOp",EDGE,"E1220"),sQuery(id+"F0.wireOp",EDGE,"E1221"),sQuery(id+"F0.wireOp",EDGE,"E1222"),sQuery(id+"F0.wireOp",EDGE,"E1223"),sQuery(id+"F0.wireOp",EDGE,"E1224"),sQuery(id+"F0.wireOp",EDGE,"E1225"),sQuery(id+"F0.wireOp",EDGE,"E1226"),sQuery(id+"F0.wireOp",EDGE,"E1227"),sQuery(id+"F0.wireOp",EDGE,"E1228"),sQuery(id+"F0.wireOp",EDGE,"E1229"),sQuery(id+"F0.wireOp",EDGE,"E1230"),sQuery(id+"F0.wireOp",EDGE,"E1231"),sQuery(id+"F0.wireOp",EDGE,"E1232"),sQuery(id+"F0.wireOp",EDGE,"E1233"),sQuery(id+"F0.wireOp",EDGE,"E1234"),sQuery(id+"F0.wireOp",EDGE,"E1235"),sQuery(id+"F0.wireOp",EDGE,"E1236"),sQuery(id+"F0.wireOp",EDGE,"E1237"),sQuery(id+"F0.wireOp",EDGE,"E1238"),sQuery(id+"F0.wireOp",EDGE,"E1239"),sQuery(id+"F0.wireOp",EDGE,"E1240"),sQuery(id+"F0.wireOp",EDGE,"E1241"),sQuery(id+"F0.wireOp",EDGE,"E1242"),sQuery(id+"F0.wireOp",EDGE,"E1243"),sQuery(id+"F0.wireOp",EDGE,"E1244"),sQuery(id+"F0.wireOp",EDGE,"E1245"),sQuery(id+"F0.wireOp",EDGE,"E1246"),sQuery(id+"F0.wireOp",EDGE,"E1247"),sQuery(id+"F0.wireOp",EDGE,"E1248"),sQuery(id+"F0.wireOp",EDGE,"E1249"),sQuery(id+"F0.wireOp",EDGE,"E1250"),sQuery(id+"F0.wireOp",EDGE,"E1251"),sQuery(id+"F0.wireOp",EDGE,"E1252"),sQuery(id+"F0.wireOp",EDGE,"E1253"),sQuery(id+"F0.wireOp",EDGE,"E1254"),sQuery(id+"F0.wireOp",EDGE,"E1255"),sQuery(id+"F0.wireOp",EDGE,"E1256"),sQuery(id+"F0.wireOp",EDGE,"E1257"),sQuery(id+"F0.wireOp",EDGE,"E1258"),sQuery(id+"F0.wireOp",EDGE,"E1259"),sQuery(id+"F0.wireOp",EDGE,"E1260"),sQuery(id+"F0.wireOp",EDGE,"E1261"),sQuery(id+"F0.wireOp",EDGE,"E1262"),sQuery(id+"F0.wireOp",EDGE,"E1263"),sQuery(id+"F0.wireOp",EDGE,"E1264"),sQuery(id+"F0.wireOp",EDGE,"E1265"),sQuery(id+"F0.wireOp",EDGE,"E1266"),sQuery(id+"F0.wireOp",EDGE,"E1267"),sQuery(id+"F0.wireOp",EDGE,"E1268"),sQuery(id+"F0.wireOp",EDGE,"E1269"),sQuery(id+"F0.wireOp",EDGE,"E1270"),sQuery(id+"F0.wireOp",EDGE,"E1271"),sQuery(id+"F0.wireOp",EDGE,"E1272"),sQuery(id+"F0.wireOp",EDGE,"E1273"),sQuery(id+"F0.wireOp",EDGE,"E1274"),sQuery(id+"F0.wireOp",EDGE,"E1275"),sQuery(id+"F0.wireOp",EDGE,"E1276"),sQuery(id+"F0.wireOp",EDGE,"E1277"),sQuery(id+"F0.wireOp",EDGE,"E1278"),sQuery(id+"F0.wireOp",EDGE,"E1279"),sQuery(id+"F0.wireOp",EDGE,"E1280"),sQuery(id+"F0.wireOp",EDGE,"E1281"),sQuery(id+"F0.wireOp",EDGE,"E1282"),sQuery(id+"F0.wireOp",EDGE,"E1283"),sQuery(id+"F0.wireOp",EDGE,"E1284"),sQuery(id+"F0.wireOp",EDGE,"E1285"),sQuery(id+"F0.wireOp",EDGE,"E1286"),sQuery(id+"F0.wireOp",EDGE,"E1287"),sQuery(id+"F0.wireOp",EDGE,"E1288"),sQuery(id+"F0.wireOp",EDGE,"E1289"),sQuery(id+"F0.wireOp",EDGE,"E1290"),sQuery(id+"F0.wireOp",EDGE,"E1291"),sQuery(id+"F0.wireOp",EDGE,"E1292"),sQuery(id+"F0.wireOp",EDGE,"E1293"),sQuery(id+"F0.wireOp",EDGE,"E1294"),sQuery(id+"F0.wireOp",EDGE,"E1295"),sQuery(id+"F0.wireOp",EDGE,"E1296"),sQuery(id+"F0.wireOp",EDGE,"E1297"),sQuery(id+"F0.wireOp",EDGE,"E1298"),sQuery(id+"F0.wireOp",EDGE,"E1299"),sQuery(id+"F0.wireOp",EDGE,"E1300"),sQuery(id+"F0.wireOp",EDGE,"E1301"),sQuery(id+"F0.wireOp",EDGE,"E1302"),sQuery(id+"F0.wireOp",EDGE,"E1303"),sQuery(id+"F0.wireOp",EDGE,"E1304"),sQuery(id+"F0.wireOp",EDGE,"E1305"),sQuery(id+"F0.wireOp",EDGE,"E1306"),sQuery(id+"F0.wireOp",EDGE,"E1307"),sQuery(id+"F0.wireOp",EDGE,"E1308"),sQuery(id+"F0.wireOp",EDGE,"E1309"),sQuery(id+"F0.wireOp",EDGE,"E1310"),sQuery(id+"F0.wireOp",EDGE,"E1311"),sQuery(id+"F0.wireOp",EDGE,"E1312"),sQuery(id+"F0.wireOp",EDGE,"E1313"),sQuery(id+"F0.wireOp",EDGE,"E1314"),sQuery(id+"F0.wireOp",EDGE,"E1315"),sQuery(id+"F0.wireOp",EDGE,"E1316"),sQuery(id+"F0.wireOp",EDGE,"E1317"),sQuery(id+"F0.wireOp",EDGE,"E1318"),sQuery(id+"F0.wireOp",EDGE,"E1319"),sQuery(id+"F0.wireOp",EDGE,"E1320"),sQuery(id+"F0.wireOp",EDGE,"E1321"),sQuery(id+"F0.wireOp",EDGE,"E1322"),sQuery(id+"F0.wireOp",EDGE,"E1323"),sQuery(id+"F0.wireOp",EDGE,"E1324"),sQuery(id+"F0.wireOp",EDGE,"E1325"),sQuery(id+"F0.wireOp",EDGE,"E1326"),sQuery(id+"F0.wireOp",EDGE,"E1327"),sQuery(id+"F0.wireOp",EDGE,"E1328"),sQuery(id+"F0.wireOp",EDGE,"E1329"),sQuery(id+"F0.wireOp",EDGE,"E1330"),sQuery(id+"F0.wireOp",EDGE,"E1331"),sQuery(id+"F0.wireOp",EDGE,"E1332"),sQuery(id+"F0.wireOp",EDGE,"E1333"),sQuery(id+"F0.wireOp",EDGE,"E1334"),sQuery(id+"F0.wireOp",EDGE,"E1335"),sQuery(id+"F0.wireOp",EDGE,"E1336"),sQuery(id+"F0.wireOp",EDGE,"E1337"),sQuery(id+"F0.wireOp",EDGE,"E1338"),sQuery(id+"F0.wireOp",EDGE,"E1339"),sQuery(id+"F0.wireOp",EDGE,"E1340"),sQuery(id+"F0.wireOp",EDGE,"E1341"),sQuery(id+"F0.wireOp",EDGE,"E1342"),sQuery(id+"F0.wireOp",EDGE,"E1343"),sQuery(id+"F0.wireOp",EDGE,"E1344"),sQuery(id+"F0.wireOp",EDGE,"E1345"),sQuery(id+"F0.wireOp",EDGE,"E1346"),sQuery(id+"F0.wireOp",EDGE,"E1347"),sQuery(id+"F0.wireOp",EDGE,"E1348"),sQuery(id+"F0.wireOp",EDGE,"E1349"),sQuery(id+"F0.wireOp",EDGE,"E1350"),sQuery(id+"F0.wireOp",EDGE,"E1351"),sQuery(id+"F0.wireOp",EDGE,"E1352"),sQuery(id+"F0.wireOp",EDGE,"E1353"),sQuery(id+"F0.wireOp",EDGE,"E1354"),sQuery(id+"F0.wireOp",EDGE,"E1355"),sQuery(id+"F0.wireOp",EDGE,"E1356"),sQuery(id+"F0.wireOp",EDGE,"E1357"),sQuery(id+"F0.wireOp",EDGE,"E1358"),sQuery(id+"F0.wireOp",EDGE,"E1359"),sQuery(id+"F0.wireOp",EDGE,"E1360"),sQuery(id+"F0.wireOp",EDGE,"E1361"),sQuery(id+"F0.wireOp",EDGE,"E1362"),sQuery(id+"F0.wireOp",EDGE,"E1363"),sQuery(id+"F0.wireOp",EDGE,"E1364"),sQuery(id+"F0.wireOp",EDGE,"E1365"),sQuery(id+"F0.wireOp",EDGE,"E1366"),sQuery(id+"F0.wireOp",EDGE,"E1367"),sQuery(id+"F0.wireOp",EDGE,"E1368"),sQuery(id+"F0.wireOp",EDGE,"E1369"),sQuery(id+"F0.wireOp",EDGE,"E1370"),sQuery(id+"F0.wireOp",EDGE,"E1371"),sQuery(id+"F0.wireOp",EDGE,"E1372"),sQuery(id+"F0.wireOp",EDGE,"E1373"),sQuery(id+"F0.wireOp",EDGE,"E1374"),sQuery(id+"F0.wireOp",EDGE,"E1375"),sQuery(id+"F0.wireOp",EDGE,"E1376"),sQuery(id+"F0.wireOp",EDGE,"E1377"),sQuery(id+"F0.wireOp",EDGE,"E1378"),sQuery(id+"F0.wireOp",EDGE,"E1379"),sQuery(id+"F0.wireOp",EDGE,"E1380"),sQuery(id+"F0.wireOp",EDGE,"E1381"),sQuery(id+"F0.wireOp",EDGE,"E1382"),sQuery(id+"F0.wireOp",EDGE,"E1383"),sQuery(id+"F0.wireOp",EDGE,"E1384"),sQuery(id+"F0.wireOp",EDGE,"E1385"),sQuery(id+"F0.wireOp",EDGE,"E1386"),sQuery(id+"F0.wireOp",EDGE,"E1387"),sQuery(id+"F0.wireOp",EDGE,"E1388"),sQuery(id+"F0.wireOp",EDGE,"E1389"),sQuery(id+"F0.wireOp",EDGE,"E1390"),sQuery(id+"F0.wireOp",EDGE,"E1391"),sQuery(id+"F0.wireOp",EDGE,"E1392"),sQuery(id+"F0.wireOp",EDGE,"E1393"),sQuery(id+"F0.wireOp",EDGE,"E1394"),sQuery(id+"F0.wireOp",EDGE,"E1395"),sQuery(id+"F0.wireOp",EDGE,"E1396"),sQuery(id+"F0.wireOp",EDGE,"E1397"),sQuery(id+"F0.wireOp",EDGE,"E1398"),sQuery(id+"F0.wireOp",EDGE,"E1399"),sQuery(id+"F0.wireOp",EDGE,"E1400"),sQuery(id+"F0.wireOp",EDGE,"E1401"),sQuery(id+"F0.wireOp",EDGE,"E1402"),sQuery(id+"F0.wireOp",EDGE,"E1403"),sQuery(id+"F0.wireOp",EDGE,"E1404"),sQuery(id+"F0.wireOp",EDGE,"E1405"),sQuery(id+"F0.wireOp",EDGE,"E1406"),sQuery(id+"F0.wireOp",EDGE,"E1407"),sQuery(id+"F0.wireOp",EDGE,"E1408"),sQuery(id+"F0.wireOp",EDGE,"E1409"),sQuery(id+"F0.wireOp",EDGE,"E1410"),sQuery(id+"F0.wireOp",EDGE,"E1411"),sQuery(id+"F0.wireOp",EDGE,"E1412"),sQuery(id+"F0.wireOp",EDGE,"E1413"),sQuery(id+"F0.wireOp",EDGE,"E1414"),sQuery(id+"F0.wireOp",EDGE,"E1415"),sQuery(id+"F0.wireOp",EDGE,"E1416"),sQuery(id+"F0.wireOp",EDGE,"E1417"),sQuery(id+"F0.wireOp",EDGE,"E1418"),sQuery(id+"F0.wireOp",EDGE,"E1419"),sQuery(id+"F0.wireOp",EDGE,"E1420"),sQuery(id+"F0.wireOp",EDGE,"E1421"),sQuery(id+"F0.wireOp",EDGE,"E1422"),sQuery(id+"F0.wireOp",EDGE,"E1423"),sQuery(id+"F0.wireOp",EDGE,"E1424"),sQuery(id+"F0.wireOp",EDGE,"E1425"),sQuery(id+"F0.wireOp",EDGE,"E1426"),sQuery(id+"F0.wireOp",EDGE,"E1427"),sQuery(id+"F0.wireOp",EDGE,"E1428"),sQuery(id+"F0.wireOp",EDGE,"E1429"),sQuery(id+"F0.wireOp",EDGE,"E1430"),sQuery(id+"F0.wireOp",EDGE,"E1431"),sQuery(id+"F0.wireOp",EDGE,"E1432"),sQuery(id+"F0.wireOp",EDGE,"E1433"),sQuery(id+"F0.wireOp",EDGE,"E1434"),sQuery(id+"F0.wireOp",EDGE,"E1435"),sQuery(id+"F0.wireOp",EDGE,"E1436"),sQuery(id+"F0.wireOp",EDGE,"E1437"),sQuery(id+"F0.wireOp",EDGE,"E1438"),sQuery(id+"F0.wireOp",EDGE,"E1439"),sQuery(id+"F0.wireOp",EDGE,"E1440"),sQuery(id+"F0.wireOp",EDGE,"E1441"),sQuery(id+"F0.wireOp",EDGE,"E1442"),sQuery(id+"F0.wireOp",EDGE,"E1443"),sQuery(id+"F0.wireOp",EDGE,"E1444"),sQuery(id+"F0.wireOp",EDGE,"E1445"),sQuery(id+"F0.wireOp",EDGE,"E1446"),sQuery(id+"F0.wireOp",EDGE,"E1447"),sQuery(id+"F0.wireOp",EDGE,"E1448"),sQuery(id+"F0.wireOp",EDGE,"E1449"),sQuery(id+"F0.wireOp",EDGE,"E1450"),sQuery(id+"F0.wireOp",EDGE,"E1451"),sQuery(id+"F0.wireOp",EDGE,"E1452"),sQuery(id+"F0.wireOp",EDGE,"E1453"),sQuery(id+"F0.wireOp",EDGE,"E1454"),sQuery(id+"F0.wireOp",EDGE,"E1455"),sQuery(id+"F0.wireOp",EDGE,"E1456"),sQuery(id+"F0.wireOp",EDGE,"E1457"),sQuery(id+"F0.wireOp",EDGE,"E1458"),sQuery(id+"F0.wireOp",EDGE,"E1459"),sQuery(id+"F0.wireOp",EDGE,"E1460"),sQuery(id+"F0.wireOp",EDGE,"E1461"),sQuery(id+"F0.wireOp",EDGE,"E1462"),sQuery(id+"F0.wireOp",EDGE,"E1463"),sQuery(id+"F0.wireOp",EDGE,"E1464"),sQuery(id+"F0.wireOp",EDGE,"E1465"),sQuery(id+"F0.wireOp",EDGE,"E1466"),sQuery(id+"F0.wireOp",EDGE,"E1467"),sQuery(id+"F0.wireOp",EDGE,"E1468"),sQuery(id+"F0.wireOp",EDGE,"E1469"),sQuery(id+"F0.wireOp",EDGE,"E1470"),sQuery(id+"F0.wireOp",EDGE,"E1471"),sQuery(id+"F0.wireOp",EDGE,"E1472"),sQuery(id+"F0.wireOp",EDGE,"E1473"),sQuery(id+"F0.wireOp",EDGE,"E1474"),sQuery(id+"F0.wireOp",EDGE,"E1475"),sQuery(id+"F0.wireOp",EDGE,"E1476"),sQuery(id+"F0.wireOp",EDGE,"E1477"),sQuery(id+"F0.wireOp",EDGE,"E1478"),sQuery(id+"F0.wireOp",EDGE,"E1479"),sQuery(id+"F0.wireOp",EDGE,"E1480"),sQuery(id+"F0.wireOp",EDGE,"E1481"),sQuery(id+"F0.wireOp",EDGE,"E1482"),sQuery(id+"F0.wireOp",EDGE,"E1483"),sQuery(id+"F0.wireOp",EDGE,"E1484"),sQuery(id+"F0.wireOp",EDGE,"E1485"),sQuery(id+"F0.wireOp",EDGE,"E1486"),sQuery(id+"F0.wireOp",EDGE,"E1487"),sQuery(id+"F0.wireOp",EDGE,"E1488"),sQuery(id+"F0.wireOp",EDGE,"E1489"),sQuery(id+"F0.wireOp",EDGE,"E1490"),sQuery(id+"F0.wireOp",EDGE,"E1491"),sQuery(id+"F0.wireOp",EDGE,"E1492"),sQuery(id+"F0.wireOp",EDGE,"E1493"),sQuery(id+"F0.wireOp",EDGE,"E1494"),sQuery(id+"F0.wireOp",EDGE,"E1495"),sQuery(id+"F0.wireOp",EDGE,"E1496"),sQuery(id+"F0.wireOp",EDGE,"E1497"),sQuery(id+"F0.wireOp",EDGE,"E1498"),sQuery(id+"F0.wireOp",EDGE,"E1499"),sQuery(id+"F0.wireOp",EDGE,"E1500"),sQuery(id+"F0.wireOp",EDGE,"E1501"),sQuery(id+"F0.wireOp",EDGE,"E1502"),sQuery(id+"F0.wireOp",EDGE,"E1503"),sQuery(id+"F0.wireOp",EDGE,"E1504"),sQuery(id+"F0.wireOp",EDGE,"E1505"),sQuery(id+"F0.wireOp",EDGE,"E1506"),sQuery(id+"F0.wireOp",EDGE,"E1507"),sQuery(id+"F0.wireOp",EDGE,"E1508"),sQuery(id+"F0.wireOp",EDGE,"E1509"),sQuery(id+"F0.wireOp",EDGE,"E1510"),sQuery(id+"F0.wireOp",EDGE,"E1511"),sQuery(id+"F0.wireOp",EDGE,"E1512"),sQuery(id+"F0.wireOp",EDGE,"E1513"),sQuery(id+"F0.wireOp",EDGE,"E1514"),sQuery(id+"F0.wireOp",EDGE,"E1515"),sQuery(id+"F0.wireOp",EDGE,"E1516"),sQuery(id+"F0.wireOp",EDGE,"E1517"),sQuery(id+"F0.wireOp",EDGE,"E1518"),sQuery(id+"F0.wireOp",EDGE,"E1519"),sQuery(id+"F0.wireOp",EDGE,"E1520"),sQuery(id+"F0.wireOp",EDGE,"E1521"),sQuery(id+"F0.wireOp",EDGE,"E1522"),sQuery(id+"F0.wireOp",EDGE,"E1523"),sQuery(id+"F0.wireOp",EDGE,"E1524"),sQuery(id+"F0.wireOp",EDGE,"E1525"),sQuery(id+"F0.wireOp",EDGE,"E1526"),sQuery(id+"F0.wireOp",EDGE,"E1527"),sQuery(id+"F0.wireOp",EDGE,"E1528"),sQuery(id+"F0.wireOp",EDGE,"E1529"),sQuery(id+"F0.wireOp",EDGE,"E1530"),sQuery(id+"F0.wireOp",EDGE,"E1531"),sQuery(id+"F0.wireOp",EDGE,"E1532"),sQuery(id+"F0.wireOp",EDGE,"E1533"),sQuery(id+"F0.wireOp",EDGE,"E1534"),sQuery(id+"F0.wireOp",EDGE,"E1535"),sQuery(id+"F0.wireOp",EDGE,"E1536"),sQuery(id+"F0.wireOp",EDGE,"E1537"),sQuery(id+"F0.wireOp",EDGE,"E1538"),sQuery(id+"F0.wireOp",EDGE,"E1539"),sQuery(id+"F0.wireOp",EDGE,"E1540"),sQuery(id+"F0.wireOp",EDGE,"E1541"),sQuery(id+"F0.wireOp",EDGE,"E1542"),sQuery(id+"F0.wireOp",EDGE,"E1543"),sQuery(id+"F0.wireOp",EDGE,"E1544"),sQuery(id+"F0.wireOp",EDGE,"E1545"),sQuery(id+"F0.wireOp",EDGE,"E1546"),sQuery(id+"F0.wireOp",EDGE,"E1547"),sQuery(id+"F0.wireOp",EDGE,"E1548"),sQuery(id+"F0.wireOp",EDGE,"E1549"),sQuery(id+"F0.wireOp",EDGE,"E1550"),sQuery(id+"F0.wireOp",EDGE,"E1551"),sQuery(id+"F0.wireOp",EDGE,"E1552"),sQuery(id+"F0.wireOp",EDGE,"E1553"),sQuery(id+"F0.wireOp",EDGE,"E1554"),sQuery(id+"F0.wireOp",EDGE,"E1555"),sQuery(id+"F0.wireOp",EDGE,"E1556"),sQuery(id+"F0.wireOp",EDGE,"E1557"),sQuery(id+"F0.wireOp",EDGE,"E1558"),sQuery(id+"F0.wireOp",EDGE,"E1559"),sQuery(id+"F0.wireOp",EDGE,"E1560"),sQuery(id+"F0.wireOp",EDGE,"E1561"),sQuery(id+"F0.wireOp",EDGE,"E1562"),sQuery(id+"F0.wireOp",EDGE,"E1563"),sQuery(id+"F0.wireOp",EDGE,"E1564"),sQuery(id+"F0.wireOp",EDGE,"E1565"),sQuery(id+"F0.wireOp",EDGE,"E1566"),sQuery(id+"F0.wireOp",EDGE,"E1567"),sQuery(id+"F0.wireOp",EDGE,"E1568"),sQuery(id+"F0.wireOp",EDGE,"E1569"),sQuery(id+"F0.wireOp",EDGE,"E1570"),sQuery(id+"F0.wireOp",EDGE,"E1571"),sQuery(id+"F0.wireOp",EDGE,"E1572"),sQuery(id+"F0.wireOp",EDGE,"E1573"),sQuery(id+"F0.wireOp",EDGE,"E1574"),sQuery(id+"F0.wireOp",EDGE,"E1575"),sQuery(id+"F0.wireOp",EDGE,"E1576"),sQuery(id+"F0.wireOp",EDGE,"E1577"),sQuery(id+"F0.wireOp",EDGE,"E1578"),sQuery(id+"F0.wireOp",EDGE,"E1579"),sQuery(id+"F0.wireOp",EDGE,"E1580"),sQuery(id+"F0.wireOp",EDGE,"E1581"),sQuery(id+"F0.wireOp",EDGE,"E1582"),sQuery(id+"F0.wireOp",EDGE,"E1583"),sQuery(id+"F0.wireOp",EDGE,"E1584"),sQuery(id+"F0.wireOp",EDGE,"E1585"),sQuery(id+"F0.wireOp",EDGE,"E1586"),sQuery(id+"F0.wireOp",EDGE,"E1587"),sQuery(id+"F0.wireOp",EDGE,"E1588"),sQuery(id+"F0.wireOp",EDGE,"E1589"),sQuery(id+"F0.wireOp",EDGE,"E1590"),sQuery(id+"F0.wireOp",EDGE,"E1591"),sQuery(id+"F0.wireOp",EDGE,"E1592"),sQuery(id+"F0.wireOp",EDGE,"E1593"),sQuery(id+"F0.wireOp",EDGE,"E1594"),sQuery(id+"F0.wireOp",EDGE,"E1595"),sQuery(id+"F0.wireOp",EDGE,"E1596"),sQuery(id+"F0.wireOp",EDGE,"E1597"),sQuery(id+"F0.wireOp",EDGE,"E1598"),sQuery(id+"F0.wireOp",EDGE,"E1599"),sQuery(id+"F0.wireOp",EDGE,"E1600"),sQuery(id+"F0.wireOp",EDGE,"E1601"),sQuery(id+"F0.wireOp",EDGE,"E1602"),sQuery(id+"F0.wireOp",EDGE,"E1603"),sQuery(id+"F0.wireOp",EDGE,"E1604"),sQuery(id+"F0.wireOp",EDGE,"E1605"),sQuery(id+"F0.wireOp",EDGE,"E1606"),sQuery(id+"F0.wireOp",EDGE,"E1607"),sQuery(id+"F0.wireOp",EDGE,"E1608"),sQuery(id+"F0.wireOp",EDGE,"E1609"),sQuery(id+"F0.wireOp",EDGE,"E1610"),sQuery(id+"F0.wireOp",EDGE,"E1611"),sQuery(id+"F0.wireOp",EDGE,"E1612"),sQuery(id+"F0.wireOp",EDGE,"E1613"),sQuery(id+"F0.wireOp",EDGE,"E1614"),sQuery(id+"F0.wireOp",EDGE,"E1615"),sQuery(id+"F0.wireOp",EDGE,"E1616"),sQuery(id+"F0.wireOp",EDGE,"E1617"),sQuery(id+"F0.wireOp",EDGE,"E1618"),sQuery(id+"F0.wireOp",EDGE,"E1619"),sQuery(id+"F0.wireOp",EDGE,"E1620"),sQuery(id+"F0.wireOp",EDGE,"E1621"),sQuery(id+"F0.wireOp",EDGE,"E1622"),sQuery(id+"F0.wireOp",EDGE,"E1623"),sQuery(id+"F0.wireOp",EDGE,"E1624"),sQuery(id+"F0.wireOp",EDGE,"E1625"),sQuery(id+"F0.wireOp",EDGE,"E1626"),sQuery(id+"F0.wireOp",EDGE,"E1627"),sQuery(id+"F0.wireOp",EDGE,"E1628"),sQuery(id+"F0.wireOp",EDGE,"E1629"),sQuery(id+"F0.wireOp",EDGE,"E1630"),sQuery(id+"F0.wireOp",EDGE,"E1631"),sQuery(id+"F0.wireOp",EDGE,"E1632"),sQuery(id+"F0.wireOp",EDGE,"E1633"),sQuery(id+"F0.wireOp",EDGE,"E1634"),sQuery(id+"F0.wireOp",EDGE,"E1635"),sQuery(id+"F0.wireOp",EDGE,"E1636"),sQuery(id+"F0.wireOp",EDGE,"E1637"),sQuery(id+"F0.wireOp",EDGE,"E1638"),sQuery(id+"F0.wireOp",EDGE,"E1639"),sQuery(id+"F0.wireOp",EDGE,"E1640"),sQuery(id+"F0.wireOp",EDGE,"E1641"),sQuery(id+"F0.wireOp",EDGE,"E1642"),sQuery(id+"F0.wireOp",EDGE,"E1643"),sQuery(id+"F0.wireOp",EDGE,"E1644"),sQuery(id+"F0.wireOp",EDGE,"E1645"),sQuery(id+"F0.wireOp",EDGE,"E1646"),sQuery(id+"F0.wireOp",EDGE,"E1647"),sQuery(id+"F0.wireOp",EDGE,"E1648"),sQuery(id+"F0.wireOp",EDGE,"E1649"),sQuery(id+"F0.wireOp",EDGE,"E1650"),sQuery(id+"F0.wireOp",EDGE,"E1651"),sQuery(id+"F0.wireOp",EDGE,"E1652"),sQuery(id+"F0.wireOp",EDGE,"E1653"),sQuery(id+"F0.wireOp",EDGE,"E1654"),sQuery(id+"F0.wireOp",EDGE,"E1655"),sQuery(id+"F0.wireOp",EDGE,"E1656"),sQuery(id+"F0.wireOp",EDGE,"E1657"),sQuery(id+"F0.wireOp",EDGE,"E1658"),sQuery(id+"F0.wireOp",EDGE,"E1659"),sQuery(id+"F0.wireOp",EDGE,"E1660"),sQuery(id+"F0.wireOp",EDGE,"E1661"),sQuery(id+"F0.wireOp",EDGE,"E1662"),sQuery(id+"F0.wireOp",EDGE,"E1663"),sQuery(id+"F0.wireOp",EDGE,"E1664"),sQuery(id+"F0.wireOp",EDGE,"E1665"),sQuery(id+"F0.wireOp",EDGE,"E1666"),sQuery(id+"F0.wireOp",EDGE,"E1667"),sQuery(id+"F0.wireOp",EDGE,"E1668"),sQuery(id+"F0.wireOp",EDGE,"E1669"),sQuery(id+"F0.wireOp",EDGE,"E1670"),sQuery(id+"F0.wireOp",EDGE,"E1671"),sQuery(id+"F0.wireOp",EDGE,"E1672"),sQuery(id+"F0.wireOp",EDGE,"E1673"),sQuery(id+"F0.wireOp",EDGE,"E1674"),sQuery(id+"F0.wireOp",EDGE,"E1675"),sQuery(id+"F0.wireOp",EDGE,"E1676"),sQuery(id+"F0.wireOp",EDGE,"E1677"),sQuery(id+"F0.wireOp",EDGE,"E1678"),sQuery(id+"F0.wireOp",EDGE,"E1679"),sQuery(id+"F0.wireOp",EDGE,"E1680"),sQuery(id+"F0.wireOp",EDGE,"E1681"),sQuery(id+"F0.wireOp",EDGE,"E1682"),sQuery(id+"F0.wireOp",EDGE,"E1683"),sQuery(id+"F0.wireOp",EDGE,"E1684"),sQuery(id+"F0.wireOp",EDGE,"E1685"),sQuery(id+"F0.wireOp",EDGE,"E1686"),sQuery(id+"F0.wireOp",EDGE,"E1687"),sQuery(id+"F0.wireOp",EDGE,"E1688"),sQuery(id+"F0.wireOp",EDGE,"E1689"),sQuery(id+"F0.wireOp",EDGE,"E1690"),sQuery(id+"F0.wireOp",EDGE,"E1691"),sQuery(id+"F0.wireOp",EDGE,"E1692"),sQuery(id+"F0.wireOp",EDGE,"E1693"),sQuery(id+"F0.wireOp",EDGE,"E1694"),sQuery(id+"F0.wireOp",EDGE,"E1695"),sQuery(id+"F0.wireOp",EDGE,"E1696"),sQuery(id+"F0.wireOp",EDGE,"E1697"),sQuery(id+"F0.wireOp",EDGE,"E1698"),sQuery(id+"F0.wireOp",EDGE,"E1699"),sQuery(id+"F0.wireOp",EDGE,"E1700"),sQuery(id+"F0.wireOp",EDGE,"E1701"),sQuery(id+"F0.wireOp",EDGE,"E1702"),sQuery(id+"F0.wireOp",EDGE,"E1703"),sQuery(id+"F0.wireOp",EDGE,"E1704"),sQuery(id+"F0.wireOp",EDGE,"E1705"),sQuery(id+"F0.wireOp",EDGE,"E1706"),sQuery(id+"F0.wireOp",EDGE,"E1707"),sQuery(id+"F0.wireOp",EDGE,"E1708"),sQuery(id+"F0.wireOp",EDGE,"E1709"),sQuery(id+"F0.wireOp",EDGE,"E1710"),sQuery(id+"F0.wireOp",EDGE,"E1711"),sQuery(id+"F0.wireOp",EDGE,"E1712"),sQuery(id+"F0.wireOp",EDGE,"E1713"),sQuery(id+"F0.wireOp",EDGE,"E1714"),sQuery(id+"F0.wireOp",EDGE,"E1715"),sQuery(id+"F0.wireOp",EDGE,"E1716"),sQuery(id+"F0.wireOp",EDGE,"E1717"),sQuery(id+"F0.wireOp",EDGE,"E1718"),sQuery(id+"F0.wireOp",EDGE,"E1719"),sQuery(id+"F0.wireOp",EDGE,"E1720"),sQuery(id+"F0.wireOp",EDGE,"E1721"),sQuery(id+"F0.wireOp",EDGE,"E1722"),sQuery(id+"F0.wireOp",EDGE,"E1723"),sQuery(id+"F0.wireOp",EDGE,"E1724"),sQuery(id+"F0.wireOp",EDGE,"E1725"),sQuery(id+"F0.wireOp",EDGE,"E1726"),sQuery(id+"F0.wireOp",EDGE,"E1727"),sQuery(id+"F0.wireOp",EDGE,"E1728"),sQuery(id+"F0.wireOp",EDGE,"E1729"),sQuery(id+"F0.wireOp",EDGE,"E1730"),sQuery(id+"F0.wireOp",EDGE,"E1731"),sQuery(id+"F0.wireOp",EDGE,"E1732"),sQuery(id+"F0.wireOp",EDGE,"E1733"),sQuery(id+"F0.wireOp",EDGE,"E1734"),sQuery(id+"F0.wireOp",EDGE,"E1735"),sQuery(id+"F0.wireOp",EDGE,"E1736"),sQuery(id+"F0.wireOp",EDGE,"E1737"),sQuery(id+"F0.wireOp",EDGE,"E1738"),sQuery(id+"F0.wireOp",EDGE,"E1739"),sQuery(id+"F0.wireOp",EDGE,"E1740"),sQuery(id+"F0.wireOp",EDGE,"E1741"),sQuery(id+"F0.wireOp",EDGE,"E1742"),sQuery(id+"F0.wireOp",EDGE,"E1743"),sQuery(id+"F0.wireOp",EDGE,"E1744"),sQuery(id+"F0.wireOp",EDGE,"E1745"),sQuery(id+"F0.wireOp",EDGE,"E1746"),sQuery(id+"F0.wireOp",EDGE,"E1747"),sQuery(id+"F0.wireOp",EDGE,"E1748"),sQuery(id+"F0.wireOp",EDGE,"E1749"),sQuery(id+"F0.wireOp",EDGE,"E1750"),sQuery(id+"F0.wireOp",EDGE,"E1751"),sQuery(id+"F0.wireOp",EDGE,"E1752"),sQuery(id+"F0.wireOp",EDGE,"E1753"),sQuery(id+"F0.wireOp",EDGE,"E1754"),sQuery(id+"F0.wireOp",EDGE,"E1755"),sQuery(id+"F0.wireOp",EDGE,"E1756"),sQuery(id+"F0.wireOp",EDGE,"E1757"),sQuery(id+"F0.wireOp",EDGE,"E1758"),sQuery(id+"F0.wireOp",EDGE,"E1759"),sQuery(id+"F0.wireOp",EDGE,"E1760"),sQuery(id+"F0.wireOp",EDGE,"E1761"),sQuery(id+"F0.wireOp",EDGE,"E1762"),sQuery(id+"F0.wireOp",EDGE,"E1763"),sQuery(id+"F0.wireOp",EDGE,"E1764"),sQuery(id+"F0.wireOp",EDGE,"E1765"),sQuery(id+"F0.wireOp",EDGE,"E1766"),sQuery(id+"F0.wireOp",EDGE,"E1767"),sQuery(id+"F0.wireOp",EDGE,"E1768"),sQuery(id+"F0.wireOp",EDGE,"E1769"),sQuery(id+"F0.wireOp",EDGE,"E1770"),sQuery(id+"F0.wireOp",EDGE,"E1771"),sQuery(id+"F0.wireOp",EDGE,"E1772"),sQuery(id+"F0.wireOp",EDGE,"E1773"),sQuery(id+"F0.wireOp",EDGE,"E1774"),sQuery(id+"F0.wireOp",EDGE,"E1775"),sQuery(id+"F0.wireOp",EDGE,"E1776"),sQuery(id+"F0.wireOp",EDGE,"E1777"),sQuery(id+"F0.wireOp",EDGE,"E1778"),sQuery(id+"F0.wireOp",EDGE,"E1779"),sQuery(id+"F0.wireOp",EDGE,"E1780"),sQuery(id+"F0.wireOp",EDGE,"E1781"),sQuery(id+"F0.wireOp",EDGE,"E1782"),sQuery(id+"F0.wireOp",EDGE,"E1783"),sQuery(id+"F0.wireOp",EDGE,"E1784"),sQuery(id+"F0.wireOp",EDGE,"E1785"),sQuery(id+"F0.wireOp",EDGE,"E1786"),sQuery(id+"F0.wireOp",EDGE,"E1787"),sQuery(id+"F0.wireOp",EDGE,"E1788"),sQuery(id+"F0.wireOp",EDGE,"E1789"),sQuery(id+"F0.wireOp",EDGE,"E1790"),sQuery(id+"F0.wireOp",EDGE,"E1791"),sQuery(id+"F0.wireOp",EDGE,"E1792"),sQuery(id+"F0.wireOp",EDGE,"E1793"),sQuery(id+"F0.wireOp",EDGE,"E1794"),sQuery(id+"F0.wireOp",EDGE,"E1795"),sQuery(id+"F0.wireOp",EDGE,"E1796"),sQuery(id+"F0.wireOp",EDGE,"E1797"),sQuery(id+"F0.wireOp",EDGE,"E1798"),sQuery(id+"F0.wireOp",EDGE,"E1799"),sQuery(id+"F0.wireOp",EDGE,"E1800"),sQuery(id+"F0.wireOp",EDGE,"E1801"),sQuery(id+"F0.wireOp",EDGE,"E1802"),sQuery(id+"F0.wireOp",EDGE,"E1803"),sQuery(id+"F0.wireOp",EDGE,"E1804"),sQuery(id+"F0.wireOp",EDGE,"E1805"),sQuery(id+"F0.wireOp",EDGE,"E1806"),sQuery(id+"F0.wireOp",EDGE,"E1807"),sQuery(id+"F0.wireOp",EDGE,"E1808"),sQuery(id+"F0.wireOp",EDGE,"E1809"),sQuery(id+"F0.wireOp",EDGE,"E1810"),sQuery(id+"F0.wireOp",EDGE,"E1811"),sQuery(id+"F0.wireOp",EDGE,"E1812"),sQuery(id+"F0.wireOp",EDGE,"E1813"),sQuery(id+"F0.wireOp",EDGE,"E1814"),sQuery(id+"F0.wireOp",EDGE,"E1815"),sQuery(id+"F0.wireOp",EDGE,"E1816"),sQuery(id+"F0.wireOp",EDGE,"E1817"),sQuery(id+"F0.wireOp",EDGE,"E1818"),sQuery(id+"F0.wireOp",EDGE,"E1819"),sQuery(id+"F0.wireOp",EDGE,"E1820"),sQuery(id+"F0.wireOp",EDGE,"E1821"),sQuery(id+"F0.wireOp",EDGE,"E1822"),sQuery(id+"F0.wireOp",EDGE,"E1823"),sQuery(id+"F0.wireOp",EDGE,"E1824"),sQuery(id+"F0.wireOp",EDGE,"E1825"),sQuery(id+"F0.wireOp",EDGE,"E1826"),sQuery(id+"F0.wireOp",EDGE,"E1827"),sQuery(id+"F0.wireOp",EDGE,"E1828"),sQuery(id+"F0.wireOp",EDGE,"E1829"),sQuery(id+"F0.wireOp",EDGE,"E1830"),sQuery(id+"F0.wireOp",EDGE,"E1831"),sQuery(id+"F0.wireOp",EDGE,"E1832"),sQuery(id+"F0.wireOp",EDGE,"E1833"),sQuery(id+"F0.wireOp",EDGE,"E1834"),sQuery(id+"F0.wireOp",EDGE,"E1835"),sQuery(id+"F0.wireOp",EDGE,"E1836"),sQuery(id+"F0.wireOp",EDGE,"E1837"),sQuery(id+"F0.wireOp",EDGE,"E1838"),sQuery(id+"F0.wireOp",EDGE,"E1839"),sQuery(id+"F0.wireOp",EDGE,"E1840"),sQuery(id+"F0.wireOp",EDGE,"E1841"),sQuery(id+"F0.wireOp",EDGE,"E1842"),sQuery(id+"F0.wireOp",EDGE,"E1843"),sQuery(id+"F0.wireOp",EDGE,"E1844"),sQuery(id+"F0.wireOp",EDGE,"E1845"),sQuery(id+"F0.wireOp",EDGE,"E1846"),sQuery(id+"F0.wireOp",EDGE,"E1847"),sQuery(id+"F0.wireOp",EDGE,"E1848"),sQuery(id+"F0.wireOp",EDGE,"E1849"),sQuery(id+"F0.wireOp",EDGE,"E1850"),sQuery(id+"F0.wireOp",EDGE,"E1851"),sQuery(id+"F0.wireOp",EDGE,"E1852"),sQuery(id+"F0.wireOp",EDGE,"E1853"),sQuery(id+"F0.wireOp",EDGE,"E1854"),sQuery(id+"F0.wireOp",EDGE,"E1855"),sQuery(id+"F0.wireOp",EDGE,"E1856"),sQuery(id+"F0.wireOp",EDGE,"E1857"),sQuery(id+"F0.wireOp",EDGE,"E1858"),sQuery(id+"F0.wireOp",EDGE,"E1859"),sQuery(id+"F0.wireOp",EDGE,"E1860"),sQuery(id+"F0.wireOp",EDGE,"E1861"),sQuery(id+"F0.wireOp",EDGE,"E1862"),sQuery(id+"F0.wireOp",EDGE,"E1863"),sQuery(id+"F0.wireOp",EDGE,"E1864"),sQuery(id+"F0.wireOp",EDGE,"E1865"),sQuery(id+"F0.wireOp",EDGE,"E1866"),sQuery(id+"F0.wireOp",EDGE,"E1867"),sQuery(id+"F0.wireOp",EDGE,"E1868"),sQuery(id+"F0.wireOp",EDGE,"E1869"),sQuery(id+"F0.wireOp",EDGE,"E1870"),sQuery(id+"F0.wireOp",EDGE,"E1871"),sQuery(id+"F0.wireOp",EDGE,"E1872"),sQuery(id+"F0.wireOp",EDGE,"E1873"),sQuery(id+"F0.wireOp",EDGE,"E1874"),sQuery(id+"F0.wireOp",EDGE,"E1875"),sQuery(id+"F0.wireOp",EDGE,"E1876"),sQuery(id+"F0.wireOp",EDGE,"E1877"),sQuery(id+"F0.wireOp",EDGE,"E1878"),sQuery(id+"F0.wireOp",EDGE,"E1879"),sQuery(id+"F0.wireOp",EDGE,"E1880"),sQuery(id+"F0.wireOp",EDGE,"E1881"),sQuery(id+"F0.wireOp",EDGE,"E1882"),sQuery(id+"F0.wireOp",EDGE,"E1883"),sQuery(id+"F0.wireOp",EDGE,"E1884"),sQuery(id+"F0.wireOp",EDGE,"E1885"),sQuery(id+"F0.wireOp",EDGE,"E1886"),sQuery(id+"F0.wireOp",EDGE,"E1887"),sQuery(id+"F0.wireOp",EDGE,"E1888"),sQuery(id+"F0.wireOp",EDGE,"E1889"),sQuery(id+"F0.wireOp",EDGE,"E1890"),sQuery(id+"F0.wireOp",EDGE,"E1891"),sQuery(id+"F0.wireOp",EDGE,"E1892"),sQuery(id+"F0.wireOp",EDGE,"E1893"),sQuery(id+"F0.wireOp",EDGE,"E1894"),sQuery(id+"F0.wireOp",EDGE,"E1895"),sQuery(id+"F0.wireOp",EDGE,"E1896"),sQuery(id+"F0.wireOp",EDGE,"E1897"),sQuery(id+"F0.wireOp",EDGE,"E1898"),sQuery(id+"F0.wireOp",EDGE,"E1899"),sQuery(id+"F0.wireOp",EDGE,"E1900"),sQuery(id+"F0.wireOp",EDGE,"E1901"),sQuery(id+"F0.wireOp",EDGE,"E1902"),sQuery(id+"F0.wireOp",EDGE,"E1903"),sQuery(id+"F0.wireOp",EDGE,"E1904"),sQuery(id+"F0.wireOp",EDGE,"E1905"),sQuery(id+"F0.wireOp",EDGE,"E1906"),sQuery(id+"F0.wireOp",EDGE,"E1907"),sQuery(id+"F0.wireOp",EDGE,"E1908"),sQuery(id+"F0.wireOp",EDGE,"E1909"),sQuery(id+"F0.wireOp",EDGE,"E1910"),sQuery(id+"F0.wireOp",EDGE,"E1911"),sQuery(id+"F0.wireOp",EDGE,"E1912"),sQuery(id+"F0.wireOp",EDGE,"E1913"),sQuery(id+"F0.wireOp",EDGE,"E1914"),sQuery(id+"F0.wireOp",EDGE,"E1915"),sQuery(id+"F0.wireOp",EDGE,"E1916"),sQuery(id+"F0.wireOp",EDGE,"E1917"),sQuery(id+"F0.wireOp",EDGE,"E1918"),sQuery(id+"F0.wireOp",EDGE,"E1919"),sQuery(id+"F0.wireOp",EDGE,"E1920"),sQuery(id+"F0.wireOp",EDGE,"E1921"),sQuery(id+"F0.wireOp",EDGE,"E1922"),sQuery(id+"F0.wireOp",EDGE,"E1923"),sQuery(id+"F0.wireOp",EDGE,"E1924"),sQuery(id+"F0.wireOp",EDGE,"E1925"),sQuery(id+"F0.wireOp",EDGE,"E1926"),sQuery(id+"F0.wireOp",EDGE,"E1927"),sQuery(id+"F0.wireOp",EDGE,"E1928"),sQuery(id+"F0.wireOp",EDGE,"E1929"),sQuery(id+"F0.wireOp",EDGE,"E1930"),sQuery(id+"F0.wireOp",EDGE,"E1931"),sQuery(id+"F0.wireOp",EDGE,"E1932"),sQuery(id+"F0.wireOp",EDGE,"E1933"),sQuery(id+"F0.wireOp",EDGE,"E1934"),sQuery(id+"F0.wireOp",EDGE,"E1935"),sQuery(id+"F0.wireOp",EDGE,"E1936"),sQuery(id+"F0.wireOp",EDGE,"E1937"),sQuery(id+"F0.wireOp",EDGE,"E1938"),sQuery(id+"F0.wireOp",EDGE,"E1939"),sQuery(id+"F0.wireOp",EDGE,"E1940"),sQuery(id+"F0.wireOp",EDGE,"E1941"),sQuery(id+"F0.wireOp",EDGE,"E1942"),sQuery(id+"F0.wireOp",EDGE,"E1943"),sQuery(id+"F0.wireOp",EDGE,"E1944"),sQuery(id+"F0.wireOp",EDGE,"E1945"),sQuery(id+"F0.wireOp",EDGE,"E1946"),sQuery(id+"F0.wireOp",EDGE,"E1947"),sQuery(id+"F0.wireOp",EDGE,"E1948"),sQuery(id+"F0.wireOp",EDGE,"E1949"),sQuery(id+"F0.wireOp",EDGE,"E1950"),sQuery(id+"F0.wireOp",EDGE,"E1951"),sQuery(id+"F0.wireOp",EDGE,"E1952"),sQuery(id+"F0.wireOp",EDGE,"E1953"),sQuery(id+"F0.wireOp",EDGE,"E1954"),sQuery(id+"F0.wireOp",EDGE,"E1955"),sQuery(id+"F0.wireOp",EDGE,"E1956"),sQuery(id+"F0.wireOp",EDGE,"E1957"),sQuery(id+"F0.wireOp",EDGE,"E1958"),sQuery(id+"F0.wireOp",EDGE,"E1959"),sQuery(id+"F0.wireOp",EDGE,"E1960"),sQuery(id+"F0.wireOp",EDGE,"E1961"),sQuery(id+"F0.wireOp",EDGE,"E1962"),sQuery(id+"F0.wireOp",EDGE,"E1963"),sQuery(id+"F0.wireOp",EDGE,"E1964"),sQuery(id+"F0.wireOp",EDGE,"E1965"),sQuery(id+"F0.wireOp",EDGE,"E1966"),sQuery(id+"F0.wireOp",EDGE,"E1967"),sQuery(id+"F0.wireOp",EDGE,"E1968"),sQuery(id+"F0.wireOp",EDGE,"E1969"),sQuery(id+"F0.wireOp",EDGE,"E1970"),sQuery(id+"F0.wireOp",EDGE,"E1971"),sQuery(id+"F0.wireOp",EDGE,"E1972"),sQuery(id+"F0.wireOp",EDGE,"E1973"),sQuery(id+"F0.wireOp",EDGE,"E1974"),sQuery(id+"F0.wireOp",EDGE,"E1975"),sQuery(id+"F0.wireOp",EDGE,"E1976"),sQuery(id+"F0.wireOp",EDGE,"E1977"),sQuery(id+"F0.wireOp",EDGE,"E1978"),sQuery(id+"F0.wireOp",EDGE,"E1979"),sQuery(id+"F0.wireOp",EDGE,"E1980"),sQuery(id+"F0.wireOp",EDGE,"E1981"),sQuery(id+"F0.wireOp",EDGE,"E1982"),sQuery(id+"F0.wireOp",EDGE,"E1983"),sQuery(id+"F0.wireOp",EDGE,"E1984"),sQuery(id+"F0.wireOp",EDGE,"E1985"),sQuery(id+"F0.wireOp",EDGE,"E1986"),sQuery(id+"F0.wireOp",EDGE,"E1987"),sQuery(id+"F0.wireOp",EDGE,"E1988"),sQuery(id+"F0.wireOp",EDGE,"E1989"),sQuery(id+"F0.wireOp",EDGE,"E1990"),sQuery(id+"F0.wireOp",EDGE,"E1991"),sQuery(id+"F0.wireOp",EDGE,"E1992"),sQuery(id+"F0.wireOp",EDGE,"E1993"),sQuery(id+"F0.wireOp",EDGE,"E1994"),sQuery(id+"F0.wireOp",EDGE,"E1995"),sQuery(id+"F0.wireOp",EDGE,"E1996"),sQuery(id+"F0.wireOp",EDGE,"E1997"),sQuery(id+"F0.wireOp",EDGE,"E1998"),sQuery(id+"F0.wireOp",EDGE,"E1999"),sQuery(id+"F0.wireOp",EDGE,"E2000"),sQuery(id+"F0.wireOp",EDGE,"E2001"),sQuery(id+"F0.wireOp",EDGE,"E2002"),sQuery(id+"F0.wireOp",EDGE,"E2003"),sQuery(id+"F0.wireOp",EDGE,"E2004"),sQuery(id+"F0.wireOp",EDGE,"E2005"),sQuery(id+"F0.wireOp",EDGE,"E2006"),sQuery(id+"F0.wireOp",EDGE,"E2007"),sQuery(id+"F0.wireOp",EDGE,"E2008"),sQuery(id+"F0.wireOp",EDGE,"E2009"),sQuery(id+"F0.wireOp",EDGE,"E2010"),sQuery(id+"F0.wireOp",EDGE,"E2011"),sQuery(id+"F0.wireOp",EDGE,"E2012"),sQuery(id+"F0.wireOp",EDGE,"E2013"),sQuery(id+"F0.wireOp",EDGE,"E2014"),sQuery(id+"F0.wireOp",EDGE,"E2015"),sQuery(id+"F0.wireOp",EDGE,"E2016"),sQuery(id+"F0.wireOp",EDGE,"E2017"),sQuery(id+"F0.wireOp",EDGE,"E2018"),sQuery(id+"F0.wireOp",EDGE,"E2019"),sQuery(id+"F0.wireOp",EDGE,"E2020"),sQuery(id+"F0.wireOp",EDGE,"E2021"),sQuery(id+"F0.wireOp",EDGE,"E2022"),sQuery(id+"F0.wireOp",EDGE,"E2023"),sQuery(id+"F0.wireOp",EDGE,"E2024"),sQuery(id+"F0.wireOp",EDGE,"E2025"),sQuery(id+"F0.wireOp",EDGE,"E2026"),sQuery(id+"F0.wireOp",EDGE,"E2027"),sQuery(id+"F0.wireOp",EDGE,"E2028"),sQuery(id+"F0.wireOp",EDGE,"E2029"),sQuery(id+"F0.wireOp",EDGE,"E2030"),sQuery(id+"F0.wireOp",EDGE,"E2031"),sQuery(id+"F0.wireOp",EDGE,"E2032"),sQuery(id+"F0.wireOp",EDGE,"E2033"),sQuery(id+"F0.wireOp",EDGE,"E2034"),sQuery(id+"F0.wireOp",EDGE,"E2035"),sQuery(id+"F0.wireOp",EDGE,"E2036"),sQuery(id+"F0.wireOp",EDGE,"E2037"),sQuery(id+"F0.wireOp",EDGE,"E2038"),sQuery(id+"F0.wireOp",EDGE,"E2039"),sQuery(id+"F0.wireOp",EDGE,"E2040"),sQuery(id+"F0.wireOp",EDGE,"E2041"),sQuery(id+"F0.wireOp",EDGE,"E2042"),sQuery(id+"F0.wireOp",EDGE,"E2043"),sQuery(id+"F0.wireOp",EDGE,"E2044"),sQuery(id+"F0.wireOp",EDGE,"E2045"),sQuery(id+"F0.wireOp",EDGE,"E2046"),sQuery(id+"F0.wireOp",EDGE,"E2047"),sQuery(id+"F0.wireOp",EDGE,"E2048"),sQuery(id+"F0.wireOp",EDGE,"E2049"),sQuery(id+"F0.wireOp",EDGE,"E2050"),sQuery(id+"F0.wireOp",EDGE,"E2051"),sQuery(id+"F0.wireOp",EDGE,"E2052"),sQuery(id+"F0.wireOp",EDGE,"E2053"),sQuery(id+"F0.wireOp",EDGE,"E2054"),sQuery(id+"F0.wireOp",EDGE,"E2055"),sQuery(id+"F0.wireOp",EDGE,"E2056"),sQuery(id+"F0.wireOp",EDGE,"E2057"),sQuery(id+"F0.wireOp",EDGE,"E2058"),sQuery(id+"F0.wireOp",EDGE,"E2059"),sQuery(id+"F0.wireOp",EDGE,"E2060"),sQuery(id+"F0.wireOp",EDGE,"E2061"),sQuery(id+"F0.wireOp",EDGE,"E2062"),sQuery(id+"F0.wireOp",EDGE,"E2063"),sQuery(id+"F0.wireOp",EDGE,"E2064"),sQuery(id+"F0.wireOp",EDGE,"E2065"),sQuery(id+"F0.wireOp",EDGE,"E2066"),sQuery(id+"F0.wireOp",EDGE,"E2067"),sQuery(id+"F0.wireOp",EDGE,"E2068"),sQuery(id+"F0.wireOp",EDGE,"E2069"),sQuery(id+"F0.wireOp",EDGE,"E2070"),sQuery(id+"F0.wireOp",EDGE,"E2071"),sQuery(id+"F0.wireOp",EDGE,"E2072"),sQuery(id+"F0.wireOp",EDGE,"E2073"),sQuery(id+"F0.wireOp",EDGE,"E2074"),sQuery(id+"F0.wireOp",EDGE,"E2075"),sQuery(id+"F0.wireOp",EDGE,"E2076"),sQuery(id+"F0.wireOp",EDGE,"E2077"),sQuery(id+"F0.wireOp",EDGE,"E2078"),sQuery(id+"F0.wireOp",EDGE,"E2079"),sQuery(id+"F0.wireOp",EDGE,"E2080"),sQuery(id+"F0.wireOp",EDGE,"E2081"),sQuery(id+"F0.wireOp",EDGE,"E2082"),sQuery(id+"F0.wireOp",EDGE,"E2083"),sQuery(id+"F0.wireOp",EDGE,"E2084"),sQuery(id+"F0.wireOp",EDGE,"E2085"),sQuery(id+"F0.wireOp",EDGE,"E2086"),sQuery(id+"F0.wireOp",EDGE,"E2087"),sQuery(id+"F0.wireOp",EDGE,"E2088"),sQuery(id+"F0.wireOp",EDGE,"E2089"),sQuery(id+"F0.wireOp",EDGE,"E2090"),sQuery(id+"F0.wireOp",EDGE,"E2091"),sQuery(id+"F0.wireOp",EDGE,"E2092"),sQuery(id+"F0.wireOp",EDGE,"E2093"),sQuery(id+"F0.wireOp",EDGE,"E2094"),sQuery(id+"F0.wireOp",EDGE,"E2095"),sQuery(id+"F0.wireOp",EDGE,"E2096"),sQuery(id+"F0.wireOp",EDGE,"E2097"),sQuery(id+"F0.wireOp",EDGE,"E2098"),sQuery(id+"F0.wireOp",EDGE,"E2099"),sQuery(id+"F0.wireOp",EDGE,"E2100"),sQuery(id+"F0.wireOp",EDGE,"E2101"),sQuery(id+"F0.wireOp",EDGE,"E2102"),sQuery(id+"F0.wireOp",EDGE,"E2103"),sQuery(id+"F0.wireOp",EDGE,"E2104"),sQuery(id+"F0.wireOp",EDGE,"E2105"),sQuery(id+"F0.wireOp",EDGE,"E2106"),sQuery(id+"F0.wireOp",EDGE,"E2107"),sQuery(id+"F0.wireOp",EDGE,"E2108"),sQuery(id+"F0.wireOp",EDGE,"E2109"),sQuery(id+"F0.wireOp",EDGE,"E2110"),sQuery(id+"F0.wireOp",EDGE,"E2111"),sQuery(id+"F0.wireOp",EDGE,"E2112"),sQuery(id+"F0.wireOp",EDGE,"E2113"),sQuery(id+"F0.wireOp",EDGE,"E2114"),sQuery(id+"F0.wireOp",EDGE,"E2115"),sQuery(id+"F0.wireOp",EDGE,"E2116"),sQuery(id+"F0.wireOp",EDGE,"E2117"),sQuery(id+"F0.wireOp",EDGE,"E2118"),sQuery(id+"F0.wireOp",EDGE,"E2119"),sQuery(id+"F0.wireOp",EDGE,"E2120"),sQuery(id+"F0.wireOp",EDGE,"E2121"),sQuery(id+"F0.wireOp",EDGE,"E2122"),sQuery(id+"F0.wireOp",EDGE,"E2123"),sQuery(id+"F0.wireOp",EDGE,"E2124"),sQuery(id+"F0.wireOp",EDGE,"E2125"),sQuery(id+"F0.wireOp",EDGE,"E2126"),sQuery(id+"F0.wireOp",EDGE,"E2127"),sQuery(id+"F0.wireOp",EDGE,"E2128"),sQuery(id+"F0.wireOp",EDGE,"E2129"),sQuery(id+"F0.wireOp",EDGE,"E2130"),sQuery(id+"F0.wireOp",EDGE,"E2131"),sQuery(id+"F0.wireOp",EDGE,"E2132"),sQuery(id+"F0.wireOp",EDGE,"E2133"),sQuery(id+"F0.wireOp",EDGE,"E2134"),sQuery(id+"F0.wireOp",EDGE,"E2135"),sQuery(id+"F0.wireOp",EDGE,"E2136"),sQuery(id+"F0.wireOp",EDGE,"E2137"),sQuery(id+"F0.wireOp",EDGE,"E2138"),sQuery(id+"F0.wireOp",EDGE,"E2139"),sQuery(id+"F0.wireOp",EDGE,"E2140"),sQuery(id+"F0.wireOp",EDGE,"E2141"),sQuery(id+"F0.wireOp",EDGE,"E2142"),sQuery(id+"F0.wireOp",EDGE,"E2143"),sQuery(id+"F0.wireOp",EDGE,"E2144"),sQuery(id+"F0.wireOp",EDGE,"E2145"),sQuery(id+"F0.wireOp",EDGE,"E2146"),sQuery(id+"F0.wireOp",EDGE,"E2147"),sQuery(id+"F0.wireOp",EDGE,"E2148"),sQuery(id+"F0.wireOp",EDGE,"E2149"),sQuery(id+"F0.wireOp",EDGE,"E2150"),sQuery(id+"F0.wireOp",EDGE,"E2151"),sQuery(id+"F0.wireOp",EDGE,"E2152")])],"isStart":false});
            var sketch = newSketch(context, id + "F2", { "sketchPlane" : qUnion([Q0])});
            skCircle(sketch, "E2154", {"center": v(-1.05, 0) * mm, "radius": 2.65 * mm});
            skCircle(sketch, "E2155", {"center": v(-1.05, 0) * mm, "radius": 5.5 * mm});
            skCircle(sketch, "E2156", {"center": v(-1.05, 0) * mm, "radius": 21.25 * mm});
            skCircle(sketch, "E2157", {"center": v(-1.05, 0) * mm, "radius": 19.75 * mm});
            skSolve(sketch);
        }
        {
            var Q0;
            Q0=makeQuery(id+"F2.imprint","IMPRINT",FACE,{"disambiguationData":[TD([[makeQuery(id+"F2.imprint","IMPRINT",EDGE,{"derivedFrom":sQuery(id+"F2.wireOp",EDGE,"E2154")}),-1.0]])]});
            extrude(context, id + "F3", {"entities" : qUnion([Q0]), "operationType" : NewBodyOperationType.ADD, "depth" : 1 * mm});
        }
        {
            var Q0;
            Q0=makeQuery(id+"F2.imprint","IMPRINT",FACE,{"disambiguationData":[TD([[makeQuery(id+"F2.imprint","IMPRINT",EDGE,{"derivedFrom":sQuery(id+"F2.wireOp",EDGE,"E2156")}),1.0]])]});
            extrude(context, id + "F4", {"entities" : qUnion([Q0]), "operationType" : NewBodyOperationType.ADD, "depth" : 0.5 * mm});
        }
        {
            var Q0;
            Q0=makeQuery(id+"F3.opExtrude","CAP_EDGE",EDGE,{"disambiguationData":[OSD([sQuery(id+"F2.wireOp",EDGE,"E2155")])],"isStart":false});
            var Q1;
            Q1=makeQuery(id+"F4.opExtrude","CAP_EDGE",EDGE,{"disambiguationData":[OSD([sQuery(id+"F2.wireOp",EDGE,"E2157")])],"isStart":false});
            var Q2;
            Q2=makeQuery(id+"F4.opExtrude","CAP_EDGE",EDGE,{"disambiguationData":[OSD([sQuery(id+"F2.wireOp",EDGE,"E2156")])],"isStart":false});
            fillet(context, id + "F5", {"entities" : qUnion([Q0, Q1, Q2]), "radius" : 0.4 * mm, "tangentPropagation" : true, "allowEdgeOverflow" : false});
        }
    });
